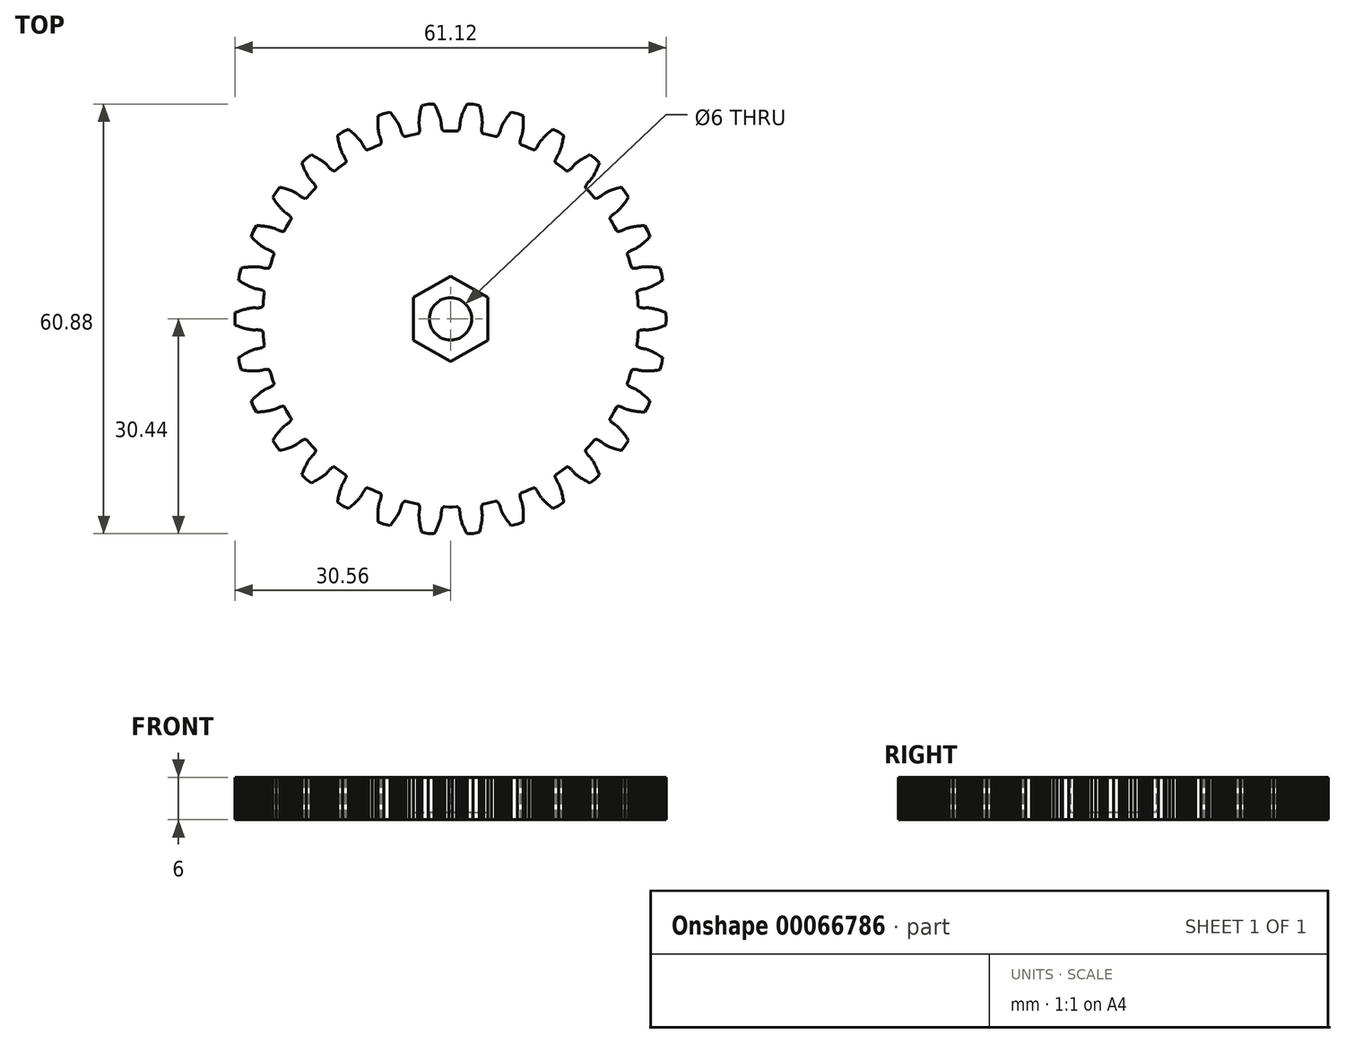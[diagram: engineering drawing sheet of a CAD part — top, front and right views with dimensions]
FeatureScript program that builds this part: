
annotation { "Feature Type Name" : "Feature", "Feature Type Description" : "" }
export const myFeature = defineFeature(function(context is Context, id is Id, definition is map)
    precondition{}
    {
        {
            var Q0;
            Q0=qCreatedBy(makeId("Top.planeOp"),FACE);
            var sketch = newSketch(context, id + "F0", { "sketchPlane" : qUnion([Q0])});
            skCircle(sketch, "E0", {"center": v(0, 0) * mm, "radius": 3 * mm});
            skLineSegment(sketch, "E1", {"start": v(29.66, -7.2) * mm, "end": v(29.89, -6.35) * mm});
            skLineSegment(sketch, "E2", {"start": v(29.89, -6.35) * mm, "end": v(30.03, -5.49) * mm});
            skLineSegment(sketch, "E3", {"start": v(30.03, -5.49) * mm, "end": v(29.86, -5.37) * mm});
            skLineSegment(sketch, "E4", {"start": v(29.86, -5.37) * mm, "end": v(29.65, -5.24) * mm});
            skLineSegment(sketch, "E5", {"start": v(29.65, -5.24) * mm, "end": v(29.45, -5.11) * mm});
            skLineSegment(sketch, "E6", {"start": v(29.45, -5.11) * mm, "end": v(29.26, -5) * mm});
            skLineSegment(sketch, "E7", {"start": v(29.26, -5) * mm, "end": v(29.07, -4.9) * mm});
            skLineSegment(sketch, "E8", {"start": v(29.07, -4.9) * mm, "end": v(28.9, -4.8) * mm});
            skLineSegment(sketch, "E9", {"start": v(28.9, -4.8) * mm, "end": v(28.73, -4.71) * mm});
            skLineSegment(sketch, "E10", {"start": v(28.73, -4.71) * mm, "end": v(28.57, -4.63) * mm});
            skLineSegment(sketch, "E11", {"start": v(28.57, -4.63) * mm, "end": v(28.42, -4.57) * mm});
            skLineSegment(sketch, "E12", {"start": v(28.42, -4.57) * mm, "end": v(28.29, -4.5) * mm});
            skLineSegment(sketch, "E13", {"start": v(28.29, -4.5) * mm, "end": v(28.16, -4.45) * mm});
            skLineSegment(sketch, "E14", {"start": v(28.16, -4.45) * mm, "end": v(28.04, -4.4) * mm});
            skLineSegment(sketch, "E15", {"start": v(28.04, -4.4) * mm, "end": v(27.93, -4.37) * mm});
            skLineSegment(sketch, "E16", {"start": v(27.93, -4.37) * mm, "end": v(27.83, -4.33) * mm});
            skLineSegment(sketch, "E17", {"start": v(27.83, -4.33) * mm, "end": v(27.75, -4.3) * mm});
            skLineSegment(sketch, "E18", {"start": v(27.75, -4.3) * mm, "end": v(27.67, -4.28) * mm});
            skLineSegment(sketch, "E19", {"start": v(27.67, -4.28) * mm, "end": v(27.6, -4.27) * mm});
            skLineSegment(sketch, "E20", {"start": v(27.6, -4.27) * mm, "end": v(27.56, -4.25) * mm});
            skLineSegment(sketch, "E21", {"start": v(27.56, -4.25) * mm, "end": v(27.52, -4.24) * mm});
            skLineSegment(sketch, "E22", {"start": v(27.52, -4.24) * mm, "end": v(27.49, -4.24) * mm});
            skLineSegment(sketch, "E23", {"start": v(27.49, -4.24) * mm, "end": v(27.47, -4.23) * mm});
            skLineSegment(sketch, "E24", {"start": v(27.47, -4.23) * mm, "end": v(27.47, -4.23) * mm});
            skLineSegment(sketch, "E25", {"start": v(27.47, -4.23) * mm, "end": v(27.38, -4.22) * mm});
            skLineSegment(sketch, "E26", {"start": v(27.38, -4.22) * mm, "end": v(27.23, -4.2) * mm});
            skLineSegment(sketch, "E27", {"start": v(27.23, -4.2) * mm, "end": v(27.08, -4.17) * mm});
            skLineSegment(sketch, "E28", {"start": v(27.08, -4.17) * mm, "end": v(26.95, -4.14) * mm});
            skLineSegment(sketch, "E29", {"start": v(26.95, -4.14) * mm, "end": v(26.83, -4.1) * mm});
            skLineSegment(sketch, "E30", {"start": v(26.83, -4.1) * mm, "end": v(26.73, -4.06) * mm});
            skLineSegment(sketch, "E31", {"start": v(26.73, -4.06) * mm, "end": v(26.64, -4.02) * mm});
            skLineSegment(sketch, "E32", {"start": v(26.64, -4.02) * mm, "end": v(26.56, -3.98) * mm});
            skLineSegment(sketch, "E33", {"start": v(26.56, -3.98) * mm, "end": v(26.5, -3.94) * mm});
            skLineSegment(sketch, "E34", {"start": v(26.5, -3.94) * mm, "end": v(26.45, -3.9) * mm});
            skLineSegment(sketch, "E35", {"start": v(26.45, -3.9) * mm, "end": v(26.4, -3.85) * mm});
            skLineSegment(sketch, "E36", {"start": v(26.4, -3.85) * mm, "end": v(26.39, -3.8) * mm});
            skLineSegment(sketch, "E37", {"start": v(26.39, -3.8) * mm, "end": v(26.38, -3.76) * mm});
            skLineSegment(sketch, "E38", {"start": v(26.38, -3.76) * mm, "end": v(26.38, -3.72) * mm});
            skLineSegment(sketch, "E39", {"start": v(26.38, -3.72) * mm, "end": v(26.4, -3.62) * mm});
            skLineSegment(sketch, "E40", {"start": v(26.4, -3.62) * mm, "end": v(26.46, -3.06) * mm});
            skLineSegment(sketch, "E41", {"start": v(26.46, -3.06) * mm, "end": v(26.52, -2.5) * mm});
            skLineSegment(sketch, "E42", {"start": v(26.52, -2.5) * mm, "end": v(26.57, -1.95) * mm});
            skLineSegment(sketch, "E43", {"start": v(26.57, -1.95) * mm, "end": v(26.57, -1.85) * mm});
            skLineSegment(sketch, "E44", {"start": v(26.57, -1.85) * mm, "end": v(26.58, -1.8) * mm});
            skLineSegment(sketch, "E45", {"start": v(26.58, -1.8) * mm, "end": v(26.6, -1.77) * mm});
            skLineSegment(sketch, "E46", {"start": v(26.6, -1.77) * mm, "end": v(26.63, -1.73) * mm});
            skLineSegment(sketch, "E47", {"start": v(26.63, -1.73) * mm, "end": v(26.68, -1.7) * mm});
            skLineSegment(sketch, "E48", {"start": v(26.68, -1.7) * mm, "end": v(26.74, -1.66) * mm});
            skLineSegment(sketch, "E49", {"start": v(26.74, -1.66) * mm, "end": v(26.8, -1.63) * mm});
            skLineSegment(sketch, "E50", {"start": v(26.8, -1.63) * mm, "end": v(26.9, -1.6) * mm});
            skLineSegment(sketch, "E51", {"start": v(26.9, -1.6) * mm, "end": v(26.99, -1.58) * mm});
            skLineSegment(sketch, "E52", {"start": v(26.99, -1.58) * mm, "end": v(27.1, -1.57) * mm});
            skLineSegment(sketch, "E53", {"start": v(27.1, -1.57) * mm, "end": v(27.22, -1.56) * mm});
            skLineSegment(sketch, "E54", {"start": v(27.22, -1.56) * mm, "end": v(27.36, -1.55) * mm});
            skLineSegment(sketch, "E55", {"start": v(27.36, -1.55) * mm, "end": v(27.5, -1.55) * mm});
            skLineSegment(sketch, "E56", {"start": v(27.5, -1.55) * mm, "end": v(27.66, -1.56) * mm});
            skLineSegment(sketch, "E57", {"start": v(27.66, -1.56) * mm, "end": v(27.75, -1.57) * mm});
            skLineSegment(sketch, "E58", {"start": v(27.75, -1.57) * mm, "end": v(27.75, -1.57) * mm});
            skLineSegment(sketch, "E59", {"start": v(27.75, -1.57) * mm, "end": v(27.77, -1.57) * mm});
            skLineSegment(sketch, "E60", {"start": v(27.77, -1.57) * mm, "end": v(27.8, -1.57) * mm});
            skLineSegment(sketch, "E61", {"start": v(27.8, -1.57) * mm, "end": v(27.84, -1.57) * mm});
            skLineSegment(sketch, "E62", {"start": v(27.84, -1.57) * mm, "end": v(27.9, -1.57) * mm});
            skLineSegment(sketch, "E63", {"start": v(27.9, -1.57) * mm, "end": v(27.96, -1.56) * mm});
            skLineSegment(sketch, "E64", {"start": v(27.96, -1.56) * mm, "end": v(28.04, -1.56) * mm});
            skLineSegment(sketch, "E65", {"start": v(28.04, -1.56) * mm, "end": v(28.13, -1.55) * mm});
            skLineSegment(sketch, "E66", {"start": v(28.13, -1.55) * mm, "end": v(28.23, -1.54) * mm});
            skLineSegment(sketch, "E67", {"start": v(28.23, -1.54) * mm, "end": v(28.34, -1.52) * mm});
            skLineSegment(sketch, "E68", {"start": v(28.34, -1.52) * mm, "end": v(28.47, -1.5) * mm});
            skLineSegment(sketch, "E69", {"start": v(28.47, -1.5) * mm, "end": v(28.6, -1.48) * mm});
            skLineSegment(sketch, "E70", {"start": v(28.6, -1.48) * mm, "end": v(28.75, -1.44) * mm});
            skLineSegment(sketch, "E71", {"start": v(28.75, -1.44) * mm, "end": v(28.91, -1.4) * mm});
            skLineSegment(sketch, "E72", {"start": v(28.91, -1.4) * mm, "end": v(29.08, -1.37) * mm});
            skLineSegment(sketch, "E73", {"start": v(29.08, -1.37) * mm, "end": v(29.26, -1.32) * mm});
            skLineSegment(sketch, "E74", {"start": v(29.26, -1.32) * mm, "end": v(29.46, -1.26) * mm});
            skLineSegment(sketch, "E75", {"start": v(29.46, -1.26) * mm, "end": v(29.66, -1.2) * mm});
            skLineSegment(sketch, "E76", {"start": v(29.66, -1.2) * mm, "end": v(29.87, -1.12) * mm});
            skLineSegment(sketch, "E77", {"start": v(29.87, -1.12) * mm, "end": v(30.1, -1.04) * mm});
            skLineSegment(sketch, "E78", {"start": v(30.1, -1.04) * mm, "end": v(30.32, -0.95) * mm});
            skLineSegment(sketch, "E79", {"start": v(30.32, -0.95) * mm, "end": v(30.51, -0.87) * mm});
            skLineSegment(sketch, "E80", {"start": v(30.51, -0.87) * mm, "end": v(30.56, 0) * mm});
            skLineSegment(sketch, "E81", {"start": v(30.56, 0) * mm, "end": v(30.51, 0.87) * mm});
            skLineSegment(sketch, "E82", {"start": v(30.51, 0.87) * mm, "end": v(30.32, 0.95) * mm});
            skLineSegment(sketch, "E83", {"start": v(30.32, 0.95) * mm, "end": v(30.1, 1.04) * mm});
            skLineSegment(sketch, "E84", {"start": v(30.1, 1.04) * mm, "end": v(29.87, 1.12) * mm});
            skLineSegment(sketch, "E85", {"start": v(29.87, 1.12) * mm, "end": v(29.66, 1.2) * mm});
            skLineSegment(sketch, "E86", {"start": v(29.66, 1.2) * mm, "end": v(29.46, 1.26) * mm});
            skLineSegment(sketch, "E87", {"start": v(29.46, 1.26) * mm, "end": v(29.26, 1.32) * mm});
            skLineSegment(sketch, "E88", {"start": v(29.26, 1.32) * mm, "end": v(29.08, 1.37) * mm});
            skLineSegment(sketch, "E89", {"start": v(29.08, 1.37) * mm, "end": v(28.91, 1.4) * mm});
            skLineSegment(sketch, "E90", {"start": v(28.91, 1.4) * mm, "end": v(28.75, 1.44) * mm});
            skLineSegment(sketch, "E91", {"start": v(28.75, 1.44) * mm, "end": v(28.6, 1.48) * mm});
            skLineSegment(sketch, "E92", {"start": v(28.6, 1.48) * mm, "end": v(28.47, 1.5) * mm});
            skLineSegment(sketch, "E93", {"start": v(28.47, 1.5) * mm, "end": v(28.34, 1.52) * mm});
            skLineSegment(sketch, "E94", {"start": v(28.34, 1.52) * mm, "end": v(28.23, 1.54) * mm});
            skLineSegment(sketch, "E95", {"start": v(28.23, 1.54) * mm, "end": v(28.13, 1.55) * mm});
            skLineSegment(sketch, "E96", {"start": v(28.13, 1.55) * mm, "end": v(28.04, 1.56) * mm});
            skLineSegment(sketch, "E97", {"start": v(28.04, 1.56) * mm, "end": v(27.96, 1.56) * mm});
            skLineSegment(sketch, "E98", {"start": v(27.96, 1.56) * mm, "end": v(27.9, 1.57) * mm});
            skLineSegment(sketch, "E99", {"start": v(27.9, 1.57) * mm, "end": v(27.84, 1.57) * mm});
            skLineSegment(sketch, "E100", {"start": v(27.84, 1.57) * mm, "end": v(27.8, 1.57) * mm});
            skLineSegment(sketch, "E101", {"start": v(27.8, 1.57) * mm, "end": v(27.77, 1.57) * mm});
            skLineSegment(sketch, "E102", {"start": v(27.77, 1.57) * mm, "end": v(27.75, 1.57) * mm});
            skLineSegment(sketch, "E103", {"start": v(27.75, 1.57) * mm, "end": v(27.75, 1.57) * mm});
            skLineSegment(sketch, "E104", {"start": v(27.75, 1.57) * mm, "end": v(27.66, 1.56) * mm});
            skLineSegment(sketch, "E105", {"start": v(27.66, 1.56) * mm, "end": v(27.5, 1.55) * mm});
            skLineSegment(sketch, "E106", {"start": v(27.5, 1.55) * mm, "end": v(27.36, 1.55) * mm});
            skLineSegment(sketch, "E107", {"start": v(27.36, 1.55) * mm, "end": v(27.22, 1.56) * mm});
            skLineSegment(sketch, "E108", {"start": v(27.22, 1.56) * mm, "end": v(27.1, 1.57) * mm});
            skLineSegment(sketch, "E109", {"start": v(27.1, 1.57) * mm, "end": v(26.99, 1.58) * mm});
            skLineSegment(sketch, "E110", {"start": v(26.99, 1.58) * mm, "end": v(26.9, 1.6) * mm});
            skLineSegment(sketch, "E111", {"start": v(26.9, 1.6) * mm, "end": v(26.8, 1.63) * mm});
            skLineSegment(sketch, "E112", {"start": v(26.8, 1.63) * mm, "end": v(26.74, 1.66) * mm});
            skLineSegment(sketch, "E113", {"start": v(26.74, 1.66) * mm, "end": v(26.68, 1.7) * mm});
            skLineSegment(sketch, "E114", {"start": v(26.68, 1.7) * mm, "end": v(26.63, 1.73) * mm});
            skLineSegment(sketch, "E115", {"start": v(26.63, 1.73) * mm, "end": v(26.6, 1.77) * mm});
            skLineSegment(sketch, "E116", {"start": v(26.6, 1.77) * mm, "end": v(26.58, 1.8) * mm});
            skLineSegment(sketch, "E117", {"start": v(26.58, 1.8) * mm, "end": v(26.57, 1.85) * mm});
            skLineSegment(sketch, "E118", {"start": v(26.57, 1.85) * mm, "end": v(26.57, 1.95) * mm});
            skLineSegment(sketch, "E119", {"start": v(26.57, 1.95) * mm, "end": v(26.52, 2.5) * mm});
            skLineSegment(sketch, "E120", {"start": v(26.52, 2.5) * mm, "end": v(26.46, 3.06) * mm});
            skLineSegment(sketch, "E121", {"start": v(26.46, 3.06) * mm, "end": v(26.4, 3.62) * mm});
            skLineSegment(sketch, "E122", {"start": v(26.4, 3.62) * mm, "end": v(26.38, 3.72) * mm});
            skLineSegment(sketch, "E123", {"start": v(26.38, 3.72) * mm, "end": v(26.38, 3.76) * mm});
            skLineSegment(sketch, "E124", {"start": v(26.38, 3.76) * mm, "end": v(26.39, 3.8) * mm});
            skLineSegment(sketch, "E125", {"start": v(26.39, 3.8) * mm, "end": v(26.4, 3.85) * mm});
            skLineSegment(sketch, "E126", {"start": v(26.4, 3.85) * mm, "end": v(26.45, 3.9) * mm});
            skLineSegment(sketch, "E127", {"start": v(26.45, 3.9) * mm, "end": v(26.5, 3.94) * mm});
            skLineSegment(sketch, "E128", {"start": v(26.5, 3.94) * mm, "end": v(26.56, 3.98) * mm});
            skLineSegment(sketch, "E129", {"start": v(26.56, 3.98) * mm, "end": v(26.64, 4.02) * mm});
            skLineSegment(sketch, "E130", {"start": v(26.64, 4.02) * mm, "end": v(26.73, 4.06) * mm});
            skLineSegment(sketch, "E131", {"start": v(26.73, 4.06) * mm, "end": v(26.83, 4.1) * mm});
            skLineSegment(sketch, "E132", {"start": v(26.83, 4.1) * mm, "end": v(26.95, 4.14) * mm});
            skLineSegment(sketch, "E133", {"start": v(26.95, 4.14) * mm, "end": v(27.08, 4.17) * mm});
            skLineSegment(sketch, "E134", {"start": v(27.08, 4.17) * mm, "end": v(27.23, 4.2) * mm});
            skLineSegment(sketch, "E135", {"start": v(27.23, 4.2) * mm, "end": v(27.38, 4.22) * mm});
            skLineSegment(sketch, "E136", {"start": v(27.38, 4.22) * mm, "end": v(27.47, 4.23) * mm});
            skLineSegment(sketch, "E137", {"start": v(27.47, 4.23) * mm, "end": v(27.47, 4.23) * mm});
            skLineSegment(sketch, "E138", {"start": v(27.47, 4.23) * mm, "end": v(27.49, 4.24) * mm});
            skLineSegment(sketch, "E139", {"start": v(27.49, 4.24) * mm, "end": v(27.52, 4.24) * mm});
            skLineSegment(sketch, "E140", {"start": v(27.52, 4.24) * mm, "end": v(27.56, 4.25) * mm});
            skLineSegment(sketch, "E141", {"start": v(27.56, 4.25) * mm, "end": v(27.6, 4.27) * mm});
            skLineSegment(sketch, "E142", {"start": v(27.6, 4.27) * mm, "end": v(27.67, 4.28) * mm});
            skLineSegment(sketch, "E143", {"start": v(27.67, 4.28) * mm, "end": v(27.75, 4.3) * mm});
            skLineSegment(sketch, "E144", {"start": v(27.75, 4.3) * mm, "end": v(27.83, 4.33) * mm});
            skLineSegment(sketch, "E145", {"start": v(27.83, 4.33) * mm, "end": v(27.93, 4.37) * mm});
            skLineSegment(sketch, "E146", {"start": v(27.93, 4.37) * mm, "end": v(28.04, 4.4) * mm});
            skLineSegment(sketch, "E147", {"start": v(28.04, 4.4) * mm, "end": v(28.16, 4.45) * mm});
            skLineSegment(sketch, "E148", {"start": v(28.16, 4.45) * mm, "end": v(28.29, 4.5) * mm});
            skLineSegment(sketch, "E149", {"start": v(28.29, 4.5) * mm, "end": v(28.42, 4.57) * mm});
            skLineSegment(sketch, "E150", {"start": v(28.42, 4.57) * mm, "end": v(28.57, 4.63) * mm});
            skLineSegment(sketch, "E151", {"start": v(28.57, 4.63) * mm, "end": v(28.73, 4.71) * mm});
            skLineSegment(sketch, "E152", {"start": v(28.73, 4.71) * mm, "end": v(28.9, 4.8) * mm});
            skLineSegment(sketch, "E153", {"start": v(28.9, 4.8) * mm, "end": v(29.07, 4.9) * mm});
            skLineSegment(sketch, "E154", {"start": v(29.07, 4.9) * mm, "end": v(29.26, 5) * mm});
            skLineSegment(sketch, "E155", {"start": v(29.26, 5) * mm, "end": v(29.45, 5.11) * mm});
            skLineSegment(sketch, "E156", {"start": v(29.45, 5.11) * mm, "end": v(29.65, 5.24) * mm});
            skLineSegment(sketch, "E157", {"start": v(29.65, 5.24) * mm, "end": v(29.86, 5.37) * mm});
            skLineSegment(sketch, "E158", {"start": v(29.86, 5.37) * mm, "end": v(30.03, 5.49) * mm});
            skLineSegment(sketch, "E159", {"start": v(30.03, 5.49) * mm, "end": v(29.89, 6.35) * mm});
            skLineSegment(sketch, "E160", {"start": v(29.89, 6.35) * mm, "end": v(29.66, 7.2) * mm});
            skLineSegment(sketch, "E161", {"start": v(29.66, 7.2) * mm, "end": v(29.46, 7.23) * mm});
            skLineSegment(sketch, "E162", {"start": v(29.46, 7.23) * mm, "end": v(29.22, 7.28) * mm});
            skLineSegment(sketch, "E163", {"start": v(29.22, 7.28) * mm, "end": v(28.98, 7.3) * mm});
            skLineSegment(sketch, "E164", {"start": v(28.98, 7.3) * mm, "end": v(28.76, 7.33) * mm});
            skLineSegment(sketch, "E165", {"start": v(28.76, 7.33) * mm, "end": v(28.55, 7.36) * mm});
            skLineSegment(sketch, "E166", {"start": v(28.55, 7.36) * mm, "end": v(28.35, 7.37) * mm});
            skLineSegment(sketch, "E167", {"start": v(28.35, 7.37) * mm, "end": v(28.16, 7.38) * mm});
            skLineSegment(sketch, "E168", {"start": v(28.16, 7.38) * mm, "end": v(27.99, 7.39) * mm});
            skLineSegment(sketch, "E169", {"start": v(27.99, 7.39) * mm, "end": v(27.82, 7.4) * mm});
            skLineSegment(sketch, "E170", {"start": v(27.82, 7.4) * mm, "end": v(27.67, 7.39) * mm});
            skLineSegment(sketch, "E171", {"start": v(27.67, 7.39) * mm, "end": v(27.53, 7.39) * mm});
            skLineSegment(sketch, "E172", {"start": v(27.53, 7.39) * mm, "end": v(27.4, 7.38) * mm});
            skLineSegment(sketch, "E173", {"start": v(27.4, 7.38) * mm, "end": v(27.3, 7.37) * mm});
            skLineSegment(sketch, "E174", {"start": v(27.3, 7.37) * mm, "end": v(27.2, 7.36) * mm});
            skLineSegment(sketch, "E175", {"start": v(27.2, 7.36) * mm, "end": v(27.1, 7.35) * mm});
            skLineSegment(sketch, "E176", {"start": v(27.1, 7.35) * mm, "end": v(27.02, 7.34) * mm});
            skLineSegment(sketch, "E177", {"start": v(27.02, 7.34) * mm, "end": v(26.96, 7.33) * mm});
            skLineSegment(sketch, "E178", {"start": v(26.96, 7.33) * mm, "end": v(26.9, 7.32) * mm});
            skLineSegment(sketch, "E179", {"start": v(26.9, 7.32) * mm, "end": v(26.86, 7.32) * mm});
            skLineSegment(sketch, "E180", {"start": v(26.86, 7.32) * mm, "end": v(26.84, 7.3) * mm});
            skLineSegment(sketch, "E181", {"start": v(26.84, 7.3) * mm, "end": v(26.82, 7.3) * mm});
            skLineSegment(sketch, "E182", {"start": v(26.82, 7.3) * mm, "end": v(26.82, 7.3) * mm});
            skLineSegment(sketch, "E183", {"start": v(26.82, 7.3) * mm, "end": v(26.73, 7.28) * mm});
            skLineSegment(sketch, "E184", {"start": v(26.73, 7.28) * mm, "end": v(26.58, 7.24) * mm});
            skLineSegment(sketch, "E185", {"start": v(26.58, 7.24) * mm, "end": v(26.44, 7.2) * mm});
            skLineSegment(sketch, "E186", {"start": v(26.44, 7.2) * mm, "end": v(26.3, 7.18) * mm});
            skLineSegment(sketch, "E187", {"start": v(26.3, 7.18) * mm, "end": v(26.18, 7.17) * mm});
            skLineSegment(sketch, "E188", {"start": v(26.18, 7.17) * mm, "end": v(26.07, 7.16) * mm});
            skLineSegment(sketch, "E189", {"start": v(26.07, 7.16) * mm, "end": v(25.97, 7.16) * mm});
            skLineSegment(sketch, "E190", {"start": v(25.97, 7.16) * mm, "end": v(25.88, 7.17) * mm});
            skLineSegment(sketch, "E191", {"start": v(25.88, 7.17) * mm, "end": v(25.8, 7.18) * mm});
            skLineSegment(sketch, "E192", {"start": v(25.8, 7.18) * mm, "end": v(25.74, 7.2) * mm});
            skLineSegment(sketch, "E193", {"start": v(25.74, 7.2) * mm, "end": v(25.69, 7.23) * mm});
            skLineSegment(sketch, "E194", {"start": v(25.69, 7.23) * mm, "end": v(25.65, 7.26) * mm});
            skLineSegment(sketch, "E195", {"start": v(25.65, 7.26) * mm, "end": v(25.62, 7.3) * mm});
            skLineSegment(sketch, "E196", {"start": v(25.62, 7.3) * mm, "end": v(25.6, 7.33) * mm});
            skLineSegment(sketch, "E197", {"start": v(25.6, 7.33) * mm, "end": v(25.58, 7.43) * mm});
            skLineSegment(sketch, "E198", {"start": v(25.58, 7.43) * mm, "end": v(25.42, 7.97) * mm});
            skLineSegment(sketch, "E199", {"start": v(25.42, 7.97) * mm, "end": v(25.25, 8.5) * mm});
            skLineSegment(sketch, "E200", {"start": v(25.25, 8.5) * mm, "end": v(25.06, 9.02) * mm});
            skLineSegment(sketch, "E201", {"start": v(25.06, 9.02) * mm, "end": v(25.03, 9.12) * mm});
            skLineSegment(sketch, "E202", {"start": v(25.03, 9.12) * mm, "end": v(25.02, 9.16) * mm});
            skLineSegment(sketch, "E203", {"start": v(25.02, 9.16) * mm, "end": v(25.02, 9.2) * mm});
            skLineSegment(sketch, "E204", {"start": v(25.02, 9.2) * mm, "end": v(25.03, 9.25) * mm});
            skLineSegment(sketch, "E205", {"start": v(25.03, 9.25) * mm, "end": v(25.06, 9.3) * mm});
            skLineSegment(sketch, "E206", {"start": v(25.06, 9.3) * mm, "end": v(25.1, 9.36) * mm});
            skLineSegment(sketch, "E207", {"start": v(25.1, 9.36) * mm, "end": v(25.15, 9.41) * mm});
            skLineSegment(sketch, "E208", {"start": v(25.15, 9.41) * mm, "end": v(25.22, 9.47) * mm});
            skLineSegment(sketch, "E209", {"start": v(25.22, 9.47) * mm, "end": v(25.3, 9.53) * mm});
            skLineSegment(sketch, "E210", {"start": v(25.3, 9.53) * mm, "end": v(25.4, 9.6) * mm});
            skLineSegment(sketch, "E211", {"start": v(25.4, 9.6) * mm, "end": v(25.5, 9.65) * mm});
            skLineSegment(sketch, "E212", {"start": v(25.5, 9.65) * mm, "end": v(25.62, 9.71) * mm});
            skLineSegment(sketch, "E213", {"start": v(25.62, 9.71) * mm, "end": v(25.76, 9.77) * mm});
            skLineSegment(sketch, "E214", {"start": v(25.76, 9.77) * mm, "end": v(25.9, 9.82) * mm});
            skLineSegment(sketch, "E215", {"start": v(25.9, 9.82) * mm, "end": v(25.99, 9.85) * mm});
            skLineSegment(sketch, "E216", {"start": v(25.99, 9.85) * mm, "end": v(26, 9.85) * mm});
            skLineSegment(sketch, "E217", {"start": v(26, 9.85) * mm, "end": v(26, 9.86) * mm});
            skLineSegment(sketch, "E218", {"start": v(26, 9.86) * mm, "end": v(26.03, 9.87) * mm});
            skLineSegment(sketch, "E219", {"start": v(26.03, 9.87) * mm, "end": v(26.07, 9.89) * mm});
            skLineSegment(sketch, "E220", {"start": v(26.07, 9.89) * mm, "end": v(26.12, 9.91) * mm});
            skLineSegment(sketch, "E221", {"start": v(26.12, 9.91) * mm, "end": v(26.18, 9.94) * mm});
            skLineSegment(sketch, "E222", {"start": v(26.18, 9.94) * mm, "end": v(26.25, 9.98) * mm});
            skLineSegment(sketch, "E223", {"start": v(26.25, 9.98) * mm, "end": v(26.33, 10.03) * mm});
            skLineSegment(sketch, "E224", {"start": v(26.33, 10.03) * mm, "end": v(26.41, 10.08) * mm});
            skLineSegment(sketch, "E225", {"start": v(26.41, 10.08) * mm, "end": v(26.51, 10.14) * mm});
            skLineSegment(sketch, "E226", {"start": v(26.51, 10.14) * mm, "end": v(26.62, 10.2) * mm});
            skLineSegment(sketch, "E227", {"start": v(26.62, 10.2) * mm, "end": v(26.73, 10.29) * mm});
            skLineSegment(sketch, "E228", {"start": v(26.73, 10.29) * mm, "end": v(26.85, 10.38) * mm});
            skLineSegment(sketch, "E229", {"start": v(26.85, 10.38) * mm, "end": v(26.99, 10.47) * mm});
            skLineSegment(sketch, "E230", {"start": v(26.99, 10.47) * mm, "end": v(27.12, 10.58) * mm});
            skLineSegment(sketch, "E231", {"start": v(27.12, 10.58) * mm, "end": v(27.27, 10.7) * mm});
            skLineSegment(sketch, "E232", {"start": v(27.27, 10.7) * mm, "end": v(27.42, 10.83) * mm});
            skLineSegment(sketch, "E233", {"start": v(27.42, 10.83) * mm, "end": v(27.58, 10.97) * mm});
            skLineSegment(sketch, "E234", {"start": v(27.58, 10.97) * mm, "end": v(27.74, 11.12) * mm});
            skLineSegment(sketch, "E235", {"start": v(27.74, 11.12) * mm, "end": v(27.91, 11.29) * mm});
            skLineSegment(sketch, "E236", {"start": v(27.91, 11.29) * mm, "end": v(28.09, 11.47) * mm});
            skLineSegment(sketch, "E237", {"start": v(28.09, 11.47) * mm, "end": v(28.23, 11.61) * mm});
            skLineSegment(sketch, "E238", {"start": v(28.23, 11.61) * mm, "end": v(27.92, 12.43) * mm});
            skLineSegment(sketch, "E239", {"start": v(27.92, 12.43) * mm, "end": v(27.52, 13.2) * mm});
            skLineSegment(sketch, "E240", {"start": v(27.52, 13.2) * mm, "end": v(27.32, 13.2) * mm});
            skLineSegment(sketch, "E241", {"start": v(27.32, 13.2) * mm, "end": v(27.07, 13.2) * mm});
            skLineSegment(sketch, "E242", {"start": v(27.07, 13.2) * mm, "end": v(26.83, 13.17) * mm});
            skLineSegment(sketch, "E243", {"start": v(26.83, 13.17) * mm, "end": v(26.6, 13.15) * mm});
            skLineSegment(sketch, "E244", {"start": v(26.6, 13.15) * mm, "end": v(26.4, 13.13) * mm});
            skLineSegment(sketch, "E245", {"start": v(26.4, 13.13) * mm, "end": v(26.2, 13.1) * mm});
            skLineSegment(sketch, "E246", {"start": v(26.2, 13.1) * mm, "end": v(26.01, 13.08) * mm});
            skLineSegment(sketch, "E247", {"start": v(26.01, 13.08) * mm, "end": v(25.84, 13.05) * mm});
            skLineSegment(sketch, "E248", {"start": v(25.84, 13.05) * mm, "end": v(25.68, 13.01) * mm});
            skLineSegment(sketch, "E249", {"start": v(25.68, 13.01) * mm, "end": v(25.53, 12.98) * mm});
            skLineSegment(sketch, "E250", {"start": v(25.53, 12.98) * mm, "end": v(25.4, 12.95) * mm});
            skLineSegment(sketch, "E251", {"start": v(25.4, 12.95) * mm, "end": v(25.27, 12.92) * mm});
            skLineSegment(sketch, "E252", {"start": v(25.27, 12.92) * mm, "end": v(25.16, 12.89) * mm});
            skLineSegment(sketch, "E253", {"start": v(25.16, 12.89) * mm, "end": v(25.07, 12.86) * mm});
            skLineSegment(sketch, "E254", {"start": v(25.07, 12.86) * mm, "end": v(24.98, 12.83) * mm});
            skLineSegment(sketch, "E255", {"start": v(24.98, 12.83) * mm, "end": v(24.9, 12.8) * mm});
            skLineSegment(sketch, "E256", {"start": v(24.9, 12.8) * mm, "end": v(24.84, 12.78) * mm});
            skLineSegment(sketch, "E257", {"start": v(24.84, 12.78) * mm, "end": v(24.8, 12.76) * mm});
            skLineSegment(sketch, "E258", {"start": v(24.8, 12.76) * mm, "end": v(24.76, 12.74) * mm});
            skLineSegment(sketch, "E259", {"start": v(24.76, 12.74) * mm, "end": v(24.73, 12.73) * mm});
            skLineSegment(sketch, "E260", {"start": v(24.73, 12.73) * mm, "end": v(24.71, 12.72) * mm});
            skLineSegment(sketch, "E261", {"start": v(24.71, 12.72) * mm, "end": v(24.71, 12.72) * mm});
            skLineSegment(sketch, "E262", {"start": v(24.71, 12.72) * mm, "end": v(24.64, 12.68) * mm});
            skLineSegment(sketch, "E263", {"start": v(24.64, 12.68) * mm, "end": v(24.5, 12.6) * mm});
            skLineSegment(sketch, "E264", {"start": v(24.5, 12.6) * mm, "end": v(24.36, 12.54) * mm});
            skLineSegment(sketch, "E265", {"start": v(24.36, 12.54) * mm, "end": v(24.24, 12.5) * mm});
            skLineSegment(sketch, "E266", {"start": v(24.24, 12.5) * mm, "end": v(24.12, 12.45) * mm});
            skLineSegment(sketch, "E267", {"start": v(24.12, 12.45) * mm, "end": v(24.01, 12.42) * mm});
            skLineSegment(sketch, "E268", {"start": v(24.01, 12.42) * mm, "end": v(23.92, 12.4) * mm});
            skLineSegment(sketch, "E269", {"start": v(23.92, 12.4) * mm, "end": v(23.83, 12.4) * mm});
            skLineSegment(sketch, "E270", {"start": v(23.83, 12.4) * mm, "end": v(23.75, 12.4) * mm});
            skLineSegment(sketch, "E271", {"start": v(23.75, 12.4) * mm, "end": v(23.68, 12.4) * mm});
            skLineSegment(sketch, "E272", {"start": v(23.68, 12.4) * mm, "end": v(23.63, 12.41) * mm});
            skLineSegment(sketch, "E273", {"start": v(23.63, 12.41) * mm, "end": v(23.58, 12.43) * mm});
            skLineSegment(sketch, "E274", {"start": v(23.58, 12.43) * mm, "end": v(23.55, 12.46) * mm});
            skLineSegment(sketch, "E275", {"start": v(23.55, 12.46) * mm, "end": v(23.52, 12.5) * mm});
            skLineSegment(sketch, "E276", {"start": v(23.52, 12.5) * mm, "end": v(23.48, 12.59) * mm});
            skLineSegment(sketch, "E277", {"start": v(23.48, 12.59) * mm, "end": v(23.2, 13.08) * mm});
            skLineSegment(sketch, "E278", {"start": v(23.2, 13.08) * mm, "end": v(22.93, 13.56) * mm});
            skLineSegment(sketch, "E279", {"start": v(22.93, 13.56) * mm, "end": v(22.64, 14.04) * mm});
            skLineSegment(sketch, "E280", {"start": v(22.64, 14.04) * mm, "end": v(22.59, 14.12) * mm});
            skLineSegment(sketch, "E281", {"start": v(22.59, 14.12) * mm, "end": v(22.57, 14.16) * mm});
            skLineSegment(sketch, "E282", {"start": v(22.57, 14.16) * mm, "end": v(22.56, 14.2) * mm});
            skLineSegment(sketch, "E283", {"start": v(22.56, 14.2) * mm, "end": v(22.56, 14.25) * mm});
            skLineSegment(sketch, "E284", {"start": v(22.56, 14.25) * mm, "end": v(22.58, 14.31) * mm});
            skLineSegment(sketch, "E285", {"start": v(22.58, 14.31) * mm, "end": v(22.6, 14.37) * mm});
            skLineSegment(sketch, "E286", {"start": v(22.6, 14.37) * mm, "end": v(22.65, 14.44) * mm});
            skLineSegment(sketch, "E287", {"start": v(22.65, 14.44) * mm, "end": v(22.7, 14.5) * mm});
            skLineSegment(sketch, "E288", {"start": v(22.7, 14.5) * mm, "end": v(22.77, 14.58) * mm});
            skLineSegment(sketch, "E289", {"start": v(22.77, 14.58) * mm, "end": v(22.84, 14.66) * mm});
            skLineSegment(sketch, "E290", {"start": v(22.84, 14.66) * mm, "end": v(22.94, 14.74) * mm});
            skLineSegment(sketch, "E291", {"start": v(22.94, 14.74) * mm, "end": v(23.04, 14.83) * mm});
            skLineSegment(sketch, "E292", {"start": v(23.04, 14.83) * mm, "end": v(23.16, 14.91) * mm});
            skLineSegment(sketch, "E293", {"start": v(23.16, 14.91) * mm, "end": v(23.3, 15) * mm});
            skLineSegment(sketch, "E294", {"start": v(23.3, 15) * mm, "end": v(23.37, 15.04) * mm});
            skLineSegment(sketch, "E295", {"start": v(23.37, 15.04) * mm, "end": v(23.37, 15.04) * mm});
            skLineSegment(sketch, "E296", {"start": v(23.37, 15.04) * mm, "end": v(23.39, 15.05) * mm});
            skLineSegment(sketch, "E297", {"start": v(23.39, 15.05) * mm, "end": v(23.41, 15.07) * mm});
            skLineSegment(sketch, "E298", {"start": v(23.41, 15.07) * mm, "end": v(23.45, 15.1) * mm});
            skLineSegment(sketch, "E299", {"start": v(23.45, 15.1) * mm, "end": v(23.49, 15.13) * mm});
            skLineSegment(sketch, "E300", {"start": v(23.49, 15.13) * mm, "end": v(23.54, 15.17) * mm});
            skLineSegment(sketch, "E301", {"start": v(23.54, 15.17) * mm, "end": v(23.6, 15.22) * mm});
            skLineSegment(sketch, "E302", {"start": v(23.6, 15.22) * mm, "end": v(23.67, 15.28) * mm});
            skLineSegment(sketch, "E303", {"start": v(23.67, 15.28) * mm, "end": v(23.74, 15.35) * mm});
            skLineSegment(sketch, "E304", {"start": v(23.74, 15.35) * mm, "end": v(23.82, 15.43) * mm});
            skLineSegment(sketch, "E305", {"start": v(23.82, 15.43) * mm, "end": v(23.91, 15.52) * mm});
            skLineSegment(sketch, "E306", {"start": v(23.91, 15.52) * mm, "end": v(24, 15.62) * mm});
            skLineSegment(sketch, "E307", {"start": v(24, 15.62) * mm, "end": v(24.11, 15.73) * mm});
            skLineSegment(sketch, "E308", {"start": v(24.11, 15.73) * mm, "end": v(24.22, 15.85) * mm});
            skLineSegment(sketch, "E309", {"start": v(24.22, 15.85) * mm, "end": v(24.33, 15.99) * mm});
            skLineSegment(sketch, "E310", {"start": v(24.33, 15.99) * mm, "end": v(24.45, 16.14) * mm});
            skLineSegment(sketch, "E311", {"start": v(24.45, 16.14) * mm, "end": v(24.57, 16.3) * mm});
            skLineSegment(sketch, "E312", {"start": v(24.57, 16.3) * mm, "end": v(24.7, 16.47) * mm});
            skLineSegment(sketch, "E313", {"start": v(24.7, 16.47) * mm, "end": v(24.83, 16.65) * mm});
            skLineSegment(sketch, "E314", {"start": v(24.83, 16.65) * mm, "end": v(24.96, 16.85) * mm});
            skLineSegment(sketch, "E315", {"start": v(24.96, 16.85) * mm, "end": v(25.1, 17.05) * mm});
            skLineSegment(sketch, "E316", {"start": v(25.1, 17.05) * mm, "end": v(25.2, 17.23) * mm});
            skLineSegment(sketch, "E317", {"start": v(25.2, 17.23) * mm, "end": v(24.72, 17.96) * mm});
            skLineSegment(sketch, "E318", {"start": v(24.72, 17.96) * mm, "end": v(24.17, 18.64) * mm});
            skLineSegment(sketch, "E319", {"start": v(24.17, 18.64) * mm, "end": v(23.97, 18.6) * mm});
            skLineSegment(sketch, "E320", {"start": v(23.97, 18.6) * mm, "end": v(23.73, 18.53) * mm});
            skLineSegment(sketch, "E321", {"start": v(23.73, 18.53) * mm, "end": v(23.5, 18.47) * mm});
            skLineSegment(sketch, "E322", {"start": v(23.5, 18.47) * mm, "end": v(23.3, 18.4) * mm});
            skLineSegment(sketch, "E323", {"start": v(23.3, 18.4) * mm, "end": v(23.09, 18.33) * mm});
            skLineSegment(sketch, "E324", {"start": v(23.09, 18.33) * mm, "end": v(22.9, 18.27) * mm});
            skLineSegment(sketch, "E325", {"start": v(22.9, 18.27) * mm, "end": v(22.73, 18.2) * mm});
            skLineSegment(sketch, "E326", {"start": v(22.73, 18.2) * mm, "end": v(22.56, 18.13) * mm});
            skLineSegment(sketch, "E327", {"start": v(22.56, 18.13) * mm, "end": v(22.41, 18.07) * mm});
            skLineSegment(sketch, "E328", {"start": v(22.41, 18.07) * mm, "end": v(22.27, 18) * mm});
            skLineSegment(sketch, "E329", {"start": v(22.27, 18) * mm, "end": v(22.15, 17.95) * mm});
            skLineSegment(sketch, "E330", {"start": v(22.15, 17.95) * mm, "end": v(22.04, 17.89) * mm});
            skLineSegment(sketch, "E331", {"start": v(22.04, 17.89) * mm, "end": v(21.93, 17.84) * mm});
            skLineSegment(sketch, "E332", {"start": v(21.93, 17.84) * mm, "end": v(21.84, 17.79) * mm});
            skLineSegment(sketch, "E333", {"start": v(21.84, 17.79) * mm, "end": v(21.77, 17.74) * mm});
            skLineSegment(sketch, "E334", {"start": v(21.77, 17.74) * mm, "end": v(21.7, 17.7) * mm});
            skLineSegment(sketch, "E335", {"start": v(21.7, 17.7) * mm, "end": v(21.64, 17.66) * mm});
            skLineSegment(sketch, "E336", {"start": v(21.64, 17.66) * mm, "end": v(21.6, 17.63) * mm});
            skLineSegment(sketch, "E337", {"start": v(21.6, 17.63) * mm, "end": v(21.57, 17.6) * mm});
            skLineSegment(sketch, "E338", {"start": v(21.57, 17.6) * mm, "end": v(21.54, 17.6) * mm});
            skLineSegment(sketch, "E339", {"start": v(21.54, 17.6) * mm, "end": v(21.53, 17.58) * mm});
            skLineSegment(sketch, "E340", {"start": v(21.53, 17.58) * mm, "end": v(21.53, 17.58) * mm});
            skLineSegment(sketch, "E341", {"start": v(21.53, 17.58) * mm, "end": v(21.46, 17.52) * mm});
            skLineSegment(sketch, "E342", {"start": v(21.46, 17.52) * mm, "end": v(21.34, 17.42) * mm});
            skLineSegment(sketch, "E343", {"start": v(21.34, 17.42) * mm, "end": v(21.22, 17.33) * mm});
            skLineSegment(sketch, "E344", {"start": v(21.22, 17.33) * mm, "end": v(21.1, 17.26) * mm});
            skLineSegment(sketch, "E345", {"start": v(21.1, 17.26) * mm, "end": v(21, 17.2) * mm});
            skLineSegment(sketch, "E346", {"start": v(21, 17.2) * mm, "end": v(20.9, 17.14) * mm});
            skLineSegment(sketch, "E347", {"start": v(20.9, 17.14) * mm, "end": v(20.81, 17.1) * mm});
            skLineSegment(sketch, "E348", {"start": v(20.81, 17.1) * mm, "end": v(20.73, 17.08) * mm});
            skLineSegment(sketch, "E349", {"start": v(20.73, 17.08) * mm, "end": v(20.65, 17.06) * mm});
            skLineSegment(sketch, "E350", {"start": v(20.65, 17.06) * mm, "end": v(20.59, 17.05) * mm});
            skLineSegment(sketch, "E351", {"start": v(20.59, 17.05) * mm, "end": v(20.53, 17.05) * mm});
            skLineSegment(sketch, "E352", {"start": v(20.53, 17.05) * mm, "end": v(20.48, 17.06) * mm});
            skLineSegment(sketch, "E353", {"start": v(20.48, 17.06) * mm, "end": v(20.44, 17.09) * mm});
            skLineSegment(sketch, "E354", {"start": v(20.44, 17.09) * mm, "end": v(20.41, 17.12) * mm});
            skLineSegment(sketch, "E355", {"start": v(20.41, 17.12) * mm, "end": v(20.35, 17.2) * mm});
            skLineSegment(sketch, "E356", {"start": v(20.35, 17.2) * mm, "end": v(19.98, 17.62) * mm});
            skLineSegment(sketch, "E357", {"start": v(19.98, 17.62) * mm, "end": v(19.6, 18.03) * mm});
            skLineSegment(sketch, "E358", {"start": v(19.6, 18.03) * mm, "end": v(19.23, 18.44) * mm});
            skLineSegment(sketch, "E359", {"start": v(19.23, 18.44) * mm, "end": v(19.16, 18.51) * mm});
            skLineSegment(sketch, "E360", {"start": v(19.16, 18.51) * mm, "end": v(19.13, 18.54) * mm});
            skLineSegment(sketch, "E361", {"start": v(19.13, 18.54) * mm, "end": v(19.11, 18.58) * mm});
            skLineSegment(sketch, "E362", {"start": v(19.11, 18.58) * mm, "end": v(19.1, 18.63) * mm});
            skLineSegment(sketch, "E363", {"start": v(19.1, 18.63) * mm, "end": v(19.1, 18.7) * mm});
            skLineSegment(sketch, "E364", {"start": v(19.1, 18.7) * mm, "end": v(19.12, 18.76) * mm});
            skLineSegment(sketch, "E365", {"start": v(19.12, 18.76) * mm, "end": v(19.15, 18.83) * mm});
            skLineSegment(sketch, "E366", {"start": v(19.15, 18.83) * mm, "end": v(19.19, 18.91) * mm});
            skLineSegment(sketch, "E367", {"start": v(19.19, 18.91) * mm, "end": v(19.24, 19) * mm});
            skLineSegment(sketch, "E368", {"start": v(19.24, 19) * mm, "end": v(19.3, 19.1) * mm});
            skLineSegment(sketch, "E369", {"start": v(19.3, 19.1) * mm, "end": v(19.37, 19.19) * mm});
            skLineSegment(sketch, "E370", {"start": v(19.37, 19.19) * mm, "end": v(19.46, 19.3) * mm});
            skLineSegment(sketch, "E371", {"start": v(19.46, 19.3) * mm, "end": v(19.56, 19.4) * mm});
            skLineSegment(sketch, "E372", {"start": v(19.56, 19.4) * mm, "end": v(19.67, 19.51) * mm});
            skLineSegment(sketch, "E373", {"start": v(19.67, 19.51) * mm, "end": v(19.73, 19.57) * mm});
            skLineSegment(sketch, "E374", {"start": v(19.73, 19.57) * mm, "end": v(19.74, 19.57) * mm});
            skLineSegment(sketch, "E375", {"start": v(19.74, 19.57) * mm, "end": v(19.75, 19.59) * mm});
            skLineSegment(sketch, "E376", {"start": v(19.75, 19.59) * mm, "end": v(19.77, 19.6) * mm});
            skLineSegment(sketch, "E377", {"start": v(19.77, 19.6) * mm, "end": v(19.8, 19.64) * mm});
            skLineSegment(sketch, "E378", {"start": v(19.8, 19.64) * mm, "end": v(19.83, 19.68) * mm});
            skLineSegment(sketch, "E379", {"start": v(19.83, 19.68) * mm, "end": v(19.87, 19.73) * mm});
            skLineSegment(sketch, "E380", {"start": v(19.87, 19.73) * mm, "end": v(19.92, 19.8) * mm});
            skLineSegment(sketch, "E381", {"start": v(19.92, 19.8) * mm, "end": v(19.97, 19.87) * mm});
            skLineSegment(sketch, "E382", {"start": v(19.97, 19.87) * mm, "end": v(20.03, 19.95) * mm});
            skLineSegment(sketch, "E383", {"start": v(20.03, 19.95) * mm, "end": v(20.1, 20.04) * mm});
            skLineSegment(sketch, "E384", {"start": v(20.1, 20.04) * mm, "end": v(20.16, 20.15) * mm});
            skLineSegment(sketch, "E385", {"start": v(20.16, 20.15) * mm, "end": v(20.24, 20.27) * mm});
            skLineSegment(sketch, "E386", {"start": v(20.24, 20.27) * mm, "end": v(20.31, 20.4) * mm});
            skLineSegment(sketch, "E387", {"start": v(20.31, 20.4) * mm, "end": v(20.4, 20.54) * mm});
            skLineSegment(sketch, "E388", {"start": v(20.4, 20.54) * mm, "end": v(20.47, 20.7) * mm});
            skLineSegment(sketch, "E389", {"start": v(20.47, 20.7) * mm, "end": v(20.56, 20.87) * mm});
            skLineSegment(sketch, "E390", {"start": v(20.56, 20.87) * mm, "end": v(20.65, 21.05) * mm});
            skLineSegment(sketch, "E391", {"start": v(20.65, 21.05) * mm, "end": v(20.73, 21.24) * mm});
            skLineSegment(sketch, "E392", {"start": v(20.73, 21.24) * mm, "end": v(20.82, 21.45) * mm});
            skLineSegment(sketch, "E393", {"start": v(20.82, 21.45) * mm, "end": v(20.9, 21.67) * mm});
            skLineSegment(sketch, "E394", {"start": v(20.9, 21.67) * mm, "end": v(21, 21.9) * mm});
            skLineSegment(sketch, "E395", {"start": v(21, 21.9) * mm, "end": v(21.07, 22.1) * mm});
            skLineSegment(sketch, "E396", {"start": v(21.07, 22.1) * mm, "end": v(20.45, 22.7) * mm});
            skLineSegment(sketch, "E397", {"start": v(20.45, 22.7) * mm, "end": v(19.77, 23.26) * mm});
            skLineSegment(sketch, "E398", {"start": v(19.77, 23.26) * mm, "end": v(19.58, 23.17) * mm});
            skLineSegment(sketch, "E399", {"start": v(19.58, 23.17) * mm, "end": v(19.36, 23.06) * mm});
            skLineSegment(sketch, "E400", {"start": v(19.36, 23.06) * mm, "end": v(19.15, 22.95) * mm});
            skLineSegment(sketch, "E401", {"start": v(19.15, 22.95) * mm, "end": v(18.96, 22.84) * mm});
            skLineSegment(sketch, "E402", {"start": v(18.96, 22.84) * mm, "end": v(18.77, 22.73) * mm});
            skLineSegment(sketch, "E403", {"start": v(18.77, 22.73) * mm, "end": v(18.6, 22.63) * mm});
            skLineSegment(sketch, "E404", {"start": v(18.6, 22.63) * mm, "end": v(18.45, 22.53) * mm});
            skLineSegment(sketch, "E405", {"start": v(18.45, 22.53) * mm, "end": v(18.3, 22.43) * mm});
            skLineSegment(sketch, "E406", {"start": v(18.3, 22.43) * mm, "end": v(18.17, 22.33) * mm});
            skLineSegment(sketch, "E407", {"start": v(18.17, 22.33) * mm, "end": v(18.04, 22.24) * mm});
            skLineSegment(sketch, "E408", {"start": v(18.04, 22.24) * mm, "end": v(17.93, 22.16) * mm});
            skLineSegment(sketch, "E409", {"start": v(17.93, 22.16) * mm, "end": v(17.83, 22.08) * mm});
            skLineSegment(sketch, "E410", {"start": v(17.83, 22.08) * mm, "end": v(17.75, 22) * mm});
            skLineSegment(sketch, "E411", {"start": v(17.75, 22) * mm, "end": v(17.67, 21.94) * mm});
            skLineSegment(sketch, "E412", {"start": v(17.67, 21.94) * mm, "end": v(17.6, 21.88) * mm});
            skLineSegment(sketch, "E413", {"start": v(17.6, 21.88) * mm, "end": v(17.55, 21.82) * mm});
            skLineSegment(sketch, "E414", {"start": v(17.55, 21.82) * mm, "end": v(17.5, 21.78) * mm});
            skLineSegment(sketch, "E415", {"start": v(17.5, 21.78) * mm, "end": v(17.46, 21.74) * mm});
            skLineSegment(sketch, "E416", {"start": v(17.46, 21.74) * mm, "end": v(17.43, 21.7) * mm});
            skLineSegment(sketch, "E417", {"start": v(17.43, 21.7) * mm, "end": v(17.41, 21.69) * mm});
            skLineSegment(sketch, "E418", {"start": v(17.41, 21.69) * mm, "end": v(17.4, 21.67) * mm});
            skLineSegment(sketch, "E419", {"start": v(17.4, 21.67) * mm, "end": v(17.4, 21.67) * mm});
            skLineSegment(sketch, "E420", {"start": v(17.4, 21.67) * mm, "end": v(17.35, 21.6) * mm});
            skLineSegment(sketch, "E421", {"start": v(17.35, 21.6) * mm, "end": v(17.25, 21.48) * mm});
            skLineSegment(sketch, "E422", {"start": v(17.25, 21.48) * mm, "end": v(17.15, 21.37) * mm});
            skLineSegment(sketch, "E423", {"start": v(17.15, 21.37) * mm, "end": v(17.06, 21.27) * mm});
            skLineSegment(sketch, "E424", {"start": v(17.06, 21.27) * mm, "end": v(16.97, 21.19) * mm});
            skLineSegment(sketch, "E425", {"start": v(16.97, 21.19) * mm, "end": v(16.88, 21.12) * mm});
            skLineSegment(sketch, "E426", {"start": v(16.88, 21.12) * mm, "end": v(16.8, 21.06) * mm});
            skLineSegment(sketch, "E427", {"start": v(16.8, 21.06) * mm, "end": v(16.73, 21.01) * mm});
            skLineSegment(sketch, "E428", {"start": v(16.73, 21.01) * mm, "end": v(16.66, 20.98) * mm});
            skLineSegment(sketch, "E429", {"start": v(16.66, 20.98) * mm, "end": v(16.6, 20.96) * mm});
            skLineSegment(sketch, "E430", {"start": v(16.6, 20.96) * mm, "end": v(16.54, 20.95) * mm});
            skLineSegment(sketch, "E431", {"start": v(16.54, 20.95) * mm, "end": v(16.48, 20.95) * mm});
            skLineSegment(sketch, "E432", {"start": v(16.48, 20.95) * mm, "end": v(16.44, 20.96) * mm});
            skLineSegment(sketch, "E433", {"start": v(16.44, 20.96) * mm, "end": v(16.4, 20.99) * mm});
            skLineSegment(sketch, "E434", {"start": v(16.4, 20.99) * mm, "end": v(16.33, 21.05) * mm});
            skLineSegment(sketch, "E435", {"start": v(16.33, 21.05) * mm, "end": v(15.88, 21.39) * mm});
            skLineSegment(sketch, "E436", {"start": v(15.88, 21.39) * mm, "end": v(15.43, 21.71) * mm});
            skLineSegment(sketch, "E437", {"start": v(15.43, 21.71) * mm, "end": v(14.97, 22.03) * mm});
            skLineSegment(sketch, "E438", {"start": v(14.97, 22.03) * mm, "end": v(14.89, 22.09) * mm});
            skLineSegment(sketch, "E439", {"start": v(14.89, 22.09) * mm, "end": v(14.86, 22.11) * mm});
            skLineSegment(sketch, "E440", {"start": v(14.86, 22.11) * mm, "end": v(14.83, 22.15) * mm});
            skLineSegment(sketch, "E441", {"start": v(14.83, 22.15) * mm, "end": v(14.81, 22.2) * mm});
            skLineSegment(sketch, "E442", {"start": v(14.81, 22.2) * mm, "end": v(14.8, 22.26) * mm});
            skLineSegment(sketch, "E443", {"start": v(14.8, 22.26) * mm, "end": v(14.8, 22.32) * mm});
            skLineSegment(sketch, "E444", {"start": v(14.8, 22.32) * mm, "end": v(14.81, 22.4) * mm});
            skLineSegment(sketch, "E445", {"start": v(14.81, 22.4) * mm, "end": v(14.83, 22.49) * mm});
            skLineSegment(sketch, "E446", {"start": v(14.83, 22.49) * mm, "end": v(14.87, 22.58) * mm});
            skLineSegment(sketch, "E447", {"start": v(14.87, 22.58) * mm, "end": v(14.9, 22.69) * mm});
            skLineSegment(sketch, "E448", {"start": v(14.9, 22.69) * mm, "end": v(14.96, 22.8) * mm});
            skLineSegment(sketch, "E449", {"start": v(14.96, 22.8) * mm, "end": v(15.02, 22.92) * mm});
            skLineSegment(sketch, "E450", {"start": v(15.02, 22.92) * mm, "end": v(15.1, 23.04) * mm});
            skLineSegment(sketch, "E451", {"start": v(15.1, 23.04) * mm, "end": v(15.18, 23.18) * mm});
            skLineSegment(sketch, "E452", {"start": v(15.18, 23.18) * mm, "end": v(15.23, 23.25) * mm});
            skLineSegment(sketch, "E453", {"start": v(15.23, 23.25) * mm, "end": v(15.23, 23.25) * mm});
            skLineSegment(sketch, "E454", {"start": v(15.23, 23.25) * mm, "end": v(15.24, 23.26) * mm});
            skLineSegment(sketch, "E455", {"start": v(15.24, 23.26) * mm, "end": v(15.26, 23.29) * mm});
            skLineSegment(sketch, "E456", {"start": v(15.26, 23.29) * mm, "end": v(15.28, 23.32) * mm});
            skLineSegment(sketch, "E457", {"start": v(15.28, 23.32) * mm, "end": v(15.3, 23.37) * mm});
            skLineSegment(sketch, "E458", {"start": v(15.3, 23.37) * mm, "end": v(15.33, 23.43) * mm});
            skLineSegment(sketch, "E459", {"start": v(15.33, 23.43) * mm, "end": v(15.37, 23.5) * mm});
            skLineSegment(sketch, "E460", {"start": v(15.37, 23.5) * mm, "end": v(15.4, 23.58) * mm});
            skLineSegment(sketch, "E461", {"start": v(15.4, 23.58) * mm, "end": v(15.45, 23.68) * mm});
            skLineSegment(sketch, "E462", {"start": v(15.45, 23.68) * mm, "end": v(15.49, 23.78) * mm});
            skLineSegment(sketch, "E463", {"start": v(15.49, 23.78) * mm, "end": v(15.53, 23.9) * mm});
            skLineSegment(sketch, "E464", {"start": v(15.53, 23.9) * mm, "end": v(15.58, 24.03) * mm});
            skLineSegment(sketch, "E465", {"start": v(15.58, 24.03) * mm, "end": v(15.63, 24.18) * mm});
            skLineSegment(sketch, "E466", {"start": v(15.63, 24.18) * mm, "end": v(15.68, 24.33) * mm});
            skLineSegment(sketch, "E467", {"start": v(15.68, 24.33) * mm, "end": v(15.72, 24.5) * mm});
            skLineSegment(sketch, "E468", {"start": v(15.72, 24.5) * mm, "end": v(15.77, 24.69) * mm});
            skLineSegment(sketch, "E469", {"start": v(15.77, 24.69) * mm, "end": v(15.82, 24.88) * mm});
            skLineSegment(sketch, "E470", {"start": v(15.82, 24.88) * mm, "end": v(15.86, 25.09) * mm});
            skLineSegment(sketch, "E471", {"start": v(15.86, 25.09) * mm, "end": v(15.9, 25.3) * mm});
            skLineSegment(sketch, "E472", {"start": v(15.9, 25.3) * mm, "end": v(15.95, 25.54) * mm});
            skLineSegment(sketch, "E473", {"start": v(15.95, 25.54) * mm, "end": v(15.99, 25.79) * mm});
            skLineSegment(sketch, "E474", {"start": v(15.99, 25.79) * mm, "end": v(16.01, 25.99) * mm});
            skLineSegment(sketch, "E475", {"start": v(16.01, 25.99) * mm, "end": v(15.28, 26.46) * mm});
            skLineSegment(sketch, "E476", {"start": v(15.28, 26.46) * mm, "end": v(14.5, 26.86) * mm});
            skLineSegment(sketch, "E477", {"start": v(14.5, 26.86) * mm, "end": v(14.34, 26.74) * mm});
            skLineSegment(sketch, "E478", {"start": v(14.34, 26.74) * mm, "end": v(14.14, 26.58) * mm});
            skLineSegment(sketch, "E479", {"start": v(14.14, 26.58) * mm, "end": v(13.96, 26.43) * mm});
            skLineSegment(sketch, "E480", {"start": v(13.96, 26.43) * mm, "end": v(13.8, 26.28) * mm});
            skLineSegment(sketch, "E481", {"start": v(13.8, 26.28) * mm, "end": v(13.64, 26.14) * mm});
            skLineSegment(sketch, "E482", {"start": v(13.64, 26.14) * mm, "end": v(13.5, 26) * mm});
            skLineSegment(sketch, "E483", {"start": v(13.5, 26) * mm, "end": v(13.36, 25.87) * mm});
            skLineSegment(sketch, "E484", {"start": v(13.36, 25.87) * mm, "end": v(13.24, 25.74) * mm});
            skLineSegment(sketch, "E485", {"start": v(13.24, 25.74) * mm, "end": v(13.13, 25.62) * mm});
            skLineSegment(sketch, "E486", {"start": v(13.13, 25.62) * mm, "end": v(13.02, 25.5) * mm});
            skLineSegment(sketch, "E487", {"start": v(13.02, 25.5) * mm, "end": v(12.93, 25.4) * mm});
            skLineSegment(sketch, "E488", {"start": v(12.93, 25.4) * mm, "end": v(12.85, 25.3) * mm});
            skLineSegment(sketch, "E489", {"start": v(12.85, 25.3) * mm, "end": v(12.78, 25.22) * mm});
            skLineSegment(sketch, "E490", {"start": v(12.78, 25.22) * mm, "end": v(12.72, 25.13) * mm});
            skLineSegment(sketch, "E491", {"start": v(12.72, 25.13) * mm, "end": v(12.67, 25.06) * mm});
            skLineSegment(sketch, "E492", {"start": v(12.67, 25.06) * mm, "end": v(12.63, 25) * mm});
            skLineSegment(sketch, "E493", {"start": v(12.63, 25) * mm, "end": v(12.59, 24.94) * mm});
            skLineSegment(sketch, "E494", {"start": v(12.59, 24.94) * mm, "end": v(12.56, 24.9) * mm});
            skLineSegment(sketch, "E495", {"start": v(12.56, 24.9) * mm, "end": v(12.54, 24.86) * mm});
            skLineSegment(sketch, "E496", {"start": v(12.54, 24.86) * mm, "end": v(12.52, 24.83) * mm});
            skLineSegment(sketch, "E497", {"start": v(12.52, 24.83) * mm, "end": v(12.52, 24.82) * mm});
            skLineSegment(sketch, "E498", {"start": v(12.52, 24.82) * mm, "end": v(12.52, 24.82) * mm});
            skLineSegment(sketch, "E499", {"start": v(12.52, 24.82) * mm, "end": v(12.48, 24.74) * mm});
            skLineSegment(sketch, "E500", {"start": v(12.48, 24.74) * mm, "end": v(12.4, 24.6) * mm});
            skLineSegment(sketch, "E501", {"start": v(12.4, 24.6) * mm, "end": v(12.34, 24.47) * mm});
            skLineSegment(sketch, "E502", {"start": v(12.34, 24.47) * mm, "end": v(12.26, 24.35) * mm});
            skLineSegment(sketch, "E503", {"start": v(12.26, 24.35) * mm, "end": v(12.2, 24.25) * mm});
            skLineSegment(sketch, "E504", {"start": v(12.2, 24.25) * mm, "end": v(12.12, 24.17) * mm});
            skLineSegment(sketch, "E505", {"start": v(12.12, 24.17) * mm, "end": v(12.06, 24.1) * mm});
            skLineSegment(sketch, "E506", {"start": v(12.06, 24.1) * mm, "end": v(12, 24.03) * mm});
            skLineSegment(sketch, "E507", {"start": v(12, 24.03) * mm, "end": v(11.93, 23.98) * mm});
            skLineSegment(sketch, "E508", {"start": v(11.93, 23.98) * mm, "end": v(11.87, 23.95) * mm});
            skLineSegment(sketch, "E509", {"start": v(11.87, 23.95) * mm, "end": v(11.82, 23.93) * mm});
            skLineSegment(sketch, "E510", {"start": v(11.82, 23.93) * mm, "end": v(11.77, 23.92) * mm});
            skLineSegment(sketch, "E511", {"start": v(11.77, 23.92) * mm, "end": v(11.72, 23.92) * mm});
            skLineSegment(sketch, "E512", {"start": v(11.72, 23.92) * mm, "end": v(11.69, 23.94) * mm});
            skLineSegment(sketch, "E513", {"start": v(11.69, 23.94) * mm, "end": v(11.6, 23.98) * mm});
            skLineSegment(sketch, "E514", {"start": v(11.6, 23.98) * mm, "end": v(11.09, 24.22) * mm});
            skLineSegment(sketch, "E515", {"start": v(11.09, 24.22) * mm, "end": v(10.58, 24.45) * mm});
            skLineSegment(sketch, "E516", {"start": v(10.58, 24.45) * mm, "end": v(10.07, 24.66) * mm});
            skLineSegment(sketch, "E517", {"start": v(10.07, 24.66) * mm, "end": v(9.97, 24.7) * mm});
            skLineSegment(sketch, "E518", {"start": v(9.97, 24.7) * mm, "end": v(9.93, 24.72) * mm});
            skLineSegment(sketch, "E519", {"start": v(9.93, 24.72) * mm, "end": v(9.9, 24.75) * mm});
            skLineSegment(sketch, "E520", {"start": v(9.9, 24.75) * mm, "end": v(9.87, 24.8) * mm});
            skLineSegment(sketch, "E521", {"start": v(9.87, 24.8) * mm, "end": v(9.85, 24.85) * mm});
            skLineSegment(sketch, "E522", {"start": v(9.85, 24.85) * mm, "end": v(9.84, 24.91) * mm});
            skLineSegment(sketch, "E523", {"start": v(9.84, 24.91) * mm, "end": v(9.83, 25) * mm});
            skLineSegment(sketch, "E524", {"start": v(9.83, 25) * mm, "end": v(9.84, 25.08) * mm});
            skLineSegment(sketch, "E525", {"start": v(9.84, 25.08) * mm, "end": v(9.85, 25.18) * mm});
            skLineSegment(sketch, "E526", {"start": v(9.85, 25.18) * mm, "end": v(9.86, 25.29) * mm});
            skLineSegment(sketch, "E527", {"start": v(9.86, 25.29) * mm, "end": v(9.9, 25.4) * mm});
            skLineSegment(sketch, "E528", {"start": v(9.9, 25.4) * mm, "end": v(9.93, 25.54) * mm});
            skLineSegment(sketch, "E529", {"start": v(9.93, 25.54) * mm, "end": v(9.98, 25.68) * mm});
            skLineSegment(sketch, "E530", {"start": v(9.98, 25.68) * mm, "end": v(10.03, 25.83) * mm});
            skLineSegment(sketch, "E531", {"start": v(10.03, 25.83) * mm, "end": v(10.07, 25.9) * mm});
            skLineSegment(sketch, "E532", {"start": v(10.07, 25.9) * mm, "end": v(10.07, 25.9) * mm});
            skLineSegment(sketch, "E533", {"start": v(10.07, 25.9) * mm, "end": v(10.07, 25.92) * mm});
            skLineSegment(sketch, "E534", {"start": v(10.07, 25.92) * mm, "end": v(10.08, 25.95) * mm});
            skLineSegment(sketch, "E535", {"start": v(10.08, 25.95) * mm, "end": v(10.1, 26) * mm});
            skLineSegment(sketch, "E536", {"start": v(10.1, 26) * mm, "end": v(10.11, 26.04) * mm});
            skLineSegment(sketch, "E537", {"start": v(10.11, 26.04) * mm, "end": v(10.13, 26.1) * mm});
            skLineSegment(sketch, "E538", {"start": v(10.13, 26.1) * mm, "end": v(10.15, 26.18) * mm});
            skLineSegment(sketch, "E539", {"start": v(10.15, 26.18) * mm, "end": v(10.16, 26.27) * mm});
            skLineSegment(sketch, "E540", {"start": v(10.16, 26.27) * mm, "end": v(10.18, 26.37) * mm});
            skLineSegment(sketch, "E541", {"start": v(10.18, 26.37) * mm, "end": v(10.2, 26.49) * mm});
            skLineSegment(sketch, "E542", {"start": v(10.2, 26.49) * mm, "end": v(10.22, 26.61) * mm});
            skLineSegment(sketch, "E543", {"start": v(10.22, 26.61) * mm, "end": v(10.24, 26.75) * mm});
            skLineSegment(sketch, "E544", {"start": v(10.24, 26.75) * mm, "end": v(10.26, 26.9) * mm});
            skLineSegment(sketch, "E545", {"start": v(10.26, 26.9) * mm, "end": v(10.27, 27.06) * mm});
            skLineSegment(sketch, "E546", {"start": v(10.27, 27.06) * mm, "end": v(10.29, 27.24) * mm});
            skLineSegment(sketch, "E547", {"start": v(10.29, 27.24) * mm, "end": v(10.3, 27.42) * mm});
            skLineSegment(sketch, "E548", {"start": v(10.3, 27.42) * mm, "end": v(10.3, 27.62) * mm});
            skLineSegment(sketch, "E549", {"start": v(10.3, 27.62) * mm, "end": v(10.3, 27.84) * mm});
            skLineSegment(sketch, "E550", {"start": v(10.3, 27.84) * mm, "end": v(10.3, 28.06) * mm});
            skLineSegment(sketch, "E551", {"start": v(10.3, 28.06) * mm, "end": v(10.29, 28.3) * mm});
            skLineSegment(sketch, "E552", {"start": v(10.29, 28.3) * mm, "end": v(10.28, 28.55) * mm});
            skLineSegment(sketch, "E553", {"start": v(10.28, 28.55) * mm, "end": v(10.26, 28.75) * mm});
            skLineSegment(sketch, "E554", {"start": v(10.26, 28.75) * mm, "end": v(9.44, 29.06) * mm});
            skLineSegment(sketch, "E555", {"start": v(9.44, 29.06) * mm, "end": v(8.6, 29.29) * mm});
            skLineSegment(sketch, "E556", {"start": v(8.6, 29.29) * mm, "end": v(8.47, 29.13) * mm});
            skLineSegment(sketch, "E557", {"start": v(8.47, 29.13) * mm, "end": v(8.3, 28.94) * mm});
            skLineSegment(sketch, "E558", {"start": v(8.3, 28.94) * mm, "end": v(8.16, 28.76) * mm});
            skLineSegment(sketch, "E559", {"start": v(8.16, 28.76) * mm, "end": v(8.03, 28.58) * mm});
            skLineSegment(sketch, "E560", {"start": v(8.03, 28.58) * mm, "end": v(7.9, 28.4) * mm});
            skLineSegment(sketch, "E561", {"start": v(7.9, 28.4) * mm, "end": v(7.8, 28.24) * mm});
            skLineSegment(sketch, "E562", {"start": v(7.8, 28.24) * mm, "end": v(7.69, 28.08) * mm});
            skLineSegment(sketch, "E563", {"start": v(7.69, 28.08) * mm, "end": v(7.6, 27.93) * mm});
            skLineSegment(sketch, "E564", {"start": v(7.6, 27.93) * mm, "end": v(7.51, 27.8) * mm});
            skLineSegment(sketch, "E565", {"start": v(7.51, 27.8) * mm, "end": v(7.44, 27.66) * mm});
            skLineSegment(sketch, "E566", {"start": v(7.44, 27.66) * mm, "end": v(7.37, 27.54) * mm});
            skLineSegment(sketch, "E567", {"start": v(7.37, 27.54) * mm, "end": v(7.31, 27.43) * mm});
            skLineSegment(sketch, "E568", {"start": v(7.31, 27.43) * mm, "end": v(7.26, 27.32) * mm});
            skLineSegment(sketch, "E569", {"start": v(7.26, 27.32) * mm, "end": v(7.22, 27.23) * mm});
            skLineSegment(sketch, "E570", {"start": v(7.22, 27.23) * mm, "end": v(7.18, 27.15) * mm});
            skLineSegment(sketch, "E571", {"start": v(7.18, 27.15) * mm, "end": v(7.15, 27.07) * mm});
            skLineSegment(sketch, "E572", {"start": v(7.15, 27.07) * mm, "end": v(7.13, 27.01) * mm});
            skLineSegment(sketch, "E573", {"start": v(7.13, 27.01) * mm, "end": v(7.11, 26.96) * mm});
            skLineSegment(sketch, "E574", {"start": v(7.11, 26.96) * mm, "end": v(7.1, 26.92) * mm});
            skLineSegment(sketch, "E575", {"start": v(7.1, 26.92) * mm, "end": v(7.09, 26.9) * mm});
            skLineSegment(sketch, "E576", {"start": v(7.09, 26.9) * mm, "end": v(7.08, 26.88) * mm});
            skLineSegment(sketch, "E577", {"start": v(7.08, 26.88) * mm, "end": v(7.08, 26.88) * mm});
            skLineSegment(sketch, "E578", {"start": v(7.08, 26.88) * mm, "end": v(7.06, 26.8) * mm});
            skLineSegment(sketch, "E579", {"start": v(7.06, 26.8) * mm, "end": v(7.02, 26.64) * mm});
            skLineSegment(sketch, "E580", {"start": v(7.02, 26.64) * mm, "end": v(6.98, 26.5) * mm});
            skLineSegment(sketch, "E581", {"start": v(6.98, 26.5) * mm, "end": v(6.93, 26.37) * mm});
            skLineSegment(sketch, "E582", {"start": v(6.93, 26.37) * mm, "end": v(6.88, 26.26) * mm});
            skLineSegment(sketch, "E583", {"start": v(6.88, 26.26) * mm, "end": v(6.84, 26.16) * mm});
            skLineSegment(sketch, "E584", {"start": v(6.84, 26.16) * mm, "end": v(6.78, 26.07) * mm});
            skLineSegment(sketch, "E585", {"start": v(6.78, 26.07) * mm, "end": v(6.73, 26) * mm});
            skLineSegment(sketch, "E586", {"start": v(6.73, 26) * mm, "end": v(6.68, 25.94) * mm});
            skLineSegment(sketch, "E587", {"start": v(6.68, 25.94) * mm, "end": v(6.63, 25.9) * mm});
            skLineSegment(sketch, "E588", {"start": v(6.63, 25.9) * mm, "end": v(6.59, 25.86) * mm});
            skLineSegment(sketch, "E589", {"start": v(6.59, 25.86) * mm, "end": v(6.54, 25.84) * mm});
            skLineSegment(sketch, "E590", {"start": v(6.54, 25.84) * mm, "end": v(6.5, 25.84) * mm});
            skLineSegment(sketch, "E591", {"start": v(6.5, 25.84) * mm, "end": v(6.45, 25.85) * mm});
            skLineSegment(sketch, "E592", {"start": v(6.45, 25.85) * mm, "end": v(6.35, 25.87) * mm});
            skLineSegment(sketch, "E593", {"start": v(6.35, 25.87) * mm, "end": v(5.81, 26) * mm});
            skLineSegment(sketch, "E594", {"start": v(5.81, 26) * mm, "end": v(5.27, 26.11) * mm});
            skLineSegment(sketch, "E595", {"start": v(5.27, 26.11) * mm, "end": v(4.72, 26.22) * mm});
            skLineSegment(sketch, "E596", {"start": v(4.72, 26.22) * mm, "end": v(4.62, 26.24) * mm});
            skLineSegment(sketch, "E597", {"start": v(4.62, 26.24) * mm, "end": v(4.58, 26.25) * mm});
            skLineSegment(sketch, "E598", {"start": v(4.58, 26.25) * mm, "end": v(4.54, 26.27) * mm});
            skLineSegment(sketch, "E599", {"start": v(4.54, 26.27) * mm, "end": v(4.5, 26.3) * mm});
            skLineSegment(sketch, "E600", {"start": v(4.5, 26.3) * mm, "end": v(4.47, 26.35) * mm});
            skLineSegment(sketch, "E601", {"start": v(4.47, 26.35) * mm, "end": v(4.44, 26.42) * mm});
            skLineSegment(sketch, "E602", {"start": v(4.44, 26.42) * mm, "end": v(4.42, 26.5) * mm});
            skLineSegment(sketch, "E603", {"start": v(4.42, 26.5) * mm, "end": v(4.4, 26.58) * mm});
            skLineSegment(sketch, "E604", {"start": v(4.4, 26.58) * mm, "end": v(4.4, 26.68) * mm});
            skLineSegment(sketch, "E605", {"start": v(4.4, 26.68) * mm, "end": v(4.4, 26.79) * mm});
            skLineSegment(sketch, "E606", {"start": v(4.4, 26.79) * mm, "end": v(4.4, 26.91) * mm});
            skLineSegment(sketch, "E607", {"start": v(4.4, 26.91) * mm, "end": v(4.4, 27.05) * mm});
            skLineSegment(sketch, "E608", {"start": v(4.4, 27.05) * mm, "end": v(4.42, 27.2) * mm});
            skLineSegment(sketch, "E609", {"start": v(4.42, 27.2) * mm, "end": v(4.44, 27.35) * mm});
            skLineSegment(sketch, "E610", {"start": v(4.44, 27.35) * mm, "end": v(4.46, 27.43) * mm});
            skLineSegment(sketch, "E611", {"start": v(4.46, 27.43) * mm, "end": v(4.46, 27.44) * mm});
            skLineSegment(sketch, "E612", {"start": v(4.46, 27.44) * mm, "end": v(4.46, 27.45) * mm});
            skLineSegment(sketch, "E613", {"start": v(4.46, 27.45) * mm, "end": v(4.47, 27.48) * mm});
            skLineSegment(sketch, "E614", {"start": v(4.47, 27.48) * mm, "end": v(4.47, 27.52) * mm});
            skLineSegment(sketch, "E615", {"start": v(4.47, 27.52) * mm, "end": v(4.47, 27.58) * mm});
            skLineSegment(sketch, "E616", {"start": v(4.47, 27.58) * mm, "end": v(4.48, 27.64) * mm});
            skLineSegment(sketch, "E617", {"start": v(4.48, 27.64) * mm, "end": v(4.48, 27.72) * mm});
            skLineSegment(sketch, "E618", {"start": v(4.48, 27.72) * mm, "end": v(4.48, 27.81) * mm});
            skLineSegment(sketch, "E619", {"start": v(4.48, 27.81) * mm, "end": v(4.48, 27.91) * mm});
            skLineSegment(sketch, "E620", {"start": v(4.48, 27.91) * mm, "end": v(4.47, 28.03) * mm});
            skLineSegment(sketch, "E621", {"start": v(4.47, 28.03) * mm, "end": v(4.47, 28.15) * mm});
            skLineSegment(sketch, "E622", {"start": v(4.47, 28.15) * mm, "end": v(4.46, 28.3) * mm});
            skLineSegment(sketch, "E623", {"start": v(4.46, 28.3) * mm, "end": v(4.44, 28.44) * mm});
            skLineSegment(sketch, "E624", {"start": v(4.44, 28.44) * mm, "end": v(4.42, 28.6) * mm});
            skLineSegment(sketch, "E625", {"start": v(4.42, 28.6) * mm, "end": v(4.4, 28.78) * mm});
            skLineSegment(sketch, "E626", {"start": v(4.4, 28.78) * mm, "end": v(4.37, 28.97) * mm});
            skLineSegment(sketch, "E627", {"start": v(4.37, 28.97) * mm, "end": v(4.33, 29.16) * mm});
            skLineSegment(sketch, "E628", {"start": v(4.33, 29.16) * mm, "end": v(4.29, 29.37) * mm});
            skLineSegment(sketch, "E629", {"start": v(4.29, 29.37) * mm, "end": v(4.24, 29.59) * mm});
            skLineSegment(sketch, "E630", {"start": v(4.24, 29.59) * mm, "end": v(4.18, 29.82) * mm});
            skLineSegment(sketch, "E631", {"start": v(4.18, 29.82) * mm, "end": v(4.12, 30.06) * mm});
            skLineSegment(sketch, "E632", {"start": v(4.12, 30.06) * mm, "end": v(4.06, 30.25) * mm});
            skLineSegment(sketch, "E633", {"start": v(4.06, 30.25) * mm, "end": v(3.2, 30.4) * mm});
            skLineSegment(sketch, "E634", {"start": v(3.2, 30.4) * mm, "end": v(2.32, 30.44) * mm});
            skLineSegment(sketch, "E635", {"start": v(2.32, 30.44) * mm, "end": v(2.22, 30.26) * mm});
            skLineSegment(sketch, "E636", {"start": v(2.22, 30.26) * mm, "end": v(2.11, 30.04) * mm});
            skLineSegment(sketch, "E637", {"start": v(2.11, 30.04) * mm, "end": v(2, 29.82) * mm});
            skLineSegment(sketch, "E638", {"start": v(2, 29.82) * mm, "end": v(1.91, 29.62) * mm});
            skLineSegment(sketch, "E639", {"start": v(1.91, 29.62) * mm, "end": v(1.83, 29.43) * mm});
            skLineSegment(sketch, "E640", {"start": v(1.83, 29.43) * mm, "end": v(1.75, 29.24) * mm});
            skLineSegment(sketch, "E641", {"start": v(1.75, 29.24) * mm, "end": v(1.68, 29.07) * mm});
            skLineSegment(sketch, "E642", {"start": v(1.68, 29.07) * mm, "end": v(1.62, 28.9) * mm});
            skLineSegment(sketch, "E643", {"start": v(1.62, 28.9) * mm, "end": v(1.57, 28.75) * mm});
            skLineSegment(sketch, "E644", {"start": v(1.57, 28.75) * mm, "end": v(1.52, 28.6) * mm});
            skLineSegment(sketch, "E645", {"start": v(1.52, 28.6) * mm, "end": v(1.48, 28.47) * mm});
            skLineSegment(sketch, "E646", {"start": v(1.48, 28.47) * mm, "end": v(1.45, 28.35) * mm});
            skLineSegment(sketch, "E647", {"start": v(1.45, 28.35) * mm, "end": v(1.42, 28.23) * mm});
            skLineSegment(sketch, "E648", {"start": v(1.42, 28.23) * mm, "end": v(1.4, 28.13) * mm});
            skLineSegment(sketch, "E649", {"start": v(1.4, 28.13) * mm, "end": v(1.38, 28.05) * mm});
            skLineSegment(sketch, "E650", {"start": v(1.38, 28.05) * mm, "end": v(1.37, 27.97) * mm});
            skLineSegment(sketch, "E651", {"start": v(1.37, 27.97) * mm, "end": v(1.36, 27.9) * mm});
            skLineSegment(sketch, "E652", {"start": v(1.36, 27.9) * mm, "end": v(1.35, 27.85) * mm});
            skLineSegment(sketch, "E653", {"start": v(1.35, 27.85) * mm, "end": v(1.34, 27.8) * mm});
            skLineSegment(sketch, "E654", {"start": v(1.34, 27.8) * mm, "end": v(1.34, 27.78) * mm});
            skLineSegment(sketch, "E655", {"start": v(1.34, 27.78) * mm, "end": v(1.34, 27.76) * mm});
            skLineSegment(sketch, "E656", {"start": v(1.34, 27.76) * mm, "end": v(1.34, 27.76) * mm});
            skLineSegment(sketch, "E657", {"start": v(1.34, 27.76) * mm, "end": v(1.34, 27.67) * mm});
            skLineSegment(sketch, "E658", {"start": v(1.34, 27.67) * mm, "end": v(1.33, 27.52) * mm});
            skLineSegment(sketch, "E659", {"start": v(1.33, 27.52) * mm, "end": v(1.32, 27.37) * mm});
            skLineSegment(sketch, "E660", {"start": v(1.32, 27.37) * mm, "end": v(1.3, 27.24) * mm});
            skLineSegment(sketch, "E661", {"start": v(1.3, 27.24) * mm, "end": v(1.28, 27.12) * mm});
            skLineSegment(sketch, "E662", {"start": v(1.28, 27.12) * mm, "end": v(1.25, 27) * mm});
            skLineSegment(sketch, "E663", {"start": v(1.25, 27) * mm, "end": v(1.22, 26.91) * mm});
            skLineSegment(sketch, "E664", {"start": v(1.22, 26.91) * mm, "end": v(1.18, 26.83) * mm});
            skLineSegment(sketch, "E665", {"start": v(1.18, 26.83) * mm, "end": v(1.14, 26.76) * mm});
            skLineSegment(sketch, "E666", {"start": v(1.14, 26.76) * mm, "end": v(1.1, 26.7) * mm});
            skLineSegment(sketch, "E667", {"start": v(1.1, 26.7) * mm, "end": v(1.06, 26.67) * mm});
            skLineSegment(sketch, "E668", {"start": v(1.06, 26.67) * mm, "end": v(1.02, 26.64) * mm});
            skLineSegment(sketch, "E669", {"start": v(1.02, 26.64) * mm, "end": v(0.98, 26.62) * mm});
            skLineSegment(sketch, "E670", {"start": v(0.98, 26.62) * mm, "end": v(0.94, 26.62) * mm});
            skLineSegment(sketch, "E671", {"start": v(0.94, 26.62) * mm, "end": v(0.84, 26.63) * mm});
            skLineSegment(sketch, "E672", {"start": v(0.84, 26.63) * mm, "end": v(0.28, 26.64) * mm});
            skLineSegment(sketch, "E673", {"start": v(0.28, 26.64) * mm, "end": v(-0.28, 26.64) * mm});
            skLineSegment(sketch, "E674", {"start": v(-0.28, 26.64) * mm, "end": v(-0.84, 26.63) * mm});
            skLineSegment(sketch, "E675", {"start": v(-0.84, 26.63) * mm, "end": v(-0.94, 26.62) * mm});
            skLineSegment(sketch, "E676", {"start": v(-0.94, 26.62) * mm, "end": v(-0.98, 26.62) * mm});
            skLineSegment(sketch, "E677", {"start": v(-0.98, 26.62) * mm, "end": v(-1.02, 26.64) * mm});
            skLineSegment(sketch, "E678", {"start": v(-1.02, 26.64) * mm, "end": v(-1.06, 26.67) * mm});
            skLineSegment(sketch, "E679", {"start": v(-1.06, 26.67) * mm, "end": v(-1.1, 26.7) * mm});
            skLineSegment(sketch, "E680", {"start": v(-1.1, 26.7) * mm, "end": v(-1.14, 26.76) * mm});
            skLineSegment(sketch, "E681", {"start": v(-1.14, 26.76) * mm, "end": v(-1.18, 26.83) * mm});
            skLineSegment(sketch, "E682", {"start": v(-1.18, 26.83) * mm, "end": v(-1.22, 26.91) * mm});
            skLineSegment(sketch, "E683", {"start": v(-1.22, 26.91) * mm, "end": v(-1.25, 27) * mm});
            skLineSegment(sketch, "E684", {"start": v(-1.25, 27) * mm, "end": v(-1.28, 27.12) * mm});
            skLineSegment(sketch, "E685", {"start": v(-1.28, 27.12) * mm, "end": v(-1.3, 27.24) * mm});
            skLineSegment(sketch, "E686", {"start": v(-1.3, 27.24) * mm, "end": v(-1.32, 27.37) * mm});
            skLineSegment(sketch, "E687", {"start": v(-1.32, 27.37) * mm, "end": v(-1.33, 27.52) * mm});
            skLineSegment(sketch, "E688", {"start": v(-1.33, 27.52) * mm, "end": v(-1.34, 27.67) * mm});
            skLineSegment(sketch, "E689", {"start": v(-1.34, 27.67) * mm, "end": v(-1.34, 27.76) * mm});
            skLineSegment(sketch, "E690", {"start": v(-1.34, 27.76) * mm, "end": v(-1.34, 27.76) * mm});
            skLineSegment(sketch, "E691", {"start": v(-1.34, 27.76) * mm, "end": v(-1.34, 27.78) * mm});
            skLineSegment(sketch, "E692", {"start": v(-1.34, 27.78) * mm, "end": v(-1.34, 27.8) * mm});
            skLineSegment(sketch, "E693", {"start": v(-1.34, 27.8) * mm, "end": v(-1.35, 27.85) * mm});
            skLineSegment(sketch, "E694", {"start": v(-1.35, 27.85) * mm, "end": v(-1.36, 27.9) * mm});
            skLineSegment(sketch, "E695", {"start": v(-1.36, 27.9) * mm, "end": v(-1.37, 27.97) * mm});
            skLineSegment(sketch, "E696", {"start": v(-1.37, 27.97) * mm, "end": v(-1.38, 28.05) * mm});
            skLineSegment(sketch, "E697", {"start": v(-1.38, 28.05) * mm, "end": v(-1.4, 28.13) * mm});
            skLineSegment(sketch, "E698", {"start": v(-1.4, 28.13) * mm, "end": v(-1.42, 28.23) * mm});
            skLineSegment(sketch, "E699", {"start": v(-1.42, 28.23) * mm, "end": v(-1.45, 28.35) * mm});
            skLineSegment(sketch, "E700", {"start": v(-1.45, 28.35) * mm, "end": v(-1.48, 28.47) * mm});
            skLineSegment(sketch, "E701", {"start": v(-1.48, 28.47) * mm, "end": v(-1.52, 28.6) * mm});
            skLineSegment(sketch, "E702", {"start": v(-1.52, 28.6) * mm, "end": v(-1.57, 28.75) * mm});
            skLineSegment(sketch, "E703", {"start": v(-1.57, 28.75) * mm, "end": v(-1.62, 28.9) * mm});
            skLineSegment(sketch, "E704", {"start": v(-1.62, 28.9) * mm, "end": v(-1.68, 29.07) * mm});
            skLineSegment(sketch, "E705", {"start": v(-1.68, 29.07) * mm, "end": v(-1.75, 29.24) * mm});
            skLineSegment(sketch, "E706", {"start": v(-1.75, 29.24) * mm, "end": v(-1.83, 29.43) * mm});
            skLineSegment(sketch, "E707", {"start": v(-1.83, 29.43) * mm, "end": v(-1.91, 29.62) * mm});
            skLineSegment(sketch, "E708", {"start": v(-1.91, 29.62) * mm, "end": v(-2, 29.82) * mm});
            skLineSegment(sketch, "E709", {"start": v(-2, 29.82) * mm, "end": v(-2.11, 30.04) * mm});
            skLineSegment(sketch, "E710", {"start": v(-2.11, 30.04) * mm, "end": v(-2.22, 30.26) * mm});
            skLineSegment(sketch, "E711", {"start": v(-2.22, 30.26) * mm, "end": v(-2.32, 30.44) * mm});
            skLineSegment(sketch, "E712", {"start": v(-2.32, 30.44) * mm, "end": v(-3.2, 30.4) * mm});
            skLineSegment(sketch, "E713", {"start": v(-3.2, 30.4) * mm, "end": v(-4.06, 30.25) * mm});
            skLineSegment(sketch, "E714", {"start": v(-4.06, 30.25) * mm, "end": v(-4.12, 30.06) * mm});
            skLineSegment(sketch, "E715", {"start": v(-4.12, 30.06) * mm, "end": v(-4.18, 29.82) * mm});
            skLineSegment(sketch, "E716", {"start": v(-4.18, 29.82) * mm, "end": v(-4.24, 29.59) * mm});
            skLineSegment(sketch, "E717", {"start": v(-4.24, 29.59) * mm, "end": v(-4.29, 29.37) * mm});
            skLineSegment(sketch, "E718", {"start": v(-4.29, 29.37) * mm, "end": v(-4.33, 29.16) * mm});
            skLineSegment(sketch, "E719", {"start": v(-4.33, 29.16) * mm, "end": v(-4.37, 28.97) * mm});
            skLineSegment(sketch, "E720", {"start": v(-4.37, 28.97) * mm, "end": v(-4.4, 28.78) * mm});
            skLineSegment(sketch, "E721", {"start": v(-4.4, 28.78) * mm, "end": v(-4.42, 28.6) * mm});
            skLineSegment(sketch, "E722", {"start": v(-4.42, 28.6) * mm, "end": v(-4.44, 28.44) * mm});
            skLineSegment(sketch, "E723", {"start": v(-4.44, 28.44) * mm, "end": v(-4.46, 28.3) * mm});
            skLineSegment(sketch, "E724", {"start": v(-4.46, 28.3) * mm, "end": v(-4.47, 28.15) * mm});
            skLineSegment(sketch, "E725", {"start": v(-4.47, 28.15) * mm, "end": v(-4.47, 28.03) * mm});
            skLineSegment(sketch, "E726", {"start": v(-4.47, 28.03) * mm, "end": v(-4.48, 27.91) * mm});
            skLineSegment(sketch, "E727", {"start": v(-4.48, 27.91) * mm, "end": v(-4.48, 27.81) * mm});
            skLineSegment(sketch, "E728", {"start": v(-4.48, 27.81) * mm, "end": v(-4.48, 27.72) * mm});
            skLineSegment(sketch, "E729", {"start": v(-4.48, 27.72) * mm, "end": v(-4.48, 27.64) * mm});
            skLineSegment(sketch, "E730", {"start": v(-4.48, 27.64) * mm, "end": v(-4.47, 27.58) * mm});
            skLineSegment(sketch, "E731", {"start": v(-4.47, 27.58) * mm, "end": v(-4.47, 27.52) * mm});
            skLineSegment(sketch, "E732", {"start": v(-4.47, 27.52) * mm, "end": v(-4.47, 27.48) * mm});
            skLineSegment(sketch, "E733", {"start": v(-4.47, 27.48) * mm, "end": v(-4.46, 27.45) * mm});
            skLineSegment(sketch, "E734", {"start": v(-4.46, 27.45) * mm, "end": v(-4.46, 27.44) * mm});
            skLineSegment(sketch, "E735", {"start": v(-4.46, 27.44) * mm, "end": v(-4.46, 27.43) * mm});
            skLineSegment(sketch, "E736", {"start": v(-4.46, 27.43) * mm, "end": v(-4.44, 27.35) * mm});
            skLineSegment(sketch, "E737", {"start": v(-4.44, 27.35) * mm, "end": v(-4.42, 27.2) * mm});
            skLineSegment(sketch, "E738", {"start": v(-4.42, 27.2) * mm, "end": v(-4.4, 27.05) * mm});
            skLineSegment(sketch, "E739", {"start": v(-4.4, 27.05) * mm, "end": v(-4.4, 26.91) * mm});
            skLineSegment(sketch, "E740", {"start": v(-4.4, 26.91) * mm, "end": v(-4.4, 26.79) * mm});
            skLineSegment(sketch, "E741", {"start": v(-4.4, 26.79) * mm, "end": v(-4.4, 26.68) * mm});
            skLineSegment(sketch, "E742", {"start": v(-4.4, 26.68) * mm, "end": v(-4.4, 26.58) * mm});
            skLineSegment(sketch, "E743", {"start": v(-4.4, 26.58) * mm, "end": v(-4.42, 26.5) * mm});
            skLineSegment(sketch, "E744", {"start": v(-4.42, 26.5) * mm, "end": v(-4.44, 26.42) * mm});
            skLineSegment(sketch, "E745", {"start": v(-4.44, 26.42) * mm, "end": v(-4.47, 26.35) * mm});
            skLineSegment(sketch, "E746", {"start": v(-4.47, 26.35) * mm, "end": v(-4.5, 26.3) * mm});
            skLineSegment(sketch, "E747", {"start": v(-4.5, 26.3) * mm, "end": v(-4.54, 26.27) * mm});
            skLineSegment(sketch, "E748", {"start": v(-4.54, 26.27) * mm, "end": v(-4.58, 26.25) * mm});
            skLineSegment(sketch, "E749", {"start": v(-4.58, 26.25) * mm, "end": v(-4.62, 26.24) * mm});
            skLineSegment(sketch, "E750", {"start": v(-4.62, 26.24) * mm, "end": v(-4.72, 26.22) * mm});
            skLineSegment(sketch, "E751", {"start": v(-4.72, 26.22) * mm, "end": v(-5.27, 26.11) * mm});
            skLineSegment(sketch, "E752", {"start": v(-5.27, 26.11) * mm, "end": v(-5.81, 26) * mm});
            skLineSegment(sketch, "E753", {"start": v(-5.81, 26) * mm, "end": v(-6.35, 25.87) * mm});
            skLineSegment(sketch, "E754", {"start": v(-6.35, 25.87) * mm, "end": v(-6.45, 25.85) * mm});
            skLineSegment(sketch, "E755", {"start": v(-6.45, 25.85) * mm, "end": v(-6.5, 25.84) * mm});
            skLineSegment(sketch, "E756", {"start": v(-6.5, 25.84) * mm, "end": v(-6.54, 25.84) * mm});
            skLineSegment(sketch, "E757", {"start": v(-6.54, 25.84) * mm, "end": v(-6.59, 25.86) * mm});
            skLineSegment(sketch, "E758", {"start": v(-6.59, 25.86) * mm, "end": v(-6.63, 25.9) * mm});
            skLineSegment(sketch, "E759", {"start": v(-6.63, 25.9) * mm, "end": v(-6.68, 25.94) * mm});
            skLineSegment(sketch, "E760", {"start": v(-6.68, 25.94) * mm, "end": v(-6.73, 26) * mm});
            skLineSegment(sketch, "E761", {"start": v(-6.73, 26) * mm, "end": v(-6.78, 26.07) * mm});
            skLineSegment(sketch, "E762", {"start": v(-6.78, 26.07) * mm, "end": v(-6.84, 26.16) * mm});
            skLineSegment(sketch, "E763", {"start": v(-6.84, 26.16) * mm, "end": v(-6.88, 26.26) * mm});
            skLineSegment(sketch, "E764", {"start": v(-6.88, 26.26) * mm, "end": v(-6.93, 26.37) * mm});
            skLineSegment(sketch, "E765", {"start": v(-6.93, 26.37) * mm, "end": v(-6.98, 26.5) * mm});
            skLineSegment(sketch, "E766", {"start": v(-6.98, 26.5) * mm, "end": v(-7.02, 26.64) * mm});
            skLineSegment(sketch, "E767", {"start": v(-7.02, 26.64) * mm, "end": v(-7.06, 26.8) * mm});
            skLineSegment(sketch, "E768", {"start": v(-7.06, 26.8) * mm, "end": v(-7.08, 26.88) * mm});
            skLineSegment(sketch, "E769", {"start": v(-7.08, 26.88) * mm, "end": v(-7.08, 26.88) * mm});
            skLineSegment(sketch, "E770", {"start": v(-7.08, 26.88) * mm, "end": v(-7.09, 26.9) * mm});
            skLineSegment(sketch, "E771", {"start": v(-7.09, 26.9) * mm, "end": v(-7.1, 26.92) * mm});
            skLineSegment(sketch, "E772", {"start": v(-7.1, 26.92) * mm, "end": v(-7.11, 26.96) * mm});
            skLineSegment(sketch, "E773", {"start": v(-7.11, 26.96) * mm, "end": v(-7.13, 27.01) * mm});
            skLineSegment(sketch, "E774", {"start": v(-7.13, 27.01) * mm, "end": v(-7.15, 27.07) * mm});
            skLineSegment(sketch, "E775", {"start": v(-7.15, 27.07) * mm, "end": v(-7.18, 27.15) * mm});
            skLineSegment(sketch, "E776", {"start": v(-7.18, 27.15) * mm, "end": v(-7.22, 27.23) * mm});
            skLineSegment(sketch, "E777", {"start": v(-7.22, 27.23) * mm, "end": v(-7.26, 27.32) * mm});
            skLineSegment(sketch, "E778", {"start": v(-7.26, 27.32) * mm, "end": v(-7.31, 27.43) * mm});
            skLineSegment(sketch, "E779", {"start": v(-7.31, 27.43) * mm, "end": v(-7.37, 27.54) * mm});
            skLineSegment(sketch, "E780", {"start": v(-7.37, 27.54) * mm, "end": v(-7.44, 27.66) * mm});
            skLineSegment(sketch, "E781", {"start": v(-7.44, 27.66) * mm, "end": v(-7.51, 27.8) * mm});
            skLineSegment(sketch, "E782", {"start": v(-7.51, 27.8) * mm, "end": v(-7.6, 27.93) * mm});
            skLineSegment(sketch, "E783", {"start": v(-7.6, 27.93) * mm, "end": v(-7.69, 28.08) * mm});
            skLineSegment(sketch, "E784", {"start": v(-7.69, 28.08) * mm, "end": v(-7.8, 28.24) * mm});
            skLineSegment(sketch, "E785", {"start": v(-7.8, 28.24) * mm, "end": v(-7.9, 28.4) * mm});
            skLineSegment(sketch, "E786", {"start": v(-7.9, 28.4) * mm, "end": v(-8.03, 28.58) * mm});
            skLineSegment(sketch, "E787", {"start": v(-8.03, 28.58) * mm, "end": v(-8.16, 28.76) * mm});
            skLineSegment(sketch, "E788", {"start": v(-8.16, 28.76) * mm, "end": v(-8.3, 28.94) * mm});
            skLineSegment(sketch, "E789", {"start": v(-8.3, 28.94) * mm, "end": v(-8.47, 29.13) * mm});
            skLineSegment(sketch, "E790", {"start": v(-8.47, 29.13) * mm, "end": v(-8.6, 29.29) * mm});
            skLineSegment(sketch, "E791", {"start": v(-8.6, 29.29) * mm, "end": v(-9.44, 29.06) * mm});
            skLineSegment(sketch, "E792", {"start": v(-9.44, 29.06) * mm, "end": v(-10.26, 28.75) * mm});
            skLineSegment(sketch, "E793", {"start": v(-10.26, 28.75) * mm, "end": v(-10.28, 28.55) * mm});
            skLineSegment(sketch, "E794", {"start": v(-10.28, 28.55) * mm, "end": v(-10.29, 28.3) * mm});
            skLineSegment(sketch, "E795", {"start": v(-10.29, 28.3) * mm, "end": v(-10.3, 28.06) * mm});
            skLineSegment(sketch, "E796", {"start": v(-10.3, 28.06) * mm, "end": v(-10.3, 27.84) * mm});
            skLineSegment(sketch, "E797", {"start": v(-10.3, 27.84) * mm, "end": v(-10.3, 27.62) * mm});
            skLineSegment(sketch, "E798", {"start": v(-10.3, 27.62) * mm, "end": v(-10.3, 27.42) * mm});
            skLineSegment(sketch, "E799", {"start": v(-10.3, 27.42) * mm, "end": v(-10.29, 27.24) * mm});
            skLineSegment(sketch, "E800", {"start": v(-10.29, 27.24) * mm, "end": v(-10.27, 27.06) * mm});
            skLineSegment(sketch, "E801", {"start": v(-10.27, 27.06) * mm, "end": v(-10.26, 26.9) * mm});
            skLineSegment(sketch, "E802", {"start": v(-10.26, 26.9) * mm, "end": v(-10.24, 26.75) * mm});
            skLineSegment(sketch, "E803", {"start": v(-10.24, 26.75) * mm, "end": v(-10.22, 26.61) * mm});
            skLineSegment(sketch, "E804", {"start": v(-10.22, 26.61) * mm, "end": v(-10.2, 26.49) * mm});
            skLineSegment(sketch, "E805", {"start": v(-10.2, 26.49) * mm, "end": v(-10.18, 26.37) * mm});
            skLineSegment(sketch, "E806", {"start": v(-10.18, 26.37) * mm, "end": v(-10.16, 26.27) * mm});
            skLineSegment(sketch, "E807", {"start": v(-10.16, 26.27) * mm, "end": v(-10.15, 26.18) * mm});
            skLineSegment(sketch, "E808", {"start": v(-10.15, 26.18) * mm, "end": v(-10.13, 26.1) * mm});
            skLineSegment(sketch, "E809", {"start": v(-10.13, 26.1) * mm, "end": v(-10.11, 26.04) * mm});
            skLineSegment(sketch, "E810", {"start": v(-10.11, 26.04) * mm, "end": v(-10.1, 26) * mm});
            skLineSegment(sketch, "E811", {"start": v(-10.1, 26) * mm, "end": v(-10.08, 25.95) * mm});
            skLineSegment(sketch, "E812", {"start": v(-10.08, 25.95) * mm, "end": v(-10.07, 25.92) * mm});
            skLineSegment(sketch, "E813", {"start": v(-10.07, 25.92) * mm, "end": v(-10.07, 25.9) * mm});
            skLineSegment(sketch, "E814", {"start": v(-10.07, 25.9) * mm, "end": v(-10.07, 25.9) * mm});
            skLineSegment(sketch, "E815", {"start": v(-10.07, 25.9) * mm, "end": v(-10.03, 25.83) * mm});
            skLineSegment(sketch, "E816", {"start": v(-10.03, 25.83) * mm, "end": v(-9.98, 25.68) * mm});
            skLineSegment(sketch, "E817", {"start": v(-9.98, 25.68) * mm, "end": v(-9.93, 25.54) * mm});
            skLineSegment(sketch, "E818", {"start": v(-9.93, 25.54) * mm, "end": v(-9.9, 25.4) * mm});
            skLineSegment(sketch, "E819", {"start": v(-9.9, 25.4) * mm, "end": v(-9.86, 25.29) * mm});
            skLineSegment(sketch, "E820", {"start": v(-9.86, 25.29) * mm, "end": v(-9.85, 25.18) * mm});
            skLineSegment(sketch, "E821", {"start": v(-9.85, 25.18) * mm, "end": v(-9.84, 25.08) * mm});
            skLineSegment(sketch, "E822", {"start": v(-9.84, 25.08) * mm, "end": v(-9.83, 25) * mm});
            skLineSegment(sketch, "E823", {"start": v(-9.83, 25) * mm, "end": v(-9.84, 24.91) * mm});
            skLineSegment(sketch, "E824", {"start": v(-9.84, 24.91) * mm, "end": v(-9.85, 24.85) * mm});
            skLineSegment(sketch, "E825", {"start": v(-9.85, 24.85) * mm, "end": v(-9.87, 24.8) * mm});
            skLineSegment(sketch, "E826", {"start": v(-9.87, 24.8) * mm, "end": v(-9.9, 24.75) * mm});
            skLineSegment(sketch, "E827", {"start": v(-9.9, 24.75) * mm, "end": v(-9.93, 24.72) * mm});
            skLineSegment(sketch, "E828", {"start": v(-9.93, 24.72) * mm, "end": v(-9.97, 24.7) * mm});
            skLineSegment(sketch, "E829", {"start": v(-9.97, 24.7) * mm, "end": v(-10.07, 24.66) * mm});
            skLineSegment(sketch, "E830", {"start": v(-10.07, 24.66) * mm, "end": v(-10.58, 24.45) * mm});
            skLineSegment(sketch, "E831", {"start": v(-10.58, 24.45) * mm, "end": v(-11.09, 24.22) * mm});
            skLineSegment(sketch, "E832", {"start": v(-11.09, 24.22) * mm, "end": v(-11.6, 23.98) * mm});
            skLineSegment(sketch, "E833", {"start": v(-11.6, 23.98) * mm, "end": v(-11.69, 23.94) * mm});
            skLineSegment(sketch, "E834", {"start": v(-11.69, 23.94) * mm, "end": v(-11.72, 23.92) * mm});
            skLineSegment(sketch, "E835", {"start": v(-11.72, 23.92) * mm, "end": v(-11.77, 23.92) * mm});
            skLineSegment(sketch, "E836", {"start": v(-11.77, 23.92) * mm, "end": v(-11.82, 23.93) * mm});
            skLineSegment(sketch, "E837", {"start": v(-11.82, 23.93) * mm, "end": v(-11.87, 23.95) * mm});
            skLineSegment(sketch, "E838", {"start": v(-11.87, 23.95) * mm, "end": v(-11.93, 23.98) * mm});
            skLineSegment(sketch, "E839", {"start": v(-11.93, 23.98) * mm, "end": v(-12, 24.03) * mm});
            skLineSegment(sketch, "E840", {"start": v(-12, 24.03) * mm, "end": v(-12.06, 24.1) * mm});
            skLineSegment(sketch, "E841", {"start": v(-12.06, 24.1) * mm, "end": v(-12.12, 24.17) * mm});
            skLineSegment(sketch, "E842", {"start": v(-12.12, 24.17) * mm, "end": v(-12.2, 24.25) * mm});
            skLineSegment(sketch, "E843", {"start": v(-12.2, 24.25) * mm, "end": v(-12.26, 24.35) * mm});
            skLineSegment(sketch, "E844", {"start": v(-12.26, 24.35) * mm, "end": v(-12.34, 24.47) * mm});
            skLineSegment(sketch, "E845", {"start": v(-12.34, 24.47) * mm, "end": v(-12.4, 24.6) * mm});
            skLineSegment(sketch, "E846", {"start": v(-12.4, 24.6) * mm, "end": v(-12.48, 24.74) * mm});
            skLineSegment(sketch, "E847", {"start": v(-12.48, 24.74) * mm, "end": v(-12.52, 24.82) * mm});
            skLineSegment(sketch, "E848", {"start": v(-12.52, 24.82) * mm, "end": v(-12.52, 24.82) * mm});
            skLineSegment(sketch, "E849", {"start": v(-12.52, 24.82) * mm, "end": v(-12.52, 24.83) * mm});
            skLineSegment(sketch, "E850", {"start": v(-12.52, 24.83) * mm, "end": v(-12.54, 24.86) * mm});
            skLineSegment(sketch, "E851", {"start": v(-12.54, 24.86) * mm, "end": v(-12.56, 24.9) * mm});
            skLineSegment(sketch, "E852", {"start": v(-12.56, 24.9) * mm, "end": v(-12.59, 24.94) * mm});
            skLineSegment(sketch, "E853", {"start": v(-12.59, 24.94) * mm, "end": v(-12.63, 25) * mm});
            skLineSegment(sketch, "E854", {"start": v(-12.63, 25) * mm, "end": v(-12.67, 25.06) * mm});
            skLineSegment(sketch, "E855", {"start": v(-12.67, 25.06) * mm, "end": v(-12.72, 25.13) * mm});
            skLineSegment(sketch, "E856", {"start": v(-12.72, 25.13) * mm, "end": v(-12.78, 25.22) * mm});
            skLineSegment(sketch, "E857", {"start": v(-12.78, 25.22) * mm, "end": v(-12.85, 25.3) * mm});
            skLineSegment(sketch, "E858", {"start": v(-12.85, 25.3) * mm, "end": v(-12.93, 25.4) * mm});
            skLineSegment(sketch, "E859", {"start": v(-12.93, 25.4) * mm, "end": v(-13.02, 25.5) * mm});
            skLineSegment(sketch, "E860", {"start": v(-13.02, 25.5) * mm, "end": v(-13.13, 25.62) * mm});
            skLineSegment(sketch, "E861", {"start": v(-13.13, 25.62) * mm, "end": v(-13.24, 25.74) * mm});
            skLineSegment(sketch, "E862", {"start": v(-13.24, 25.74) * mm, "end": v(-13.36, 25.87) * mm});
            skLineSegment(sketch, "E863", {"start": v(-13.36, 25.87) * mm, "end": v(-13.5, 26) * mm});
            skLineSegment(sketch, "E864", {"start": v(-13.5, 26) * mm, "end": v(-13.64, 26.14) * mm});
            skLineSegment(sketch, "E865", {"start": v(-13.64, 26.14) * mm, "end": v(-13.8, 26.28) * mm});
            skLineSegment(sketch, "E866", {"start": v(-13.8, 26.28) * mm, "end": v(-13.96, 26.43) * mm});
            skLineSegment(sketch, "E867", {"start": v(-13.96, 26.43) * mm, "end": v(-14.14, 26.58) * mm});
            skLineSegment(sketch, "E868", {"start": v(-14.14, 26.58) * mm, "end": v(-14.34, 26.74) * mm});
            skLineSegment(sketch, "E869", {"start": v(-14.34, 26.74) * mm, "end": v(-14.5, 26.86) * mm});
            skLineSegment(sketch, "E870", {"start": v(-14.5, 26.86) * mm, "end": v(-15.28, 26.46) * mm});
            skLineSegment(sketch, "E871", {"start": v(-15.28, 26.46) * mm, "end": v(-16.01, 25.99) * mm});
            skLineSegment(sketch, "E872", {"start": v(-16.01, 25.99) * mm, "end": v(-15.99, 25.79) * mm});
            skLineSegment(sketch, "E873", {"start": v(-15.99, 25.79) * mm, "end": v(-15.95, 25.54) * mm});
            skLineSegment(sketch, "E874", {"start": v(-15.95, 25.54) * mm, "end": v(-15.9, 25.3) * mm});
            skLineSegment(sketch, "E875", {"start": v(-15.9, 25.3) * mm, "end": v(-15.86, 25.09) * mm});
            skLineSegment(sketch, "E876", {"start": v(-15.86, 25.09) * mm, "end": v(-15.82, 24.88) * mm});
            skLineSegment(sketch, "E877", {"start": v(-15.82, 24.88) * mm, "end": v(-15.77, 24.69) * mm});
            skLineSegment(sketch, "E878", {"start": v(-15.77, 24.69) * mm, "end": v(-15.72, 24.5) * mm});
            skLineSegment(sketch, "E879", {"start": v(-15.72, 24.5) * mm, "end": v(-15.68, 24.33) * mm});
            skLineSegment(sketch, "E880", {"start": v(-15.68, 24.33) * mm, "end": v(-15.63, 24.18) * mm});
            skLineSegment(sketch, "E881", {"start": v(-15.63, 24.18) * mm, "end": v(-15.58, 24.03) * mm});
            skLineSegment(sketch, "E882", {"start": v(-15.58, 24.03) * mm, "end": v(-15.53, 23.9) * mm});
            skLineSegment(sketch, "E883", {"start": v(-15.53, 23.9) * mm, "end": v(-15.49, 23.78) * mm});
            skLineSegment(sketch, "E884", {"start": v(-15.49, 23.78) * mm, "end": v(-15.45, 23.68) * mm});
            skLineSegment(sketch, "E885", {"start": v(-15.45, 23.68) * mm, "end": v(-15.4, 23.58) * mm});
            skLineSegment(sketch, "E886", {"start": v(-15.4, 23.58) * mm, "end": v(-15.37, 23.5) * mm});
            skLineSegment(sketch, "E887", {"start": v(-15.37, 23.5) * mm, "end": v(-15.33, 23.43) * mm});
            skLineSegment(sketch, "E888", {"start": v(-15.33, 23.43) * mm, "end": v(-15.3, 23.37) * mm});
            skLineSegment(sketch, "E889", {"start": v(-15.3, 23.37) * mm, "end": v(-15.28, 23.32) * mm});
            skLineSegment(sketch, "E890", {"start": v(-15.28, 23.32) * mm, "end": v(-15.26, 23.29) * mm});
            skLineSegment(sketch, "E891", {"start": v(-15.26, 23.29) * mm, "end": v(-15.24, 23.26) * mm});
            skLineSegment(sketch, "E892", {"start": v(-15.24, 23.26) * mm, "end": v(-15.23, 23.25) * mm});
            skLineSegment(sketch, "E893", {"start": v(-15.23, 23.25) * mm, "end": v(-15.23, 23.25) * mm});
            skLineSegment(sketch, "E894", {"start": v(-15.23, 23.25) * mm, "end": v(-15.18, 23.18) * mm});
            skLineSegment(sketch, "E895", {"start": v(-15.18, 23.18) * mm, "end": v(-15.1, 23.04) * mm});
            skLineSegment(sketch, "E896", {"start": v(-15.1, 23.04) * mm, "end": v(-15.02, 22.92) * mm});
            skLineSegment(sketch, "E897", {"start": v(-15.02, 22.92) * mm, "end": v(-14.96, 22.8) * mm});
            skLineSegment(sketch, "E898", {"start": v(-14.96, 22.8) * mm, "end": v(-14.9, 22.69) * mm});
            skLineSegment(sketch, "E899", {"start": v(-14.9, 22.69) * mm, "end": v(-14.87, 22.58) * mm});
            skLineSegment(sketch, "E900", {"start": v(-14.87, 22.58) * mm, "end": v(-14.83, 22.49) * mm});
            skLineSegment(sketch, "E901", {"start": v(-14.83, 22.49) * mm, "end": v(-14.81, 22.4) * mm});
            skLineSegment(sketch, "E902", {"start": v(-14.81, 22.4) * mm, "end": v(-14.8, 22.32) * mm});
            skLineSegment(sketch, "E903", {"start": v(-14.8, 22.32) * mm, "end": v(-14.8, 22.26) * mm});
            skLineSegment(sketch, "E904", {"start": v(-14.8, 22.26) * mm, "end": v(-14.81, 22.2) * mm});
            skLineSegment(sketch, "E905", {"start": v(-14.81, 22.2) * mm, "end": v(-14.83, 22.15) * mm});
            skLineSegment(sketch, "E906", {"start": v(-14.83, 22.15) * mm, "end": v(-14.86, 22.11) * mm});
            skLineSegment(sketch, "E907", {"start": v(-14.86, 22.11) * mm, "end": v(-14.89, 22.09) * mm});
            skLineSegment(sketch, "E908", {"start": v(-14.89, 22.09) * mm, "end": v(-14.97, 22.03) * mm});
            skLineSegment(sketch, "E909", {"start": v(-14.97, 22.03) * mm, "end": v(-15.43, 21.71) * mm});
            skLineSegment(sketch, "E910", {"start": v(-15.43, 21.71) * mm, "end": v(-15.88, 21.39) * mm});
            skLineSegment(sketch, "E911", {"start": v(-15.88, 21.39) * mm, "end": v(-16.33, 21.05) * mm});
            skLineSegment(sketch, "E912", {"start": v(-16.33, 21.05) * mm, "end": v(-16.4, 20.99) * mm});
            skLineSegment(sketch, "E913", {"start": v(-16.4, 20.99) * mm, "end": v(-16.44, 20.96) * mm});
            skLineSegment(sketch, "E914", {"start": v(-16.44, 20.96) * mm, "end": v(-16.48, 20.95) * mm});
            skLineSegment(sketch, "E915", {"start": v(-16.48, 20.95) * mm, "end": v(-16.54, 20.95) * mm});
            skLineSegment(sketch, "E916", {"start": v(-16.54, 20.95) * mm, "end": v(-16.6, 20.96) * mm});
            skLineSegment(sketch, "E917", {"start": v(-16.6, 20.96) * mm, "end": v(-16.66, 20.98) * mm});
            skLineSegment(sketch, "E918", {"start": v(-16.66, 20.98) * mm, "end": v(-16.73, 21.01) * mm});
            skLineSegment(sketch, "E919", {"start": v(-16.73, 21.01) * mm, "end": v(-16.8, 21.06) * mm});
            skLineSegment(sketch, "E920", {"start": v(-16.8, 21.06) * mm, "end": v(-16.88, 21.12) * mm});
            skLineSegment(sketch, "E921", {"start": v(-16.88, 21.12) * mm, "end": v(-16.97, 21.19) * mm});
            skLineSegment(sketch, "E922", {"start": v(-16.97, 21.19) * mm, "end": v(-17.06, 21.27) * mm});
            skLineSegment(sketch, "E923", {"start": v(-17.06, 21.27) * mm, "end": v(-17.15, 21.37) * mm});
            skLineSegment(sketch, "E924", {"start": v(-17.15, 21.37) * mm, "end": v(-17.25, 21.48) * mm});
            skLineSegment(sketch, "E925", {"start": v(-17.25, 21.48) * mm, "end": v(-17.35, 21.6) * mm});
            skLineSegment(sketch, "E926", {"start": v(-17.35, 21.6) * mm, "end": v(-17.4, 21.67) * mm});
            skLineSegment(sketch, "E927", {"start": v(-17.4, 21.67) * mm, "end": v(-17.4, 21.67) * mm});
            skLineSegment(sketch, "E928", {"start": v(-17.4, 21.67) * mm, "end": v(-17.41, 21.69) * mm});
            skLineSegment(sketch, "E929", {"start": v(-17.41, 21.69) * mm, "end": v(-17.43, 21.7) * mm});
            skLineSegment(sketch, "E930", {"start": v(-17.43, 21.7) * mm, "end": v(-17.46, 21.74) * mm});
            skLineSegment(sketch, "E931", {"start": v(-17.46, 21.74) * mm, "end": v(-17.5, 21.78) * mm});
            skLineSegment(sketch, "E932", {"start": v(-17.5, 21.78) * mm, "end": v(-17.55, 21.82) * mm});
            skLineSegment(sketch, "E933", {"start": v(-17.55, 21.82) * mm, "end": v(-17.6, 21.88) * mm});
            skLineSegment(sketch, "E934", {"start": v(-17.6, 21.88) * mm, "end": v(-17.67, 21.94) * mm});
            skLineSegment(sketch, "E935", {"start": v(-17.67, 21.94) * mm, "end": v(-17.75, 22) * mm});
            skLineSegment(sketch, "E936", {"start": v(-17.75, 22) * mm, "end": v(-17.83, 22.08) * mm});
            skLineSegment(sketch, "E937", {"start": v(-17.83, 22.08) * mm, "end": v(-17.93, 22.16) * mm});
            skLineSegment(sketch, "E938", {"start": v(-17.93, 22.16) * mm, "end": v(-18.04, 22.24) * mm});
            skLineSegment(sketch, "E939", {"start": v(-18.04, 22.24) * mm, "end": v(-18.17, 22.33) * mm});
            skLineSegment(sketch, "E940", {"start": v(-18.17, 22.33) * mm, "end": v(-18.3, 22.43) * mm});
            skLineSegment(sketch, "E941", {"start": v(-18.3, 22.43) * mm, "end": v(-18.45, 22.53) * mm});
            skLineSegment(sketch, "E942", {"start": v(-18.45, 22.53) * mm, "end": v(-18.6, 22.63) * mm});
            skLineSegment(sketch, "E943", {"start": v(-18.6, 22.63) * mm, "end": v(-18.77, 22.73) * mm});
            skLineSegment(sketch, "E944", {"start": v(-18.77, 22.73) * mm, "end": v(-18.96, 22.84) * mm});
            skLineSegment(sketch, "E945", {"start": v(-18.96, 22.84) * mm, "end": v(-19.15, 22.95) * mm});
            skLineSegment(sketch, "E946", {"start": v(-19.15, 22.95) * mm, "end": v(-19.36, 23.06) * mm});
            skLineSegment(sketch, "E947", {"start": v(-19.36, 23.06) * mm, "end": v(-19.58, 23.17) * mm});
            skLineSegment(sketch, "E948", {"start": v(-19.58, 23.17) * mm, "end": v(-19.77, 23.26) * mm});
            skLineSegment(sketch, "E949", {"start": v(-19.77, 23.26) * mm, "end": v(-20.45, 22.7) * mm});
            skLineSegment(sketch, "E950", {"start": v(-20.45, 22.7) * mm, "end": v(-21.07, 22.1) * mm});
            skLineSegment(sketch, "E951", {"start": v(-21.07, 22.1) * mm, "end": v(-21, 21.9) * mm});
            skLineSegment(sketch, "E952", {"start": v(-21, 21.9) * mm, "end": v(-20.9, 21.67) * mm});
            skLineSegment(sketch, "E953", {"start": v(-20.9, 21.67) * mm, "end": v(-20.82, 21.45) * mm});
            skLineSegment(sketch, "E954", {"start": v(-20.82, 21.45) * mm, "end": v(-20.73, 21.24) * mm});
            skLineSegment(sketch, "E955", {"start": v(-20.73, 21.24) * mm, "end": v(-20.65, 21.05) * mm});
            skLineSegment(sketch, "E956", {"start": v(-20.65, 21.05) * mm, "end": v(-20.56, 20.87) * mm});
            skLineSegment(sketch, "E957", {"start": v(-20.56, 20.87) * mm, "end": v(-20.47, 20.7) * mm});
            skLineSegment(sketch, "E958", {"start": v(-20.47, 20.7) * mm, "end": v(-20.4, 20.54) * mm});
            skLineSegment(sketch, "E959", {"start": v(-20.4, 20.54) * mm, "end": v(-20.31, 20.4) * mm});
            skLineSegment(sketch, "E960", {"start": v(-20.31, 20.4) * mm, "end": v(-20.24, 20.27) * mm});
            skLineSegment(sketch, "E961", {"start": v(-20.24, 20.27) * mm, "end": v(-20.16, 20.15) * mm});
            skLineSegment(sketch, "E962", {"start": v(-20.16, 20.15) * mm, "end": v(-20.1, 20.04) * mm});
            skLineSegment(sketch, "E963", {"start": v(-20.1, 20.04) * mm, "end": v(-20.03, 19.95) * mm});
            skLineSegment(sketch, "E964", {"start": v(-20.03, 19.95) * mm, "end": v(-19.97, 19.87) * mm});
            skLineSegment(sketch, "E965", {"start": v(-19.97, 19.87) * mm, "end": v(-19.92, 19.8) * mm});
            skLineSegment(sketch, "E966", {"start": v(-19.92, 19.8) * mm, "end": v(-19.87, 19.73) * mm});
            skLineSegment(sketch, "E967", {"start": v(-19.87, 19.73) * mm, "end": v(-19.83, 19.68) * mm});
            skLineSegment(sketch, "E968", {"start": v(-19.83, 19.68) * mm, "end": v(-19.8, 19.64) * mm});
            skLineSegment(sketch, "E969", {"start": v(-19.8, 19.64) * mm, "end": v(-19.77, 19.6) * mm});
            skLineSegment(sketch, "E970", {"start": v(-19.77, 19.6) * mm, "end": v(-19.75, 19.59) * mm});
            skLineSegment(sketch, "E971", {"start": v(-19.75, 19.59) * mm, "end": v(-19.74, 19.57) * mm});
            skLineSegment(sketch, "E972", {"start": v(-19.74, 19.57) * mm, "end": v(-19.73, 19.57) * mm});
            skLineSegment(sketch, "E973", {"start": v(-19.73, 19.57) * mm, "end": v(-19.67, 19.51) * mm});
            skLineSegment(sketch, "E974", {"start": v(-19.67, 19.51) * mm, "end": v(-19.56, 19.4) * mm});
            skLineSegment(sketch, "E975", {"start": v(-19.56, 19.4) * mm, "end": v(-19.46, 19.3) * mm});
            skLineSegment(sketch, "E976", {"start": v(-19.46, 19.3) * mm, "end": v(-19.37, 19.19) * mm});
            skLineSegment(sketch, "E977", {"start": v(-19.37, 19.19) * mm, "end": v(-19.3, 19.1) * mm});
            skLineSegment(sketch, "E978", {"start": v(-19.3, 19.1) * mm, "end": v(-19.24, 19) * mm});
            skLineSegment(sketch, "E979", {"start": v(-19.24, 19) * mm, "end": v(-19.19, 18.91) * mm});
            skLineSegment(sketch, "E980", {"start": v(-19.19, 18.91) * mm, "end": v(-19.15, 18.83) * mm});
            skLineSegment(sketch, "E981", {"start": v(-19.15, 18.83) * mm, "end": v(-19.12, 18.76) * mm});
            skLineSegment(sketch, "E982", {"start": v(-19.12, 18.76) * mm, "end": v(-19.1, 18.7) * mm});
            skLineSegment(sketch, "E983", {"start": v(-19.1, 18.7) * mm, "end": v(-19.1, 18.63) * mm});
            skLineSegment(sketch, "E984", {"start": v(-19.1, 18.63) * mm, "end": v(-19.11, 18.58) * mm});
            skLineSegment(sketch, "E985", {"start": v(-19.11, 18.58) * mm, "end": v(-19.13, 18.54) * mm});
            skLineSegment(sketch, "E986", {"start": v(-19.13, 18.54) * mm, "end": v(-19.16, 18.51) * mm});
            skLineSegment(sketch, "E987", {"start": v(-19.16, 18.51) * mm, "end": v(-19.23, 18.44) * mm});
            skLineSegment(sketch, "E988", {"start": v(-19.23, 18.44) * mm, "end": v(-19.6, 18.03) * mm});
            skLineSegment(sketch, "E989", {"start": v(-19.6, 18.03) * mm, "end": v(-19.98, 17.62) * mm});
            skLineSegment(sketch, "E990", {"start": v(-19.98, 17.62) * mm, "end": v(-20.35, 17.2) * mm});
            skLineSegment(sketch, "E991", {"start": v(-20.35, 17.2) * mm, "end": v(-20.41, 17.12) * mm});
            skLineSegment(sketch, "E992", {"start": v(-20.41, 17.12) * mm, "end": v(-20.44, 17.09) * mm});
            skLineSegment(sketch, "E993", {"start": v(-20.44, 17.09) * mm, "end": v(-20.48, 17.06) * mm});
            skLineSegment(sketch, "E994", {"start": v(-20.48, 17.06) * mm, "end": v(-20.53, 17.05) * mm});
            skLineSegment(sketch, "E995", {"start": v(-20.53, 17.05) * mm, "end": v(-20.59, 17.05) * mm});
            skLineSegment(sketch, "E996", {"start": v(-20.59, 17.05) * mm, "end": v(-20.65, 17.06) * mm});
            skLineSegment(sketch, "E997", {"start": v(-20.65, 17.06) * mm, "end": v(-20.73, 17.08) * mm});
            skLineSegment(sketch, "E998", {"start": v(-20.73, 17.08) * mm, "end": v(-20.81, 17.1) * mm});
            skLineSegment(sketch, "E999", {"start": v(-20.81, 17.1) * mm, "end": v(-20.9, 17.14) * mm});
            skLineSegment(sketch, "E1000", {"start": v(-20.9, 17.14) * mm, "end": v(-21, 17.2) * mm});
            skLineSegment(sketch, "E1001", {"start": v(-21, 17.2) * mm, "end": v(-21.1, 17.26) * mm});
            skLineSegment(sketch, "E1002", {"start": v(-21.1, 17.26) * mm, "end": v(-21.22, 17.33) * mm});
            skLineSegment(sketch, "E1003", {"start": v(-21.22, 17.33) * mm, "end": v(-21.34, 17.42) * mm});
            skLineSegment(sketch, "E1004", {"start": v(-21.34, 17.42) * mm, "end": v(-21.46, 17.52) * mm});
            skLineSegment(sketch, "E1005", {"start": v(-21.46, 17.52) * mm, "end": v(-21.53, 17.58) * mm});
            skLineSegment(sketch, "E1006", {"start": v(-21.53, 17.58) * mm, "end": v(-21.53, 17.58) * mm});
            skLineSegment(sketch, "E1007", {"start": v(-21.53, 17.58) * mm, "end": v(-21.54, 17.6) * mm});
            skLineSegment(sketch, "E1008", {"start": v(-21.54, 17.6) * mm, "end": v(-21.57, 17.6) * mm});
            skLineSegment(sketch, "E1009", {"start": v(-21.57, 17.6) * mm, "end": v(-21.6, 17.63) * mm});
            skLineSegment(sketch, "E1010", {"start": v(-21.6, 17.63) * mm, "end": v(-21.64, 17.66) * mm});
            skLineSegment(sketch, "E1011", {"start": v(-21.64, 17.66) * mm, "end": v(-21.7, 17.7) * mm});
            skLineSegment(sketch, "E1012", {"start": v(-21.7, 17.7) * mm, "end": v(-21.77, 17.74) * mm});
            skLineSegment(sketch, "E1013", {"start": v(-21.77, 17.74) * mm, "end": v(-21.84, 17.79) * mm});
            skLineSegment(sketch, "E1014", {"start": v(-21.84, 17.79) * mm, "end": v(-21.93, 17.84) * mm});
            skLineSegment(sketch, "E1015", {"start": v(-21.93, 17.84) * mm, "end": v(-22.04, 17.89) * mm});
            skLineSegment(sketch, "E1016", {"start": v(-22.04, 17.89) * mm, "end": v(-22.15, 17.95) * mm});
            skLineSegment(sketch, "E1017", {"start": v(-22.15, 17.95) * mm, "end": v(-22.27, 18) * mm});
            skLineSegment(sketch, "E1018", {"start": v(-22.27, 18) * mm, "end": v(-22.41, 18.07) * mm});
            skLineSegment(sketch, "E1019", {"start": v(-22.41, 18.07) * mm, "end": v(-22.56, 18.13) * mm});
            skLineSegment(sketch, "E1020", {"start": v(-22.56, 18.13) * mm, "end": v(-22.73, 18.2) * mm});
            skLineSegment(sketch, "E1021", {"start": v(-22.73, 18.2) * mm, "end": v(-22.9, 18.27) * mm});
            skLineSegment(sketch, "E1022", {"start": v(-22.9, 18.27) * mm, "end": v(-23.09, 18.33) * mm});
            skLineSegment(sketch, "E1023", {"start": v(-23.09, 18.33) * mm, "end": v(-23.3, 18.4) * mm});
            skLineSegment(sketch, "E1024", {"start": v(-23.3, 18.4) * mm, "end": v(-23.5, 18.47) * mm});
            skLineSegment(sketch, "E1025", {"start": v(-23.5, 18.47) * mm, "end": v(-23.73, 18.53) * mm});
            skLineSegment(sketch, "E1026", {"start": v(-23.73, 18.53) * mm, "end": v(-23.97, 18.6) * mm});
            skLineSegment(sketch, "E1027", {"start": v(-23.97, 18.6) * mm, "end": v(-24.17, 18.64) * mm});
            skLineSegment(sketch, "E1028", {"start": v(-24.17, 18.64) * mm, "end": v(-24.72, 17.96) * mm});
            skLineSegment(sketch, "E1029", {"start": v(-24.72, 17.96) * mm, "end": v(-25.2, 17.23) * mm});
            skLineSegment(sketch, "E1030", {"start": v(-25.2, 17.23) * mm, "end": v(-25.1, 17.05) * mm});
            skLineSegment(sketch, "E1031", {"start": v(-25.1, 17.05) * mm, "end": v(-24.96, 16.85) * mm});
            skLineSegment(sketch, "E1032", {"start": v(-24.96, 16.85) * mm, "end": v(-24.83, 16.65) * mm});
            skLineSegment(sketch, "E1033", {"start": v(-24.83, 16.65) * mm, "end": v(-24.7, 16.47) * mm});
            skLineSegment(sketch, "E1034", {"start": v(-24.7, 16.47) * mm, "end": v(-24.57, 16.3) * mm});
            skLineSegment(sketch, "E1035", {"start": v(-24.57, 16.3) * mm, "end": v(-24.45, 16.14) * mm});
            skLineSegment(sketch, "E1036", {"start": v(-24.45, 16.14) * mm, "end": v(-24.33, 15.99) * mm});
            skLineSegment(sketch, "E1037", {"start": v(-24.33, 15.99) * mm, "end": v(-24.22, 15.85) * mm});
            skLineSegment(sketch, "E1038", {"start": v(-24.22, 15.85) * mm, "end": v(-24.11, 15.73) * mm});
            skLineSegment(sketch, "E1039", {"start": v(-24.11, 15.73) * mm, "end": v(-24, 15.62) * mm});
            skLineSegment(sketch, "E1040", {"start": v(-24, 15.62) * mm, "end": v(-23.91, 15.52) * mm});
            skLineSegment(sketch, "E1041", {"start": v(-23.91, 15.52) * mm, "end": v(-23.82, 15.43) * mm});
            skLineSegment(sketch, "E1042", {"start": v(-23.82, 15.43) * mm, "end": v(-23.74, 15.35) * mm});
            skLineSegment(sketch, "E1043", {"start": v(-23.74, 15.35) * mm, "end": v(-23.67, 15.28) * mm});
            skLineSegment(sketch, "E1044", {"start": v(-23.67, 15.28) * mm, "end": v(-23.6, 15.22) * mm});
            skLineSegment(sketch, "E1045", {"start": v(-23.6, 15.22) * mm, "end": v(-23.54, 15.17) * mm});
            skLineSegment(sketch, "E1046", {"start": v(-23.54, 15.17) * mm, "end": v(-23.49, 15.13) * mm});
            skLineSegment(sketch, "E1047", {"start": v(-23.49, 15.13) * mm, "end": v(-23.45, 15.1) * mm});
            skLineSegment(sketch, "E1048", {"start": v(-23.45, 15.1) * mm, "end": v(-23.41, 15.07) * mm});
            skLineSegment(sketch, "E1049", {"start": v(-23.41, 15.07) * mm, "end": v(-23.39, 15.05) * mm});
            skLineSegment(sketch, "E1050", {"start": v(-23.39, 15.05) * mm, "end": v(-23.37, 15.04) * mm});
            skLineSegment(sketch, "E1051", {"start": v(-23.37, 15.04) * mm, "end": v(-23.37, 15.04) * mm});
            skLineSegment(sketch, "E1052", {"start": v(-23.37, 15.04) * mm, "end": v(-23.3, 15) * mm});
            skLineSegment(sketch, "E1053", {"start": v(-23.3, 15) * mm, "end": v(-23.16, 14.91) * mm});
            skLineSegment(sketch, "E1054", {"start": v(-23.16, 14.91) * mm, "end": v(-23.04, 14.83) * mm});
            skLineSegment(sketch, "E1055", {"start": v(-23.04, 14.83) * mm, "end": v(-22.94, 14.74) * mm});
            skLineSegment(sketch, "E1056", {"start": v(-22.94, 14.74) * mm, "end": v(-22.84, 14.66) * mm});
            skLineSegment(sketch, "E1057", {"start": v(-22.84, 14.66) * mm, "end": v(-22.77, 14.58) * mm});
            skLineSegment(sketch, "E1058", {"start": v(-22.77, 14.58) * mm, "end": v(-22.7, 14.5) * mm});
            skLineSegment(sketch, "E1059", {"start": v(-22.7, 14.5) * mm, "end": v(-22.65, 14.44) * mm});
            skLineSegment(sketch, "E1060", {"start": v(-22.65, 14.44) * mm, "end": v(-22.6, 14.37) * mm});
            skLineSegment(sketch, "E1061", {"start": v(-22.6, 14.37) * mm, "end": v(-22.58, 14.31) * mm});
            skLineSegment(sketch, "E1062", {"start": v(-22.58, 14.31) * mm, "end": v(-22.56, 14.25) * mm});
            skLineSegment(sketch, "E1063", {"start": v(-22.56, 14.25) * mm, "end": v(-22.56, 14.2) * mm});
            skLineSegment(sketch, "E1064", {"start": v(-22.56, 14.2) * mm, "end": v(-22.57, 14.16) * mm});
            skLineSegment(sketch, "E1065", {"start": v(-22.57, 14.16) * mm, "end": v(-22.59, 14.12) * mm});
            skLineSegment(sketch, "E1066", {"start": v(-22.59, 14.12) * mm, "end": v(-22.64, 14.04) * mm});
            skLineSegment(sketch, "E1067", {"start": v(-22.64, 14.04) * mm, "end": v(-22.93, 13.56) * mm});
            skLineSegment(sketch, "E1068", {"start": v(-22.93, 13.56) * mm, "end": v(-23.2, 13.08) * mm});
            skLineSegment(sketch, "E1069", {"start": v(-23.2, 13.08) * mm, "end": v(-23.48, 12.59) * mm});
            skLineSegment(sketch, "E1070", {"start": v(-23.48, 12.59) * mm, "end": v(-23.52, 12.5) * mm});
            skLineSegment(sketch, "E1071", {"start": v(-23.52, 12.5) * mm, "end": v(-23.55, 12.46) * mm});
            skLineSegment(sketch, "E1072", {"start": v(-23.55, 12.46) * mm, "end": v(-23.58, 12.43) * mm});
            skLineSegment(sketch, "E1073", {"start": v(-23.58, 12.43) * mm, "end": v(-23.63, 12.41) * mm});
            skLineSegment(sketch, "E1074", {"start": v(-23.63, 12.41) * mm, "end": v(-23.68, 12.4) * mm});
            skLineSegment(sketch, "E1075", {"start": v(-23.68, 12.4) * mm, "end": v(-23.75, 12.4) * mm});
            skLineSegment(sketch, "E1076", {"start": v(-23.75, 12.4) * mm, "end": v(-23.83, 12.4) * mm});
            skLineSegment(sketch, "E1077", {"start": v(-23.83, 12.4) * mm, "end": v(-23.92, 12.4) * mm});
            skLineSegment(sketch, "E1078", {"start": v(-23.92, 12.4) * mm, "end": v(-24.01, 12.42) * mm});
            skLineSegment(sketch, "E1079", {"start": v(-24.01, 12.42) * mm, "end": v(-24.12, 12.45) * mm});
            skLineSegment(sketch, "E1080", {"start": v(-24.12, 12.45) * mm, "end": v(-24.24, 12.5) * mm});
            skLineSegment(sketch, "E1081", {"start": v(-24.24, 12.5) * mm, "end": v(-24.36, 12.54) * mm});
            skLineSegment(sketch, "E1082", {"start": v(-24.36, 12.54) * mm, "end": v(-24.5, 12.6) * mm});
            skLineSegment(sketch, "E1083", {"start": v(-24.5, 12.6) * mm, "end": v(-24.64, 12.68) * mm});
            skLineSegment(sketch, "E1084", {"start": v(-24.64, 12.68) * mm, "end": v(-24.71, 12.72) * mm});
            skLineSegment(sketch, "E1085", {"start": v(-24.71, 12.72) * mm, "end": v(-24.71, 12.72) * mm});
            skLineSegment(sketch, "E1086", {"start": v(-24.71, 12.72) * mm, "end": v(-24.73, 12.73) * mm});
            skLineSegment(sketch, "E1087", {"start": v(-24.73, 12.73) * mm, "end": v(-24.76, 12.74) * mm});
            skLineSegment(sketch, "E1088", {"start": v(-24.76, 12.74) * mm, "end": v(-24.8, 12.76) * mm});
            skLineSegment(sketch, "E1089", {"start": v(-24.8, 12.76) * mm, "end": v(-24.84, 12.78) * mm});
            skLineSegment(sketch, "E1090", {"start": v(-24.84, 12.78) * mm, "end": v(-24.9, 12.8) * mm});
            skLineSegment(sketch, "E1091", {"start": v(-24.9, 12.8) * mm, "end": v(-24.98, 12.83) * mm});
            skLineSegment(sketch, "E1092", {"start": v(-24.98, 12.83) * mm, "end": v(-25.07, 12.86) * mm});
            skLineSegment(sketch, "E1093", {"start": v(-25.07, 12.86) * mm, "end": v(-25.16, 12.89) * mm});
            skLineSegment(sketch, "E1094", {"start": v(-25.16, 12.89) * mm, "end": v(-25.27, 12.92) * mm});
            skLineSegment(sketch, "E1095", {"start": v(-25.27, 12.92) * mm, "end": v(-25.4, 12.95) * mm});
            skLineSegment(sketch, "E1096", {"start": v(-25.4, 12.95) * mm, "end": v(-25.53, 12.98) * mm});
            skLineSegment(sketch, "E1097", {"start": v(-25.53, 12.98) * mm, "end": v(-25.68, 13.01) * mm});
            skLineSegment(sketch, "E1098", {"start": v(-25.68, 13.01) * mm, "end": v(-25.84, 13.05) * mm});
            skLineSegment(sketch, "E1099", {"start": v(-25.84, 13.05) * mm, "end": v(-26.01, 13.08) * mm});
            skLineSegment(sketch, "E1100", {"start": v(-26.01, 13.08) * mm, "end": v(-26.2, 13.1) * mm});
            skLineSegment(sketch, "E1101", {"start": v(-26.2, 13.1) * mm, "end": v(-26.4, 13.13) * mm});
            skLineSegment(sketch, "E1102", {"start": v(-26.4, 13.13) * mm, "end": v(-26.6, 13.15) * mm});
            skLineSegment(sketch, "E1103", {"start": v(-26.6, 13.15) * mm, "end": v(-26.83, 13.17) * mm});
            skLineSegment(sketch, "E1104", {"start": v(-26.83, 13.17) * mm, "end": v(-27.07, 13.2) * mm});
            skLineSegment(sketch, "E1105", {"start": v(-27.07, 13.2) * mm, "end": v(-27.32, 13.2) * mm});
            skLineSegment(sketch, "E1106", {"start": v(-27.32, 13.2) * mm, "end": v(-27.52, 13.2) * mm});
            skLineSegment(sketch, "E1107", {"start": v(-27.52, 13.2) * mm, "end": v(-27.92, 12.43) * mm});
            skLineSegment(sketch, "E1108", {"start": v(-27.92, 12.43) * mm, "end": v(-28.23, 11.61) * mm});
            skLineSegment(sketch, "E1109", {"start": v(-28.23, 11.61) * mm, "end": v(-28.09, 11.47) * mm});
            skLineSegment(sketch, "E1110", {"start": v(-28.09, 11.47) * mm, "end": v(-27.91, 11.29) * mm});
            skLineSegment(sketch, "E1111", {"start": v(-27.91, 11.29) * mm, "end": v(-27.74, 11.12) * mm});
            skLineSegment(sketch, "E1112", {"start": v(-27.74, 11.12) * mm, "end": v(-27.58, 10.97) * mm});
            skLineSegment(sketch, "E1113", {"start": v(-27.58, 10.97) * mm, "end": v(-27.42, 10.83) * mm});
            skLineSegment(sketch, "E1114", {"start": v(-27.42, 10.83) * mm, "end": v(-27.27, 10.7) * mm});
            skLineSegment(sketch, "E1115", {"start": v(-27.27, 10.7) * mm, "end": v(-27.12, 10.58) * mm});
            skLineSegment(sketch, "E1116", {"start": v(-27.12, 10.58) * mm, "end": v(-26.99, 10.47) * mm});
            skLineSegment(sketch, "E1117", {"start": v(-26.99, 10.47) * mm, "end": v(-26.85, 10.38) * mm});
            skLineSegment(sketch, "E1118", {"start": v(-26.85, 10.38) * mm, "end": v(-26.73, 10.29) * mm});
            skLineSegment(sketch, "E1119", {"start": v(-26.73, 10.29) * mm, "end": v(-26.62, 10.2) * mm});
            skLineSegment(sketch, "E1120", {"start": v(-26.62, 10.2) * mm, "end": v(-26.51, 10.14) * mm});
            skLineSegment(sketch, "E1121", {"start": v(-26.51, 10.14) * mm, "end": v(-26.41, 10.08) * mm});
            skLineSegment(sketch, "E1122", {"start": v(-26.41, 10.08) * mm, "end": v(-26.33, 10.03) * mm});
            skLineSegment(sketch, "E1123", {"start": v(-26.33, 10.03) * mm, "end": v(-26.25, 9.98) * mm});
            skLineSegment(sketch, "E1124", {"start": v(-26.25, 9.98) * mm, "end": v(-26.18, 9.94) * mm});
            skLineSegment(sketch, "E1125", {"start": v(-26.18, 9.94) * mm, "end": v(-26.12, 9.91) * mm});
            skLineSegment(sketch, "E1126", {"start": v(-26.12, 9.91) * mm, "end": v(-26.07, 9.89) * mm});
            skLineSegment(sketch, "E1127", {"start": v(-26.07, 9.89) * mm, "end": v(-26.03, 9.87) * mm});
            skLineSegment(sketch, "E1128", {"start": v(-26.03, 9.87) * mm, "end": v(-26, 9.86) * mm});
            skLineSegment(sketch, "E1129", {"start": v(-26, 9.86) * mm, "end": v(-26, 9.85) * mm});
            skLineSegment(sketch, "E1130", {"start": v(-26, 9.85) * mm, "end": v(-25.99, 9.85) * mm});
            skLineSegment(sketch, "E1131", {"start": v(-25.99, 9.85) * mm, "end": v(-25.9, 9.82) * mm});
            skLineSegment(sketch, "E1132", {"start": v(-25.9, 9.82) * mm, "end": v(-25.76, 9.77) * mm});
            skLineSegment(sketch, "E1133", {"start": v(-25.76, 9.77) * mm, "end": v(-25.62, 9.71) * mm});
            skLineSegment(sketch, "E1134", {"start": v(-25.62, 9.71) * mm, "end": v(-25.5, 9.65) * mm});
            skLineSegment(sketch, "E1135", {"start": v(-25.5, 9.65) * mm, "end": v(-25.4, 9.6) * mm});
            skLineSegment(sketch, "E1136", {"start": v(-25.4, 9.6) * mm, "end": v(-25.3, 9.53) * mm});
            skLineSegment(sketch, "E1137", {"start": v(-25.3, 9.53) * mm, "end": v(-25.22, 9.47) * mm});
            skLineSegment(sketch, "E1138", {"start": v(-25.22, 9.47) * mm, "end": v(-25.15, 9.41) * mm});
            skLineSegment(sketch, "E1139", {"start": v(-25.15, 9.41) * mm, "end": v(-25.1, 9.36) * mm});
            skLineSegment(sketch, "E1140", {"start": v(-25.1, 9.36) * mm, "end": v(-25.06, 9.3) * mm});
            skLineSegment(sketch, "E1141", {"start": v(-25.06, 9.3) * mm, "end": v(-25.03, 9.25) * mm});
            skLineSegment(sketch, "E1142", {"start": v(-25.03, 9.25) * mm, "end": v(-25.02, 9.2) * mm});
            skLineSegment(sketch, "E1143", {"start": v(-25.02, 9.2) * mm, "end": v(-25.02, 9.16) * mm});
            skLineSegment(sketch, "E1144", {"start": v(-25.02, 9.16) * mm, "end": v(-25.03, 9.12) * mm});
            skLineSegment(sketch, "E1145", {"start": v(-25.03, 9.12) * mm, "end": v(-25.06, 9.02) * mm});
            skLineSegment(sketch, "E1146", {"start": v(-25.06, 9.02) * mm, "end": v(-25.25, 8.5) * mm});
            skLineSegment(sketch, "E1147", {"start": v(-25.25, 8.5) * mm, "end": v(-25.42, 7.97) * mm});
            skLineSegment(sketch, "E1148", {"start": v(-25.42, 7.97) * mm, "end": v(-25.58, 7.43) * mm});
            skLineSegment(sketch, "E1149", {"start": v(-25.58, 7.43) * mm, "end": v(-25.6, 7.33) * mm});
            skLineSegment(sketch, "E1150", {"start": v(-25.6, 7.33) * mm, "end": v(-25.62, 7.3) * mm});
            skLineSegment(sketch, "E1151", {"start": v(-25.62, 7.3) * mm, "end": v(-25.65, 7.26) * mm});
            skLineSegment(sketch, "E1152", {"start": v(-25.65, 7.26) * mm, "end": v(-25.69, 7.23) * mm});
            skLineSegment(sketch, "E1153", {"start": v(-25.69, 7.23) * mm, "end": v(-25.74, 7.2) * mm});
            skLineSegment(sketch, "E1154", {"start": v(-25.74, 7.2) * mm, "end": v(-25.8, 7.18) * mm});
            skLineSegment(sketch, "E1155", {"start": v(-25.8, 7.18) * mm, "end": v(-25.88, 7.17) * mm});
            skLineSegment(sketch, "E1156", {"start": v(-25.88, 7.17) * mm, "end": v(-25.97, 7.16) * mm});
            skLineSegment(sketch, "E1157", {"start": v(-25.97, 7.16) * mm, "end": v(-26.07, 7.16) * mm});
            skLineSegment(sketch, "E1158", {"start": v(-26.07, 7.16) * mm, "end": v(-26.18, 7.17) * mm});
            skLineSegment(sketch, "E1159", {"start": v(-26.18, 7.17) * mm, "end": v(-26.3, 7.18) * mm});
            skLineSegment(sketch, "E1160", {"start": v(-26.3, 7.18) * mm, "end": v(-26.44, 7.2) * mm});
            skLineSegment(sketch, "E1161", {"start": v(-26.44, 7.2) * mm, "end": v(-26.58, 7.24) * mm});
            skLineSegment(sketch, "E1162", {"start": v(-26.58, 7.24) * mm, "end": v(-26.73, 7.28) * mm});
            skLineSegment(sketch, "E1163", {"start": v(-26.73, 7.28) * mm, "end": v(-26.82, 7.3) * mm});
            skLineSegment(sketch, "E1164", {"start": v(-26.82, 7.3) * mm, "end": v(-26.82, 7.3) * mm});
            skLineSegment(sketch, "E1165", {"start": v(-26.82, 7.3) * mm, "end": v(-26.84, 7.3) * mm});
            skLineSegment(sketch, "E1166", {"start": v(-26.84, 7.3) * mm, "end": v(-26.86, 7.32) * mm});
            skLineSegment(sketch, "E1167", {"start": v(-26.86, 7.32) * mm, "end": v(-26.9, 7.32) * mm});
            skLineSegment(sketch, "E1168", {"start": v(-26.9, 7.32) * mm, "end": v(-26.96, 7.33) * mm});
            skLineSegment(sketch, "E1169", {"start": v(-26.96, 7.33) * mm, "end": v(-27.02, 7.34) * mm});
            skLineSegment(sketch, "E1170", {"start": v(-27.02, 7.34) * mm, "end": v(-27.1, 7.35) * mm});
            skLineSegment(sketch, "E1171", {"start": v(-27.1, 7.35) * mm, "end": v(-27.2, 7.36) * mm});
            skLineSegment(sketch, "E1172", {"start": v(-27.2, 7.36) * mm, "end": v(-27.3, 7.37) * mm});
            skLineSegment(sketch, "E1173", {"start": v(-27.3, 7.37) * mm, "end": v(-27.4, 7.38) * mm});
            skLineSegment(sketch, "E1174", {"start": v(-27.4, 7.38) * mm, "end": v(-27.53, 7.39) * mm});
            skLineSegment(sketch, "E1175", {"start": v(-27.53, 7.39) * mm, "end": v(-27.67, 7.39) * mm});
            skLineSegment(sketch, "E1176", {"start": v(-27.67, 7.39) * mm, "end": v(-27.82, 7.4) * mm});
            skLineSegment(sketch, "E1177", {"start": v(-27.82, 7.4) * mm, "end": v(-27.99, 7.39) * mm});
            skLineSegment(sketch, "E1178", {"start": v(-27.99, 7.39) * mm, "end": v(-28.16, 7.38) * mm});
            skLineSegment(sketch, "E1179", {"start": v(-28.16, 7.38) * mm, "end": v(-28.35, 7.37) * mm});
            skLineSegment(sketch, "E1180", {"start": v(-28.35, 7.37) * mm, "end": v(-28.55, 7.36) * mm});
            skLineSegment(sketch, "E1181", {"start": v(-28.55, 7.36) * mm, "end": v(-28.76, 7.33) * mm});
            skLineSegment(sketch, "E1182", {"start": v(-28.76, 7.33) * mm, "end": v(-28.98, 7.3) * mm});
            skLineSegment(sketch, "E1183", {"start": v(-28.98, 7.3) * mm, "end": v(-29.22, 7.28) * mm});
            skLineSegment(sketch, "E1184", {"start": v(-29.22, 7.28) * mm, "end": v(-29.46, 7.23) * mm});
            skLineSegment(sketch, "E1185", {"start": v(-29.46, 7.23) * mm, "end": v(-29.66, 7.2) * mm});
            skLineSegment(sketch, "E1186", {"start": v(-29.66, 7.2) * mm, "end": v(-29.89, 6.35) * mm});
            skLineSegment(sketch, "E1187", {"start": v(-29.89, 6.35) * mm, "end": v(-30.03, 5.49) * mm});
            skLineSegment(sketch, "E1188", {"start": v(-30.03, 5.49) * mm, "end": v(-29.86, 5.37) * mm});
            skLineSegment(sketch, "E1189", {"start": v(-29.86, 5.37) * mm, "end": v(-29.65, 5.24) * mm});
            skLineSegment(sketch, "E1190", {"start": v(-29.65, 5.24) * mm, "end": v(-29.45, 5.11) * mm});
            skLineSegment(sketch, "E1191", {"start": v(-29.45, 5.11) * mm, "end": v(-29.26, 5) * mm});
            skLineSegment(sketch, "E1192", {"start": v(-29.26, 5) * mm, "end": v(-29.07, 4.9) * mm});
            skLineSegment(sketch, "E1193", {"start": v(-29.07, 4.9) * mm, "end": v(-28.9, 4.8) * mm});
            skLineSegment(sketch, "E1194", {"start": v(-28.9, 4.8) * mm, "end": v(-28.73, 4.71) * mm});
            skLineSegment(sketch, "E1195", {"start": v(-28.73, 4.71) * mm, "end": v(-28.57, 4.63) * mm});
            skLineSegment(sketch, "E1196", {"start": v(-28.57, 4.63) * mm, "end": v(-28.42, 4.57) * mm});
            skLineSegment(sketch, "E1197", {"start": v(-28.42, 4.57) * mm, "end": v(-28.29, 4.5) * mm});
            skLineSegment(sketch, "E1198", {"start": v(-28.29, 4.5) * mm, "end": v(-28.16, 4.45) * mm});
            skLineSegment(sketch, "E1199", {"start": v(-28.16, 4.45) * mm, "end": v(-28.04, 4.4) * mm});
            skLineSegment(sketch, "E1200", {"start": v(-28.04, 4.4) * mm, "end": v(-27.93, 4.37) * mm});
            skLineSegment(sketch, "E1201", {"start": v(-27.93, 4.37) * mm, "end": v(-27.83, 4.33) * mm});
            skLineSegment(sketch, "E1202", {"start": v(-27.83, 4.33) * mm, "end": v(-27.75, 4.3) * mm});
            skLineSegment(sketch, "E1203", {"start": v(-27.75, 4.3) * mm, "end": v(-27.67, 4.28) * mm});
            skLineSegment(sketch, "E1204", {"start": v(-27.67, 4.28) * mm, "end": v(-27.6, 4.27) * mm});
            skLineSegment(sketch, "E1205", {"start": v(-27.6, 4.27) * mm, "end": v(-27.56, 4.25) * mm});
            skLineSegment(sketch, "E1206", {"start": v(-27.56, 4.25) * mm, "end": v(-27.52, 4.24) * mm});
            skLineSegment(sketch, "E1207", {"start": v(-27.52, 4.24) * mm, "end": v(-27.49, 4.24) * mm});
            skLineSegment(sketch, "E1208", {"start": v(-27.49, 4.24) * mm, "end": v(-27.47, 4.23) * mm});
            skLineSegment(sketch, "E1209", {"start": v(-27.47, 4.23) * mm, "end": v(-27.47, 4.23) * mm});
            skLineSegment(sketch, "E1210", {"start": v(-27.47, 4.23) * mm, "end": v(-27.38, 4.22) * mm});
            skLineSegment(sketch, "E1211", {"start": v(-27.38, 4.22) * mm, "end": v(-27.23, 4.2) * mm});
            skLineSegment(sketch, "E1212", {"start": v(-27.23, 4.2) * mm, "end": v(-27.08, 4.17) * mm});
            skLineSegment(sketch, "E1213", {"start": v(-27.08, 4.17) * mm, "end": v(-26.95, 4.14) * mm});
            skLineSegment(sketch, "E1214", {"start": v(-26.95, 4.14) * mm, "end": v(-26.83, 4.1) * mm});
            skLineSegment(sketch, "E1215", {"start": v(-26.83, 4.1) * mm, "end": v(-26.73, 4.06) * mm});
            skLineSegment(sketch, "E1216", {"start": v(-26.73, 4.06) * mm, "end": v(-26.64, 4.02) * mm});
            skLineSegment(sketch, "E1217", {"start": v(-26.64, 4.02) * mm, "end": v(-26.56, 3.98) * mm});
            skLineSegment(sketch, "E1218", {"start": v(-26.56, 3.98) * mm, "end": v(-26.5, 3.94) * mm});
            skLineSegment(sketch, "E1219", {"start": v(-26.5, 3.94) * mm, "end": v(-26.45, 3.9) * mm});
            skLineSegment(sketch, "E1220", {"start": v(-26.45, 3.9) * mm, "end": v(-26.4, 3.85) * mm});
            skLineSegment(sketch, "E1221", {"start": v(-26.4, 3.85) * mm, "end": v(-26.39, 3.8) * mm});
            skLineSegment(sketch, "E1222", {"start": v(-26.39, 3.8) * mm, "end": v(-26.38, 3.76) * mm});
            skLineSegment(sketch, "E1223", {"start": v(-26.38, 3.76) * mm, "end": v(-26.38, 3.72) * mm});
            skLineSegment(sketch, "E1224", {"start": v(-26.38, 3.72) * mm, "end": v(-26.4, 3.62) * mm});
            skLineSegment(sketch, "E1225", {"start": v(-26.4, 3.62) * mm, "end": v(-26.46, 3.06) * mm});
            skLineSegment(sketch, "E1226", {"start": v(-26.46, 3.06) * mm, "end": v(-26.52, 2.5) * mm});
            skLineSegment(sketch, "E1227", {"start": v(-26.52, 2.5) * mm, "end": v(-26.57, 1.95) * mm});
            skLineSegment(sketch, "E1228", {"start": v(-26.57, 1.95) * mm, "end": v(-26.57, 1.85) * mm});
            skLineSegment(sketch, "E1229", {"start": v(-26.57, 1.85) * mm, "end": v(-26.58, 1.8) * mm});
            skLineSegment(sketch, "E1230", {"start": v(-26.58, 1.8) * mm, "end": v(-26.6, 1.77) * mm});
            skLineSegment(sketch, "E1231", {"start": v(-26.6, 1.77) * mm, "end": v(-26.63, 1.73) * mm});
            skLineSegment(sketch, "E1232", {"start": v(-26.63, 1.73) * mm, "end": v(-26.68, 1.7) * mm});
            skLineSegment(sketch, "E1233", {"start": v(-26.68, 1.7) * mm, "end": v(-26.74, 1.66) * mm});
            skLineSegment(sketch, "E1234", {"start": v(-26.74, 1.66) * mm, "end": v(-26.8, 1.63) * mm});
            skLineSegment(sketch, "E1235", {"start": v(-26.8, 1.63) * mm, "end": v(-26.9, 1.6) * mm});
            skLineSegment(sketch, "E1236", {"start": v(-26.9, 1.6) * mm, "end": v(-26.99, 1.58) * mm});
            skLineSegment(sketch, "E1237", {"start": v(-26.99, 1.58) * mm, "end": v(-27.1, 1.57) * mm});
            skLineSegment(sketch, "E1238", {"start": v(-27.1, 1.57) * mm, "end": v(-27.22, 1.56) * mm});
            skLineSegment(sketch, "E1239", {"start": v(-27.22, 1.56) * mm, "end": v(-27.36, 1.55) * mm});
            skLineSegment(sketch, "E1240", {"start": v(-27.36, 1.55) * mm, "end": v(-27.5, 1.55) * mm});
            skLineSegment(sketch, "E1241", {"start": v(-27.5, 1.55) * mm, "end": v(-27.66, 1.56) * mm});
            skLineSegment(sketch, "E1242", {"start": v(-27.66, 1.56) * mm, "end": v(-27.75, 1.57) * mm});
            skLineSegment(sketch, "E1243", {"start": v(-27.75, 1.57) * mm, "end": v(-27.75, 1.57) * mm});
            skLineSegment(sketch, "E1244", {"start": v(-27.75, 1.57) * mm, "end": v(-27.77, 1.57) * mm});
            skLineSegment(sketch, "E1245", {"start": v(-27.77, 1.57) * mm, "end": v(-27.8, 1.57) * mm});
            skLineSegment(sketch, "E1246", {"start": v(-27.8, 1.57) * mm, "end": v(-27.84, 1.57) * mm});
            skLineSegment(sketch, "E1247", {"start": v(-27.84, 1.57) * mm, "end": v(-27.9, 1.57) * mm});
            skLineSegment(sketch, "E1248", {"start": v(-27.9, 1.57) * mm, "end": v(-27.96, 1.56) * mm});
            skLineSegment(sketch, "E1249", {"start": v(-27.96, 1.56) * mm, "end": v(-28.04, 1.56) * mm});
            skLineSegment(sketch, "E1250", {"start": v(-28.04, 1.56) * mm, "end": v(-28.13, 1.55) * mm});
            skLineSegment(sketch, "E1251", {"start": v(-28.13, 1.55) * mm, "end": v(-28.23, 1.54) * mm});
            skLineSegment(sketch, "E1252", {"start": v(-28.23, 1.54) * mm, "end": v(-28.34, 1.52) * mm});
            skLineSegment(sketch, "E1253", {"start": v(-28.34, 1.52) * mm, "end": v(-28.47, 1.5) * mm});
            skLineSegment(sketch, "E1254", {"start": v(-28.47, 1.5) * mm, "end": v(-28.6, 1.48) * mm});
            skLineSegment(sketch, "E1255", {"start": v(-28.6, 1.48) * mm, "end": v(-28.75, 1.44) * mm});
            skLineSegment(sketch, "E1256", {"start": v(-28.75, 1.44) * mm, "end": v(-28.91, 1.4) * mm});
            skLineSegment(sketch, "E1257", {"start": v(-28.91, 1.4) * mm, "end": v(-29.08, 1.37) * mm});
            skLineSegment(sketch, "E1258", {"start": v(-29.08, 1.37) * mm, "end": v(-29.26, 1.32) * mm});
            skLineSegment(sketch, "E1259", {"start": v(-29.26, 1.32) * mm, "end": v(-29.46, 1.26) * mm});
            skLineSegment(sketch, "E1260", {"start": v(-29.46, 1.26) * mm, "end": v(-29.66, 1.2) * mm});
            skLineSegment(sketch, "E1261", {"start": v(-29.66, 1.2) * mm, "end": v(-29.87, 1.12) * mm});
            skLineSegment(sketch, "E1262", {"start": v(-29.87, 1.12) * mm, "end": v(-30.1, 1.04) * mm});
            skLineSegment(sketch, "E1263", {"start": v(-30.1, 1.04) * mm, "end": v(-30.32, 0.95) * mm});
            skLineSegment(sketch, "E1264", {"start": v(-30.32, 0.95) * mm, "end": v(-30.51, 0.87) * mm});
            skLineSegment(sketch, "E1265", {"start": v(-30.51, 0.87) * mm, "end": v(-30.56, 0) * mm});
            skLineSegment(sketch, "E1266", {"start": v(-30.56, 0) * mm, "end": v(-30.51, -0.87) * mm});
            skLineSegment(sketch, "E1267", {"start": v(-30.51, -0.87) * mm, "end": v(-30.32, -0.95) * mm});
            skLineSegment(sketch, "E1268", {"start": v(-30.32, -0.95) * mm, "end": v(-30.1, -1.04) * mm});
            skLineSegment(sketch, "E1269", {"start": v(-30.1, -1.04) * mm, "end": v(-29.87, -1.12) * mm});
            skLineSegment(sketch, "E1270", {"start": v(-29.87, -1.12) * mm, "end": v(-29.66, -1.2) * mm});
            skLineSegment(sketch, "E1271", {"start": v(-29.66, -1.2) * mm, "end": v(-29.46, -1.26) * mm});
            skLineSegment(sketch, "E1272", {"start": v(-29.46, -1.26) * mm, "end": v(-29.26, -1.32) * mm});
            skLineSegment(sketch, "E1273", {"start": v(-29.26, -1.32) * mm, "end": v(-29.08, -1.37) * mm});
            skLineSegment(sketch, "E1274", {"start": v(-29.08, -1.37) * mm, "end": v(-28.91, -1.4) * mm});
            skLineSegment(sketch, "E1275", {"start": v(-28.91, -1.4) * mm, "end": v(-28.75, -1.44) * mm});
            skLineSegment(sketch, "E1276", {"start": v(-28.75, -1.44) * mm, "end": v(-28.6, -1.48) * mm});
            skLineSegment(sketch, "E1277", {"start": v(-28.6, -1.48) * mm, "end": v(-28.47, -1.5) * mm});
            skLineSegment(sketch, "E1278", {"start": v(-28.47, -1.5) * mm, "end": v(-28.34, -1.52) * mm});
            skLineSegment(sketch, "E1279", {"start": v(-28.34, -1.52) * mm, "end": v(-28.23, -1.54) * mm});
            skLineSegment(sketch, "E1280", {"start": v(-28.23, -1.54) * mm, "end": v(-28.13, -1.55) * mm});
            skLineSegment(sketch, "E1281", {"start": v(-28.13, -1.55) * mm, "end": v(-28.04, -1.56) * mm});
            skLineSegment(sketch, "E1282", {"start": v(-28.04, -1.56) * mm, "end": v(-27.96, -1.56) * mm});
            skLineSegment(sketch, "E1283", {"start": v(-27.96, -1.56) * mm, "end": v(-27.9, -1.57) * mm});
            skLineSegment(sketch, "E1284", {"start": v(-27.9, -1.57) * mm, "end": v(-27.84, -1.57) * mm});
            skLineSegment(sketch, "E1285", {"start": v(-27.84, -1.57) * mm, "end": v(-27.8, -1.57) * mm});
            skLineSegment(sketch, "E1286", {"start": v(-27.8, -1.57) * mm, "end": v(-27.77, -1.57) * mm});
            skLineSegment(sketch, "E1287", {"start": v(-27.77, -1.57) * mm, "end": v(-27.75, -1.57) * mm});
            skLineSegment(sketch, "E1288", {"start": v(-27.75, -1.57) * mm, "end": v(-27.75, -1.57) * mm});
            skLineSegment(sketch, "E1289", {"start": v(-27.75, -1.57) * mm, "end": v(-27.66, -1.56) * mm});
            skLineSegment(sketch, "E1290", {"start": v(-27.66, -1.56) * mm, "end": v(-27.5, -1.55) * mm});
            skLineSegment(sketch, "E1291", {"start": v(-27.5, -1.55) * mm, "end": v(-27.36, -1.55) * mm});
            skLineSegment(sketch, "E1292", {"start": v(-27.36, -1.55) * mm, "end": v(-27.22, -1.56) * mm});
            skLineSegment(sketch, "E1293", {"start": v(-27.22, -1.56) * mm, "end": v(-27.1, -1.57) * mm});
            skLineSegment(sketch, "E1294", {"start": v(-27.1, -1.57) * mm, "end": v(-26.99, -1.58) * mm});
            skLineSegment(sketch, "E1295", {"start": v(-26.99, -1.58) * mm, "end": v(-26.9, -1.6) * mm});
            skLineSegment(sketch, "E1296", {"start": v(-26.9, -1.6) * mm, "end": v(-26.8, -1.63) * mm});
            skLineSegment(sketch, "E1297", {"start": v(-26.8, -1.63) * mm, "end": v(-26.74, -1.66) * mm});
            skLineSegment(sketch, "E1298", {"start": v(-26.74, -1.66) * mm, "end": v(-26.68, -1.7) * mm});
            skLineSegment(sketch, "E1299", {"start": v(-26.68, -1.7) * mm, "end": v(-26.63, -1.73) * mm});
            skLineSegment(sketch, "E1300", {"start": v(-26.63, -1.73) * mm, "end": v(-26.6, -1.77) * mm});
            skLineSegment(sketch, "E1301", {"start": v(-26.6, -1.77) * mm, "end": v(-26.58, -1.8) * mm});
            skLineSegment(sketch, "E1302", {"start": v(-26.58, -1.8) * mm, "end": v(-26.57, -1.85) * mm});
            skLineSegment(sketch, "E1303", {"start": v(-26.57, -1.85) * mm, "end": v(-26.57, -1.95) * mm});
            skLineSegment(sketch, "E1304", {"start": v(-26.57, -1.95) * mm, "end": v(-26.52, -2.5) * mm});
            skLineSegment(sketch, "E1305", {"start": v(-26.52, -2.5) * mm, "end": v(-26.46, -3.06) * mm});
            skLineSegment(sketch, "E1306", {"start": v(-26.46, -3.06) * mm, "end": v(-26.4, -3.62) * mm});
            skLineSegment(sketch, "E1307", {"start": v(-26.4, -3.62) * mm, "end": v(-26.38, -3.72) * mm});
            skLineSegment(sketch, "E1308", {"start": v(-26.38, -3.72) * mm, "end": v(-26.38, -3.76) * mm});
            skLineSegment(sketch, "E1309", {"start": v(-26.38, -3.76) * mm, "end": v(-26.39, -3.8) * mm});
            skLineSegment(sketch, "E1310", {"start": v(-26.39, -3.8) * mm, "end": v(-26.4, -3.85) * mm});
            skLineSegment(sketch, "E1311", {"start": v(-26.4, -3.85) * mm, "end": v(-26.45, -3.9) * mm});
            skLineSegment(sketch, "E1312", {"start": v(-26.45, -3.9) * mm, "end": v(-26.5, -3.94) * mm});
            skLineSegment(sketch, "E1313", {"start": v(-26.5, -3.94) * mm, "end": v(-26.56, -3.98) * mm});
            skLineSegment(sketch, "E1314", {"start": v(-26.56, -3.98) * mm, "end": v(-26.64, -4.02) * mm});
            skLineSegment(sketch, "E1315", {"start": v(-26.64, -4.02) * mm, "end": v(-26.73, -4.06) * mm});
            skLineSegment(sketch, "E1316", {"start": v(-26.73, -4.06) * mm, "end": v(-26.83, -4.1) * mm});
            skLineSegment(sketch, "E1317", {"start": v(-26.83, -4.1) * mm, "end": v(-26.95, -4.14) * mm});
            skLineSegment(sketch, "E1318", {"start": v(-26.95, -4.14) * mm, "end": v(-27.08, -4.17) * mm});
            skLineSegment(sketch, "E1319", {"start": v(-27.08, -4.17) * mm, "end": v(-27.23, -4.2) * mm});
            skLineSegment(sketch, "E1320", {"start": v(-27.23, -4.2) * mm, "end": v(-27.38, -4.22) * mm});
            skLineSegment(sketch, "E1321", {"start": v(-27.38, -4.22) * mm, "end": v(-27.47, -4.23) * mm});
            skLineSegment(sketch, "E1322", {"start": v(-27.47, -4.23) * mm, "end": v(-27.47, -4.23) * mm});
            skLineSegment(sketch, "E1323", {"start": v(-27.47, -4.23) * mm, "end": v(-27.49, -4.24) * mm});
            skLineSegment(sketch, "E1324", {"start": v(-27.49, -4.24) * mm, "end": v(-27.52, -4.24) * mm});
            skLineSegment(sketch, "E1325", {"start": v(-27.52, -4.24) * mm, "end": v(-27.56, -4.25) * mm});
            skLineSegment(sketch, "E1326", {"start": v(-27.56, -4.25) * mm, "end": v(-27.6, -4.27) * mm});
            skLineSegment(sketch, "E1327", {"start": v(-27.6, -4.27) * mm, "end": v(-27.67, -4.28) * mm});
            skLineSegment(sketch, "E1328", {"start": v(-27.67, -4.28) * mm, "end": v(-27.75, -4.3) * mm});
            skLineSegment(sketch, "E1329", {"start": v(-27.75, -4.3) * mm, "end": v(-27.83, -4.33) * mm});
            skLineSegment(sketch, "E1330", {"start": v(-27.83, -4.33) * mm, "end": v(-27.93, -4.37) * mm});
            skLineSegment(sketch, "E1331", {"start": v(-27.93, -4.37) * mm, "end": v(-28.04, -4.4) * mm});
            skLineSegment(sketch, "E1332", {"start": v(-28.04, -4.4) * mm, "end": v(-28.16, -4.45) * mm});
            skLineSegment(sketch, "E1333", {"start": v(-28.16, -4.45) * mm, "end": v(-28.29, -4.5) * mm});
            skLineSegment(sketch, "E1334", {"start": v(-28.29, -4.5) * mm, "end": v(-28.42, -4.57) * mm});
            skLineSegment(sketch, "E1335", {"start": v(-28.42, -4.57) * mm, "end": v(-28.57, -4.63) * mm});
            skLineSegment(sketch, "E1336", {"start": v(-28.57, -4.63) * mm, "end": v(-28.73, -4.71) * mm});
            skLineSegment(sketch, "E1337", {"start": v(-28.73, -4.71) * mm, "end": v(-28.9, -4.8) * mm});
            skLineSegment(sketch, "E1338", {"start": v(-28.9, -4.8) * mm, "end": v(-29.07, -4.9) * mm});
            skLineSegment(sketch, "E1339", {"start": v(-29.07, -4.9) * mm, "end": v(-29.26, -5) * mm});
            skLineSegment(sketch, "E1340", {"start": v(-29.26, -5) * mm, "end": v(-29.45, -5.11) * mm});
            skLineSegment(sketch, "E1341", {"start": v(-29.45, -5.11) * mm, "end": v(-29.65, -5.24) * mm});
            skLineSegment(sketch, "E1342", {"start": v(-29.65, -5.24) * mm, "end": v(-29.86, -5.37) * mm});
            skLineSegment(sketch, "E1343", {"start": v(-29.86, -5.37) * mm, "end": v(-30.03, -5.49) * mm});
            skLineSegment(sketch, "E1344", {"start": v(-30.03, -5.49) * mm, "end": v(-29.89, -6.35) * mm});
            skLineSegment(sketch, "E1345", {"start": v(-29.89, -6.35) * mm, "end": v(-29.66, -7.2) * mm});
            skLineSegment(sketch, "E1346", {"start": v(-29.66, -7.2) * mm, "end": v(-29.46, -7.23) * mm});
            skLineSegment(sketch, "E1347", {"start": v(-29.46, -7.23) * mm, "end": v(-29.22, -7.28) * mm});
            skLineSegment(sketch, "E1348", {"start": v(-29.22, -7.28) * mm, "end": v(-28.98, -7.3) * mm});
            skLineSegment(sketch, "E1349", {"start": v(-28.98, -7.3) * mm, "end": v(-28.76, -7.33) * mm});
            skLineSegment(sketch, "E1350", {"start": v(-28.76, -7.33) * mm, "end": v(-28.55, -7.36) * mm});
            skLineSegment(sketch, "E1351", {"start": v(-28.55, -7.36) * mm, "end": v(-28.35, -7.37) * mm});
            skLineSegment(sketch, "E1352", {"start": v(-28.35, -7.37) * mm, "end": v(-28.16, -7.38) * mm});
            skLineSegment(sketch, "E1353", {"start": v(-28.16, -7.38) * mm, "end": v(-27.99, -7.39) * mm});
            skLineSegment(sketch, "E1354", {"start": v(-27.99, -7.39) * mm, "end": v(-27.82, -7.4) * mm});
            skLineSegment(sketch, "E1355", {"start": v(-27.82, -7.4) * mm, "end": v(-27.67, -7.39) * mm});
            skLineSegment(sketch, "E1356", {"start": v(-27.67, -7.39) * mm, "end": v(-27.53, -7.39) * mm});
            skLineSegment(sketch, "E1357", {"start": v(-27.53, -7.39) * mm, "end": v(-27.4, -7.38) * mm});
            skLineSegment(sketch, "E1358", {"start": v(-27.4, -7.38) * mm, "end": v(-27.3, -7.37) * mm});
            skLineSegment(sketch, "E1359", {"start": v(-27.3, -7.37) * mm, "end": v(-27.2, -7.36) * mm});
            skLineSegment(sketch, "E1360", {"start": v(-27.2, -7.36) * mm, "end": v(-27.1, -7.35) * mm});
            skLineSegment(sketch, "E1361", {"start": v(-27.1, -7.35) * mm, "end": v(-27.02, -7.34) * mm});
            skLineSegment(sketch, "E1362", {"start": v(-27.02, -7.34) * mm, "end": v(-26.96, -7.33) * mm});
            skLineSegment(sketch, "E1363", {"start": v(-26.96, -7.33) * mm, "end": v(-26.9, -7.32) * mm});
            skLineSegment(sketch, "E1364", {"start": v(-26.9, -7.32) * mm, "end": v(-26.86, -7.32) * mm});
            skLineSegment(sketch, "E1365", {"start": v(-26.86, -7.32) * mm, "end": v(-26.84, -7.3) * mm});
            skLineSegment(sketch, "E1366", {"start": v(-26.84, -7.3) * mm, "end": v(-26.82, -7.3) * mm});
            skLineSegment(sketch, "E1367", {"start": v(-26.82, -7.3) * mm, "end": v(-26.82, -7.3) * mm});
            skLineSegment(sketch, "E1368", {"start": v(-26.82, -7.3) * mm, "end": v(-26.73, -7.28) * mm});
            skLineSegment(sketch, "E1369", {"start": v(-26.73, -7.28) * mm, "end": v(-26.58, -7.24) * mm});
            skLineSegment(sketch, "E1370", {"start": v(-26.58, -7.24) * mm, "end": v(-26.44, -7.2) * mm});
            skLineSegment(sketch, "E1371", {"start": v(-26.44, -7.2) * mm, "end": v(-26.3, -7.18) * mm});
            skLineSegment(sketch, "E1372", {"start": v(-26.3, -7.18) * mm, "end": v(-26.18, -7.17) * mm});
            skLineSegment(sketch, "E1373", {"start": v(-26.18, -7.17) * mm, "end": v(-26.07, -7.16) * mm});
            skLineSegment(sketch, "E1374", {"start": v(-26.07, -7.16) * mm, "end": v(-25.97, -7.16) * mm});
            skLineSegment(sketch, "E1375", {"start": v(-25.97, -7.16) * mm, "end": v(-25.88, -7.17) * mm});
            skLineSegment(sketch, "E1376", {"start": v(-25.88, -7.17) * mm, "end": v(-25.8, -7.18) * mm});
            skLineSegment(sketch, "E1377", {"start": v(-25.8, -7.18) * mm, "end": v(-25.74, -7.2) * mm});
            skLineSegment(sketch, "E1378", {"start": v(-25.74, -7.2) * mm, "end": v(-25.69, -7.23) * mm});
            skLineSegment(sketch, "E1379", {"start": v(-25.69, -7.23) * mm, "end": v(-25.65, -7.26) * mm});
            skLineSegment(sketch, "E1380", {"start": v(-25.65, -7.26) * mm, "end": v(-25.62, -7.3) * mm});
            skLineSegment(sketch, "E1381", {"start": v(-25.62, -7.3) * mm, "end": v(-25.6, -7.33) * mm});
            skLineSegment(sketch, "E1382", {"start": v(-25.6, -7.33) * mm, "end": v(-25.58, -7.43) * mm});
            skLineSegment(sketch, "E1383", {"start": v(-25.58, -7.43) * mm, "end": v(-25.42, -7.97) * mm});
            skLineSegment(sketch, "E1384", {"start": v(-25.42, -7.97) * mm, "end": v(-25.25, -8.5) * mm});
            skLineSegment(sketch, "E1385", {"start": v(-25.25, -8.5) * mm, "end": v(-25.06, -9.02) * mm});
            skLineSegment(sketch, "E1386", {"start": v(-25.06, -9.02) * mm, "end": v(-25.03, -9.12) * mm});
            skLineSegment(sketch, "E1387", {"start": v(-25.03, -9.12) * mm, "end": v(-25.02, -9.16) * mm});
            skLineSegment(sketch, "E1388", {"start": v(-25.02, -9.16) * mm, "end": v(-25.02, -9.2) * mm});
            skLineSegment(sketch, "E1389", {"start": v(-25.02, -9.2) * mm, "end": v(-25.03, -9.25) * mm});
            skLineSegment(sketch, "E1390", {"start": v(-25.03, -9.25) * mm, "end": v(-25.06, -9.3) * mm});
            skLineSegment(sketch, "E1391", {"start": v(-25.06, -9.3) * mm, "end": v(-25.1, -9.36) * mm});
            skLineSegment(sketch, "E1392", {"start": v(-25.1, -9.36) * mm, "end": v(-25.15, -9.41) * mm});
            skLineSegment(sketch, "E1393", {"start": v(-25.15, -9.41) * mm, "end": v(-25.22, -9.47) * mm});
            skLineSegment(sketch, "E1394", {"start": v(-25.22, -9.47) * mm, "end": v(-25.3, -9.53) * mm});
            skLineSegment(sketch, "E1395", {"start": v(-25.3, -9.53) * mm, "end": v(-25.4, -9.6) * mm});
            skLineSegment(sketch, "E1396", {"start": v(-25.4, -9.6) * mm, "end": v(-25.5, -9.65) * mm});
            skLineSegment(sketch, "E1397", {"start": v(-25.5, -9.65) * mm, "end": v(-25.62, -9.71) * mm});
            skLineSegment(sketch, "E1398", {"start": v(-25.62, -9.71) * mm, "end": v(-25.76, -9.77) * mm});
            skLineSegment(sketch, "E1399", {"start": v(-25.76, -9.77) * mm, "end": v(-25.9, -9.82) * mm});
            skLineSegment(sketch, "E1400", {"start": v(-25.9, -9.82) * mm, "end": v(-25.99, -9.85) * mm});
            skLineSegment(sketch, "E1401", {"start": v(-25.99, -9.85) * mm, "end": v(-26, -9.85) * mm});
            skLineSegment(sketch, "E1402", {"start": v(-26, -9.85) * mm, "end": v(-26, -9.86) * mm});
            skLineSegment(sketch, "E1403", {"start": v(-26, -9.86) * mm, "end": v(-26.03, -9.87) * mm});
            skLineSegment(sketch, "E1404", {"start": v(-26.03, -9.87) * mm, "end": v(-26.07, -9.89) * mm});
            skLineSegment(sketch, "E1405", {"start": v(-26.07, -9.89) * mm, "end": v(-26.12, -9.91) * mm});
            skLineSegment(sketch, "E1406", {"start": v(-26.12, -9.91) * mm, "end": v(-26.18, -9.94) * mm});
            skLineSegment(sketch, "E1407", {"start": v(-26.18, -9.94) * mm, "end": v(-26.25, -9.98) * mm});
            skLineSegment(sketch, "E1408", {"start": v(-26.25, -9.98) * mm, "end": v(-26.33, -10.03) * mm});
            skLineSegment(sketch, "E1409", {"start": v(-26.33, -10.03) * mm, "end": v(-26.41, -10.08) * mm});
            skLineSegment(sketch, "E1410", {"start": v(-26.41, -10.08) * mm, "end": v(-26.51, -10.14) * mm});
            skLineSegment(sketch, "E1411", {"start": v(-26.51, -10.14) * mm, "end": v(-26.62, -10.2) * mm});
            skLineSegment(sketch, "E1412", {"start": v(-26.62, -10.2) * mm, "end": v(-26.73, -10.29) * mm});
            skLineSegment(sketch, "E1413", {"start": v(-26.73, -10.29) * mm, "end": v(-26.85, -10.38) * mm});
            skLineSegment(sketch, "E1414", {"start": v(-26.85, -10.38) * mm, "end": v(-26.99, -10.47) * mm});
            skLineSegment(sketch, "E1415", {"start": v(-26.99, -10.47) * mm, "end": v(-27.12, -10.58) * mm});
            skLineSegment(sketch, "E1416", {"start": v(-27.12, -10.58) * mm, "end": v(-27.27, -10.7) * mm});
            skLineSegment(sketch, "E1417", {"start": v(-27.27, -10.7) * mm, "end": v(-27.42, -10.83) * mm});
            skLineSegment(sketch, "E1418", {"start": v(-27.42, -10.83) * mm, "end": v(-27.58, -10.97) * mm});
            skLineSegment(sketch, "E1419", {"start": v(-27.58, -10.97) * mm, "end": v(-27.74, -11.12) * mm});
            skLineSegment(sketch, "E1420", {"start": v(-27.74, -11.12) * mm, "end": v(-27.91, -11.29) * mm});
            skLineSegment(sketch, "E1421", {"start": v(-27.91, -11.29) * mm, "end": v(-28.09, -11.47) * mm});
            skLineSegment(sketch, "E1422", {"start": v(-28.09, -11.47) * mm, "end": v(-28.23, -11.61) * mm});
            skLineSegment(sketch, "E1423", {"start": v(-28.23, -11.61) * mm, "end": v(-27.92, -12.43) * mm});
            skLineSegment(sketch, "E1424", {"start": v(-27.92, -12.43) * mm, "end": v(-27.52, -13.2) * mm});
            skLineSegment(sketch, "E1425", {"start": v(-27.52, -13.2) * mm, "end": v(-27.32, -13.2) * mm});
            skLineSegment(sketch, "E1426", {"start": v(-27.32, -13.2) * mm, "end": v(-27.07, -13.2) * mm});
            skLineSegment(sketch, "E1427", {"start": v(-27.07, -13.2) * mm, "end": v(-26.83, -13.17) * mm});
            skLineSegment(sketch, "E1428", {"start": v(-26.83, -13.17) * mm, "end": v(-26.6, -13.15) * mm});
            skLineSegment(sketch, "E1429", {"start": v(-26.6, -13.15) * mm, "end": v(-26.4, -13.13) * mm});
            skLineSegment(sketch, "E1430", {"start": v(-26.4, -13.13) * mm, "end": v(-26.2, -13.1) * mm});
            skLineSegment(sketch, "E1431", {"start": v(-26.2, -13.1) * mm, "end": v(-26.01, -13.08) * mm});
            skLineSegment(sketch, "E1432", {"start": v(-26.01, -13.08) * mm, "end": v(-25.84, -13.05) * mm});
            skLineSegment(sketch, "E1433", {"start": v(-25.84, -13.05) * mm, "end": v(-25.68, -13.01) * mm});
            skLineSegment(sketch, "E1434", {"start": v(-25.68, -13.01) * mm, "end": v(-25.53, -12.98) * mm});
            skLineSegment(sketch, "E1435", {"start": v(-25.53, -12.98) * mm, "end": v(-25.4, -12.95) * mm});
            skLineSegment(sketch, "E1436", {"start": v(-25.4, -12.95) * mm, "end": v(-25.27, -12.92) * mm});
            skLineSegment(sketch, "E1437", {"start": v(-25.27, -12.92) * mm, "end": v(-25.16, -12.89) * mm});
            skLineSegment(sketch, "E1438", {"start": v(-25.16, -12.89) * mm, "end": v(-25.07, -12.86) * mm});
            skLineSegment(sketch, "E1439", {"start": v(-25.07, -12.86) * mm, "end": v(-24.98, -12.83) * mm});
            skLineSegment(sketch, "E1440", {"start": v(-24.98, -12.83) * mm, "end": v(-24.9, -12.8) * mm});
            skLineSegment(sketch, "E1441", {"start": v(-24.9, -12.8) * mm, "end": v(-24.84, -12.78) * mm});
            skLineSegment(sketch, "E1442", {"start": v(-24.84, -12.78) * mm, "end": v(-24.8, -12.76) * mm});
            skLineSegment(sketch, "E1443", {"start": v(-24.8, -12.76) * mm, "end": v(-24.76, -12.74) * mm});
            skLineSegment(sketch, "E1444", {"start": v(-24.76, -12.74) * mm, "end": v(-24.73, -12.73) * mm});
            skLineSegment(sketch, "E1445", {"start": v(-24.73, -12.73) * mm, "end": v(-24.71, -12.72) * mm});
            skLineSegment(sketch, "E1446", {"start": v(-24.71, -12.72) * mm, "end": v(-24.71, -12.72) * mm});
            skLineSegment(sketch, "E1447", {"start": v(-24.71, -12.72) * mm, "end": v(-24.64, -12.68) * mm});
            skLineSegment(sketch, "E1448", {"start": v(-24.64, -12.68) * mm, "end": v(-24.5, -12.6) * mm});
            skLineSegment(sketch, "E1449", {"start": v(-24.5, -12.6) * mm, "end": v(-24.36, -12.54) * mm});
            skLineSegment(sketch, "E1450", {"start": v(-24.36, -12.54) * mm, "end": v(-24.24, -12.5) * mm});
            skLineSegment(sketch, "E1451", {"start": v(-24.24, -12.5) * mm, "end": v(-24.12, -12.45) * mm});
            skLineSegment(sketch, "E1452", {"start": v(-24.12, -12.45) * mm, "end": v(-24.01, -12.42) * mm});
            skLineSegment(sketch, "E1453", {"start": v(-24.01, -12.42) * mm, "end": v(-23.92, -12.4) * mm});
            skLineSegment(sketch, "E1454", {"start": v(-23.92, -12.4) * mm, "end": v(-23.83, -12.4) * mm});
            skLineSegment(sketch, "E1455", {"start": v(-23.83, -12.4) * mm, "end": v(-23.75, -12.4) * mm});
            skLineSegment(sketch, "E1456", {"start": v(-23.75, -12.4) * mm, "end": v(-23.68, -12.4) * mm});
            skLineSegment(sketch, "E1457", {"start": v(-23.68, -12.4) * mm, "end": v(-23.63, -12.41) * mm});
            skLineSegment(sketch, "E1458", {"start": v(-23.63, -12.41) * mm, "end": v(-23.58, -12.43) * mm});
            skLineSegment(sketch, "E1459", {"start": v(-23.58, -12.43) * mm, "end": v(-23.55, -12.46) * mm});
            skLineSegment(sketch, "E1460", {"start": v(-23.55, -12.46) * mm, "end": v(-23.52, -12.5) * mm});
            skLineSegment(sketch, "E1461", {"start": v(-23.52, -12.5) * mm, "end": v(-23.48, -12.59) * mm});
            skLineSegment(sketch, "E1462", {"start": v(-23.48, -12.59) * mm, "end": v(-23.2, -13.08) * mm});
            skLineSegment(sketch, "E1463", {"start": v(-23.2, -13.08) * mm, "end": v(-22.93, -13.56) * mm});
            skLineSegment(sketch, "E1464", {"start": v(-22.93, -13.56) * mm, "end": v(-22.64, -14.04) * mm});
            skLineSegment(sketch, "E1465", {"start": v(-22.64, -14.04) * mm, "end": v(-22.59, -14.12) * mm});
            skLineSegment(sketch, "E1466", {"start": v(-22.59, -14.12) * mm, "end": v(-22.57, -14.16) * mm});
            skLineSegment(sketch, "E1467", {"start": v(-22.57, -14.16) * mm, "end": v(-22.56, -14.2) * mm});
            skLineSegment(sketch, "E1468", {"start": v(-22.56, -14.2) * mm, "end": v(-22.56, -14.25) * mm});
            skLineSegment(sketch, "E1469", {"start": v(-22.56, -14.25) * mm, "end": v(-22.58, -14.31) * mm});
            skLineSegment(sketch, "E1470", {"start": v(-22.58, -14.31) * mm, "end": v(-22.6, -14.37) * mm});
            skLineSegment(sketch, "E1471", {"start": v(-22.6, -14.37) * mm, "end": v(-22.65, -14.44) * mm});
            skLineSegment(sketch, "E1472", {"start": v(-22.65, -14.44) * mm, "end": v(-22.7, -14.5) * mm});
            skLineSegment(sketch, "E1473", {"start": v(-22.7, -14.5) * mm, "end": v(-22.77, -14.58) * mm});
            skLineSegment(sketch, "E1474", {"start": v(-22.77, -14.58) * mm, "end": v(-22.84, -14.66) * mm});
            skLineSegment(sketch, "E1475", {"start": v(-22.84, -14.66) * mm, "end": v(-22.94, -14.74) * mm});
            skLineSegment(sketch, "E1476", {"start": v(-22.94, -14.74) * mm, "end": v(-23.04, -14.83) * mm});
            skLineSegment(sketch, "E1477", {"start": v(-23.04, -14.83) * mm, "end": v(-23.16, -14.91) * mm});
            skLineSegment(sketch, "E1478", {"start": v(-23.16, -14.91) * mm, "end": v(-23.3, -15) * mm});
            skLineSegment(sketch, "E1479", {"start": v(-23.3, -15) * mm, "end": v(-23.37, -15.04) * mm});
            skLineSegment(sketch, "E1480", {"start": v(-23.37, -15.04) * mm, "end": v(-23.37, -15.04) * mm});
            skLineSegment(sketch, "E1481", {"start": v(-23.37, -15.04) * mm, "end": v(-23.39, -15.05) * mm});
            skLineSegment(sketch, "E1482", {"start": v(-23.39, -15.05) * mm, "end": v(-23.41, -15.07) * mm});
            skLineSegment(sketch, "E1483", {"start": v(-23.41, -15.07) * mm, "end": v(-23.45, -15.1) * mm});
            skLineSegment(sketch, "E1484", {"start": v(-23.45, -15.1) * mm, "end": v(-23.49, -15.13) * mm});
            skLineSegment(sketch, "E1485", {"start": v(-23.49, -15.13) * mm, "end": v(-23.54, -15.17) * mm});
            skLineSegment(sketch, "E1486", {"start": v(-23.54, -15.17) * mm, "end": v(-23.6, -15.22) * mm});
            skLineSegment(sketch, "E1487", {"start": v(-23.6, -15.22) * mm, "end": v(-23.67, -15.28) * mm});
            skLineSegment(sketch, "E1488", {"start": v(-23.67, -15.28) * mm, "end": v(-23.74, -15.35) * mm});
            skLineSegment(sketch, "E1489", {"start": v(-23.74, -15.35) * mm, "end": v(-23.82, -15.43) * mm});
            skLineSegment(sketch, "E1490", {"start": v(-23.82, -15.43) * mm, "end": v(-23.91, -15.52) * mm});
            skLineSegment(sketch, "E1491", {"start": v(-23.91, -15.52) * mm, "end": v(-24, -15.62) * mm});
            skLineSegment(sketch, "E1492", {"start": v(-24, -15.62) * mm, "end": v(-24.11, -15.73) * mm});
            skLineSegment(sketch, "E1493", {"start": v(-24.11, -15.73) * mm, "end": v(-24.22, -15.85) * mm});
            skLineSegment(sketch, "E1494", {"start": v(-24.22, -15.85) * mm, "end": v(-24.33, -15.99) * mm});
            skLineSegment(sketch, "E1495", {"start": v(-24.33, -15.99) * mm, "end": v(-24.45, -16.14) * mm});
            skLineSegment(sketch, "E1496", {"start": v(-24.45, -16.14) * mm, "end": v(-24.57, -16.3) * mm});
            skLineSegment(sketch, "E1497", {"start": v(-24.57, -16.3) * mm, "end": v(-24.7, -16.47) * mm});
            skLineSegment(sketch, "E1498", {"start": v(-24.7, -16.47) * mm, "end": v(-24.83, -16.65) * mm});
            skLineSegment(sketch, "E1499", {"start": v(-24.83, -16.65) * mm, "end": v(-24.96, -16.85) * mm});
            skLineSegment(sketch, "E1500", {"start": v(-24.96, -16.85) * mm, "end": v(-25.1, -17.05) * mm});
            skLineSegment(sketch, "E1501", {"start": v(-25.1, -17.05) * mm, "end": v(-25.2, -17.23) * mm});
            skLineSegment(sketch, "E1502", {"start": v(-25.2, -17.23) * mm, "end": v(-24.72, -17.96) * mm});
            skLineSegment(sketch, "E1503", {"start": v(-24.72, -17.96) * mm, "end": v(-24.17, -18.64) * mm});
            skLineSegment(sketch, "E1504", {"start": v(-24.17, -18.64) * mm, "end": v(-23.97, -18.6) * mm});
            skLineSegment(sketch, "E1505", {"start": v(-23.97, -18.6) * mm, "end": v(-23.73, -18.53) * mm});
            skLineSegment(sketch, "E1506", {"start": v(-23.73, -18.53) * mm, "end": v(-23.5, -18.47) * mm});
            skLineSegment(sketch, "E1507", {"start": v(-23.5, -18.47) * mm, "end": v(-23.3, -18.4) * mm});
            skLineSegment(sketch, "E1508", {"start": v(-23.3, -18.4) * mm, "end": v(-23.09, -18.33) * mm});
            skLineSegment(sketch, "E1509", {"start": v(-23.09, -18.33) * mm, "end": v(-22.9, -18.27) * mm});
            skLineSegment(sketch, "E1510", {"start": v(-22.9, -18.27) * mm, "end": v(-22.73, -18.2) * mm});
            skLineSegment(sketch, "E1511", {"start": v(-22.73, -18.2) * mm, "end": v(-22.56, -18.13) * mm});
            skLineSegment(sketch, "E1512", {"start": v(-22.56, -18.13) * mm, "end": v(-22.41, -18.07) * mm});
            skLineSegment(sketch, "E1513", {"start": v(-22.41, -18.07) * mm, "end": v(-22.27, -18) * mm});
            skLineSegment(sketch, "E1514", {"start": v(-22.27, -18) * mm, "end": v(-22.15, -17.95) * mm});
            skLineSegment(sketch, "E1515", {"start": v(-22.15, -17.95) * mm, "end": v(-22.04, -17.89) * mm});
            skLineSegment(sketch, "E1516", {"start": v(-22.04, -17.89) * mm, "end": v(-21.93, -17.84) * mm});
            skLineSegment(sketch, "E1517", {"start": v(-21.93, -17.84) * mm, "end": v(-21.84, -17.79) * mm});
            skLineSegment(sketch, "E1518", {"start": v(-21.84, -17.79) * mm, "end": v(-21.77, -17.74) * mm});
            skLineSegment(sketch, "E1519", {"start": v(-21.77, -17.74) * mm, "end": v(-21.7, -17.7) * mm});
            skLineSegment(sketch, "E1520", {"start": v(-21.7, -17.7) * mm, "end": v(-21.64, -17.66) * mm});
            skLineSegment(sketch, "E1521", {"start": v(-21.64, -17.66) * mm, "end": v(-21.6, -17.63) * mm});
            skLineSegment(sketch, "E1522", {"start": v(-21.6, -17.63) * mm, "end": v(-21.57, -17.6) * mm});
            skLineSegment(sketch, "E1523", {"start": v(-21.57, -17.6) * mm, "end": v(-21.54, -17.6) * mm});
            skLineSegment(sketch, "E1524", {"start": v(-21.54, -17.6) * mm, "end": v(-21.53, -17.58) * mm});
            skLineSegment(sketch, "E1525", {"start": v(-21.53, -17.58) * mm, "end": v(-21.53, -17.58) * mm});
            skLineSegment(sketch, "E1526", {"start": v(-21.53, -17.58) * mm, "end": v(-21.46, -17.52) * mm});
            skLineSegment(sketch, "E1527", {"start": v(-21.46, -17.52) * mm, "end": v(-21.34, -17.42) * mm});
            skLineSegment(sketch, "E1528", {"start": v(-21.34, -17.42) * mm, "end": v(-21.22, -17.33) * mm});
            skLineSegment(sketch, "E1529", {"start": v(-21.22, -17.33) * mm, "end": v(-21.1, -17.26) * mm});
            skLineSegment(sketch, "E1530", {"start": v(-21.1, -17.26) * mm, "end": v(-21, -17.2) * mm});
            skLineSegment(sketch, "E1531", {"start": v(-21, -17.2) * mm, "end": v(-20.9, -17.14) * mm});
            skLineSegment(sketch, "E1532", {"start": v(-20.9, -17.14) * mm, "end": v(-20.81, -17.1) * mm});
            skLineSegment(sketch, "E1533", {"start": v(-20.81, -17.1) * mm, "end": v(-20.73, -17.08) * mm});
            skLineSegment(sketch, "E1534", {"start": v(-20.73, -17.08) * mm, "end": v(-20.65, -17.06) * mm});
            skLineSegment(sketch, "E1535", {"start": v(-20.65, -17.06) * mm, "end": v(-20.59, -17.05) * mm});
            skLineSegment(sketch, "E1536", {"start": v(-20.59, -17.05) * mm, "end": v(-20.53, -17.05) * mm});
            skLineSegment(sketch, "E1537", {"start": v(-20.53, -17.05) * mm, "end": v(-20.48, -17.06) * mm});
            skLineSegment(sketch, "E1538", {"start": v(-20.48, -17.06) * mm, "end": v(-20.44, -17.09) * mm});
            skLineSegment(sketch, "E1539", {"start": v(-20.44, -17.09) * mm, "end": v(-20.41, -17.12) * mm});
            skLineSegment(sketch, "E1540", {"start": v(-20.41, -17.12) * mm, "end": v(-20.35, -17.2) * mm});
            skLineSegment(sketch, "E1541", {"start": v(-20.35, -17.2) * mm, "end": v(-19.98, -17.62) * mm});
            skLineSegment(sketch, "E1542", {"start": v(-19.98, -17.62) * mm, "end": v(-19.6, -18.03) * mm});
            skLineSegment(sketch, "E1543", {"start": v(-19.6, -18.03) * mm, "end": v(-19.23, -18.44) * mm});
            skLineSegment(sketch, "E1544", {"start": v(-19.23, -18.44) * mm, "end": v(-19.16, -18.51) * mm});
            skLineSegment(sketch, "E1545", {"start": v(-19.16, -18.51) * mm, "end": v(-19.13, -18.54) * mm});
            skLineSegment(sketch, "E1546", {"start": v(-19.13, -18.54) * mm, "end": v(-19.11, -18.58) * mm});
            skLineSegment(sketch, "E1547", {"start": v(-19.11, -18.58) * mm, "end": v(-19.1, -18.63) * mm});
            skLineSegment(sketch, "E1548", {"start": v(-19.1, -18.63) * mm, "end": v(-19.1, -18.7) * mm});
            skLineSegment(sketch, "E1549", {"start": v(-19.1, -18.7) * mm, "end": v(-19.12, -18.76) * mm});
            skLineSegment(sketch, "E1550", {"start": v(-19.12, -18.76) * mm, "end": v(-19.15, -18.83) * mm});
            skLineSegment(sketch, "E1551", {"start": v(-19.15, -18.83) * mm, "end": v(-19.19, -18.91) * mm});
            skLineSegment(sketch, "E1552", {"start": v(-19.19, -18.91) * mm, "end": v(-19.24, -19) * mm});
            skLineSegment(sketch, "E1553", {"start": v(-19.24, -19) * mm, "end": v(-19.3, -19.1) * mm});
            skLineSegment(sketch, "E1554", {"start": v(-19.3, -19.1) * mm, "end": v(-19.37, -19.19) * mm});
            skLineSegment(sketch, "E1555", {"start": v(-19.37, -19.19) * mm, "end": v(-19.46, -19.3) * mm});
            skLineSegment(sketch, "E1556", {"start": v(-19.46, -19.3) * mm, "end": v(-19.56, -19.4) * mm});
            skLineSegment(sketch, "E1557", {"start": v(-19.56, -19.4) * mm, "end": v(-19.67, -19.51) * mm});
            skLineSegment(sketch, "E1558", {"start": v(-19.67, -19.51) * mm, "end": v(-19.73, -19.57) * mm});
            skLineSegment(sketch, "E1559", {"start": v(-19.73, -19.57) * mm, "end": v(-19.74, -19.57) * mm});
            skLineSegment(sketch, "E1560", {"start": v(-19.74, -19.57) * mm, "end": v(-19.75, -19.59) * mm});
            skLineSegment(sketch, "E1561", {"start": v(-19.75, -19.59) * mm, "end": v(-19.77, -19.6) * mm});
            skLineSegment(sketch, "E1562", {"start": v(-19.77, -19.6) * mm, "end": v(-19.8, -19.64) * mm});
            skLineSegment(sketch, "E1563", {"start": v(-19.8, -19.64) * mm, "end": v(-19.83, -19.68) * mm});
            skLineSegment(sketch, "E1564", {"start": v(-19.83, -19.68) * mm, "end": v(-19.87, -19.73) * mm});
            skLineSegment(sketch, "E1565", {"start": v(-19.87, -19.73) * mm, "end": v(-19.92, -19.8) * mm});
            skLineSegment(sketch, "E1566", {"start": v(-19.92, -19.8) * mm, "end": v(-19.97, -19.87) * mm});
            skLineSegment(sketch, "E1567", {"start": v(-19.97, -19.87) * mm, "end": v(-20.03, -19.95) * mm});
            skLineSegment(sketch, "E1568", {"start": v(-20.03, -19.95) * mm, "end": v(-20.1, -20.04) * mm});
            skLineSegment(sketch, "E1569", {"start": v(-20.1, -20.04) * mm, "end": v(-20.16, -20.15) * mm});
            skLineSegment(sketch, "E1570", {"start": v(-20.16, -20.15) * mm, "end": v(-20.24, -20.27) * mm});
            skLineSegment(sketch, "E1571", {"start": v(-20.24, -20.27) * mm, "end": v(-20.31, -20.4) * mm});
            skLineSegment(sketch, "E1572", {"start": v(-20.31, -20.4) * mm, "end": v(-20.4, -20.54) * mm});
            skLineSegment(sketch, "E1573", {"start": v(-20.4, -20.54) * mm, "end": v(-20.47, -20.7) * mm});
            skLineSegment(sketch, "E1574", {"start": v(-20.47, -20.7) * mm, "end": v(-20.56, -20.87) * mm});
            skLineSegment(sketch, "E1575", {"start": v(-20.56, -20.87) * mm, "end": v(-20.65, -21.05) * mm});
            skLineSegment(sketch, "E1576", {"start": v(-20.65, -21.05) * mm, "end": v(-20.73, -21.24) * mm});
            skLineSegment(sketch, "E1577", {"start": v(-20.73, -21.24) * mm, "end": v(-20.82, -21.45) * mm});
            skLineSegment(sketch, "E1578", {"start": v(-20.82, -21.45) * mm, "end": v(-20.9, -21.67) * mm});
            skLineSegment(sketch, "E1579", {"start": v(-20.9, -21.67) * mm, "end": v(-21, -21.9) * mm});
            skLineSegment(sketch, "E1580", {"start": v(-21, -21.9) * mm, "end": v(-21.07, -22.1) * mm});
            skLineSegment(sketch, "E1581", {"start": v(-21.07, -22.1) * mm, "end": v(-20.45, -22.7) * mm});
            skLineSegment(sketch, "E1582", {"start": v(-20.45, -22.7) * mm, "end": v(-19.77, -23.26) * mm});
            skLineSegment(sketch, "E1583", {"start": v(-19.77, -23.26) * mm, "end": v(-19.58, -23.17) * mm});
            skLineSegment(sketch, "E1584", {"start": v(-19.58, -23.17) * mm, "end": v(-19.36, -23.06) * mm});
            skLineSegment(sketch, "E1585", {"start": v(-19.36, -23.06) * mm, "end": v(-19.15, -22.95) * mm});
            skLineSegment(sketch, "E1586", {"start": v(-19.15, -22.95) * mm, "end": v(-18.96, -22.84) * mm});
            skLineSegment(sketch, "E1587", {"start": v(-18.96, -22.84) * mm, "end": v(-18.77, -22.73) * mm});
            skLineSegment(sketch, "E1588", {"start": v(-18.77, -22.73) * mm, "end": v(-18.6, -22.63) * mm});
            skLineSegment(sketch, "E1589", {"start": v(-18.6, -22.63) * mm, "end": v(-18.45, -22.53) * mm});
            skLineSegment(sketch, "E1590", {"start": v(-18.45, -22.53) * mm, "end": v(-18.3, -22.43) * mm});
            skLineSegment(sketch, "E1591", {"start": v(-18.3, -22.43) * mm, "end": v(-18.17, -22.33) * mm});
            skLineSegment(sketch, "E1592", {"start": v(-18.17, -22.33) * mm, "end": v(-18.04, -22.24) * mm});
            skLineSegment(sketch, "E1593", {"start": v(-18.04, -22.24) * mm, "end": v(-17.93, -22.16) * mm});
            skLineSegment(sketch, "E1594", {"start": v(-17.93, -22.16) * mm, "end": v(-17.83, -22.08) * mm});
            skLineSegment(sketch, "E1595", {"start": v(-17.83, -22.08) * mm, "end": v(-17.75, -22) * mm});
            skLineSegment(sketch, "E1596", {"start": v(-17.75, -22) * mm, "end": v(-17.67, -21.94) * mm});
            skLineSegment(sketch, "E1597", {"start": v(-17.67, -21.94) * mm, "end": v(-17.6, -21.88) * mm});
            skLineSegment(sketch, "E1598", {"start": v(-17.6, -21.88) * mm, "end": v(-17.55, -21.82) * mm});
            skLineSegment(sketch, "E1599", {"start": v(-17.55, -21.82) * mm, "end": v(-17.5, -21.78) * mm});
            skLineSegment(sketch, "E1600", {"start": v(-17.5, -21.78) * mm, "end": v(-17.46, -21.74) * mm});
            skLineSegment(sketch, "E1601", {"start": v(-17.46, -21.74) * mm, "end": v(-17.43, -21.7) * mm});
            skLineSegment(sketch, "E1602", {"start": v(-17.43, -21.7) * mm, "end": v(-17.41, -21.69) * mm});
            skLineSegment(sketch, "E1603", {"start": v(-17.41, -21.69) * mm, "end": v(-17.4, -21.67) * mm});
            skLineSegment(sketch, "E1604", {"start": v(-17.4, -21.67) * mm, "end": v(-17.4, -21.67) * mm});
            skLineSegment(sketch, "E1605", {"start": v(-17.4, -21.67) * mm, "end": v(-17.35, -21.6) * mm});
            skLineSegment(sketch, "E1606", {"start": v(-17.35, -21.6) * mm, "end": v(-17.25, -21.48) * mm});
            skLineSegment(sketch, "E1607", {"start": v(-17.25, -21.48) * mm, "end": v(-17.15, -21.37) * mm});
            skLineSegment(sketch, "E1608", {"start": v(-17.15, -21.37) * mm, "end": v(-17.06, -21.27) * mm});
            skLineSegment(sketch, "E1609", {"start": v(-17.06, -21.27) * mm, "end": v(-16.97, -21.19) * mm});
            skLineSegment(sketch, "E1610", {"start": v(-16.97, -21.19) * mm, "end": v(-16.88, -21.12) * mm});
            skLineSegment(sketch, "E1611", {"start": v(-16.88, -21.12) * mm, "end": v(-16.8, -21.06) * mm});
            skLineSegment(sketch, "E1612", {"start": v(-16.8, -21.06) * mm, "end": v(-16.73, -21.01) * mm});
            skLineSegment(sketch, "E1613", {"start": v(-16.73, -21.01) * mm, "end": v(-16.66, -20.98) * mm});
            skLineSegment(sketch, "E1614", {"start": v(-16.66, -20.98) * mm, "end": v(-16.6, -20.96) * mm});
            skLineSegment(sketch, "E1615", {"start": v(-16.6, -20.96) * mm, "end": v(-16.54, -20.95) * mm});
            skLineSegment(sketch, "E1616", {"start": v(-16.54, -20.95) * mm, "end": v(-16.48, -20.95) * mm});
            skLineSegment(sketch, "E1617", {"start": v(-16.48, -20.95) * mm, "end": v(-16.44, -20.96) * mm});
            skLineSegment(sketch, "E1618", {"start": v(-16.44, -20.96) * mm, "end": v(-16.4, -20.99) * mm});
            skLineSegment(sketch, "E1619", {"start": v(-16.4, -20.99) * mm, "end": v(-16.33, -21.05) * mm});
            skLineSegment(sketch, "E1620", {"start": v(-16.33, -21.05) * mm, "end": v(-15.88, -21.39) * mm});
            skLineSegment(sketch, "E1621", {"start": v(-15.88, -21.39) * mm, "end": v(-15.43, -21.71) * mm});
            skLineSegment(sketch, "E1622", {"start": v(-15.43, -21.71) * mm, "end": v(-14.97, -22.03) * mm});
            skLineSegment(sketch, "E1623", {"start": v(-14.97, -22.03) * mm, "end": v(-14.89, -22.09) * mm});
            skLineSegment(sketch, "E1624", {"start": v(-14.89, -22.09) * mm, "end": v(-14.86, -22.11) * mm});
            skLineSegment(sketch, "E1625", {"start": v(-14.86, -22.11) * mm, "end": v(-14.83, -22.15) * mm});
            skLineSegment(sketch, "E1626", {"start": v(-14.83, -22.15) * mm, "end": v(-14.81, -22.2) * mm});
            skLineSegment(sketch, "E1627", {"start": v(-14.81, -22.2) * mm, "end": v(-14.8, -22.26) * mm});
            skLineSegment(sketch, "E1628", {"start": v(-14.8, -22.26) * mm, "end": v(-14.8, -22.32) * mm});
            skLineSegment(sketch, "E1629", {"start": v(-14.8, -22.32) * mm, "end": v(-14.81, -22.4) * mm});
            skLineSegment(sketch, "E1630", {"start": v(-14.81, -22.4) * mm, "end": v(-14.83, -22.49) * mm});
            skLineSegment(sketch, "E1631", {"start": v(-14.83, -22.49) * mm, "end": v(-14.87, -22.58) * mm});
            skLineSegment(sketch, "E1632", {"start": v(-14.87, -22.58) * mm, "end": v(-14.9, -22.69) * mm});
            skLineSegment(sketch, "E1633", {"start": v(-14.9, -22.69) * mm, "end": v(-14.96, -22.8) * mm});
            skLineSegment(sketch, "E1634", {"start": v(-14.96, -22.8) * mm, "end": v(-15.02, -22.92) * mm});
            skLineSegment(sketch, "E1635", {"start": v(-15.02, -22.92) * mm, "end": v(-15.1, -23.04) * mm});
            skLineSegment(sketch, "E1636", {"start": v(-15.1, -23.04) * mm, "end": v(-15.18, -23.18) * mm});
            skLineSegment(sketch, "E1637", {"start": v(-15.18, -23.18) * mm, "end": v(-15.23, -23.25) * mm});
            skLineSegment(sketch, "E1638", {"start": v(-15.23, -23.25) * mm, "end": v(-15.23, -23.25) * mm});
            skLineSegment(sketch, "E1639", {"start": v(-15.23, -23.25) * mm, "end": v(-15.24, -23.26) * mm});
            skLineSegment(sketch, "E1640", {"start": v(-15.24, -23.26) * mm, "end": v(-15.26, -23.29) * mm});
            skLineSegment(sketch, "E1641", {"start": v(-15.26, -23.29) * mm, "end": v(-15.28, -23.32) * mm});
            skLineSegment(sketch, "E1642", {"start": v(-15.28, -23.32) * mm, "end": v(-15.3, -23.37) * mm});
            skLineSegment(sketch, "E1643", {"start": v(-15.3, -23.37) * mm, "end": v(-15.33, -23.43) * mm});
            skLineSegment(sketch, "E1644", {"start": v(-15.33, -23.43) * mm, "end": v(-15.37, -23.5) * mm});
            skLineSegment(sketch, "E1645", {"start": v(-15.37, -23.5) * mm, "end": v(-15.4, -23.58) * mm});
            skLineSegment(sketch, "E1646", {"start": v(-15.4, -23.58) * mm, "end": v(-15.45, -23.68) * mm});
            skLineSegment(sketch, "E1647", {"start": v(-15.45, -23.68) * mm, "end": v(-15.49, -23.78) * mm});
            skLineSegment(sketch, "E1648", {"start": v(-15.49, -23.78) * mm, "end": v(-15.53, -23.9) * mm});
            skLineSegment(sketch, "E1649", {"start": v(-15.53, -23.9) * mm, "end": v(-15.58, -24.03) * mm});
            skLineSegment(sketch, "E1650", {"start": v(-15.58, -24.03) * mm, "end": v(-15.63, -24.18) * mm});
            skLineSegment(sketch, "E1651", {"start": v(-15.63, -24.18) * mm, "end": v(-15.68, -24.33) * mm});
            skLineSegment(sketch, "E1652", {"start": v(-15.68, -24.33) * mm, "end": v(-15.72, -24.5) * mm});
            skLineSegment(sketch, "E1653", {"start": v(-15.72, -24.5) * mm, "end": v(-15.77, -24.69) * mm});
            skLineSegment(sketch, "E1654", {"start": v(-15.77, -24.69) * mm, "end": v(-15.82, -24.88) * mm});
            skLineSegment(sketch, "E1655", {"start": v(-15.82, -24.88) * mm, "end": v(-15.86, -25.09) * mm});
            skLineSegment(sketch, "E1656", {"start": v(-15.86, -25.09) * mm, "end": v(-15.9, -25.3) * mm});
            skLineSegment(sketch, "E1657", {"start": v(-15.9, -25.3) * mm, "end": v(-15.95, -25.54) * mm});
            skLineSegment(sketch, "E1658", {"start": v(-15.95, -25.54) * mm, "end": v(-15.99, -25.79) * mm});
            skLineSegment(sketch, "E1659", {"start": v(-15.99, -25.79) * mm, "end": v(-16.01, -25.99) * mm});
            skLineSegment(sketch, "E1660", {"start": v(-16.01, -25.99) * mm, "end": v(-15.28, -26.46) * mm});
            skLineSegment(sketch, "E1661", {"start": v(-15.28, -26.46) * mm, "end": v(-14.5, -26.86) * mm});
            skLineSegment(sketch, "E1662", {"start": v(-14.5, -26.86) * mm, "end": v(-14.34, -26.74) * mm});
            skLineSegment(sketch, "E1663", {"start": v(-14.34, -26.74) * mm, "end": v(-14.14, -26.58) * mm});
            skLineSegment(sketch, "E1664", {"start": v(-14.14, -26.58) * mm, "end": v(-13.96, -26.43) * mm});
            skLineSegment(sketch, "E1665", {"start": v(-13.96, -26.43) * mm, "end": v(-13.8, -26.28) * mm});
            skLineSegment(sketch, "E1666", {"start": v(-13.8, -26.28) * mm, "end": v(-13.64, -26.14) * mm});
            skLineSegment(sketch, "E1667", {"start": v(-13.64, -26.14) * mm, "end": v(-13.5, -26) * mm});
            skLineSegment(sketch, "E1668", {"start": v(-13.5, -26) * mm, "end": v(-13.36, -25.87) * mm});
            skLineSegment(sketch, "E1669", {"start": v(-13.36, -25.87) * mm, "end": v(-13.24, -25.74) * mm});
            skLineSegment(sketch, "E1670", {"start": v(-13.24, -25.74) * mm, "end": v(-13.13, -25.62) * mm});
            skLineSegment(sketch, "E1671", {"start": v(-13.13, -25.62) * mm, "end": v(-13.02, -25.5) * mm});
            skLineSegment(sketch, "E1672", {"start": v(-13.02, -25.5) * mm, "end": v(-12.93, -25.4) * mm});
            skLineSegment(sketch, "E1673", {"start": v(-12.93, -25.4) * mm, "end": v(-12.85, -25.3) * mm});
            skLineSegment(sketch, "E1674", {"start": v(-12.85, -25.3) * mm, "end": v(-12.78, -25.22) * mm});
            skLineSegment(sketch, "E1675", {"start": v(-12.78, -25.22) * mm, "end": v(-12.72, -25.13) * mm});
            skLineSegment(sketch, "E1676", {"start": v(-12.72, -25.13) * mm, "end": v(-12.67, -25.06) * mm});
            skLineSegment(sketch, "E1677", {"start": v(-12.67, -25.06) * mm, "end": v(-12.63, -25) * mm});
            skLineSegment(sketch, "E1678", {"start": v(-12.63, -25) * mm, "end": v(-12.59, -24.94) * mm});
            skLineSegment(sketch, "E1679", {"start": v(-12.59, -24.94) * mm, "end": v(-12.56, -24.9) * mm});
            skLineSegment(sketch, "E1680", {"start": v(-12.56, -24.9) * mm, "end": v(-12.54, -24.86) * mm});
            skLineSegment(sketch, "E1681", {"start": v(-12.54, -24.86) * mm, "end": v(-12.52, -24.83) * mm});
            skLineSegment(sketch, "E1682", {"start": v(-12.52, -24.83) * mm, "end": v(-12.52, -24.82) * mm});
            skLineSegment(sketch, "E1683", {"start": v(-12.52, -24.82) * mm, "end": v(-12.52, -24.82) * mm});
            skLineSegment(sketch, "E1684", {"start": v(-12.52, -24.82) * mm, "end": v(-12.48, -24.74) * mm});
            skLineSegment(sketch, "E1685", {"start": v(-12.48, -24.74) * mm, "end": v(-12.4, -24.6) * mm});
            skLineSegment(sketch, "E1686", {"start": v(-12.4, -24.6) * mm, "end": v(-12.34, -24.47) * mm});
            skLineSegment(sketch, "E1687", {"start": v(-12.34, -24.47) * mm, "end": v(-12.26, -24.35) * mm});
            skLineSegment(sketch, "E1688", {"start": v(-12.26, -24.35) * mm, "end": v(-12.2, -24.25) * mm});
            skLineSegment(sketch, "E1689", {"start": v(-12.2, -24.25) * mm, "end": v(-12.12, -24.17) * mm});
            skLineSegment(sketch, "E1690", {"start": v(-12.12, -24.17) * mm, "end": v(-12.06, -24.1) * mm});
            skLineSegment(sketch, "E1691", {"start": v(-12.06, -24.1) * mm, "end": v(-12, -24.03) * mm});
            skLineSegment(sketch, "E1692", {"start": v(-12, -24.03) * mm, "end": v(-11.93, -23.98) * mm});
            skLineSegment(sketch, "E1693", {"start": v(-11.93, -23.98) * mm, "end": v(-11.87, -23.95) * mm});
            skLineSegment(sketch, "E1694", {"start": v(-11.87, -23.95) * mm, "end": v(-11.82, -23.93) * mm});
            skLineSegment(sketch, "E1695", {"start": v(-11.82, -23.93) * mm, "end": v(-11.77, -23.92) * mm});
            skLineSegment(sketch, "E1696", {"start": v(-11.77, -23.92) * mm, "end": v(-11.72, -23.92) * mm});
            skLineSegment(sketch, "E1697", {"start": v(-11.72, -23.92) * mm, "end": v(-11.69, -23.94) * mm});
            skLineSegment(sketch, "E1698", {"start": v(-11.69, -23.94) * mm, "end": v(-11.6, -23.98) * mm});
            skLineSegment(sketch, "E1699", {"start": v(-11.6, -23.98) * mm, "end": v(-11.09, -24.22) * mm});
            skLineSegment(sketch, "E1700", {"start": v(-11.09, -24.22) * mm, "end": v(-10.58, -24.45) * mm});
            skLineSegment(sketch, "E1701", {"start": v(-10.58, -24.45) * mm, "end": v(-10.07, -24.66) * mm});
            skLineSegment(sketch, "E1702", {"start": v(-10.07, -24.66) * mm, "end": v(-9.97, -24.7) * mm});
            skLineSegment(sketch, "E1703", {"start": v(-9.97, -24.7) * mm, "end": v(-9.93, -24.72) * mm});
            skLineSegment(sketch, "E1704", {"start": v(-9.93, -24.72) * mm, "end": v(-9.9, -24.75) * mm});
            skLineSegment(sketch, "E1705", {"start": v(-9.9, -24.75) * mm, "end": v(-9.87, -24.8) * mm});
            skLineSegment(sketch, "E1706", {"start": v(-9.87, -24.8) * mm, "end": v(-9.85, -24.85) * mm});
            skLineSegment(sketch, "E1707", {"start": v(-9.85, -24.85) * mm, "end": v(-9.84, -24.91) * mm});
            skLineSegment(sketch, "E1708", {"start": v(-9.84, -24.91) * mm, "end": v(-9.83, -25) * mm});
            skLineSegment(sketch, "E1709", {"start": v(-9.83, -25) * mm, "end": v(-9.84, -25.08) * mm});
            skLineSegment(sketch, "E1710", {"start": v(-9.84, -25.08) * mm, "end": v(-9.85, -25.18) * mm});
            skLineSegment(sketch, "E1711", {"start": v(-9.85, -25.18) * mm, "end": v(-9.86, -25.29) * mm});
            skLineSegment(sketch, "E1712", {"start": v(-9.86, -25.29) * mm, "end": v(-9.9, -25.4) * mm});
            skLineSegment(sketch, "E1713", {"start": v(-9.9, -25.4) * mm, "end": v(-9.93, -25.54) * mm});
            skLineSegment(sketch, "E1714", {"start": v(-9.93, -25.54) * mm, "end": v(-9.98, -25.68) * mm});
            skLineSegment(sketch, "E1715", {"start": v(-9.98, -25.68) * mm, "end": v(-10.03, -25.83) * mm});
            skLineSegment(sketch, "E1716", {"start": v(-10.03, -25.83) * mm, "end": v(-10.07, -25.9) * mm});
            skLineSegment(sketch, "E1717", {"start": v(-10.07, -25.9) * mm, "end": v(-10.07, -25.9) * mm});
            skLineSegment(sketch, "E1718", {"start": v(-10.07, -25.9) * mm, "end": v(-10.07, -25.92) * mm});
            skLineSegment(sketch, "E1719", {"start": v(-10.07, -25.92) * mm, "end": v(-10.08, -25.95) * mm});
            skLineSegment(sketch, "E1720", {"start": v(-10.08, -25.95) * mm, "end": v(-10.1, -26) * mm});
            skLineSegment(sketch, "E1721", {"start": v(-10.1, -26) * mm, "end": v(-10.11, -26.04) * mm});
            skLineSegment(sketch, "E1722", {"start": v(-10.11, -26.04) * mm, "end": v(-10.13, -26.1) * mm});
            skLineSegment(sketch, "E1723", {"start": v(-10.13, -26.1) * mm, "end": v(-10.15, -26.18) * mm});
            skLineSegment(sketch, "E1724", {"start": v(-10.15, -26.18) * mm, "end": v(-10.16, -26.27) * mm});
            skLineSegment(sketch, "E1725", {"start": v(-10.16, -26.27) * mm, "end": v(-10.18, -26.37) * mm});
            skLineSegment(sketch, "E1726", {"start": v(-10.18, -26.37) * mm, "end": v(-10.2, -26.49) * mm});
            skLineSegment(sketch, "E1727", {"start": v(-10.2, -26.49) * mm, "end": v(-10.22, -26.61) * mm});
            skLineSegment(sketch, "E1728", {"start": v(-10.22, -26.61) * mm, "end": v(-10.24, -26.75) * mm});
            skLineSegment(sketch, "E1729", {"start": v(-10.24, -26.75) * mm, "end": v(-10.26, -26.9) * mm});
            skLineSegment(sketch, "E1730", {"start": v(-10.26, -26.9) * mm, "end": v(-10.27, -27.06) * mm});
            skLineSegment(sketch, "E1731", {"start": v(-10.27, -27.06) * mm, "end": v(-10.29, -27.24) * mm});
            skLineSegment(sketch, "E1732", {"start": v(-10.29, -27.24) * mm, "end": v(-10.3, -27.42) * mm});
            skLineSegment(sketch, "E1733", {"start": v(-10.3, -27.42) * mm, "end": v(-10.3, -27.62) * mm});
            skLineSegment(sketch, "E1734", {"start": v(-10.3, -27.62) * mm, "end": v(-10.3, -27.84) * mm});
            skLineSegment(sketch, "E1735", {"start": v(-10.3, -27.84) * mm, "end": v(-10.3, -28.06) * mm});
            skLineSegment(sketch, "E1736", {"start": v(-10.3, -28.06) * mm, "end": v(-10.29, -28.3) * mm});
            skLineSegment(sketch, "E1737", {"start": v(-10.29, -28.3) * mm, "end": v(-10.28, -28.55) * mm});
            skLineSegment(sketch, "E1738", {"start": v(-10.28, -28.55) * mm, "end": v(-10.26, -28.75) * mm});
            skLineSegment(sketch, "E1739", {"start": v(-10.26, -28.75) * mm, "end": v(-9.44, -29.06) * mm});
            skLineSegment(sketch, "E1740", {"start": v(-9.44, -29.06) * mm, "end": v(-8.6, -29.29) * mm});
            skLineSegment(sketch, "E1741", {"start": v(-8.6, -29.29) * mm, "end": v(-8.47, -29.13) * mm});
            skLineSegment(sketch, "E1742", {"start": v(-8.47, -29.13) * mm, "end": v(-8.3, -28.94) * mm});
            skLineSegment(sketch, "E1743", {"start": v(-8.3, -28.94) * mm, "end": v(-8.16, -28.76) * mm});
            skLineSegment(sketch, "E1744", {"start": v(-8.16, -28.76) * mm, "end": v(-8.03, -28.58) * mm});
            skLineSegment(sketch, "E1745", {"start": v(-8.03, -28.58) * mm, "end": v(-7.9, -28.4) * mm});
            skLineSegment(sketch, "E1746", {"start": v(-7.9, -28.4) * mm, "end": v(-7.8, -28.24) * mm});
            skLineSegment(sketch, "E1747", {"start": v(-7.8, -28.24) * mm, "end": v(-7.69, -28.08) * mm});
            skLineSegment(sketch, "E1748", {"start": v(-7.69, -28.08) * mm, "end": v(-7.6, -27.93) * mm});
            skLineSegment(sketch, "E1749", {"start": v(-7.6, -27.93) * mm, "end": v(-7.51, -27.8) * mm});
            skLineSegment(sketch, "E1750", {"start": v(-7.51, -27.8) * mm, "end": v(-7.44, -27.66) * mm});
            skLineSegment(sketch, "E1751", {"start": v(-7.44, -27.66) * mm, "end": v(-7.37, -27.54) * mm});
            skLineSegment(sketch, "E1752", {"start": v(-7.37, -27.54) * mm, "end": v(-7.31, -27.43) * mm});
            skLineSegment(sketch, "E1753", {"start": v(-7.31, -27.43) * mm, "end": v(-7.26, -27.32) * mm});
            skLineSegment(sketch, "E1754", {"start": v(-7.26, -27.32) * mm, "end": v(-7.22, -27.23) * mm});
            skLineSegment(sketch, "E1755", {"start": v(-7.22, -27.23) * mm, "end": v(-7.18, -27.15) * mm});
            skLineSegment(sketch, "E1756", {"start": v(-7.18, -27.15) * mm, "end": v(-7.15, -27.07) * mm});
            skLineSegment(sketch, "E1757", {"start": v(-7.15, -27.07) * mm, "end": v(-7.13, -27.01) * mm});
            skLineSegment(sketch, "E1758", {"start": v(-7.13, -27.01) * mm, "end": v(-7.11, -26.96) * mm});
            skLineSegment(sketch, "E1759", {"start": v(-7.11, -26.96) * mm, "end": v(-7.1, -26.92) * mm});
            skLineSegment(sketch, "E1760", {"start": v(-7.1, -26.92) * mm, "end": v(-7.09, -26.9) * mm});
            skLineSegment(sketch, "E1761", {"start": v(-7.09, -26.9) * mm, "end": v(-7.08, -26.88) * mm});
            skLineSegment(sketch, "E1762", {"start": v(-7.08, -26.88) * mm, "end": v(-7.08, -26.88) * mm});
            skLineSegment(sketch, "E1763", {"start": v(-7.08, -26.88) * mm, "end": v(-7.06, -26.8) * mm});
            skLineSegment(sketch, "E1764", {"start": v(-7.06, -26.8) * mm, "end": v(-7.02, -26.64) * mm});
            skLineSegment(sketch, "E1765", {"start": v(-7.02, -26.64) * mm, "end": v(-6.98, -26.5) * mm});
            skLineSegment(sketch, "E1766", {"start": v(-6.98, -26.5) * mm, "end": v(-6.93, -26.37) * mm});
            skLineSegment(sketch, "E1767", {"start": v(-6.93, -26.37) * mm, "end": v(-6.88, -26.26) * mm});
            skLineSegment(sketch, "E1768", {"start": v(-6.88, -26.26) * mm, "end": v(-6.84, -26.16) * mm});
            skLineSegment(sketch, "E1769", {"start": v(-6.84, -26.16) * mm, "end": v(-6.78, -26.07) * mm});
            skLineSegment(sketch, "E1770", {"start": v(-6.78, -26.07) * mm, "end": v(-6.73, -26) * mm});
            skLineSegment(sketch, "E1771", {"start": v(-6.73, -26) * mm, "end": v(-6.68, -25.94) * mm});
            skLineSegment(sketch, "E1772", {"start": v(-6.68, -25.94) * mm, "end": v(-6.63, -25.9) * mm});
            skLineSegment(sketch, "E1773", {"start": v(-6.63, -25.9) * mm, "end": v(-6.59, -25.86) * mm});
            skLineSegment(sketch, "E1774", {"start": v(-6.59, -25.86) * mm, "end": v(-6.54, -25.84) * mm});
            skLineSegment(sketch, "E1775", {"start": v(-6.54, -25.84) * mm, "end": v(-6.5, -25.84) * mm});
            skLineSegment(sketch, "E1776", {"start": v(-6.5, -25.84) * mm, "end": v(-6.45, -25.85) * mm});
            skLineSegment(sketch, "E1777", {"start": v(-6.45, -25.85) * mm, "end": v(-6.35, -25.87) * mm});
            skLineSegment(sketch, "E1778", {"start": v(-6.35, -25.87) * mm, "end": v(-5.81, -26) * mm});
            skLineSegment(sketch, "E1779", {"start": v(-5.81, -26) * mm, "end": v(-5.27, -26.11) * mm});
            skLineSegment(sketch, "E1780", {"start": v(-5.27, -26.11) * mm, "end": v(-4.72, -26.22) * mm});
            skLineSegment(sketch, "E1781", {"start": v(-4.72, -26.22) * mm, "end": v(-4.62, -26.24) * mm});
            skLineSegment(sketch, "E1782", {"start": v(-4.62, -26.24) * mm, "end": v(-4.58, -26.25) * mm});
            skLineSegment(sketch, "E1783", {"start": v(-4.58, -26.25) * mm, "end": v(-4.54, -26.27) * mm});
            skLineSegment(sketch, "E1784", {"start": v(-4.54, -26.27) * mm, "end": v(-4.5, -26.3) * mm});
            skLineSegment(sketch, "E1785", {"start": v(-4.5, -26.3) * mm, "end": v(-4.47, -26.35) * mm});
            skLineSegment(sketch, "E1786", {"start": v(-4.47, -26.35) * mm, "end": v(-4.44, -26.42) * mm});
            skLineSegment(sketch, "E1787", {"start": v(-4.44, -26.42) * mm, "end": v(-4.42, -26.5) * mm});
            skLineSegment(sketch, "E1788", {"start": v(-4.42, -26.5) * mm, "end": v(-4.4, -26.58) * mm});
            skLineSegment(sketch, "E1789", {"start": v(-4.4, -26.58) * mm, "end": v(-4.4, -26.68) * mm});
            skLineSegment(sketch, "E1790", {"start": v(-4.4, -26.68) * mm, "end": v(-4.4, -26.79) * mm});
            skLineSegment(sketch, "E1791", {"start": v(-4.4, -26.79) * mm, "end": v(-4.4, -26.91) * mm});
            skLineSegment(sketch, "E1792", {"start": v(-4.4, -26.91) * mm, "end": v(-4.4, -27.05) * mm});
            skLineSegment(sketch, "E1793", {"start": v(-4.4, -27.05) * mm, "end": v(-4.42, -27.2) * mm});
            skLineSegment(sketch, "E1794", {"start": v(-4.42, -27.2) * mm, "end": v(-4.44, -27.35) * mm});
            skLineSegment(sketch, "E1795", {"start": v(-4.44, -27.35) * mm, "end": v(-4.46, -27.43) * mm});
            skLineSegment(sketch, "E1796", {"start": v(-4.46, -27.43) * mm, "end": v(-4.46, -27.44) * mm});
            skLineSegment(sketch, "E1797", {"start": v(-4.46, -27.44) * mm, "end": v(-4.46, -27.45) * mm});
            skLineSegment(sketch, "E1798", {"start": v(-4.46, -27.45) * mm, "end": v(-4.47, -27.48) * mm});
            skLineSegment(sketch, "E1799", {"start": v(-4.47, -27.48) * mm, "end": v(-4.47, -27.52) * mm});
            skLineSegment(sketch, "E1800", {"start": v(-4.47, -27.52) * mm, "end": v(-4.47, -27.58) * mm});
            skLineSegment(sketch, "E1801", {"start": v(-4.47, -27.58) * mm, "end": v(-4.48, -27.64) * mm});
            skLineSegment(sketch, "E1802", {"start": v(-4.48, -27.64) * mm, "end": v(-4.48, -27.72) * mm});
            skLineSegment(sketch, "E1803", {"start": v(-4.48, -27.72) * mm, "end": v(-4.48, -27.81) * mm});
            skLineSegment(sketch, "E1804", {"start": v(-4.48, -27.81) * mm, "end": v(-4.48, -27.91) * mm});
            skLineSegment(sketch, "E1805", {"start": v(-4.48, -27.91) * mm, "end": v(-4.47, -28.03) * mm});
            skLineSegment(sketch, "E1806", {"start": v(-4.47, -28.03) * mm, "end": v(-4.47, -28.15) * mm});
            skLineSegment(sketch, "E1807", {"start": v(-4.47, -28.15) * mm, "end": v(-4.46, -28.3) * mm});
            skLineSegment(sketch, "E1808", {"start": v(-4.46, -28.3) * mm, "end": v(-4.44, -28.44) * mm});
            skLineSegment(sketch, "E1809", {"start": v(-4.44, -28.44) * mm, "end": v(-4.42, -28.6) * mm});
            skLineSegment(sketch, "E1810", {"start": v(-4.42, -28.6) * mm, "end": v(-4.4, -28.78) * mm});
            skLineSegment(sketch, "E1811", {"start": v(-4.4, -28.78) * mm, "end": v(-4.37, -28.97) * mm});
            skLineSegment(sketch, "E1812", {"start": v(-4.37, -28.97) * mm, "end": v(-4.33, -29.16) * mm});
            skLineSegment(sketch, "E1813", {"start": v(-4.33, -29.16) * mm, "end": v(-4.29, -29.37) * mm});
            skLineSegment(sketch, "E1814", {"start": v(-4.29, -29.37) * mm, "end": v(-4.24, -29.59) * mm});
            skLineSegment(sketch, "E1815", {"start": v(-4.24, -29.59) * mm, "end": v(-4.18, -29.82) * mm});
            skLineSegment(sketch, "E1816", {"start": v(-4.18, -29.82) * mm, "end": v(-4.12, -30.06) * mm});
            skLineSegment(sketch, "E1817", {"start": v(-4.12, -30.06) * mm, "end": v(-4.06, -30.25) * mm});
            skLineSegment(sketch, "E1818", {"start": v(-4.06, -30.25) * mm, "end": v(-3.2, -30.4) * mm});
            skLineSegment(sketch, "E1819", {"start": v(-3.2, -30.4) * mm, "end": v(-2.32, -30.44) * mm});
            skLineSegment(sketch, "E1820", {"start": v(-2.32, -30.44) * mm, "end": v(-2.22, -30.26) * mm});
            skLineSegment(sketch, "E1821", {"start": v(-2.22, -30.26) * mm, "end": v(-2.11, -30.04) * mm});
            skLineSegment(sketch, "E1822", {"start": v(-2.11, -30.04) * mm, "end": v(-2, -29.82) * mm});
            skLineSegment(sketch, "E1823", {"start": v(-2, -29.82) * mm, "end": v(-1.91, -29.62) * mm});
            skLineSegment(sketch, "E1824", {"start": v(-1.91, -29.62) * mm, "end": v(-1.83, -29.43) * mm});
            skLineSegment(sketch, "E1825", {"start": v(-1.83, -29.43) * mm, "end": v(-1.75, -29.24) * mm});
            skLineSegment(sketch, "E1826", {"start": v(-1.75, -29.24) * mm, "end": v(-1.68, -29.07) * mm});
            skLineSegment(sketch, "E1827", {"start": v(-1.68, -29.07) * mm, "end": v(-1.62, -28.9) * mm});
            skLineSegment(sketch, "E1828", {"start": v(-1.62, -28.9) * mm, "end": v(-1.57, -28.75) * mm});
            skLineSegment(sketch, "E1829", {"start": v(-1.57, -28.75) * mm, "end": v(-1.52, -28.6) * mm});
            skLineSegment(sketch, "E1830", {"start": v(-1.52, -28.6) * mm, "end": v(-1.48, -28.47) * mm});
            skLineSegment(sketch, "E1831", {"start": v(-1.48, -28.47) * mm, "end": v(-1.45, -28.35) * mm});
            skLineSegment(sketch, "E1832", {"start": v(-1.45, -28.35) * mm, "end": v(-1.42, -28.23) * mm});
            skLineSegment(sketch, "E1833", {"start": v(-1.42, -28.23) * mm, "end": v(-1.4, -28.13) * mm});
            skLineSegment(sketch, "E1834", {"start": v(-1.4, -28.13) * mm, "end": v(-1.38, -28.05) * mm});
            skLineSegment(sketch, "E1835", {"start": v(-1.38, -28.05) * mm, "end": v(-1.37, -27.97) * mm});
            skLineSegment(sketch, "E1836", {"start": v(-1.37, -27.97) * mm, "end": v(-1.36, -27.9) * mm});
            skLineSegment(sketch, "E1837", {"start": v(-1.36, -27.9) * mm, "end": v(-1.35, -27.85) * mm});
            skLineSegment(sketch, "E1838", {"start": v(-1.35, -27.85) * mm, "end": v(-1.34, -27.8) * mm});
            skLineSegment(sketch, "E1839", {"start": v(-1.34, -27.8) * mm, "end": v(-1.34, -27.78) * mm});
            skLineSegment(sketch, "E1840", {"start": v(-1.34, -27.78) * mm, "end": v(-1.34, -27.76) * mm});
            skLineSegment(sketch, "E1841", {"start": v(-1.34, -27.76) * mm, "end": v(-1.34, -27.76) * mm});
            skLineSegment(sketch, "E1842", {"start": v(-1.34, -27.76) * mm, "end": v(-1.34, -27.67) * mm});
            skLineSegment(sketch, "E1843", {"start": v(-1.34, -27.67) * mm, "end": v(-1.33, -27.52) * mm});
            skLineSegment(sketch, "E1844", {"start": v(-1.33, -27.52) * mm, "end": v(-1.32, -27.37) * mm});
            skLineSegment(sketch, "E1845", {"start": v(-1.32, -27.37) * mm, "end": v(-1.3, -27.24) * mm});
            skLineSegment(sketch, "E1846", {"start": v(-1.3, -27.24) * mm, "end": v(-1.28, -27.12) * mm});
            skLineSegment(sketch, "E1847", {"start": v(-1.28, -27.12) * mm, "end": v(-1.25, -27) * mm});
            skLineSegment(sketch, "E1848", {"start": v(-1.25, -27) * mm, "end": v(-1.22, -26.91) * mm});
            skLineSegment(sketch, "E1849", {"start": v(-1.22, -26.91) * mm, "end": v(-1.18, -26.83) * mm});
            skLineSegment(sketch, "E1850", {"start": v(-1.18, -26.83) * mm, "end": v(-1.14, -26.76) * mm});
            skLineSegment(sketch, "E1851", {"start": v(-1.14, -26.76) * mm, "end": v(-1.1, -26.7) * mm});
            skLineSegment(sketch, "E1852", {"start": v(-1.1, -26.7) * mm, "end": v(-1.06, -26.67) * mm});
            skLineSegment(sketch, "E1853", {"start": v(-1.06, -26.67) * mm, "end": v(-1.02, -26.64) * mm});
            skLineSegment(sketch, "E1854", {"start": v(-1.02, -26.64) * mm, "end": v(-0.98, -26.62) * mm});
            skLineSegment(sketch, "E1855", {"start": v(-0.98, -26.62) * mm, "end": v(-0.94, -26.62) * mm});
            skLineSegment(sketch, "E1856", {"start": v(-0.94, -26.62) * mm, "end": v(-0.84, -26.63) * mm});
            skLineSegment(sketch, "E1857", {"start": v(-0.84, -26.63) * mm, "end": v(-0.28, -26.64) * mm});
            skLineSegment(sketch, "E1858", {"start": v(-0.28, -26.64) * mm, "end": v(0.28, -26.64) * mm});
            skLineSegment(sketch, "E1859", {"start": v(0.28, -26.64) * mm, "end": v(0.84, -26.63) * mm});
            skLineSegment(sketch, "E1860", {"start": v(0.84, -26.63) * mm, "end": v(0.94, -26.62) * mm});
            skLineSegment(sketch, "E1861", {"start": v(0.94, -26.62) * mm, "end": v(0.98, -26.62) * mm});
            skLineSegment(sketch, "E1862", {"start": v(0.98, -26.62) * mm, "end": v(1.02, -26.64) * mm});
            skLineSegment(sketch, "E1863", {"start": v(1.02, -26.64) * mm, "end": v(1.06, -26.67) * mm});
            skLineSegment(sketch, "E1864", {"start": v(1.06, -26.67) * mm, "end": v(1.1, -26.7) * mm});
            skLineSegment(sketch, "E1865", {"start": v(1.1, -26.7) * mm, "end": v(1.14, -26.76) * mm});
            skLineSegment(sketch, "E1866", {"start": v(1.14, -26.76) * mm, "end": v(1.18, -26.83) * mm});
            skLineSegment(sketch, "E1867", {"start": v(1.18, -26.83) * mm, "end": v(1.22, -26.91) * mm});
            skLineSegment(sketch, "E1868", {"start": v(1.22, -26.91) * mm, "end": v(1.25, -27) * mm});
            skLineSegment(sketch, "E1869", {"start": v(1.25, -27) * mm, "end": v(1.28, -27.12) * mm});
            skLineSegment(sketch, "E1870", {"start": v(1.28, -27.12) * mm, "end": v(1.3, -27.24) * mm});
            skLineSegment(sketch, "E1871", {"start": v(1.3, -27.24) * mm, "end": v(1.32, -27.37) * mm});
            skLineSegment(sketch, "E1872", {"start": v(1.32, -27.37) * mm, "end": v(1.33, -27.52) * mm});
            skLineSegment(sketch, "E1873", {"start": v(1.33, -27.52) * mm, "end": v(1.34, -27.67) * mm});
            skLineSegment(sketch, "E1874", {"start": v(1.34, -27.67) * mm, "end": v(1.34, -27.76) * mm});
            skLineSegment(sketch, "E1875", {"start": v(1.34, -27.76) * mm, "end": v(1.34, -27.76) * mm});
            skLineSegment(sketch, "E1876", {"start": v(1.34, -27.76) * mm, "end": v(1.34, -27.78) * mm});
            skLineSegment(sketch, "E1877", {"start": v(1.34, -27.78) * mm, "end": v(1.34, -27.8) * mm});
            skLineSegment(sketch, "E1878", {"start": v(1.34, -27.8) * mm, "end": v(1.35, -27.85) * mm});
            skLineSegment(sketch, "E1879", {"start": v(1.35, -27.85) * mm, "end": v(1.36, -27.9) * mm});
            skLineSegment(sketch, "E1880", {"start": v(1.36, -27.9) * mm, "end": v(1.37, -27.97) * mm});
            skLineSegment(sketch, "E1881", {"start": v(1.37, -27.97) * mm, "end": v(1.38, -28.05) * mm});
            skLineSegment(sketch, "E1882", {"start": v(1.38, -28.05) * mm, "end": v(1.4, -28.13) * mm});
            skLineSegment(sketch, "E1883", {"start": v(1.4, -28.13) * mm, "end": v(1.42, -28.23) * mm});
            skLineSegment(sketch, "E1884", {"start": v(1.42, -28.23) * mm, "end": v(1.45, -28.35) * mm});
            skLineSegment(sketch, "E1885", {"start": v(1.45, -28.35) * mm, "end": v(1.48, -28.47) * mm});
            skLineSegment(sketch, "E1886", {"start": v(1.48, -28.47) * mm, "end": v(1.52, -28.6) * mm});
            skLineSegment(sketch, "E1887", {"start": v(1.52, -28.6) * mm, "end": v(1.57, -28.75) * mm});
            skLineSegment(sketch, "E1888", {"start": v(1.57, -28.75) * mm, "end": v(1.62, -28.9) * mm});
            skLineSegment(sketch, "E1889", {"start": v(1.62, -28.9) * mm, "end": v(1.68, -29.07) * mm});
            skLineSegment(sketch, "E1890", {"start": v(1.68, -29.07) * mm, "end": v(1.75, -29.24) * mm});
            skLineSegment(sketch, "E1891", {"start": v(1.75, -29.24) * mm, "end": v(1.83, -29.43) * mm});
            skLineSegment(sketch, "E1892", {"start": v(1.83, -29.43) * mm, "end": v(1.91, -29.62) * mm});
            skLineSegment(sketch, "E1893", {"start": v(1.91, -29.62) * mm, "end": v(2, -29.82) * mm});
            skLineSegment(sketch, "E1894", {"start": v(2, -29.82) * mm, "end": v(2.11, -30.04) * mm});
            skLineSegment(sketch, "E1895", {"start": v(2.11, -30.04) * mm, "end": v(2.22, -30.26) * mm});
            skLineSegment(sketch, "E1896", {"start": v(2.22, -30.26) * mm, "end": v(2.32, -30.44) * mm});
            skLineSegment(sketch, "E1897", {"start": v(2.32, -30.44) * mm, "end": v(3.2, -30.4) * mm});
            skLineSegment(sketch, "E1898", {"start": v(3.2, -30.4) * mm, "end": v(4.06, -30.25) * mm});
            skLineSegment(sketch, "E1899", {"start": v(4.06, -30.25) * mm, "end": v(4.12, -30.06) * mm});
            skLineSegment(sketch, "E1900", {"start": v(4.12, -30.06) * mm, "end": v(4.18, -29.82) * mm});
            skLineSegment(sketch, "E1901", {"start": v(4.18, -29.82) * mm, "end": v(4.24, -29.59) * mm});
            skLineSegment(sketch, "E1902", {"start": v(4.24, -29.59) * mm, "end": v(4.29, -29.37) * mm});
            skLineSegment(sketch, "E1903", {"start": v(4.29, -29.37) * mm, "end": v(4.33, -29.16) * mm});
            skLineSegment(sketch, "E1904", {"start": v(4.33, -29.16) * mm, "end": v(4.37, -28.97) * mm});
            skLineSegment(sketch, "E1905", {"start": v(4.37, -28.97) * mm, "end": v(4.4, -28.78) * mm});
            skLineSegment(sketch, "E1906", {"start": v(4.4, -28.78) * mm, "end": v(4.42, -28.6) * mm});
            skLineSegment(sketch, "E1907", {"start": v(4.42, -28.6) * mm, "end": v(4.44, -28.44) * mm});
            skLineSegment(sketch, "E1908", {"start": v(4.44, -28.44) * mm, "end": v(4.46, -28.3) * mm});
            skLineSegment(sketch, "E1909", {"start": v(4.46, -28.3) * mm, "end": v(4.47, -28.15) * mm});
            skLineSegment(sketch, "E1910", {"start": v(4.47, -28.15) * mm, "end": v(4.47, -28.03) * mm});
            skLineSegment(sketch, "E1911", {"start": v(4.47, -28.03) * mm, "end": v(4.48, -27.91) * mm});
            skLineSegment(sketch, "E1912", {"start": v(4.48, -27.91) * mm, "end": v(4.48, -27.81) * mm});
            skLineSegment(sketch, "E1913", {"start": v(4.48, -27.81) * mm, "end": v(4.48, -27.72) * mm});
            skLineSegment(sketch, "E1914", {"start": v(4.48, -27.72) * mm, "end": v(4.48, -27.64) * mm});
            skLineSegment(sketch, "E1915", {"start": v(4.48, -27.64) * mm, "end": v(4.47, -27.58) * mm});
            skLineSegment(sketch, "E1916", {"start": v(4.47, -27.58) * mm, "end": v(4.47, -27.52) * mm});
            skLineSegment(sketch, "E1917", {"start": v(4.47, -27.52) * mm, "end": v(4.47, -27.48) * mm});
            skLineSegment(sketch, "E1918", {"start": v(4.47, -27.48) * mm, "end": v(4.46, -27.45) * mm});
            skLineSegment(sketch, "E1919", {"start": v(4.46, -27.45) * mm, "end": v(4.46, -27.44) * mm});
            skLineSegment(sketch, "E1920", {"start": v(4.46, -27.44) * mm, "end": v(4.46, -27.43) * mm});
            skLineSegment(sketch, "E1921", {"start": v(4.46, -27.43) * mm, "end": v(4.44, -27.35) * mm});
            skLineSegment(sketch, "E1922", {"start": v(4.44, -27.35) * mm, "end": v(4.42, -27.2) * mm});
            skLineSegment(sketch, "E1923", {"start": v(4.42, -27.2) * mm, "end": v(4.4, -27.05) * mm});
            skLineSegment(sketch, "E1924", {"start": v(4.4, -27.05) * mm, "end": v(4.4, -26.91) * mm});
            skLineSegment(sketch, "E1925", {"start": v(4.4, -26.91) * mm, "end": v(4.4, -26.79) * mm});
            skLineSegment(sketch, "E1926", {"start": v(4.4, -26.79) * mm, "end": v(4.4, -26.68) * mm});
            skLineSegment(sketch, "E1927", {"start": v(4.4, -26.68) * mm, "end": v(4.4, -26.58) * mm});
            skLineSegment(sketch, "E1928", {"start": v(4.4, -26.58) * mm, "end": v(4.42, -26.5) * mm});
            skLineSegment(sketch, "E1929", {"start": v(4.42, -26.5) * mm, "end": v(4.44, -26.42) * mm});
            skLineSegment(sketch, "E1930", {"start": v(4.44, -26.42) * mm, "end": v(4.47, -26.35) * mm});
            skLineSegment(sketch, "E1931", {"start": v(4.47, -26.35) * mm, "end": v(4.5, -26.3) * mm});
            skLineSegment(sketch, "E1932", {"start": v(4.5, -26.3) * mm, "end": v(4.54, -26.27) * mm});
            skLineSegment(sketch, "E1933", {"start": v(4.54, -26.27) * mm, "end": v(4.58, -26.25) * mm});
            skLineSegment(sketch, "E1934", {"start": v(4.58, -26.25) * mm, "end": v(4.62, -26.24) * mm});
            skLineSegment(sketch, "E1935", {"start": v(4.62, -26.24) * mm, "end": v(4.72, -26.22) * mm});
            skLineSegment(sketch, "E1936", {"start": v(4.72, -26.22) * mm, "end": v(5.27, -26.11) * mm});
            skLineSegment(sketch, "E1937", {"start": v(5.27, -26.11) * mm, "end": v(5.81, -26) * mm});
            skLineSegment(sketch, "E1938", {"start": v(5.81, -26) * mm, "end": v(6.35, -25.87) * mm});
            skLineSegment(sketch, "E1939", {"start": v(6.35, -25.87) * mm, "end": v(6.45, -25.85) * mm});
            skLineSegment(sketch, "E1940", {"start": v(6.45, -25.85) * mm, "end": v(6.5, -25.84) * mm});
            skLineSegment(sketch, "E1941", {"start": v(6.5, -25.84) * mm, "end": v(6.54, -25.84) * mm});
            skLineSegment(sketch, "E1942", {"start": v(6.54, -25.84) * mm, "end": v(6.59, -25.86) * mm});
            skLineSegment(sketch, "E1943", {"start": v(6.59, -25.86) * mm, "end": v(6.63, -25.9) * mm});
            skLineSegment(sketch, "E1944", {"start": v(6.63, -25.9) * mm, "end": v(6.68, -25.94) * mm});
            skLineSegment(sketch, "E1945", {"start": v(6.68, -25.94) * mm, "end": v(6.73, -26) * mm});
            skLineSegment(sketch, "E1946", {"start": v(6.73, -26) * mm, "end": v(6.78, -26.07) * mm});
            skLineSegment(sketch, "E1947", {"start": v(6.78, -26.07) * mm, "end": v(6.84, -26.16) * mm});
            skLineSegment(sketch, "E1948", {"start": v(6.84, -26.16) * mm, "end": v(6.88, -26.26) * mm});
            skLineSegment(sketch, "E1949", {"start": v(6.88, -26.26) * mm, "end": v(6.93, -26.37) * mm});
            skLineSegment(sketch, "E1950", {"start": v(6.93, -26.37) * mm, "end": v(6.98, -26.5) * mm});
            skLineSegment(sketch, "E1951", {"start": v(6.98, -26.5) * mm, "end": v(7.02, -26.64) * mm});
            skLineSegment(sketch, "E1952", {"start": v(7.02, -26.64) * mm, "end": v(7.06, -26.8) * mm});
            skLineSegment(sketch, "E1953", {"start": v(7.06, -26.8) * mm, "end": v(7.08, -26.88) * mm});
            skLineSegment(sketch, "E1954", {"start": v(7.08, -26.88) * mm, "end": v(7.08, -26.88) * mm});
            skLineSegment(sketch, "E1955", {"start": v(7.08, -26.88) * mm, "end": v(7.09, -26.9) * mm});
            skLineSegment(sketch, "E1956", {"start": v(7.09, -26.9) * mm, "end": v(7.1, -26.92) * mm});
            skLineSegment(sketch, "E1957", {"start": v(7.1, -26.92) * mm, "end": v(7.11, -26.96) * mm});
            skLineSegment(sketch, "E1958", {"start": v(7.11, -26.96) * mm, "end": v(7.13, -27.01) * mm});
            skLineSegment(sketch, "E1959", {"start": v(7.13, -27.01) * mm, "end": v(7.15, -27.07) * mm});
            skLineSegment(sketch, "E1960", {"start": v(7.15, -27.07) * mm, "end": v(7.18, -27.15) * mm});
            skLineSegment(sketch, "E1961", {"start": v(7.18, -27.15) * mm, "end": v(7.22, -27.23) * mm});
            skLineSegment(sketch, "E1962", {"start": v(7.22, -27.23) * mm, "end": v(7.26, -27.32) * mm});
            skLineSegment(sketch, "E1963", {"start": v(7.26, -27.32) * mm, "end": v(7.31, -27.43) * mm});
            skLineSegment(sketch, "E1964", {"start": v(7.31, -27.43) * mm, "end": v(7.37, -27.54) * mm});
            skLineSegment(sketch, "E1965", {"start": v(7.37, -27.54) * mm, "end": v(7.44, -27.66) * mm});
            skLineSegment(sketch, "E1966", {"start": v(7.44, -27.66) * mm, "end": v(7.51, -27.8) * mm});
            skLineSegment(sketch, "E1967", {"start": v(7.51, -27.8) * mm, "end": v(7.6, -27.93) * mm});
            skLineSegment(sketch, "E1968", {"start": v(7.6, -27.93) * mm, "end": v(7.69, -28.08) * mm});
            skLineSegment(sketch, "E1969", {"start": v(7.69, -28.08) * mm, "end": v(7.8, -28.24) * mm});
            skLineSegment(sketch, "E1970", {"start": v(7.8, -28.24) * mm, "end": v(7.9, -28.4) * mm});
            skLineSegment(sketch, "E1971", {"start": v(7.9, -28.4) * mm, "end": v(8.03, -28.58) * mm});
            skLineSegment(sketch, "E1972", {"start": v(8.03, -28.58) * mm, "end": v(8.16, -28.76) * mm});
            skLineSegment(sketch, "E1973", {"start": v(8.16, -28.76) * mm, "end": v(8.3, -28.94) * mm});
            skLineSegment(sketch, "E1974", {"start": v(8.3, -28.94) * mm, "end": v(8.47, -29.13) * mm});
            skLineSegment(sketch, "E1975", {"start": v(8.47, -29.13) * mm, "end": v(8.6, -29.29) * mm});
            skLineSegment(sketch, "E1976", {"start": v(8.6, -29.29) * mm, "end": v(9.44, -29.06) * mm});
            skLineSegment(sketch, "E1977", {"start": v(9.44, -29.06) * mm, "end": v(10.26, -28.75) * mm});
            skLineSegment(sketch, "E1978", {"start": v(10.26, -28.75) * mm, "end": v(10.28, -28.55) * mm});
            skLineSegment(sketch, "E1979", {"start": v(10.28, -28.55) * mm, "end": v(10.29, -28.3) * mm});
            skLineSegment(sketch, "E1980", {"start": v(10.29, -28.3) * mm, "end": v(10.3, -28.06) * mm});
            skLineSegment(sketch, "E1981", {"start": v(10.3, -28.06) * mm, "end": v(10.3, -27.84) * mm});
            skLineSegment(sketch, "E1982", {"start": v(10.3, -27.84) * mm, "end": v(10.3, -27.62) * mm});
            skLineSegment(sketch, "E1983", {"start": v(10.3, -27.62) * mm, "end": v(10.3, -27.42) * mm});
            skLineSegment(sketch, "E1984", {"start": v(10.3, -27.42) * mm, "end": v(10.29, -27.24) * mm});
            skLineSegment(sketch, "E1985", {"start": v(10.29, -27.24) * mm, "end": v(10.27, -27.06) * mm});
            skLineSegment(sketch, "E1986", {"start": v(10.27, -27.06) * mm, "end": v(10.26, -26.9) * mm});
            skLineSegment(sketch, "E1987", {"start": v(10.26, -26.9) * mm, "end": v(10.24, -26.75) * mm});
            skLineSegment(sketch, "E1988", {"start": v(10.24, -26.75) * mm, "end": v(10.22, -26.61) * mm});
            skLineSegment(sketch, "E1989", {"start": v(10.22, -26.61) * mm, "end": v(10.2, -26.49) * mm});
            skLineSegment(sketch, "E1990", {"start": v(10.2, -26.49) * mm, "end": v(10.18, -26.37) * mm});
            skLineSegment(sketch, "E1991", {"start": v(10.18, -26.37) * mm, "end": v(10.16, -26.27) * mm});
            skLineSegment(sketch, "E1992", {"start": v(10.16, -26.27) * mm, "end": v(10.15, -26.18) * mm});
            skLineSegment(sketch, "E1993", {"start": v(10.15, -26.18) * mm, "end": v(10.13, -26.1) * mm});
            skLineSegment(sketch, "E1994", {"start": v(10.13, -26.1) * mm, "end": v(10.11, -26.04) * mm});
            skLineSegment(sketch, "E1995", {"start": v(10.11, -26.04) * mm, "end": v(10.1, -26) * mm});
            skLineSegment(sketch, "E1996", {"start": v(10.1, -26) * mm, "end": v(10.08, -25.95) * mm});
            skLineSegment(sketch, "E1997", {"start": v(10.08, -25.95) * mm, "end": v(10.07, -25.92) * mm});
            skLineSegment(sketch, "E1998", {"start": v(10.07, -25.92) * mm, "end": v(10.07, -25.9) * mm});
            skLineSegment(sketch, "E1999", {"start": v(10.07, -25.9) * mm, "end": v(10.07, -25.9) * mm});
            skLineSegment(sketch, "E2000", {"start": v(10.07, -25.9) * mm, "end": v(10.03, -25.83) * mm});
            skLineSegment(sketch, "E2001", {"start": v(10.03, -25.83) * mm, "end": v(9.98, -25.68) * mm});
            skLineSegment(sketch, "E2002", {"start": v(9.98, -25.68) * mm, "end": v(9.93, -25.54) * mm});
            skLineSegment(sketch, "E2003", {"start": v(9.93, -25.54) * mm, "end": v(9.9, -25.4) * mm});
            skLineSegment(sketch, "E2004", {"start": v(9.9, -25.4) * mm, "end": v(9.86, -25.29) * mm});
            skLineSegment(sketch, "E2005", {"start": v(9.86, -25.29) * mm, "end": v(9.85, -25.18) * mm});
            skLineSegment(sketch, "E2006", {"start": v(9.85, -25.18) * mm, "end": v(9.84, -25.08) * mm});
            skLineSegment(sketch, "E2007", {"start": v(9.84, -25.08) * mm, "end": v(9.83, -25) * mm});
            skLineSegment(sketch, "E2008", {"start": v(9.83, -25) * mm, "end": v(9.84, -24.91) * mm});
            skLineSegment(sketch, "E2009", {"start": v(9.84, -24.91) * mm, "end": v(9.85, -24.85) * mm});
            skLineSegment(sketch, "E2010", {"start": v(9.85, -24.85) * mm, "end": v(9.87, -24.8) * mm});
            skLineSegment(sketch, "E2011", {"start": v(9.87, -24.8) * mm, "end": v(9.9, -24.75) * mm});
            skLineSegment(sketch, "E2012", {"start": v(9.9, -24.75) * mm, "end": v(9.93, -24.72) * mm});
            skLineSegment(sketch, "E2013", {"start": v(9.93, -24.72) * mm, "end": v(9.97, -24.7) * mm});
            skLineSegment(sketch, "E2014", {"start": v(9.97, -24.7) * mm, "end": v(10.07, -24.66) * mm});
            skLineSegment(sketch, "E2015", {"start": v(10.07, -24.66) * mm, "end": v(10.58, -24.45) * mm});
            skLineSegment(sketch, "E2016", {"start": v(10.58, -24.45) * mm, "end": v(11.09, -24.22) * mm});
            skLineSegment(sketch, "E2017", {"start": v(11.09, -24.22) * mm, "end": v(11.6, -23.98) * mm});
            skLineSegment(sketch, "E2018", {"start": v(11.6, -23.98) * mm, "end": v(11.69, -23.94) * mm});
            skLineSegment(sketch, "E2019", {"start": v(11.69, -23.94) * mm, "end": v(11.72, -23.92) * mm});
            skLineSegment(sketch, "E2020", {"start": v(11.72, -23.92) * mm, "end": v(11.77, -23.92) * mm});
            skLineSegment(sketch, "E2021", {"start": v(11.77, -23.92) * mm, "end": v(11.82, -23.93) * mm});
            skLineSegment(sketch, "E2022", {"start": v(11.82, -23.93) * mm, "end": v(11.87, -23.95) * mm});
            skLineSegment(sketch, "E2023", {"start": v(11.87, -23.95) * mm, "end": v(11.93, -23.98) * mm});
            skLineSegment(sketch, "E2024", {"start": v(11.93, -23.98) * mm, "end": v(12, -24.03) * mm});
            skLineSegment(sketch, "E2025", {"start": v(12, -24.03) * mm, "end": v(12.06, -24.1) * mm});
            skLineSegment(sketch, "E2026", {"start": v(12.06, -24.1) * mm, "end": v(12.12, -24.17) * mm});
            skLineSegment(sketch, "E2027", {"start": v(12.12, -24.17) * mm, "end": v(12.2, -24.25) * mm});
            skLineSegment(sketch, "E2028", {"start": v(12.2, -24.25) * mm, "end": v(12.26, -24.35) * mm});
            skLineSegment(sketch, "E2029", {"start": v(12.26, -24.35) * mm, "end": v(12.34, -24.47) * mm});
            skLineSegment(sketch, "E2030", {"start": v(12.34, -24.47) * mm, "end": v(12.4, -24.6) * mm});
            skLineSegment(sketch, "E2031", {"start": v(12.4, -24.6) * mm, "end": v(12.48, -24.74) * mm});
            skLineSegment(sketch, "E2032", {"start": v(12.48, -24.74) * mm, "end": v(12.52, -24.82) * mm});
            skLineSegment(sketch, "E2033", {"start": v(12.52, -24.82) * mm, "end": v(12.52, -24.82) * mm});
            skLineSegment(sketch, "E2034", {"start": v(12.52, -24.82) * mm, "end": v(12.52, -24.83) * mm});
            skLineSegment(sketch, "E2035", {"start": v(12.52, -24.83) * mm, "end": v(12.54, -24.86) * mm});
            skLineSegment(sketch, "E2036", {"start": v(12.54, -24.86) * mm, "end": v(12.56, -24.9) * mm});
            skLineSegment(sketch, "E2037", {"start": v(12.56, -24.9) * mm, "end": v(12.59, -24.94) * mm});
            skLineSegment(sketch, "E2038", {"start": v(12.59, -24.94) * mm, "end": v(12.63, -25) * mm});
            skLineSegment(sketch, "E2039", {"start": v(12.63, -25) * mm, "end": v(12.67, -25.06) * mm});
            skLineSegment(sketch, "E2040", {"start": v(12.67, -25.06) * mm, "end": v(12.72, -25.13) * mm});
            skLineSegment(sketch, "E2041", {"start": v(12.72, -25.13) * mm, "end": v(12.78, -25.22) * mm});
            skLineSegment(sketch, "E2042", {"start": v(12.78, -25.22) * mm, "end": v(12.85, -25.3) * mm});
            skLineSegment(sketch, "E2043", {"start": v(12.85, -25.3) * mm, "end": v(12.93, -25.4) * mm});
            skLineSegment(sketch, "E2044", {"start": v(12.93, -25.4) * mm, "end": v(13.02, -25.5) * mm});
            skLineSegment(sketch, "E2045", {"start": v(13.02, -25.5) * mm, "end": v(13.13, -25.62) * mm});
            skLineSegment(sketch, "E2046", {"start": v(13.13, -25.62) * mm, "end": v(13.24, -25.74) * mm});
            skLineSegment(sketch, "E2047", {"start": v(13.24, -25.74) * mm, "end": v(13.36, -25.87) * mm});
            skLineSegment(sketch, "E2048", {"start": v(13.36, -25.87) * mm, "end": v(13.5, -26) * mm});
            skLineSegment(sketch, "E2049", {"start": v(13.5, -26) * mm, "end": v(13.64, -26.14) * mm});
            skLineSegment(sketch, "E2050", {"start": v(13.64, -26.14) * mm, "end": v(13.8, -26.28) * mm});
            skLineSegment(sketch, "E2051", {"start": v(13.8, -26.28) * mm, "end": v(13.96, -26.43) * mm});
            skLineSegment(sketch, "E2052", {"start": v(13.96, -26.43) * mm, "end": v(14.14, -26.58) * mm});
            skLineSegment(sketch, "E2053", {"start": v(14.14, -26.58) * mm, "end": v(14.34, -26.74) * mm});
            skLineSegment(sketch, "E2054", {"start": v(14.34, -26.74) * mm, "end": v(14.5, -26.86) * mm});
            skLineSegment(sketch, "E2055", {"start": v(14.5, -26.86) * mm, "end": v(15.28, -26.46) * mm});
            skLineSegment(sketch, "E2056", {"start": v(15.28, -26.46) * mm, "end": v(16.01, -25.99) * mm});
            skLineSegment(sketch, "E2057", {"start": v(16.01, -25.99) * mm, "end": v(15.99, -25.79) * mm});
            skLineSegment(sketch, "E2058", {"start": v(15.99, -25.79) * mm, "end": v(15.95, -25.54) * mm});
            skLineSegment(sketch, "E2059", {"start": v(15.95, -25.54) * mm, "end": v(15.9, -25.3) * mm});
            skLineSegment(sketch, "E2060", {"start": v(15.9, -25.3) * mm, "end": v(15.86, -25.09) * mm});
            skLineSegment(sketch, "E2061", {"start": v(15.86, -25.09) * mm, "end": v(15.82, -24.88) * mm});
            skLineSegment(sketch, "E2062", {"start": v(15.82, -24.88) * mm, "end": v(15.77, -24.69) * mm});
            skLineSegment(sketch, "E2063", {"start": v(15.77, -24.69) * mm, "end": v(15.72, -24.5) * mm});
            skLineSegment(sketch, "E2064", {"start": v(15.72, -24.5) * mm, "end": v(15.68, -24.33) * mm});
            skLineSegment(sketch, "E2065", {"start": v(15.68, -24.33) * mm, "end": v(15.63, -24.18) * mm});
            skLineSegment(sketch, "E2066", {"start": v(15.63, -24.18) * mm, "end": v(15.58, -24.03) * mm});
            skLineSegment(sketch, "E2067", {"start": v(15.58, -24.03) * mm, "end": v(15.53, -23.9) * mm});
            skLineSegment(sketch, "E2068", {"start": v(15.53, -23.9) * mm, "end": v(15.49, -23.78) * mm});
            skLineSegment(sketch, "E2069", {"start": v(15.49, -23.78) * mm, "end": v(15.45, -23.68) * mm});
            skLineSegment(sketch, "E2070", {"start": v(15.45, -23.68) * mm, "end": v(15.4, -23.58) * mm});
            skLineSegment(sketch, "E2071", {"start": v(15.4, -23.58) * mm, "end": v(15.37, -23.5) * mm});
            skLineSegment(sketch, "E2072", {"start": v(15.37, -23.5) * mm, "end": v(15.33, -23.43) * mm});
            skLineSegment(sketch, "E2073", {"start": v(15.33, -23.43) * mm, "end": v(15.3, -23.37) * mm});
            skLineSegment(sketch, "E2074", {"start": v(15.3, -23.37) * mm, "end": v(15.28, -23.32) * mm});
            skLineSegment(sketch, "E2075", {"start": v(15.28, -23.32) * mm, "end": v(15.26, -23.29) * mm});
            skLineSegment(sketch, "E2076", {"start": v(15.26, -23.29) * mm, "end": v(15.24, -23.26) * mm});
            skLineSegment(sketch, "E2077", {"start": v(15.24, -23.26) * mm, "end": v(15.23, -23.25) * mm});
            skLineSegment(sketch, "E2078", {"start": v(15.23, -23.25) * mm, "end": v(15.23, -23.25) * mm});
            skLineSegment(sketch, "E2079", {"start": v(15.23, -23.25) * mm, "end": v(15.18, -23.18) * mm});
            skLineSegment(sketch, "E2080", {"start": v(15.18, -23.18) * mm, "end": v(15.1, -23.04) * mm});
            skLineSegment(sketch, "E2081", {"start": v(15.1, -23.04) * mm, "end": v(15.02, -22.92) * mm});
            skLineSegment(sketch, "E2082", {"start": v(15.02, -22.92) * mm, "end": v(14.96, -22.8) * mm});
            skLineSegment(sketch, "E2083", {"start": v(14.96, -22.8) * mm, "end": v(14.9, -22.69) * mm});
            skLineSegment(sketch, "E2084", {"start": v(14.9, -22.69) * mm, "end": v(14.87, -22.58) * mm});
            skLineSegment(sketch, "E2085", {"start": v(14.87, -22.58) * mm, "end": v(14.83, -22.49) * mm});
            skLineSegment(sketch, "E2086", {"start": v(14.83, -22.49) * mm, "end": v(14.81, -22.4) * mm});
            skLineSegment(sketch, "E2087", {"start": v(14.81, -22.4) * mm, "end": v(14.8, -22.32) * mm});
            skLineSegment(sketch, "E2088", {"start": v(14.8, -22.32) * mm, "end": v(14.8, -22.26) * mm});
            skLineSegment(sketch, "E2089", {"start": v(14.8, -22.26) * mm, "end": v(14.81, -22.2) * mm});
            skLineSegment(sketch, "E2090", {"start": v(14.81, -22.2) * mm, "end": v(14.83, -22.15) * mm});
            skLineSegment(sketch, "E2091", {"start": v(14.83, -22.15) * mm, "end": v(14.86, -22.11) * mm});
            skLineSegment(sketch, "E2092", {"start": v(14.86, -22.11) * mm, "end": v(14.89, -22.09) * mm});
            skLineSegment(sketch, "E2093", {"start": v(14.89, -22.09) * mm, "end": v(14.97, -22.03) * mm});
            skLineSegment(sketch, "E2094", {"start": v(14.97, -22.03) * mm, "end": v(15.43, -21.71) * mm});
            skLineSegment(sketch, "E2095", {"start": v(15.43, -21.71) * mm, "end": v(15.88, -21.39) * mm});
            skLineSegment(sketch, "E2096", {"start": v(15.88, -21.39) * mm, "end": v(16.33, -21.05) * mm});
            skLineSegment(sketch, "E2097", {"start": v(16.33, -21.05) * mm, "end": v(16.4, -20.99) * mm});
            skLineSegment(sketch, "E2098", {"start": v(16.4, -20.99) * mm, "end": v(16.44, -20.96) * mm});
            skLineSegment(sketch, "E2099", {"start": v(16.44, -20.96) * mm, "end": v(16.48, -20.95) * mm});
            skLineSegment(sketch, "E2100", {"start": v(16.48, -20.95) * mm, "end": v(16.54, -20.95) * mm});
            skLineSegment(sketch, "E2101", {"start": v(16.54, -20.95) * mm, "end": v(16.6, -20.96) * mm});
            skLineSegment(sketch, "E2102", {"start": v(16.6, -20.96) * mm, "end": v(16.66, -20.98) * mm});
            skLineSegment(sketch, "E2103", {"start": v(16.66, -20.98) * mm, "end": v(16.73, -21.01) * mm});
            skLineSegment(sketch, "E2104", {"start": v(16.73, -21.01) * mm, "end": v(16.8, -21.06) * mm});
            skLineSegment(sketch, "E2105", {"start": v(16.8, -21.06) * mm, "end": v(16.88, -21.12) * mm});
            skLineSegment(sketch, "E2106", {"start": v(16.88, -21.12) * mm, "end": v(16.97, -21.19) * mm});
            skLineSegment(sketch, "E2107", {"start": v(16.97, -21.19) * mm, "end": v(17.06, -21.27) * mm});
            skLineSegment(sketch, "E2108", {"start": v(17.06, -21.27) * mm, "end": v(17.15, -21.37) * mm});
            skLineSegment(sketch, "E2109", {"start": v(17.15, -21.37) * mm, "end": v(17.25, -21.48) * mm});
            skLineSegment(sketch, "E2110", {"start": v(17.25, -21.48) * mm, "end": v(17.35, -21.6) * mm});
            skLineSegment(sketch, "E2111", {"start": v(17.35, -21.6) * mm, "end": v(17.4, -21.67) * mm});
            skLineSegment(sketch, "E2112", {"start": v(17.4, -21.67) * mm, "end": v(17.4, -21.67) * mm});
            skLineSegment(sketch, "E2113", {"start": v(17.4, -21.67) * mm, "end": v(17.41, -21.69) * mm});
            skLineSegment(sketch, "E2114", {"start": v(17.41, -21.69) * mm, "end": v(17.43, -21.7) * mm});
            skLineSegment(sketch, "E2115", {"start": v(17.43, -21.7) * mm, "end": v(17.46, -21.74) * mm});
            skLineSegment(sketch, "E2116", {"start": v(17.46, -21.74) * mm, "end": v(17.5, -21.78) * mm});
            skLineSegment(sketch, "E2117", {"start": v(17.5, -21.78) * mm, "end": v(17.55, -21.82) * mm});
            skLineSegment(sketch, "E2118", {"start": v(17.55, -21.82) * mm, "end": v(17.6, -21.88) * mm});
            skLineSegment(sketch, "E2119", {"start": v(17.6, -21.88) * mm, "end": v(17.67, -21.94) * mm});
            skLineSegment(sketch, "E2120", {"start": v(17.67, -21.94) * mm, "end": v(17.75, -22) * mm});
            skLineSegment(sketch, "E2121", {"start": v(17.75, -22) * mm, "end": v(17.83, -22.08) * mm});
            skLineSegment(sketch, "E2122", {"start": v(17.83, -22.08) * mm, "end": v(17.93, -22.16) * mm});
            skLineSegment(sketch, "E2123", {"start": v(17.93, -22.16) * mm, "end": v(18.04, -22.24) * mm});
            skLineSegment(sketch, "E2124", {"start": v(18.04, -22.24) * mm, "end": v(18.17, -22.33) * mm});
            skLineSegment(sketch, "E2125", {"start": v(18.17, -22.33) * mm, "end": v(18.3, -22.43) * mm});
            skLineSegment(sketch, "E2126", {"start": v(18.3, -22.43) * mm, "end": v(18.45, -22.53) * mm});
            skLineSegment(sketch, "E2127", {"start": v(18.45, -22.53) * mm, "end": v(18.6, -22.63) * mm});
            skLineSegment(sketch, "E2128", {"start": v(18.6, -22.63) * mm, "end": v(18.77, -22.73) * mm});
            skLineSegment(sketch, "E2129", {"start": v(18.77, -22.73) * mm, "end": v(18.96, -22.84) * mm});
            skLineSegment(sketch, "E2130", {"start": v(18.96, -22.84) * mm, "end": v(19.15, -22.95) * mm});
            skLineSegment(sketch, "E2131", {"start": v(19.15, -22.95) * mm, "end": v(19.36, -23.06) * mm});
            skLineSegment(sketch, "E2132", {"start": v(19.36, -23.06) * mm, "end": v(19.58, -23.17) * mm});
            skLineSegment(sketch, "E2133", {"start": v(19.58, -23.17) * mm, "end": v(19.77, -23.26) * mm});
            skLineSegment(sketch, "E2134", {"start": v(19.77, -23.26) * mm, "end": v(20.45, -22.7) * mm});
            skLineSegment(sketch, "E2135", {"start": v(20.45, -22.7) * mm, "end": v(21.07, -22.1) * mm});
            skLineSegment(sketch, "E2136", {"start": v(21.07, -22.1) * mm, "end": v(21, -21.9) * mm});
            skLineSegment(sketch, "E2137", {"start": v(21, -21.9) * mm, "end": v(20.9, -21.67) * mm});
            skLineSegment(sketch, "E2138", {"start": v(20.9, -21.67) * mm, "end": v(20.82, -21.45) * mm});
            skLineSegment(sketch, "E2139", {"start": v(20.82, -21.45) * mm, "end": v(20.73, -21.24) * mm});
            skLineSegment(sketch, "E2140", {"start": v(20.73, -21.24) * mm, "end": v(20.65, -21.05) * mm});
            skLineSegment(sketch, "E2141", {"start": v(20.65, -21.05) * mm, "end": v(20.56, -20.87) * mm});
            skLineSegment(sketch, "E2142", {"start": v(20.56, -20.87) * mm, "end": v(20.47, -20.7) * mm});
            skLineSegment(sketch, "E2143", {"start": v(20.47, -20.7) * mm, "end": v(20.4, -20.54) * mm});
            skLineSegment(sketch, "E2144", {"start": v(20.4, -20.54) * mm, "end": v(20.31, -20.4) * mm});
            skLineSegment(sketch, "E2145", {"start": v(20.31, -20.4) * mm, "end": v(20.24, -20.27) * mm});
            skLineSegment(sketch, "E2146", {"start": v(20.24, -20.27) * mm, "end": v(20.16, -20.15) * mm});
            skLineSegment(sketch, "E2147", {"start": v(20.16, -20.15) * mm, "end": v(20.1, -20.04) * mm});
            skLineSegment(sketch, "E2148", {"start": v(20.1, -20.04) * mm, "end": v(20.03, -19.95) * mm});
            skLineSegment(sketch, "E2149", {"start": v(20.03, -19.95) * mm, "end": v(19.97, -19.87) * mm});
            skLineSegment(sketch, "E2150", {"start": v(19.97, -19.87) * mm, "end": v(19.92, -19.8) * mm});
            skLineSegment(sketch, "E2151", {"start": v(19.92, -19.8) * mm, "end": v(19.87, -19.73) * mm});
            skLineSegment(sketch, "E2152", {"start": v(19.87, -19.73) * mm, "end": v(19.83, -19.68) * mm});
            skLineSegment(sketch, "E2153", {"start": v(19.83, -19.68) * mm, "end": v(19.8, -19.64) * mm});
            skLineSegment(sketch, "E2154", {"start": v(19.8, -19.64) * mm, "end": v(19.77, -19.6) * mm});
            skLineSegment(sketch, "E2155", {"start": v(19.77, -19.6) * mm, "end": v(19.75, -19.59) * mm});
            skLineSegment(sketch, "E2156", {"start": v(19.75, -19.59) * mm, "end": v(19.74, -19.57) * mm});
            skLineSegment(sketch, "E2157", {"start": v(19.74, -19.57) * mm, "end": v(19.73, -19.57) * mm});
            skLineSegment(sketch, "E2158", {"start": v(19.73, -19.57) * mm, "end": v(19.67, -19.51) * mm});
            skLineSegment(sketch, "E2159", {"start": v(19.67, -19.51) * mm, "end": v(19.56, -19.4) * mm});
            skLineSegment(sketch, "E2160", {"start": v(19.56, -19.4) * mm, "end": v(19.46, -19.3) * mm});
            skLineSegment(sketch, "E2161", {"start": v(19.46, -19.3) * mm, "end": v(19.37, -19.19) * mm});
            skLineSegment(sketch, "E2162", {"start": v(19.37, -19.19) * mm, "end": v(19.3, -19.1) * mm});
            skLineSegment(sketch, "E2163", {"start": v(19.3, -19.1) * mm, "end": v(19.24, -19) * mm});
            skLineSegment(sketch, "E2164", {"start": v(19.24, -19) * mm, "end": v(19.19, -18.91) * mm});
            skLineSegment(sketch, "E2165", {"start": v(19.19, -18.91) * mm, "end": v(19.15, -18.83) * mm});
            skLineSegment(sketch, "E2166", {"start": v(19.15, -18.83) * mm, "end": v(19.12, -18.76) * mm});
            skLineSegment(sketch, "E2167", {"start": v(19.12, -18.76) * mm, "end": v(19.1, -18.7) * mm});
            skLineSegment(sketch, "E2168", {"start": v(19.1, -18.7) * mm, "end": v(19.1, -18.63) * mm});
            skLineSegment(sketch, "E2169", {"start": v(19.1, -18.63) * mm, "end": v(19.11, -18.58) * mm});
            skLineSegment(sketch, "E2170", {"start": v(19.11, -18.58) * mm, "end": v(19.13, -18.54) * mm});
            skLineSegment(sketch, "E2171", {"start": v(19.13, -18.54) * mm, "end": v(19.16, -18.51) * mm});
            skLineSegment(sketch, "E2172", {"start": v(19.16, -18.51) * mm, "end": v(19.23, -18.44) * mm});
            skLineSegment(sketch, "E2173", {"start": v(19.23, -18.44) * mm, "end": v(19.6, -18.03) * mm});
            skLineSegment(sketch, "E2174", {"start": v(19.6, -18.03) * mm, "end": v(19.98, -17.62) * mm});
            skLineSegment(sketch, "E2175", {"start": v(19.98, -17.62) * mm, "end": v(20.35, -17.2) * mm});
            skLineSegment(sketch, "E2176", {"start": v(20.35, -17.2) * mm, "end": v(20.41, -17.12) * mm});
            skLineSegment(sketch, "E2177", {"start": v(20.41, -17.12) * mm, "end": v(20.44, -17.09) * mm});
            skLineSegment(sketch, "E2178", {"start": v(20.44, -17.09) * mm, "end": v(20.48, -17.06) * mm});
            skLineSegment(sketch, "E2179", {"start": v(20.48, -17.06) * mm, "end": v(20.53, -17.05) * mm});
            skLineSegment(sketch, "E2180", {"start": v(20.53, -17.05) * mm, "end": v(20.59, -17.05) * mm});
            skLineSegment(sketch, "E2181", {"start": v(20.59, -17.05) * mm, "end": v(20.65, -17.06) * mm});
            skLineSegment(sketch, "E2182", {"start": v(20.65, -17.06) * mm, "end": v(20.73, -17.08) * mm});
            skLineSegment(sketch, "E2183", {"start": v(20.73, -17.08) * mm, "end": v(20.81, -17.1) * mm});
            skLineSegment(sketch, "E2184", {"start": v(20.81, -17.1) * mm, "end": v(20.9, -17.14) * mm});
            skLineSegment(sketch, "E2185", {"start": v(20.9, -17.14) * mm, "end": v(21, -17.2) * mm});
            skLineSegment(sketch, "E2186", {"start": v(21, -17.2) * mm, "end": v(21.1, -17.26) * mm});
            skLineSegment(sketch, "E2187", {"start": v(21.1, -17.26) * mm, "end": v(21.22, -17.33) * mm});
            skLineSegment(sketch, "E2188", {"start": v(21.22, -17.33) * mm, "end": v(21.34, -17.42) * mm});
            skLineSegment(sketch, "E2189", {"start": v(21.34, -17.42) * mm, "end": v(21.46, -17.52) * mm});
            skLineSegment(sketch, "E2190", {"start": v(21.46, -17.52) * mm, "end": v(21.53, -17.58) * mm});
            skLineSegment(sketch, "E2191", {"start": v(21.53, -17.58) * mm, "end": v(21.53, -17.58) * mm});
            skLineSegment(sketch, "E2192", {"start": v(21.53, -17.58) * mm, "end": v(21.54, -17.6) * mm});
            skLineSegment(sketch, "E2193", {"start": v(21.54, -17.6) * mm, "end": v(21.57, -17.6) * mm});
            skLineSegment(sketch, "E2194", {"start": v(21.57, -17.6) * mm, "end": v(21.6, -17.63) * mm});
            skLineSegment(sketch, "E2195", {"start": v(21.6, -17.63) * mm, "end": v(21.64, -17.66) * mm});
            skLineSegment(sketch, "E2196", {"start": v(21.64, -17.66) * mm, "end": v(21.7, -17.7) * mm});
            skLineSegment(sketch, "E2197", {"start": v(21.7, -17.7) * mm, "end": v(21.77, -17.74) * mm});
            skLineSegment(sketch, "E2198", {"start": v(21.77, -17.74) * mm, "end": v(21.84, -17.79) * mm});
            skLineSegment(sketch, "E2199", {"start": v(21.84, -17.79) * mm, "end": v(21.93, -17.84) * mm});
            skLineSegment(sketch, "E2200", {"start": v(21.93, -17.84) * mm, "end": v(22.04, -17.89) * mm});
            skLineSegment(sketch, "E2201", {"start": v(22.04, -17.89) * mm, "end": v(22.15, -17.95) * mm});
            skLineSegment(sketch, "E2202", {"start": v(22.15, -17.95) * mm, "end": v(22.27, -18) * mm});
            skLineSegment(sketch, "E2203", {"start": v(22.27, -18) * mm, "end": v(22.41, -18.07) * mm});
            skLineSegment(sketch, "E2204", {"start": v(22.41, -18.07) * mm, "end": v(22.56, -18.13) * mm});
            skLineSegment(sketch, "E2205", {"start": v(22.56, -18.13) * mm, "end": v(22.73, -18.2) * mm});
            skLineSegment(sketch, "E2206", {"start": v(22.73, -18.2) * mm, "end": v(22.9, -18.27) * mm});
            skLineSegment(sketch, "E2207", {"start": v(22.9, -18.27) * mm, "end": v(23.09, -18.33) * mm});
            skLineSegment(sketch, "E2208", {"start": v(23.09, -18.33) * mm, "end": v(23.3, -18.4) * mm});
            skLineSegment(sketch, "E2209", {"start": v(23.3, -18.4) * mm, "end": v(23.5, -18.47) * mm});
            skLineSegment(sketch, "E2210", {"start": v(23.5, -18.47) * mm, "end": v(23.73, -18.53) * mm});
            skLineSegment(sketch, "E2211", {"start": v(23.73, -18.53) * mm, "end": v(23.97, -18.6) * mm});
            skLineSegment(sketch, "E2212", {"start": v(23.97, -18.6) * mm, "end": v(24.17, -18.64) * mm});
            skLineSegment(sketch, "E2213", {"start": v(24.17, -18.64) * mm, "end": v(24.72, -17.96) * mm});
            skLineSegment(sketch, "E2214", {"start": v(24.72, -17.96) * mm, "end": v(25.2, -17.23) * mm});
            skLineSegment(sketch, "E2215", {"start": v(25.2, -17.23) * mm, "end": v(25.1, -17.05) * mm});
            skLineSegment(sketch, "E2216", {"start": v(25.1, -17.05) * mm, "end": v(24.96, -16.85) * mm});
            skLineSegment(sketch, "E2217", {"start": v(24.96, -16.85) * mm, "end": v(24.83, -16.65) * mm});
            skLineSegment(sketch, "E2218", {"start": v(24.83, -16.65) * mm, "end": v(24.7, -16.47) * mm});
            skLineSegment(sketch, "E2219", {"start": v(24.7, -16.47) * mm, "end": v(24.57, -16.3) * mm});
            skLineSegment(sketch, "E2220", {"start": v(24.57, -16.3) * mm, "end": v(24.45, -16.14) * mm});
            skLineSegment(sketch, "E2221", {"start": v(24.45, -16.14) * mm, "end": v(24.33, -15.99) * mm});
            skLineSegment(sketch, "E2222", {"start": v(24.33, -15.99) * mm, "end": v(24.22, -15.85) * mm});
            skLineSegment(sketch, "E2223", {"start": v(24.22, -15.85) * mm, "end": v(24.11, -15.73) * mm});
            skLineSegment(sketch, "E2224", {"start": v(24.11, -15.73) * mm, "end": v(24, -15.62) * mm});
            skLineSegment(sketch, "E2225", {"start": v(24, -15.62) * mm, "end": v(23.91, -15.52) * mm});
            skLineSegment(sketch, "E2226", {"start": v(23.91, -15.52) * mm, "end": v(23.82, -15.43) * mm});
            skLineSegment(sketch, "E2227", {"start": v(23.82, -15.43) * mm, "end": v(23.74, -15.35) * mm});
            skLineSegment(sketch, "E2228", {"start": v(23.74, -15.35) * mm, "end": v(23.67, -15.28) * mm});
            skLineSegment(sketch, "E2229", {"start": v(23.67, -15.28) * mm, "end": v(23.6, -15.22) * mm});
            skLineSegment(sketch, "E2230", {"start": v(23.6, -15.22) * mm, "end": v(23.54, -15.17) * mm});
            skLineSegment(sketch, "E2231", {"start": v(23.54, -15.17) * mm, "end": v(23.49, -15.13) * mm});
            skLineSegment(sketch, "E2232", {"start": v(23.49, -15.13) * mm, "end": v(23.45, -15.1) * mm});
            skLineSegment(sketch, "E2233", {"start": v(23.45, -15.1) * mm, "end": v(23.41, -15.07) * mm});
            skLineSegment(sketch, "E2234", {"start": v(23.41, -15.07) * mm, "end": v(23.39, -15.05) * mm});
            skLineSegment(sketch, "E2235", {"start": v(23.39, -15.05) * mm, "end": v(23.37, -15.04) * mm});
            skLineSegment(sketch, "E2236", {"start": v(23.37, -15.04) * mm, "end": v(23.37, -15.04) * mm});
            skLineSegment(sketch, "E2237", {"start": v(23.37, -15.04) * mm, "end": v(23.3, -15) * mm});
            skLineSegment(sketch, "E2238", {"start": v(23.3, -15) * mm, "end": v(23.16, -14.91) * mm});
            skLineSegment(sketch, "E2239", {"start": v(23.16, -14.91) * mm, "end": v(23.04, -14.83) * mm});
            skLineSegment(sketch, "E2240", {"start": v(23.04, -14.83) * mm, "end": v(22.94, -14.74) * mm});
            skLineSegment(sketch, "E2241", {"start": v(22.94, -14.74) * mm, "end": v(22.84, -14.66) * mm});
            skLineSegment(sketch, "E2242", {"start": v(22.84, -14.66) * mm, "end": v(22.77, -14.58) * mm});
            skLineSegment(sketch, "E2243", {"start": v(22.77, -14.58) * mm, "end": v(22.7, -14.5) * mm});
            skLineSegment(sketch, "E2244", {"start": v(22.7, -14.5) * mm, "end": v(22.65, -14.44) * mm});
            skLineSegment(sketch, "E2245", {"start": v(22.65, -14.44) * mm, "end": v(22.6, -14.37) * mm});
            skLineSegment(sketch, "E2246", {"start": v(22.6, -14.37) * mm, "end": v(22.58, -14.31) * mm});
            skLineSegment(sketch, "E2247", {"start": v(22.58, -14.31) * mm, "end": v(22.56, -14.25) * mm});
            skLineSegment(sketch, "E2248", {"start": v(22.56, -14.25) * mm, "end": v(22.56, -14.2) * mm});
            skLineSegment(sketch, "E2249", {"start": v(22.56, -14.2) * mm, "end": v(22.57, -14.16) * mm});
            skLineSegment(sketch, "E2250", {"start": v(22.57, -14.16) * mm, "end": v(22.59, -14.12) * mm});
            skLineSegment(sketch, "E2251", {"start": v(22.59, -14.12) * mm, "end": v(22.64, -14.04) * mm});
            skLineSegment(sketch, "E2252", {"start": v(22.64, -14.04) * mm, "end": v(22.93, -13.56) * mm});
            skLineSegment(sketch, "E2253", {"start": v(22.93, -13.56) * mm, "end": v(23.2, -13.08) * mm});
            skLineSegment(sketch, "E2254", {"start": v(23.2, -13.08) * mm, "end": v(23.48, -12.59) * mm});
            skLineSegment(sketch, "E2255", {"start": v(23.48, -12.59) * mm, "end": v(23.52, -12.5) * mm});
            skLineSegment(sketch, "E2256", {"start": v(23.52, -12.5) * mm, "end": v(23.55, -12.46) * mm});
            skLineSegment(sketch, "E2257", {"start": v(23.55, -12.46) * mm, "end": v(23.58, -12.43) * mm});
            skLineSegment(sketch, "E2258", {"start": v(23.58, -12.43) * mm, "end": v(23.63, -12.41) * mm});
            skLineSegment(sketch, "E2259", {"start": v(23.63, -12.41) * mm, "end": v(23.68, -12.4) * mm});
            skLineSegment(sketch, "E2260", {"start": v(23.68, -12.4) * mm, "end": v(23.75, -12.4) * mm});
            skLineSegment(sketch, "E2261", {"start": v(23.75, -12.4) * mm, "end": v(23.83, -12.4) * mm});
            skLineSegment(sketch, "E2262", {"start": v(23.83, -12.4) * mm, "end": v(23.92, -12.4) * mm});
            skLineSegment(sketch, "E2263", {"start": v(23.92, -12.4) * mm, "end": v(24.01, -12.42) * mm});
            skLineSegment(sketch, "E2264", {"start": v(24.01, -12.42) * mm, "end": v(24.12, -12.45) * mm});
            skLineSegment(sketch, "E2265", {"start": v(24.12, -12.45) * mm, "end": v(24.24, -12.5) * mm});
            skLineSegment(sketch, "E2266", {"start": v(24.24, -12.5) * mm, "end": v(24.36, -12.54) * mm});
            skLineSegment(sketch, "E2267", {"start": v(24.36, -12.54) * mm, "end": v(24.5, -12.6) * mm});
            skLineSegment(sketch, "E2268", {"start": v(24.5, -12.6) * mm, "end": v(24.64, -12.68) * mm});
            skLineSegment(sketch, "E2269", {"start": v(24.64, -12.68) * mm, "end": v(24.71, -12.72) * mm});
            skLineSegment(sketch, "E2270", {"start": v(24.71, -12.72) * mm, "end": v(24.71, -12.72) * mm});
            skLineSegment(sketch, "E2271", {"start": v(24.71, -12.72) * mm, "end": v(24.73, -12.73) * mm});
            skLineSegment(sketch, "E2272", {"start": v(24.73, -12.73) * mm, "end": v(24.76, -12.74) * mm});
            skLineSegment(sketch, "E2273", {"start": v(24.76, -12.74) * mm, "end": v(24.8, -12.76) * mm});
            skLineSegment(sketch, "E2274", {"start": v(24.8, -12.76) * mm, "end": v(24.84, -12.78) * mm});
            skLineSegment(sketch, "E2275", {"start": v(24.84, -12.78) * mm, "end": v(24.9, -12.8) * mm});
            skLineSegment(sketch, "E2276", {"start": v(24.9, -12.8) * mm, "end": v(24.98, -12.83) * mm});
            skLineSegment(sketch, "E2277", {"start": v(24.98, -12.83) * mm, "end": v(25.07, -12.86) * mm});
            skLineSegment(sketch, "E2278", {"start": v(25.07, -12.86) * mm, "end": v(25.16, -12.89) * mm});
            skLineSegment(sketch, "E2279", {"start": v(25.16, -12.89) * mm, "end": v(25.27, -12.92) * mm});
            skLineSegment(sketch, "E2280", {"start": v(25.27, -12.92) * mm, "end": v(25.4, -12.95) * mm});
            skLineSegment(sketch, "E2281", {"start": v(25.4, -12.95) * mm, "end": v(25.53, -12.98) * mm});
            skLineSegment(sketch, "E2282", {"start": v(25.53, -12.98) * mm, "end": v(25.68, -13.01) * mm});
            skLineSegment(sketch, "E2283", {"start": v(25.68, -13.01) * mm, "end": v(25.84, -13.05) * mm});
            skLineSegment(sketch, "E2284", {"start": v(25.84, -13.05) * mm, "end": v(26.01, -13.08) * mm});
            skLineSegment(sketch, "E2285", {"start": v(26.01, -13.08) * mm, "end": v(26.2, -13.1) * mm});
            skLineSegment(sketch, "E2286", {"start": v(26.2, -13.1) * mm, "end": v(26.4, -13.13) * mm});
            skLineSegment(sketch, "E2287", {"start": v(26.4, -13.13) * mm, "end": v(26.6, -13.15) * mm});
            skLineSegment(sketch, "E2288", {"start": v(26.6, -13.15) * mm, "end": v(26.83, -13.17) * mm});
            skLineSegment(sketch, "E2289", {"start": v(26.83, -13.17) * mm, "end": v(27.07, -13.2) * mm});
            skLineSegment(sketch, "E2290", {"start": v(27.07, -13.2) * mm, "end": v(27.32, -13.2) * mm});
            skLineSegment(sketch, "E2291", {"start": v(27.32, -13.2) * mm, "end": v(27.52, -13.2) * mm});
            skLineSegment(sketch, "E2292", {"start": v(27.52, -13.2) * mm, "end": v(27.92, -12.43) * mm});
            skLineSegment(sketch, "E2293", {"start": v(27.92, -12.43) * mm, "end": v(28.23, -11.61) * mm});
            skLineSegment(sketch, "E2294", {"start": v(28.23, -11.61) * mm, "end": v(28.09, -11.47) * mm});
            skLineSegment(sketch, "E2295", {"start": v(28.09, -11.47) * mm, "end": v(27.91, -11.29) * mm});
            skLineSegment(sketch, "E2296", {"start": v(27.91, -11.29) * mm, "end": v(27.74, -11.12) * mm});
            skLineSegment(sketch, "E2297", {"start": v(27.74, -11.12) * mm, "end": v(27.58, -10.97) * mm});
            skLineSegment(sketch, "E2298", {"start": v(27.58, -10.97) * mm, "end": v(27.42, -10.83) * mm});
            skLineSegment(sketch, "E2299", {"start": v(27.42, -10.83) * mm, "end": v(27.27, -10.7) * mm});
            skLineSegment(sketch, "E2300", {"start": v(27.27, -10.7) * mm, "end": v(27.12, -10.58) * mm});
            skLineSegment(sketch, "E2301", {"start": v(27.12, -10.58) * mm, "end": v(26.99, -10.47) * mm});
            skLineSegment(sketch, "E2302", {"start": v(26.99, -10.47) * mm, "end": v(26.85, -10.38) * mm});
            skLineSegment(sketch, "E2303", {"start": v(26.85, -10.38) * mm, "end": v(26.73, -10.29) * mm});
            skLineSegment(sketch, "E2304", {"start": v(26.73, -10.29) * mm, "end": v(26.62, -10.2) * mm});
            skLineSegment(sketch, "E2305", {"start": v(26.62, -10.2) * mm, "end": v(26.51, -10.14) * mm});
            skLineSegment(sketch, "E2306", {"start": v(26.51, -10.14) * mm, "end": v(26.41, -10.08) * mm});
            skLineSegment(sketch, "E2307", {"start": v(26.41, -10.08) * mm, "end": v(26.33, -10.03) * mm});
            skLineSegment(sketch, "E2308", {"start": v(26.33, -10.03) * mm, "end": v(26.25, -9.98) * mm});
            skLineSegment(sketch, "E2309", {"start": v(26.25, -9.98) * mm, "end": v(26.18, -9.94) * mm});
            skLineSegment(sketch, "E2310", {"start": v(26.18, -9.94) * mm, "end": v(26.12, -9.91) * mm});
            skLineSegment(sketch, "E2311", {"start": v(26.12, -9.91) * mm, "end": v(26.07, -9.89) * mm});
            skLineSegment(sketch, "E2312", {"start": v(26.07, -9.89) * mm, "end": v(26.03, -9.87) * mm});
            skLineSegment(sketch, "E2313", {"start": v(26.03, -9.87) * mm, "end": v(26, -9.86) * mm});
            skLineSegment(sketch, "E2314", {"start": v(26, -9.86) * mm, "end": v(26, -9.85) * mm});
            skLineSegment(sketch, "E2315", {"start": v(26, -9.85) * mm, "end": v(25.99, -9.85) * mm});
            skLineSegment(sketch, "E2316", {"start": v(25.99, -9.85) * mm, "end": v(25.9, -9.82) * mm});
            skLineSegment(sketch, "E2317", {"start": v(25.9, -9.82) * mm, "end": v(25.76, -9.77) * mm});
            skLineSegment(sketch, "E2318", {"start": v(25.76, -9.77) * mm, "end": v(25.62, -9.71) * mm});
            skLineSegment(sketch, "E2319", {"start": v(25.62, -9.71) * mm, "end": v(25.5, -9.65) * mm});
            skLineSegment(sketch, "E2320", {"start": v(25.5, -9.65) * mm, "end": v(25.4, -9.6) * mm});
            skLineSegment(sketch, "E2321", {"start": v(25.4, -9.6) * mm, "end": v(25.3, -9.53) * mm});
            skLineSegment(sketch, "E2322", {"start": v(25.3, -9.53) * mm, "end": v(25.22, -9.47) * mm});
            skLineSegment(sketch, "E2323", {"start": v(25.22, -9.47) * mm, "end": v(25.15, -9.41) * mm});
            skLineSegment(sketch, "E2324", {"start": v(25.15, -9.41) * mm, "end": v(25.1, -9.36) * mm});
            skLineSegment(sketch, "E2325", {"start": v(25.1, -9.36) * mm, "end": v(25.06, -9.3) * mm});
            skLineSegment(sketch, "E2326", {"start": v(25.06, -9.3) * mm, "end": v(25.03, -9.25) * mm});
            skLineSegment(sketch, "E2327", {"start": v(25.03, -9.25) * mm, "end": v(25.02, -9.2) * mm});
            skLineSegment(sketch, "E2328", {"start": v(25.02, -9.2) * mm, "end": v(25.02, -9.16) * mm});
            skLineSegment(sketch, "E2329", {"start": v(25.02, -9.16) * mm, "end": v(25.03, -9.12) * mm});
            skLineSegment(sketch, "E2330", {"start": v(25.03, -9.12) * mm, "end": v(25.06, -9.02) * mm});
            skLineSegment(sketch, "E2331", {"start": v(25.06, -9.02) * mm, "end": v(25.25, -8.5) * mm});
            skLineSegment(sketch, "E2332", {"start": v(25.25, -8.5) * mm, "end": v(25.42, -7.97) * mm});
            skLineSegment(sketch, "E2333", {"start": v(25.42, -7.97) * mm, "end": v(25.58, -7.43) * mm});
            skLineSegment(sketch, "E2334", {"start": v(25.58, -7.43) * mm, "end": v(25.6, -7.33) * mm});
            skLineSegment(sketch, "E2335", {"start": v(25.6, -7.33) * mm, "end": v(25.62, -7.3) * mm});
            skLineSegment(sketch, "E2336", {"start": v(25.62, -7.3) * mm, "end": v(25.65, -7.26) * mm});
            skLineSegment(sketch, "E2337", {"start": v(25.65, -7.26) * mm, "end": v(25.69, -7.23) * mm});
            skLineSegment(sketch, "E2338", {"start": v(25.69, -7.23) * mm, "end": v(25.74, -7.2) * mm});
            skLineSegment(sketch, "E2339", {"start": v(25.74, -7.2) * mm, "end": v(25.8, -7.18) * mm});
            skLineSegment(sketch, "E2340", {"start": v(25.8, -7.18) * mm, "end": v(25.88, -7.17) * mm});
            skLineSegment(sketch, "E2341", {"start": v(25.88, -7.17) * mm, "end": v(25.97, -7.16) * mm});
            skLineSegment(sketch, "E2342", {"start": v(25.97, -7.16) * mm, "end": v(26.07, -7.16) * mm});
            skLineSegment(sketch, "E2343", {"start": v(26.07, -7.16) * mm, "end": v(26.18, -7.17) * mm});
            skLineSegment(sketch, "E2344", {"start": v(26.18, -7.17) * mm, "end": v(26.3, -7.18) * mm});
            skLineSegment(sketch, "E2345", {"start": v(26.3, -7.18) * mm, "end": v(26.44, -7.2) * mm});
            skLineSegment(sketch, "E2346", {"start": v(26.44, -7.2) * mm, "end": v(26.58, -7.24) * mm});
            skLineSegment(sketch, "E2347", {"start": v(26.58, -7.24) * mm, "end": v(26.73, -7.28) * mm});
            skLineSegment(sketch, "E2348", {"start": v(26.73, -7.28) * mm, "end": v(26.82, -7.3) * mm});
            skLineSegment(sketch, "E2349", {"start": v(26.82, -7.3) * mm, "end": v(26.82, -7.3) * mm});
            skLineSegment(sketch, "E2350", {"start": v(26.82, -7.3) * mm, "end": v(26.84, -7.3) * mm});
            skLineSegment(sketch, "E2351", {"start": v(26.84, -7.3) * mm, "end": v(26.86, -7.32) * mm});
            skLineSegment(sketch, "E2352", {"start": v(26.86, -7.32) * mm, "end": v(26.9, -7.32) * mm});
            skLineSegment(sketch, "E2353", {"start": v(26.9, -7.32) * mm, "end": v(26.96, -7.33) * mm});
            skLineSegment(sketch, "E2354", {"start": v(26.96, -7.33) * mm, "end": v(27.02, -7.34) * mm});
            skLineSegment(sketch, "E2355", {"start": v(27.02, -7.34) * mm, "end": v(27.1, -7.35) * mm});
            skLineSegment(sketch, "E2356", {"start": v(27.1, -7.35) * mm, "end": v(27.2, -7.36) * mm});
            skLineSegment(sketch, "E2357", {"start": v(27.2, -7.36) * mm, "end": v(27.3, -7.37) * mm});
            skLineSegment(sketch, "E2358", {"start": v(27.3, -7.37) * mm, "end": v(27.4, -7.38) * mm});
            skLineSegment(sketch, "E2359", {"start": v(27.4, -7.38) * mm, "end": v(27.53, -7.39) * mm});
            skLineSegment(sketch, "E2360", {"start": v(27.53, -7.39) * mm, "end": v(27.67, -7.39) * mm});
            skLineSegment(sketch, "E2361", {"start": v(27.67, -7.39) * mm, "end": v(27.82, -7.4) * mm});
            skLineSegment(sketch, "E2362", {"start": v(27.82, -7.4) * mm, "end": v(27.99, -7.39) * mm});
            skLineSegment(sketch, "E2363", {"start": v(27.99, -7.39) * mm, "end": v(28.16, -7.38) * mm});
            skLineSegment(sketch, "E2364", {"start": v(28.16, -7.38) * mm, "end": v(28.35, -7.37) * mm});
            skLineSegment(sketch, "E2365", {"start": v(28.35, -7.37) * mm, "end": v(28.55, -7.36) * mm});
            skLineSegment(sketch, "E2366", {"start": v(28.55, -7.36) * mm, "end": v(28.76, -7.33) * mm});
            skLineSegment(sketch, "E2367", {"start": v(28.76, -7.33) * mm, "end": v(28.98, -7.3) * mm});
            skLineSegment(sketch, "E2368", {"start": v(28.98, -7.3) * mm, "end": v(29.22, -7.28) * mm});
            skLineSegment(sketch, "E2369", {"start": v(29.22, -7.28) * mm, "end": v(29.46, -7.23) * mm});
            skLineSegment(sketch, "E2370", {"start": v(29.46, -7.23) * mm, "end": v(29.66, -7.2) * mm});
            skSolve(sketch);
        }
        {
            var Q0;
            Q0=makeQuery(id+"F0.imprint","IMPRINT",FACE,{"disambiguationData":[TD([[makeQuery(id+"F0.imprint","IMPRINT",EDGE,{"derivedFrom":sQuery(id+"F0.wireOp",EDGE,"E0")}),-1.0]])]});
            extrude(context, id + "F1", {"entities" : qUnion([Q0]), "depth" : 1 * mm});
        }
        {
            var Q0;
            Q0=makeQuery(id+"F1.opExtrude","CAP_FACE",FACE,{"disambiguationData":[OSD([sQuery(id+"F0.wireOp",EDGE,"E0"),sQuery(id+"F0.wireOp",EDGE,"E1"),sQuery(id+"F0.wireOp",EDGE,"E2"),sQuery(id+"F0.wireOp",EDGE,"E3"),sQuery(id+"F0.wireOp",EDGE,"E4"),sQuery(id+"F0.wireOp",EDGE,"E5"),sQuery(id+"F0.wireOp",EDGE,"E6"),sQuery(id+"F0.wireOp",EDGE,"E7"),sQuery(id+"F0.wireOp",EDGE,"E8"),sQuery(id+"F0.wireOp",EDGE,"E9"),sQuery(id+"F0.wireOp",EDGE,"E10"),sQuery(id+"F0.wireOp",EDGE,"E11"),sQuery(id+"F0.wireOp",EDGE,"E12"),sQuery(id+"F0.wireOp",EDGE,"E13"),sQuery(id+"F0.wireOp",EDGE,"E14"),sQuery(id+"F0.wireOp",EDGE,"E15"),sQuery(id+"F0.wireOp",EDGE,"E16"),sQuery(id+"F0.wireOp",EDGE,"E17"),sQuery(id+"F0.wireOp",EDGE,"E18"),sQuery(id+"F0.wireOp",EDGE,"E19"),sQuery(id+"F0.wireOp",EDGE,"E20"),sQuery(id+"F0.wireOp",EDGE,"E21"),sQuery(id+"F0.wireOp",EDGE,"E22"),sQuery(id+"F0.wireOp",EDGE,"E23"),sQuery(id+"F0.wireOp",EDGE,"E24"),sQuery(id+"F0.wireOp",EDGE,"E25"),sQuery(id+"F0.wireOp",EDGE,"E26"),sQuery(id+"F0.wireOp",EDGE,"E27"),sQuery(id+"F0.wireOp",EDGE,"E28"),sQuery(id+"F0.wireOp",EDGE,"E29"),sQuery(id+"F0.wireOp",EDGE,"E30"),sQuery(id+"F0.wireOp",EDGE,"E31"),sQuery(id+"F0.wireOp",EDGE,"E32"),sQuery(id+"F0.wireOp",EDGE,"E33"),sQuery(id+"F0.wireOp",EDGE,"E34"),sQuery(id+"F0.wireOp",EDGE,"E35"),sQuery(id+"F0.wireOp",EDGE,"E36"),sQuery(id+"F0.wireOp",EDGE,"E37"),sQuery(id+"F0.wireOp",EDGE,"E38"),sQuery(id+"F0.wireOp",EDGE,"E39"),sQuery(id+"F0.wireOp",EDGE,"E40"),sQuery(id+"F0.wireOp",EDGE,"E41"),sQuery(id+"F0.wireOp",EDGE,"E42"),sQuery(id+"F0.wireOp",EDGE,"E43"),sQuery(id+"F0.wireOp",EDGE,"E44"),sQuery(id+"F0.wireOp",EDGE,"E45"),sQuery(id+"F0.wireOp",EDGE,"E46"),sQuery(id+"F0.wireOp",EDGE,"E47"),sQuery(id+"F0.wireOp",EDGE,"E48"),sQuery(id+"F0.wireOp",EDGE,"E49"),sQuery(id+"F0.wireOp",EDGE,"E50"),sQuery(id+"F0.wireOp",EDGE,"E51"),sQuery(id+"F0.wireOp",EDGE,"E52"),sQuery(id+"F0.wireOp",EDGE,"E53"),sQuery(id+"F0.wireOp",EDGE,"E54"),sQuery(id+"F0.wireOp",EDGE,"E55"),sQuery(id+"F0.wireOp",EDGE,"E56"),sQuery(id+"F0.wireOp",EDGE,"E57"),sQuery(id+"F0.wireOp",EDGE,"E58"),sQuery(id+"F0.wireOp",EDGE,"E59"),sQuery(id+"F0.wireOp",EDGE,"E60"),sQuery(id+"F0.wireOp",EDGE,"E61"),sQuery(id+"F0.wireOp",EDGE,"E62"),sQuery(id+"F0.wireOp",EDGE,"E63"),sQuery(id+"F0.wireOp",EDGE,"E64"),sQuery(id+"F0.wireOp",EDGE,"E65"),sQuery(id+"F0.wireOp",EDGE,"E66"),sQuery(id+"F0.wireOp",EDGE,"E67"),sQuery(id+"F0.wireOp",EDGE,"E68"),sQuery(id+"F0.wireOp",EDGE,"E69"),sQuery(id+"F0.wireOp",EDGE,"E70"),sQuery(id+"F0.wireOp",EDGE,"E71"),sQuery(id+"F0.wireOp",EDGE,"E72"),sQuery(id+"F0.wireOp",EDGE,"E73"),sQuery(id+"F0.wireOp",EDGE,"E74"),sQuery(id+"F0.wireOp",EDGE,"E75"),sQuery(id+"F0.wireOp",EDGE,"E76"),sQuery(id+"F0.wireOp",EDGE,"E77"),sQuery(id+"F0.wireOp",EDGE,"E78"),sQuery(id+"F0.wireOp",EDGE,"E79"),sQuery(id+"F0.wireOp",EDGE,"E80"),sQuery(id+"F0.wireOp",EDGE,"E81"),sQuery(id+"F0.wireOp",EDGE,"E82"),sQuery(id+"F0.wireOp",EDGE,"E83"),sQuery(id+"F0.wireOp",EDGE,"E84"),sQuery(id+"F0.wireOp",EDGE,"E85"),sQuery(id+"F0.wireOp",EDGE,"E86"),sQuery(id+"F0.wireOp",EDGE,"E87"),sQuery(id+"F0.wireOp",EDGE,"E88"),sQuery(id+"F0.wireOp",EDGE,"E89"),sQuery(id+"F0.wireOp",EDGE,"E90"),sQuery(id+"F0.wireOp",EDGE,"E91"),sQuery(id+"F0.wireOp",EDGE,"E92"),sQuery(id+"F0.wireOp",EDGE,"E93"),sQuery(id+"F0.wireOp",EDGE,"E94"),sQuery(id+"F0.wireOp",EDGE,"E95"),sQuery(id+"F0.wireOp",EDGE,"E96"),sQuery(id+"F0.wireOp",EDGE,"E97"),sQuery(id+"F0.wireOp",EDGE,"E98"),sQuery(id+"F0.wireOp",EDGE,"E99"),sQuery(id+"F0.wireOp",EDGE,"E100"),sQuery(id+"F0.wireOp",EDGE,"E101"),sQuery(id+"F0.wireOp",EDGE,"E102"),sQuery(id+"F0.wireOp",EDGE,"E103"),sQuery(id+"F0.wireOp",EDGE,"E104"),sQuery(id+"F0.wireOp",EDGE,"E105"),sQuery(id+"F0.wireOp",EDGE,"E106"),sQuery(id+"F0.wireOp",EDGE,"E107"),sQuery(id+"F0.wireOp",EDGE,"E108"),sQuery(id+"F0.wireOp",EDGE,"E109"),sQuery(id+"F0.wireOp",EDGE,"E110"),sQuery(id+"F0.wireOp",EDGE,"E111"),sQuery(id+"F0.wireOp",EDGE,"E112"),sQuery(id+"F0.wireOp",EDGE,"E113"),sQuery(id+"F0.wireOp",EDGE,"E114"),sQuery(id+"F0.wireOp",EDGE,"E115"),sQuery(id+"F0.wireOp",EDGE,"E116"),sQuery(id+"F0.wireOp",EDGE,"E117"),sQuery(id+"F0.wireOp",EDGE,"E118"),sQuery(id+"F0.wireOp",EDGE,"E119"),sQuery(id+"F0.wireOp",EDGE,"E120"),sQuery(id+"F0.wireOp",EDGE,"E121"),sQuery(id+"F0.wireOp",EDGE,"E122"),sQuery(id+"F0.wireOp",EDGE,"E123"),sQuery(id+"F0.wireOp",EDGE,"E124"),sQuery(id+"F0.wireOp",EDGE,"E125"),sQuery(id+"F0.wireOp",EDGE,"E126"),sQuery(id+"F0.wireOp",EDGE,"E127"),sQuery(id+"F0.wireOp",EDGE,"E128"),sQuery(id+"F0.wireOp",EDGE,"E129"),sQuery(id+"F0.wireOp",EDGE,"E130"),sQuery(id+"F0.wireOp",EDGE,"E131"),sQuery(id+"F0.wireOp",EDGE,"E132"),sQuery(id+"F0.wireOp",EDGE,"E133"),sQuery(id+"F0.wireOp",EDGE,"E134"),sQuery(id+"F0.wireOp",EDGE,"E135"),sQuery(id+"F0.wireOp",EDGE,"E136"),sQuery(id+"F0.wireOp",EDGE,"E137"),sQuery(id+"F0.wireOp",EDGE,"E138"),sQuery(id+"F0.wireOp",EDGE,"E139"),sQuery(id+"F0.wireOp",EDGE,"E140"),sQuery(id+"F0.wireOp",EDGE,"E141"),sQuery(id+"F0.wireOp",EDGE,"E142"),sQuery(id+"F0.wireOp",EDGE,"E143"),sQuery(id+"F0.wireOp",EDGE,"E144"),sQuery(id+"F0.wireOp",EDGE,"E145"),sQuery(id+"F0.wireOp",EDGE,"E146"),sQuery(id+"F0.wireOp",EDGE,"E147"),sQuery(id+"F0.wireOp",EDGE,"E148"),sQuery(id+"F0.wireOp",EDGE,"E149"),sQuery(id+"F0.wireOp",EDGE,"E150"),sQuery(id+"F0.wireOp",EDGE,"E151"),sQuery(id+"F0.wireOp",EDGE,"E152"),sQuery(id+"F0.wireOp",EDGE,"E153"),sQuery(id+"F0.wireOp",EDGE,"E154"),sQuery(id+"F0.wireOp",EDGE,"E155"),sQuery(id+"F0.wireOp",EDGE,"E156"),sQuery(id+"F0.wireOp",EDGE,"E157"),sQuery(id+"F0.wireOp",EDGE,"E158"),sQuery(id+"F0.wireOp",EDGE,"E159"),sQuery(id+"F0.wireOp",EDGE,"E160"),sQuery(id+"F0.wireOp",EDGE,"E161"),sQuery(id+"F0.wireOp",EDGE,"E162"),sQuery(id+"F0.wireOp",EDGE,"E163"),sQuery(id+"F0.wireOp",EDGE,"E164"),sQuery(id+"F0.wireOp",EDGE,"E165"),sQuery(id+"F0.wireOp",EDGE,"E166"),sQuery(id+"F0.wireOp",EDGE,"E167"),sQuery(id+"F0.wireOp",EDGE,"E168"),sQuery(id+"F0.wireOp",EDGE,"E169"),sQuery(id+"F0.wireOp",EDGE,"E170"),sQuery(id+"F0.wireOp",EDGE,"E171"),sQuery(id+"F0.wireOp",EDGE,"E172"),sQuery(id+"F0.wireOp",EDGE,"E173"),sQuery(id+"F0.wireOp",EDGE,"E174"),sQuery(id+"F0.wireOp",EDGE,"E175"),sQuery(id+"F0.wireOp",EDGE,"E176"),sQuery(id+"F0.wireOp",EDGE,"E177"),sQuery(id+"F0.wireOp",EDGE,"E178"),sQuery(id+"F0.wireOp",EDGE,"E179"),sQuery(id+"F0.wireOp",EDGE,"E180"),sQuery(id+"F0.wireOp",EDGE,"E181"),sQuery(id+"F0.wireOp",EDGE,"E182"),sQuery(id+"F0.wireOp",EDGE,"E183"),sQuery(id+"F0.wireOp",EDGE,"E184"),sQuery(id+"F0.wireOp",EDGE,"E185"),sQuery(id+"F0.wireOp",EDGE,"E186"),sQuery(id+"F0.wireOp",EDGE,"E187"),sQuery(id+"F0.wireOp",EDGE,"E188"),sQuery(id+"F0.wireOp",EDGE,"E189"),sQuery(id+"F0.wireOp",EDGE,"E190"),sQuery(id+"F0.wireOp",EDGE,"E191"),sQuery(id+"F0.wireOp",EDGE,"E192"),sQuery(id+"F0.wireOp",EDGE,"E193"),sQuery(id+"F0.wireOp",EDGE,"E194"),sQuery(id+"F0.wireOp",EDGE,"E195"),sQuery(id+"F0.wireOp",EDGE,"E196"),sQuery(id+"F0.wireOp",EDGE,"E197"),sQuery(id+"F0.wireOp",EDGE,"E198"),sQuery(id+"F0.wireOp",EDGE,"E199"),sQuery(id+"F0.wireOp",EDGE,"E200"),sQuery(id+"F0.wireOp",EDGE,"E201"),sQuery(id+"F0.wireOp",EDGE,"E202"),sQuery(id+"F0.wireOp",EDGE,"E203"),sQuery(id+"F0.wireOp",EDGE,"E204"),sQuery(id+"F0.wireOp",EDGE,"E205"),sQuery(id+"F0.wireOp",EDGE,"E206"),sQuery(id+"F0.wireOp",EDGE,"E207"),sQuery(id+"F0.wireOp",EDGE,"E208"),sQuery(id+"F0.wireOp",EDGE,"E209"),sQuery(id+"F0.wireOp",EDGE,"E210"),sQuery(id+"F0.wireOp",EDGE,"E211"),sQuery(id+"F0.wireOp",EDGE,"E212"),sQuery(id+"F0.wireOp",EDGE,"E213"),sQuery(id+"F0.wireOp",EDGE,"E214"),sQuery(id+"F0.wireOp",EDGE,"E215"),sQuery(id+"F0.wireOp",EDGE,"E216"),sQuery(id+"F0.wireOp",EDGE,"E217"),sQuery(id+"F0.wireOp",EDGE,"E218"),sQuery(id+"F0.wireOp",EDGE,"E219"),sQuery(id+"F0.wireOp",EDGE,"E220"),sQuery(id+"F0.wireOp",EDGE,"E221"),sQuery(id+"F0.wireOp",EDGE,"E222"),sQuery(id+"F0.wireOp",EDGE,"E223"),sQuery(id+"F0.wireOp",EDGE,"E224"),sQuery(id+"F0.wireOp",EDGE,"E225"),sQuery(id+"F0.wireOp",EDGE,"E226"),sQuery(id+"F0.wireOp",EDGE,"E227"),sQuery(id+"F0.wireOp",EDGE,"E228"),sQuery(id+"F0.wireOp",EDGE,"E229"),sQuery(id+"F0.wireOp",EDGE,"E230"),sQuery(id+"F0.wireOp",EDGE,"E231"),sQuery(id+"F0.wireOp",EDGE,"E232"),sQuery(id+"F0.wireOp",EDGE,"E233"),sQuery(id+"F0.wireOp",EDGE,"E234"),sQuery(id+"F0.wireOp",EDGE,"E235"),sQuery(id+"F0.wireOp",EDGE,"E236"),sQuery(id+"F0.wireOp",EDGE,"E237"),sQuery(id+"F0.wireOp",EDGE,"E238"),sQuery(id+"F0.wireOp",EDGE,"E239"),sQuery(id+"F0.wireOp",EDGE,"E240"),sQuery(id+"F0.wireOp",EDGE,"E241"),sQuery(id+"F0.wireOp",EDGE,"E242"),sQuery(id+"F0.wireOp",EDGE,"E243"),sQuery(id+"F0.wireOp",EDGE,"E244"),sQuery(id+"F0.wireOp",EDGE,"E245"),sQuery(id+"F0.wireOp",EDGE,"E246"),sQuery(id+"F0.wireOp",EDGE,"E247"),sQuery(id+"F0.wireOp",EDGE,"E248"),sQuery(id+"F0.wireOp",EDGE,"E249"),sQuery(id+"F0.wireOp",EDGE,"E250"),sQuery(id+"F0.wireOp",EDGE,"E251"),sQuery(id+"F0.wireOp",EDGE,"E252"),sQuery(id+"F0.wireOp",EDGE,"E253"),sQuery(id+"F0.wireOp",EDGE,"E254"),sQuery(id+"F0.wireOp",EDGE,"E255"),sQuery(id+"F0.wireOp",EDGE,"E256"),sQuery(id+"F0.wireOp",EDGE,"E257"),sQuery(id+"F0.wireOp",EDGE,"E258"),sQuery(id+"F0.wireOp",EDGE,"E259"),sQuery(id+"F0.wireOp",EDGE,"E260"),sQuery(id+"F0.wireOp",EDGE,"E261"),sQuery(id+"F0.wireOp",EDGE,"E262"),sQuery(id+"F0.wireOp",EDGE,"E263"),sQuery(id+"F0.wireOp",EDGE,"E264"),sQuery(id+"F0.wireOp",EDGE,"E265"),sQuery(id+"F0.wireOp",EDGE,"E266"),sQuery(id+"F0.wireOp",EDGE,"E267"),sQuery(id+"F0.wireOp",EDGE,"E268"),sQuery(id+"F0.wireOp",EDGE,"E269"),sQuery(id+"F0.wireOp",EDGE,"E270"),sQuery(id+"F0.wireOp",EDGE,"E271"),sQuery(id+"F0.wireOp",EDGE,"E272"),sQuery(id+"F0.wireOp",EDGE,"E273"),sQuery(id+"F0.wireOp",EDGE,"E274"),sQuery(id+"F0.wireOp",EDGE,"E275"),sQuery(id+"F0.wireOp",EDGE,"E276"),sQuery(id+"F0.wireOp",EDGE,"E277"),sQuery(id+"F0.wireOp",EDGE,"E278"),sQuery(id+"F0.wireOp",EDGE,"E279"),sQuery(id+"F0.wireOp",EDGE,"E280"),sQuery(id+"F0.wireOp",EDGE,"E281"),sQuery(id+"F0.wireOp",EDGE,"E282"),sQuery(id+"F0.wireOp",EDGE,"E283"),sQuery(id+"F0.wireOp",EDGE,"E284"),sQuery(id+"F0.wireOp",EDGE,"E285"),sQuery(id+"F0.wireOp",EDGE,"E286"),sQuery(id+"F0.wireOp",EDGE,"E287"),sQuery(id+"F0.wireOp",EDGE,"E288"),sQuery(id+"F0.wireOp",EDGE,"E289"),sQuery(id+"F0.wireOp",EDGE,"E290"),sQuery(id+"F0.wireOp",EDGE,"E291"),sQuery(id+"F0.wireOp",EDGE,"E292"),sQuery(id+"F0.wireOp",EDGE,"E293"),sQuery(id+"F0.wireOp",EDGE,"E294"),sQuery(id+"F0.wireOp",EDGE,"E295"),sQuery(id+"F0.wireOp",EDGE,"E296"),sQuery(id+"F0.wireOp",EDGE,"E297"),sQuery(id+"F0.wireOp",EDGE,"E298"),sQuery(id+"F0.wireOp",EDGE,"E299"),sQuery(id+"F0.wireOp",EDGE,"E300"),sQuery(id+"F0.wireOp",EDGE,"E301"),sQuery(id+"F0.wireOp",EDGE,"E302"),sQuery(id+"F0.wireOp",EDGE,"E303"),sQuery(id+"F0.wireOp",EDGE,"E304"),sQuery(id+"F0.wireOp",EDGE,"E305"),sQuery(id+"F0.wireOp",EDGE,"E306"),sQuery(id+"F0.wireOp",EDGE,"E307"),sQuery(id+"F0.wireOp",EDGE,"E308"),sQuery(id+"F0.wireOp",EDGE,"E309"),sQuery(id+"F0.wireOp",EDGE,"E310"),sQuery(id+"F0.wireOp",EDGE,"E311"),sQuery(id+"F0.wireOp",EDGE,"E312"),sQuery(id+"F0.wireOp",EDGE,"E313"),sQuery(id+"F0.wireOp",EDGE,"E314"),sQuery(id+"F0.wireOp",EDGE,"E315"),sQuery(id+"F0.wireOp",EDGE,"E316"),sQuery(id+"F0.wireOp",EDGE,"E317"),sQuery(id+"F0.wireOp",EDGE,"E318"),sQuery(id+"F0.wireOp",EDGE,"E319"),sQuery(id+"F0.wireOp",EDGE,"E320"),sQuery(id+"F0.wireOp",EDGE,"E321"),sQuery(id+"F0.wireOp",EDGE,"E322"),sQuery(id+"F0.wireOp",EDGE,"E323"),sQuery(id+"F0.wireOp",EDGE,"E324"),sQuery(id+"F0.wireOp",EDGE,"E325"),sQuery(id+"F0.wireOp",EDGE,"E326"),sQuery(id+"F0.wireOp",EDGE,"E327"),sQuery(id+"F0.wireOp",EDGE,"E328"),sQuery(id+"F0.wireOp",EDGE,"E329"),sQuery(id+"F0.wireOp",EDGE,"E330"),sQuery(id+"F0.wireOp",EDGE,"E331"),sQuery(id+"F0.wireOp",EDGE,"E332"),sQuery(id+"F0.wireOp",EDGE,"E333"),sQuery(id+"F0.wireOp",EDGE,"E334"),sQuery(id+"F0.wireOp",EDGE,"E335"),sQuery(id+"F0.wireOp",EDGE,"E336"),sQuery(id+"F0.wireOp",EDGE,"E337"),sQuery(id+"F0.wireOp",EDGE,"E338"),sQuery(id+"F0.wireOp",EDGE,"E339"),sQuery(id+"F0.wireOp",EDGE,"E340"),sQuery(id+"F0.wireOp",EDGE,"E341"),sQuery(id+"F0.wireOp",EDGE,"E342"),sQuery(id+"F0.wireOp",EDGE,"E343"),sQuery(id+"F0.wireOp",EDGE,"E344"),sQuery(id+"F0.wireOp",EDGE,"E345"),sQuery(id+"F0.wireOp",EDGE,"E346"),sQuery(id+"F0.wireOp",EDGE,"E347"),sQuery(id+"F0.wireOp",EDGE,"E348"),sQuery(id+"F0.wireOp",EDGE,"E349"),sQuery(id+"F0.wireOp",EDGE,"E350"),sQuery(id+"F0.wireOp",EDGE,"E351"),sQuery(id+"F0.wireOp",EDGE,"E352"),sQuery(id+"F0.wireOp",EDGE,"E353"),sQuery(id+"F0.wireOp",EDGE,"E354"),sQuery(id+"F0.wireOp",EDGE,"E355"),sQuery(id+"F0.wireOp",EDGE,"E356"),sQuery(id+"F0.wireOp",EDGE,"E357"),sQuery(id+"F0.wireOp",EDGE,"E358"),sQuery(id+"F0.wireOp",EDGE,"E359"),sQuery(id+"F0.wireOp",EDGE,"E360"),sQuery(id+"F0.wireOp",EDGE,"E361"),sQuery(id+"F0.wireOp",EDGE,"E362"),sQuery(id+"F0.wireOp",EDGE,"E363"),sQuery(id+"F0.wireOp",EDGE,"E364"),sQuery(id+"F0.wireOp",EDGE,"E365"),sQuery(id+"F0.wireOp",EDGE,"E366"),sQuery(id+"F0.wireOp",EDGE,"E367"),sQuery(id+"F0.wireOp",EDGE,"E368"),sQuery(id+"F0.wireOp",EDGE,"E369"),sQuery(id+"F0.wireOp",EDGE,"E370"),sQuery(id+"F0.wireOp",EDGE,"E371"),sQuery(id+"F0.wireOp",EDGE,"E372"),sQuery(id+"F0.wireOp",EDGE,"E373"),sQuery(id+"F0.wireOp",EDGE,"E374"),sQuery(id+"F0.wireOp",EDGE,"E375"),sQuery(id+"F0.wireOp",EDGE,"E376"),sQuery(id+"F0.wireOp",EDGE,"E377"),sQuery(id+"F0.wireOp",EDGE,"E378"),sQuery(id+"F0.wireOp",EDGE,"E379"),sQuery(id+"F0.wireOp",EDGE,"E380"),sQuery(id+"F0.wireOp",EDGE,"E381"),sQuery(id+"F0.wireOp",EDGE,"E382"),sQuery(id+"F0.wireOp",EDGE,"E383"),sQuery(id+"F0.wireOp",EDGE,"E384"),sQuery(id+"F0.wireOp",EDGE,"E385"),sQuery(id+"F0.wireOp",EDGE,"E386"),sQuery(id+"F0.wireOp",EDGE,"E387"),sQuery(id+"F0.wireOp",EDGE,"E388"),sQuery(id+"F0.wireOp",EDGE,"E389"),sQuery(id+"F0.wireOp",EDGE,"E390"),sQuery(id+"F0.wireOp",EDGE,"E391"),sQuery(id+"F0.wireOp",EDGE,"E392"),sQuery(id+"F0.wireOp",EDGE,"E393"),sQuery(id+"F0.wireOp",EDGE,"E394"),sQuery(id+"F0.wireOp",EDGE,"E395"),sQuery(id+"F0.wireOp",EDGE,"E396"),sQuery(id+"F0.wireOp",EDGE,"E397"),sQuery(id+"F0.wireOp",EDGE,"E398"),sQuery(id+"F0.wireOp",EDGE,"E399"),sQuery(id+"F0.wireOp",EDGE,"E400"),sQuery(id+"F0.wireOp",EDGE,"E401"),sQuery(id+"F0.wireOp",EDGE,"E402"),sQuery(id+"F0.wireOp",EDGE,"E403"),sQuery(id+"F0.wireOp",EDGE,"E404"),sQuery(id+"F0.wireOp",EDGE,"E405"),sQuery(id+"F0.wireOp",EDGE,"E406"),sQuery(id+"F0.wireOp",EDGE,"E407"),sQuery(id+"F0.wireOp",EDGE,"E408"),sQuery(id+"F0.wireOp",EDGE,"E409"),sQuery(id+"F0.wireOp",EDGE,"E410"),sQuery(id+"F0.wireOp",EDGE,"E411"),sQuery(id+"F0.wireOp",EDGE,"E412"),sQuery(id+"F0.wireOp",EDGE,"E413"),sQuery(id+"F0.wireOp",EDGE,"E414"),sQuery(id+"F0.wireOp",EDGE,"E415"),sQuery(id+"F0.wireOp",EDGE,"E416"),sQuery(id+"F0.wireOp",EDGE,"E417"),sQuery(id+"F0.wireOp",EDGE,"E418"),sQuery(id+"F0.wireOp",EDGE,"E419"),sQuery(id+"F0.wireOp",EDGE,"E420"),sQuery(id+"F0.wireOp",EDGE,"E421"),sQuery(id+"F0.wireOp",EDGE,"E422"),sQuery(id+"F0.wireOp",EDGE,"E423"),sQuery(id+"F0.wireOp",EDGE,"E424"),sQuery(id+"F0.wireOp",EDGE,"E425"),sQuery(id+"F0.wireOp",EDGE,"E426"),sQuery(id+"F0.wireOp",EDGE,"E427"),sQuery(id+"F0.wireOp",EDGE,"E428"),sQuery(id+"F0.wireOp",EDGE,"E429"),sQuery(id+"F0.wireOp",EDGE,"E430"),sQuery(id+"F0.wireOp",EDGE,"E431"),sQuery(id+"F0.wireOp",EDGE,"E432"),sQuery(id+"F0.wireOp",EDGE,"E433"),sQuery(id+"F0.wireOp",EDGE,"E434"),sQuery(id+"F0.wireOp",EDGE,"E435"),sQuery(id+"F0.wireOp",EDGE,"E436"),sQuery(id+"F0.wireOp",EDGE,"E437"),sQuery(id+"F0.wireOp",EDGE,"E438"),sQuery(id+"F0.wireOp",EDGE,"E439"),sQuery(id+"F0.wireOp",EDGE,"E440"),sQuery(id+"F0.wireOp",EDGE,"E441"),sQuery(id+"F0.wireOp",EDGE,"E442"),sQuery(id+"F0.wireOp",EDGE,"E443"),sQuery(id+"F0.wireOp",EDGE,"E444"),sQuery(id+"F0.wireOp",EDGE,"E445"),sQuery(id+"F0.wireOp",EDGE,"E446"),sQuery(id+"F0.wireOp",EDGE,"E447"),sQuery(id+"F0.wireOp",EDGE,"E448"),sQuery(id+"F0.wireOp",EDGE,"E449"),sQuery(id+"F0.wireOp",EDGE,"E450"),sQuery(id+"F0.wireOp",EDGE,"E451"),sQuery(id+"F0.wireOp",EDGE,"E452"),sQuery(id+"F0.wireOp",EDGE,"E453"),sQuery(id+"F0.wireOp",EDGE,"E454"),sQuery(id+"F0.wireOp",EDGE,"E455"),sQuery(id+"F0.wireOp",EDGE,"E456"),sQuery(id+"F0.wireOp",EDGE,"E457"),sQuery(id+"F0.wireOp",EDGE,"E458"),sQuery(id+"F0.wireOp",EDGE,"E459"),sQuery(id+"F0.wireOp",EDGE,"E460"),sQuery(id+"F0.wireOp",EDGE,"E461"),sQuery(id+"F0.wireOp",EDGE,"E462"),sQuery(id+"F0.wireOp",EDGE,"E463"),sQuery(id+"F0.wireOp",EDGE,"E464"),sQuery(id+"F0.wireOp",EDGE,"E465"),sQuery(id+"F0.wireOp",EDGE,"E466"),sQuery(id+"F0.wireOp",EDGE,"E467"),sQuery(id+"F0.wireOp",EDGE,"E468"),sQuery(id+"F0.wireOp",EDGE,"E469"),sQuery(id+"F0.wireOp",EDGE,"E470"),sQuery(id+"F0.wireOp",EDGE,"E471"),sQuery(id+"F0.wireOp",EDGE,"E472"),sQuery(id+"F0.wireOp",EDGE,"E473"),sQuery(id+"F0.wireOp",EDGE,"E474"),sQuery(id+"F0.wireOp",EDGE,"E475"),sQuery(id+"F0.wireOp",EDGE,"E476"),sQuery(id+"F0.wireOp",EDGE,"E477"),sQuery(id+"F0.wireOp",EDGE,"E478"),sQuery(id+"F0.wireOp",EDGE,"E479"),sQuery(id+"F0.wireOp",EDGE,"E480"),sQuery(id+"F0.wireOp",EDGE,"E481"),sQuery(id+"F0.wireOp",EDGE,"E482"),sQuery(id+"F0.wireOp",EDGE,"E483"),sQuery(id+"F0.wireOp",EDGE,"E484"),sQuery(id+"F0.wireOp",EDGE,"E485"),sQuery(id+"F0.wireOp",EDGE,"E486"),sQuery(id+"F0.wireOp",EDGE,"E487"),sQuery(id+"F0.wireOp",EDGE,"E488"),sQuery(id+"F0.wireOp",EDGE,"E489"),sQuery(id+"F0.wireOp",EDGE,"E490"),sQuery(id+"F0.wireOp",EDGE,"E491"),sQuery(id+"F0.wireOp",EDGE,"E492"),sQuery(id+"F0.wireOp",EDGE,"E493"),sQuery(id+"F0.wireOp",EDGE,"E494"),sQuery(id+"F0.wireOp",EDGE,"E495"),sQuery(id+"F0.wireOp",EDGE,"E496"),sQuery(id+"F0.wireOp",EDGE,"E497"),sQuery(id+"F0.wireOp",EDGE,"E498"),sQuery(id+"F0.wireOp",EDGE,"E499"),sQuery(id+"F0.wireOp",EDGE,"E500"),sQuery(id+"F0.wireOp",EDGE,"E501"),sQuery(id+"F0.wireOp",EDGE,"E502"),sQuery(id+"F0.wireOp",EDGE,"E503"),sQuery(id+"F0.wireOp",EDGE,"E504"),sQuery(id+"F0.wireOp",EDGE,"E505"),sQuery(id+"F0.wireOp",EDGE,"E506"),sQuery(id+"F0.wireOp",EDGE,"E507"),sQuery(id+"F0.wireOp",EDGE,"E508"),sQuery(id+"F0.wireOp",EDGE,"E509"),sQuery(id+"F0.wireOp",EDGE,"E510"),sQuery(id+"F0.wireOp",EDGE,"E511"),sQuery(id+"F0.wireOp",EDGE,"E512"),sQuery(id+"F0.wireOp",EDGE,"E513"),sQuery(id+"F0.wireOp",EDGE,"E514"),sQuery(id+"F0.wireOp",EDGE,"E515"),sQuery(id+"F0.wireOp",EDGE,"E516"),sQuery(id+"F0.wireOp",EDGE,"E517"),sQuery(id+"F0.wireOp",EDGE,"E518"),sQuery(id+"F0.wireOp",EDGE,"E519"),sQuery(id+"F0.wireOp",EDGE,"E520"),sQuery(id+"F0.wireOp",EDGE,"E521"),sQuery(id+"F0.wireOp",EDGE,"E522"),sQuery(id+"F0.wireOp",EDGE,"E523"),sQuery(id+"F0.wireOp",EDGE,"E524"),sQuery(id+"F0.wireOp",EDGE,"E525"),sQuery(id+"F0.wireOp",EDGE,"E526"),sQuery(id+"F0.wireOp",EDGE,"E527"),sQuery(id+"F0.wireOp",EDGE,"E528"),sQuery(id+"F0.wireOp",EDGE,"E529"),sQuery(id+"F0.wireOp",EDGE,"E530"),sQuery(id+"F0.wireOp",EDGE,"E531"),sQuery(id+"F0.wireOp",EDGE,"E532"),sQuery(id+"F0.wireOp",EDGE,"E533"),sQuery(id+"F0.wireOp",EDGE,"E534"),sQuery(id+"F0.wireOp",EDGE,"E535"),sQuery(id+"F0.wireOp",EDGE,"E536"),sQuery(id+"F0.wireOp",EDGE,"E537"),sQuery(id+"F0.wireOp",EDGE,"E538"),sQuery(id+"F0.wireOp",EDGE,"E539"),sQuery(id+"F0.wireOp",EDGE,"E540"),sQuery(id+"F0.wireOp",EDGE,"E541"),sQuery(id+"F0.wireOp",EDGE,"E542"),sQuery(id+"F0.wireOp",EDGE,"E543"),sQuery(id+"F0.wireOp",EDGE,"E544"),sQuery(id+"F0.wireOp",EDGE,"E545"),sQuery(id+"F0.wireOp",EDGE,"E546"),sQuery(id+"F0.wireOp",EDGE,"E547"),sQuery(id+"F0.wireOp",EDGE,"E548"),sQuery(id+"F0.wireOp",EDGE,"E549"),sQuery(id+"F0.wireOp",EDGE,"E550"),sQuery(id+"F0.wireOp",EDGE,"E551"),sQuery(id+"F0.wireOp",EDGE,"E552"),sQuery(id+"F0.wireOp",EDGE,"E553"),sQuery(id+"F0.wireOp",EDGE,"E554"),sQuery(id+"F0.wireOp",EDGE,"E555"),sQuery(id+"F0.wireOp",EDGE,"E556"),sQuery(id+"F0.wireOp",EDGE,"E557"),sQuery(id+"F0.wireOp",EDGE,"E558"),sQuery(id+"F0.wireOp",EDGE,"E559"),sQuery(id+"F0.wireOp",EDGE,"E560"),sQuery(id+"F0.wireOp",EDGE,"E561"),sQuery(id+"F0.wireOp",EDGE,"E562"),sQuery(id+"F0.wireOp",EDGE,"E563"),sQuery(id+"F0.wireOp",EDGE,"E564"),sQuery(id+"F0.wireOp",EDGE,"E565"),sQuery(id+"F0.wireOp",EDGE,"E566"),sQuery(id+"F0.wireOp",EDGE,"E567"),sQuery(id+"F0.wireOp",EDGE,"E568"),sQuery(id+"F0.wireOp",EDGE,"E569"),sQuery(id+"F0.wireOp",EDGE,"E570"),sQuery(id+"F0.wireOp",EDGE,"E571"),sQuery(id+"F0.wireOp",EDGE,"E572"),sQuery(id+"F0.wireOp",EDGE,"E573"),sQuery(id+"F0.wireOp",EDGE,"E574"),sQuery(id+"F0.wireOp",EDGE,"E575"),sQuery(id+"F0.wireOp",EDGE,"E576"),sQuery(id+"F0.wireOp",EDGE,"E577"),sQuery(id+"F0.wireOp",EDGE,"E578"),sQuery(id+"F0.wireOp",EDGE,"E579"),sQuery(id+"F0.wireOp",EDGE,"E580"),sQuery(id+"F0.wireOp",EDGE,"E581"),sQuery(id+"F0.wireOp",EDGE,"E582"),sQuery(id+"F0.wireOp",EDGE,"E583"),sQuery(id+"F0.wireOp",EDGE,"E584"),sQuery(id+"F0.wireOp",EDGE,"E585"),sQuery(id+"F0.wireOp",EDGE,"E586"),sQuery(id+"F0.wireOp",EDGE,"E587"),sQuery(id+"F0.wireOp",EDGE,"E588"),sQuery(id+"F0.wireOp",EDGE,"E589"),sQuery(id+"F0.wireOp",EDGE,"E590"),sQuery(id+"F0.wireOp",EDGE,"E591"),sQuery(id+"F0.wireOp",EDGE,"E592"),sQuery(id+"F0.wireOp",EDGE,"E593"),sQuery(id+"F0.wireOp",EDGE,"E594"),sQuery(id+"F0.wireOp",EDGE,"E595"),sQuery(id+"F0.wireOp",EDGE,"E596"),sQuery(id+"F0.wireOp",EDGE,"E597"),sQuery(id+"F0.wireOp",EDGE,"E598"),sQuery(id+"F0.wireOp",EDGE,"E599"),sQuery(id+"F0.wireOp",EDGE,"E600"),sQuery(id+"F0.wireOp",EDGE,"E601"),sQuery(id+"F0.wireOp",EDGE,"E602"),sQuery(id+"F0.wireOp",EDGE,"E603"),sQuery(id+"F0.wireOp",EDGE,"E604"),sQuery(id+"F0.wireOp",EDGE,"E605"),sQuery(id+"F0.wireOp",EDGE,"E606"),sQuery(id+"F0.wireOp",EDGE,"E607"),sQuery(id+"F0.wireOp",EDGE,"E608"),sQuery(id+"F0.wireOp",EDGE,"E609"),sQuery(id+"F0.wireOp",EDGE,"E610"),sQuery(id+"F0.wireOp",EDGE,"E611"),sQuery(id+"F0.wireOp",EDGE,"E612"),sQuery(id+"F0.wireOp",EDGE,"E613"),sQuery(id+"F0.wireOp",EDGE,"E614"),sQuery(id+"F0.wireOp",EDGE,"E615"),sQuery(id+"F0.wireOp",EDGE,"E616"),sQuery(id+"F0.wireOp",EDGE,"E617"),sQuery(id+"F0.wireOp",EDGE,"E618"),sQuery(id+"F0.wireOp",EDGE,"E619"),sQuery(id+"F0.wireOp",EDGE,"E620"),sQuery(id+"F0.wireOp",EDGE,"E621"),sQuery(id+"F0.wireOp",EDGE,"E622"),sQuery(id+"F0.wireOp",EDGE,"E623"),sQuery(id+"F0.wireOp",EDGE,"E624"),sQuery(id+"F0.wireOp",EDGE,"E625"),sQuery(id+"F0.wireOp",EDGE,"E626"),sQuery(id+"F0.wireOp",EDGE,"E627"),sQuery(id+"F0.wireOp",EDGE,"E628"),sQuery(id+"F0.wireOp",EDGE,"E629"),sQuery(id+"F0.wireOp",EDGE,"E630"),sQuery(id+"F0.wireOp",EDGE,"E631"),sQuery(id+"F0.wireOp",EDGE,"E632"),sQuery(id+"F0.wireOp",EDGE,"E633"),sQuery(id+"F0.wireOp",EDGE,"E634"),sQuery(id+"F0.wireOp",EDGE,"E635"),sQuery(id+"F0.wireOp",EDGE,"E636"),sQuery(id+"F0.wireOp",EDGE,"E637"),sQuery(id+"F0.wireOp",EDGE,"E638"),sQuery(id+"F0.wireOp",EDGE,"E639"),sQuery(id+"F0.wireOp",EDGE,"E640"),sQuery(id+"F0.wireOp",EDGE,"E641"),sQuery(id+"F0.wireOp",EDGE,"E642"),sQuery(id+"F0.wireOp",EDGE,"E643"),sQuery(id+"F0.wireOp",EDGE,"E644"),sQuery(id+"F0.wireOp",EDGE,"E645"),sQuery(id+"F0.wireOp",EDGE,"E646"),sQuery(id+"F0.wireOp",EDGE,"E647"),sQuery(id+"F0.wireOp",EDGE,"E648"),sQuery(id+"F0.wireOp",EDGE,"E649"),sQuery(id+"F0.wireOp",EDGE,"E650"),sQuery(id+"F0.wireOp",EDGE,"E651"),sQuery(id+"F0.wireOp",EDGE,"E652"),sQuery(id+"F0.wireOp",EDGE,"E653"),sQuery(id+"F0.wireOp",EDGE,"E654"),sQuery(id+"F0.wireOp",EDGE,"E655"),sQuery(id+"F0.wireOp",EDGE,"E656"),sQuery(id+"F0.wireOp",EDGE,"E657"),sQuery(id+"F0.wireOp",EDGE,"E658"),sQuery(id+"F0.wireOp",EDGE,"E659"),sQuery(id+"F0.wireOp",EDGE,"E660"),sQuery(id+"F0.wireOp",EDGE,"E661"),sQuery(id+"F0.wireOp",EDGE,"E662"),sQuery(id+"F0.wireOp",EDGE,"E663"),sQuery(id+"F0.wireOp",EDGE,"E664"),sQuery(id+"F0.wireOp",EDGE,"E665"),sQuery(id+"F0.wireOp",EDGE,"E666"),sQuery(id+"F0.wireOp",EDGE,"E667"),sQuery(id+"F0.wireOp",EDGE,"E668"),sQuery(id+"F0.wireOp",EDGE,"E669"),sQuery(id+"F0.wireOp",EDGE,"E670"),sQuery(id+"F0.wireOp",EDGE,"E671"),sQuery(id+"F0.wireOp",EDGE,"E672"),sQuery(id+"F0.wireOp",EDGE,"E673"),sQuery(id+"F0.wireOp",EDGE,"E674"),sQuery(id+"F0.wireOp",EDGE,"E675"),sQuery(id+"F0.wireOp",EDGE,"E676"),sQuery(id+"F0.wireOp",EDGE,"E677"),sQuery(id+"F0.wireOp",EDGE,"E678"),sQuery(id+"F0.wireOp",EDGE,"E679"),sQuery(id+"F0.wireOp",EDGE,"E680"),sQuery(id+"F0.wireOp",EDGE,"E681"),sQuery(id+"F0.wireOp",EDGE,"E682"),sQuery(id+"F0.wireOp",EDGE,"E683"),sQuery(id+"F0.wireOp",EDGE,"E684"),sQuery(id+"F0.wireOp",EDGE,"E685"),sQuery(id+"F0.wireOp",EDGE,"E686"),sQuery(id+"F0.wireOp",EDGE,"E687"),sQuery(id+"F0.wireOp",EDGE,"E688"),sQuery(id+"F0.wireOp",EDGE,"E689"),sQuery(id+"F0.wireOp",EDGE,"E690"),sQuery(id+"F0.wireOp",EDGE,"E691"),sQuery(id+"F0.wireOp",EDGE,"E692"),sQuery(id+"F0.wireOp",EDGE,"E693"),sQuery(id+"F0.wireOp",EDGE,"E694"),sQuery(id+"F0.wireOp",EDGE,"E695"),sQuery(id+"F0.wireOp",EDGE,"E696"),sQuery(id+"F0.wireOp",EDGE,"E697"),sQuery(id+"F0.wireOp",EDGE,"E698"),sQuery(id+"F0.wireOp",EDGE,"E699"),sQuery(id+"F0.wireOp",EDGE,"E700"),sQuery(id+"F0.wireOp",EDGE,"E701"),sQuery(id+"F0.wireOp",EDGE,"E702"),sQuery(id+"F0.wireOp",EDGE,"E703"),sQuery(id+"F0.wireOp",EDGE,"E704"),sQuery(id+"F0.wireOp",EDGE,"E705"),sQuery(id+"F0.wireOp",EDGE,"E706"),sQuery(id+"F0.wireOp",EDGE,"E707"),sQuery(id+"F0.wireOp",EDGE,"E708"),sQuery(id+"F0.wireOp",EDGE,"E709"),sQuery(id+"F0.wireOp",EDGE,"E710"),sQuery(id+"F0.wireOp",EDGE,"E711"),sQuery(id+"F0.wireOp",EDGE,"E712"),sQuery(id+"F0.wireOp",EDGE,"E713"),sQuery(id+"F0.wireOp",EDGE,"E714"),sQuery(id+"F0.wireOp",EDGE,"E715"),sQuery(id+"F0.wireOp",EDGE,"E716"),sQuery(id+"F0.wireOp",EDGE,"E717"),sQuery(id+"F0.wireOp",EDGE,"E718"),sQuery(id+"F0.wireOp",EDGE,"E719"),sQuery(id+"F0.wireOp",EDGE,"E720"),sQuery(id+"F0.wireOp",EDGE,"E721"),sQuery(id+"F0.wireOp",EDGE,"E722"),sQuery(id+"F0.wireOp",EDGE,"E723"),sQuery(id+"F0.wireOp",EDGE,"E724"),sQuery(id+"F0.wireOp",EDGE,"E725"),sQuery(id+"F0.wireOp",EDGE,"E726"),sQuery(id+"F0.wireOp",EDGE,"E727"),sQuery(id+"F0.wireOp",EDGE,"E728"),sQuery(id+"F0.wireOp",EDGE,"E729"),sQuery(id+"F0.wireOp",EDGE,"E730"),sQuery(id+"F0.wireOp",EDGE,"E731"),sQuery(id+"F0.wireOp",EDGE,"E732"),sQuery(id+"F0.wireOp",EDGE,"E733"),sQuery(id+"F0.wireOp",EDGE,"E734"),sQuery(id+"F0.wireOp",EDGE,"E735"),sQuery(id+"F0.wireOp",EDGE,"E736"),sQuery(id+"F0.wireOp",EDGE,"E737"),sQuery(id+"F0.wireOp",EDGE,"E738"),sQuery(id+"F0.wireOp",EDGE,"E739"),sQuery(id+"F0.wireOp",EDGE,"E740"),sQuery(id+"F0.wireOp",EDGE,"E741"),sQuery(id+"F0.wireOp",EDGE,"E742"),sQuery(id+"F0.wireOp",EDGE,"E743"),sQuery(id+"F0.wireOp",EDGE,"E744"),sQuery(id+"F0.wireOp",EDGE,"E745"),sQuery(id+"F0.wireOp",EDGE,"E746"),sQuery(id+"F0.wireOp",EDGE,"E747"),sQuery(id+"F0.wireOp",EDGE,"E748"),sQuery(id+"F0.wireOp",EDGE,"E749"),sQuery(id+"F0.wireOp",EDGE,"E750"),sQuery(id+"F0.wireOp",EDGE,"E751"),sQuery(id+"F0.wireOp",EDGE,"E752"),sQuery(id+"F0.wireOp",EDGE,"E753"),sQuery(id+"F0.wireOp",EDGE,"E754"),sQuery(id+"F0.wireOp",EDGE,"E755"),sQuery(id+"F0.wireOp",EDGE,"E756"),sQuery(id+"F0.wireOp",EDGE,"E757"),sQuery(id+"F0.wireOp",EDGE,"E758"),sQuery(id+"F0.wireOp",EDGE,"E759"),sQuery(id+"F0.wireOp",EDGE,"E760"),sQuery(id+"F0.wireOp",EDGE,"E761"),sQuery(id+"F0.wireOp",EDGE,"E762"),sQuery(id+"F0.wireOp",EDGE,"E763"),sQuery(id+"F0.wireOp",EDGE,"E764"),sQuery(id+"F0.wireOp",EDGE,"E765"),sQuery(id+"F0.wireOp",EDGE,"E766"),sQuery(id+"F0.wireOp",EDGE,"E767"),sQuery(id+"F0.wireOp",EDGE,"E768"),sQuery(id+"F0.wireOp",EDGE,"E769"),sQuery(id+"F0.wireOp",EDGE,"E770"),sQuery(id+"F0.wireOp",EDGE,"E771"),sQuery(id+"F0.wireOp",EDGE,"E772"),sQuery(id+"F0.wireOp",EDGE,"E773"),sQuery(id+"F0.wireOp",EDGE,"E774"),sQuery(id+"F0.wireOp",EDGE,"E775"),sQuery(id+"F0.wireOp",EDGE,"E776"),sQuery(id+"F0.wireOp",EDGE,"E777"),sQuery(id+"F0.wireOp",EDGE,"E778"),sQuery(id+"F0.wireOp",EDGE,"E779"),sQuery(id+"F0.wireOp",EDGE,"E780"),sQuery(id+"F0.wireOp",EDGE,"E781"),sQuery(id+"F0.wireOp",EDGE,"E782"),sQuery(id+"F0.wireOp",EDGE,"E783"),sQuery(id+"F0.wireOp",EDGE,"E784"),sQuery(id+"F0.wireOp",EDGE,"E785"),sQuery(id+"F0.wireOp",EDGE,"E786"),sQuery(id+"F0.wireOp",EDGE,"E787"),sQuery(id+"F0.wireOp",EDGE,"E788"),sQuery(id+"F0.wireOp",EDGE,"E789"),sQuery(id+"F0.wireOp",EDGE,"E790"),sQuery(id+"F0.wireOp",EDGE,"E791"),sQuery(id+"F0.wireOp",EDGE,"E792"),sQuery(id+"F0.wireOp",EDGE,"E793"),sQuery(id+"F0.wireOp",EDGE,"E794"),sQuery(id+"F0.wireOp",EDGE,"E795"),sQuery(id+"F0.wireOp",EDGE,"E796"),sQuery(id+"F0.wireOp",EDGE,"E797"),sQuery(id+"F0.wireOp",EDGE,"E798"),sQuery(id+"F0.wireOp",EDGE,"E799"),sQuery(id+"F0.wireOp",EDGE,"E800"),sQuery(id+"F0.wireOp",EDGE,"E801"),sQuery(id+"F0.wireOp",EDGE,"E802"),sQuery(id+"F0.wireOp",EDGE,"E803"),sQuery(id+"F0.wireOp",EDGE,"E804"),sQuery(id+"F0.wireOp",EDGE,"E805"),sQuery(id+"F0.wireOp",EDGE,"E806"),sQuery(id+"F0.wireOp",EDGE,"E807"),sQuery(id+"F0.wireOp",EDGE,"E808"),sQuery(id+"F0.wireOp",EDGE,"E809"),sQuery(id+"F0.wireOp",EDGE,"E810"),sQuery(id+"F0.wireOp",EDGE,"E811"),sQuery(id+"F0.wireOp",EDGE,"E812"),sQuery(id+"F0.wireOp",EDGE,"E813"),sQuery(id+"F0.wireOp",EDGE,"E814"),sQuery(id+"F0.wireOp",EDGE,"E815"),sQuery(id+"F0.wireOp",EDGE,"E816"),sQuery(id+"F0.wireOp",EDGE,"E817"),sQuery(id+"F0.wireOp",EDGE,"E818"),sQuery(id+"F0.wireOp",EDGE,"E819"),sQuery(id+"F0.wireOp",EDGE,"E820"),sQuery(id+"F0.wireOp",EDGE,"E821"),sQuery(id+"F0.wireOp",EDGE,"E822"),sQuery(id+"F0.wireOp",EDGE,"E823"),sQuery(id+"F0.wireOp",EDGE,"E824"),sQuery(id+"F0.wireOp",EDGE,"E825"),sQuery(id+"F0.wireOp",EDGE,"E826"),sQuery(id+"F0.wireOp",EDGE,"E827"),sQuery(id+"F0.wireOp",EDGE,"E828"),sQuery(id+"F0.wireOp",EDGE,"E829"),sQuery(id+"F0.wireOp",EDGE,"E830"),sQuery(id+"F0.wireOp",EDGE,"E831"),sQuery(id+"F0.wireOp",EDGE,"E832"),sQuery(id+"F0.wireOp",EDGE,"E833"),sQuery(id+"F0.wireOp",EDGE,"E834"),sQuery(id+"F0.wireOp",EDGE,"E835"),sQuery(id+"F0.wireOp",EDGE,"E836"),sQuery(id+"F0.wireOp",EDGE,"E837"),sQuery(id+"F0.wireOp",EDGE,"E838"),sQuery(id+"F0.wireOp",EDGE,"E839"),sQuery(id+"F0.wireOp",EDGE,"E840"),sQuery(id+"F0.wireOp",EDGE,"E841"),sQuery(id+"F0.wireOp",EDGE,"E842"),sQuery(id+"F0.wireOp",EDGE,"E843"),sQuery(id+"F0.wireOp",EDGE,"E844"),sQuery(id+"F0.wireOp",EDGE,"E845"),sQuery(id+"F0.wireOp",EDGE,"E846"),sQuery(id+"F0.wireOp",EDGE,"E847"),sQuery(id+"F0.wireOp",EDGE,"E848"),sQuery(id+"F0.wireOp",EDGE,"E849"),sQuery(id+"F0.wireOp",EDGE,"E850"),sQuery(id+"F0.wireOp",EDGE,"E851"),sQuery(id+"F0.wireOp",EDGE,"E852"),sQuery(id+"F0.wireOp",EDGE,"E853"),sQuery(id+"F0.wireOp",EDGE,"E854"),sQuery(id+"F0.wireOp",EDGE,"E855"),sQuery(id+"F0.wireOp",EDGE,"E856"),sQuery(id+"F0.wireOp",EDGE,"E857"),sQuery(id+"F0.wireOp",EDGE,"E858"),sQuery(id+"F0.wireOp",EDGE,"E859"),sQuery(id+"F0.wireOp",EDGE,"E860"),sQuery(id+"F0.wireOp",EDGE,"E861"),sQuery(id+"F0.wireOp",EDGE,"E862"),sQuery(id+"F0.wireOp",EDGE,"E863"),sQuery(id+"F0.wireOp",EDGE,"E864"),sQuery(id+"F0.wireOp",EDGE,"E865"),sQuery(id+"F0.wireOp",EDGE,"E866"),sQuery(id+"F0.wireOp",EDGE,"E867"),sQuery(id+"F0.wireOp",EDGE,"E868"),sQuery(id+"F0.wireOp",EDGE,"E869"),sQuery(id+"F0.wireOp",EDGE,"E870"),sQuery(id+"F0.wireOp",EDGE,"E871"),sQuery(id+"F0.wireOp",EDGE,"E872"),sQuery(id+"F0.wireOp",EDGE,"E873"),sQuery(id+"F0.wireOp",EDGE,"E874"),sQuery(id+"F0.wireOp",EDGE,"E875"),sQuery(id+"F0.wireOp",EDGE,"E876"),sQuery(id+"F0.wireOp",EDGE,"E877"),sQuery(id+"F0.wireOp",EDGE,"E878"),sQuery(id+"F0.wireOp",EDGE,"E879"),sQuery(id+"F0.wireOp",EDGE,"E880"),sQuery(id+"F0.wireOp",EDGE,"E881"),sQuery(id+"F0.wireOp",EDGE,"E882"),sQuery(id+"F0.wireOp",EDGE,"E883"),sQuery(id+"F0.wireOp",EDGE,"E884"),sQuery(id+"F0.wireOp",EDGE,"E885"),sQuery(id+"F0.wireOp",EDGE,"E886"),sQuery(id+"F0.wireOp",EDGE,"E887"),sQuery(id+"F0.wireOp",EDGE,"E888"),sQuery(id+"F0.wireOp",EDGE,"E889"),sQuery(id+"F0.wireOp",EDGE,"E890"),sQuery(id+"F0.wireOp",EDGE,"E891"),sQuery(id+"F0.wireOp",EDGE,"E892"),sQuery(id+"F0.wireOp",EDGE,"E893"),sQuery(id+"F0.wireOp",EDGE,"E894"),sQuery(id+"F0.wireOp",EDGE,"E895"),sQuery(id+"F0.wireOp",EDGE,"E896"),sQuery(id+"F0.wireOp",EDGE,"E897"),sQuery(id+"F0.wireOp",EDGE,"E898"),sQuery(id+"F0.wireOp",EDGE,"E899"),sQuery(id+"F0.wireOp",EDGE,"E900"),sQuery(id+"F0.wireOp",EDGE,"E901"),sQuery(id+"F0.wireOp",EDGE,"E902"),sQuery(id+"F0.wireOp",EDGE,"E903"),sQuery(id+"F0.wireOp",EDGE,"E904"),sQuery(id+"F0.wireOp",EDGE,"E905"),sQuery(id+"F0.wireOp",EDGE,"E906"),sQuery(id+"F0.wireOp",EDGE,"E907"),sQuery(id+"F0.wireOp",EDGE,"E908"),sQuery(id+"F0.wireOp",EDGE,"E909"),sQuery(id+"F0.wireOp",EDGE,"E910"),sQuery(id+"F0.wireOp",EDGE,"E911"),sQuery(id+"F0.wireOp",EDGE,"E912"),sQuery(id+"F0.wireOp",EDGE,"E913"),sQuery(id+"F0.wireOp",EDGE,"E914"),sQuery(id+"F0.wireOp",EDGE,"E915"),sQuery(id+"F0.wireOp",EDGE,"E916"),sQuery(id+"F0.wireOp",EDGE,"E917"),sQuery(id+"F0.wireOp",EDGE,"E918"),sQuery(id+"F0.wireOp",EDGE,"E919"),sQuery(id+"F0.wireOp",EDGE,"E920"),sQuery(id+"F0.wireOp",EDGE,"E921"),sQuery(id+"F0.wireOp",EDGE,"E922"),sQuery(id+"F0.wireOp",EDGE,"E923"),sQuery(id+"F0.wireOp",EDGE,"E924"),sQuery(id+"F0.wireOp",EDGE,"E925"),sQuery(id+"F0.wireOp",EDGE,"E926"),sQuery(id+"F0.wireOp",EDGE,"E927"),sQuery(id+"F0.wireOp",EDGE,"E928"),sQuery(id+"F0.wireOp",EDGE,"E929"),sQuery(id+"F0.wireOp",EDGE,"E930"),sQuery(id+"F0.wireOp",EDGE,"E931"),sQuery(id+"F0.wireOp",EDGE,"E932"),sQuery(id+"F0.wireOp",EDGE,"E933"),sQuery(id+"F0.wireOp",EDGE,"E934"),sQuery(id+"F0.wireOp",EDGE,"E935"),sQuery(id+"F0.wireOp",EDGE,"E936"),sQuery(id+"F0.wireOp",EDGE,"E937"),sQuery(id+"F0.wireOp",EDGE,"E938"),sQuery(id+"F0.wireOp",EDGE,"E939"),sQuery(id+"F0.wireOp",EDGE,"E940"),sQuery(id+"F0.wireOp",EDGE,"E941"),sQuery(id+"F0.wireOp",EDGE,"E942"),sQuery(id+"F0.wireOp",EDGE,"E943"),sQuery(id+"F0.wireOp",EDGE,"E944"),sQuery(id+"F0.wireOp",EDGE,"E945"),sQuery(id+"F0.wireOp",EDGE,"E946"),sQuery(id+"F0.wireOp",EDGE,"E947"),sQuery(id+"F0.wireOp",EDGE,"E948"),sQuery(id+"F0.wireOp",EDGE,"E949"),sQuery(id+"F0.wireOp",EDGE,"E950"),sQuery(id+"F0.wireOp",EDGE,"E951"),sQuery(id+"F0.wireOp",EDGE,"E952"),sQuery(id+"F0.wireOp",EDGE,"E953"),sQuery(id+"F0.wireOp",EDGE,"E954"),sQuery(id+"F0.wireOp",EDGE,"E955"),sQuery(id+"F0.wireOp",EDGE,"E956"),sQuery(id+"F0.wireOp",EDGE,"E957"),sQuery(id+"F0.wireOp",EDGE,"E958"),sQuery(id+"F0.wireOp",EDGE,"E959"),sQuery(id+"F0.wireOp",EDGE,"E960"),sQuery(id+"F0.wireOp",EDGE,"E961"),sQuery(id+"F0.wireOp",EDGE,"E962"),sQuery(id+"F0.wireOp",EDGE,"E963"),sQuery(id+"F0.wireOp",EDGE,"E964"),sQuery(id+"F0.wireOp",EDGE,"E965"),sQuery(id+"F0.wireOp",EDGE,"E966"),sQuery(id+"F0.wireOp",EDGE,"E967"),sQuery(id+"F0.wireOp",EDGE,"E968"),sQuery(id+"F0.wireOp",EDGE,"E969"),sQuery(id+"F0.wireOp",EDGE,"E970"),sQuery(id+"F0.wireOp",EDGE,"E971"),sQuery(id+"F0.wireOp",EDGE,"E972"),sQuery(id+"F0.wireOp",EDGE,"E973"),sQuery(id+"F0.wireOp",EDGE,"E974"),sQuery(id+"F0.wireOp",EDGE,"E975"),sQuery(id+"F0.wireOp",EDGE,"E976"),sQuery(id+"F0.wireOp",EDGE,"E977"),sQuery(id+"F0.wireOp",EDGE,"E978"),sQuery(id+"F0.wireOp",EDGE,"E979"),sQuery(id+"F0.wireOp",EDGE,"E980"),sQuery(id+"F0.wireOp",EDGE,"E981"),sQuery(id+"F0.wireOp",EDGE,"E982"),sQuery(id+"F0.wireOp",EDGE,"E983"),sQuery(id+"F0.wireOp",EDGE,"E984"),sQuery(id+"F0.wireOp",EDGE,"E985"),sQuery(id+"F0.wireOp",EDGE,"E986"),sQuery(id+"F0.wireOp",EDGE,"E987"),sQuery(id+"F0.wireOp",EDGE,"E988"),sQuery(id+"F0.wireOp",EDGE,"E989"),sQuery(id+"F0.wireOp",EDGE,"E990"),sQuery(id+"F0.wireOp",EDGE,"E991"),sQuery(id+"F0.wireOp",EDGE,"E992"),sQuery(id+"F0.wireOp",EDGE,"E993"),sQuery(id+"F0.wireOp",EDGE,"E994"),sQuery(id+"F0.wireOp",EDGE,"E995"),sQuery(id+"F0.wireOp",EDGE,"E996"),sQuery(id+"F0.wireOp",EDGE,"E997"),sQuery(id+"F0.wireOp",EDGE,"E998"),sQuery(id+"F0.wireOp",EDGE,"E999"),sQuery(id+"F0.wireOp",EDGE,"E1000"),sQuery(id+"F0.wireOp",EDGE,"E1001"),sQuery(id+"F0.wireOp",EDGE,"E1002"),sQuery(id+"F0.wireOp",EDGE,"E1003"),sQuery(id+"F0.wireOp",EDGE,"E1004"),sQuery(id+"F0.wireOp",EDGE,"E1005"),sQuery(id+"F0.wireOp",EDGE,"E1006"),sQuery(id+"F0.wireOp",EDGE,"E1007"),sQuery(id+"F0.wireOp",EDGE,"E1008"),sQuery(id+"F0.wireOp",EDGE,"E1009"),sQuery(id+"F0.wireOp",EDGE,"E1010"),sQuery(id+"F0.wireOp",EDGE,"E1011"),sQuery(id+"F0.wireOp",EDGE,"E1012"),sQuery(id+"F0.wireOp",EDGE,"E1013"),sQuery(id+"F0.wireOp",EDGE,"E1014"),sQuery(id+"F0.wireOp",EDGE,"E1015"),sQuery(id+"F0.wireOp",EDGE,"E1016"),sQuery(id+"F0.wireOp",EDGE,"E1017"),sQuery(id+"F0.wireOp",EDGE,"E1018"),sQuery(id+"F0.wireOp",EDGE,"E1019"),sQuery(id+"F0.wireOp",EDGE,"E1020"),sQuery(id+"F0.wireOp",EDGE,"E1021"),sQuery(id+"F0.wireOp",EDGE,"E1022"),sQuery(id+"F0.wireOp",EDGE,"E1023"),sQuery(id+"F0.wireOp",EDGE,"E1024"),sQuery(id+"F0.wireOp",EDGE,"E1025"),sQuery(id+"F0.wireOp",EDGE,"E1026"),sQuery(id+"F0.wireOp",EDGE,"E1027"),sQuery(id+"F0.wireOp",EDGE,"E1028"),sQuery(id+"F0.wireOp",EDGE,"E1029"),sQuery(id+"F0.wireOp",EDGE,"E1030"),sQuery(id+"F0.wireOp",EDGE,"E1031"),sQuery(id+"F0.wireOp",EDGE,"E1032"),sQuery(id+"F0.wireOp",EDGE,"E1033"),sQuery(id+"F0.wireOp",EDGE,"E1034"),sQuery(id+"F0.wireOp",EDGE,"E1035"),sQuery(id+"F0.wireOp",EDGE,"E1036"),sQuery(id+"F0.wireOp",EDGE,"E1037"),sQuery(id+"F0.wireOp",EDGE,"E1038"),sQuery(id+"F0.wireOp",EDGE,"E1039"),sQuery(id+"F0.wireOp",EDGE,"E1040"),sQuery(id+"F0.wireOp",EDGE,"E1041"),sQuery(id+"F0.wireOp",EDGE,"E1042"),sQuery(id+"F0.wireOp",EDGE,"E1043"),sQuery(id+"F0.wireOp",EDGE,"E1044"),sQuery(id+"F0.wireOp",EDGE,"E1045"),sQuery(id+"F0.wireOp",EDGE,"E1046"),sQuery(id+"F0.wireOp",EDGE,"E1047"),sQuery(id+"F0.wireOp",EDGE,"E1048"),sQuery(id+"F0.wireOp",EDGE,"E1049"),sQuery(id+"F0.wireOp",EDGE,"E1050"),sQuery(id+"F0.wireOp",EDGE,"E1051"),sQuery(id+"F0.wireOp",EDGE,"E1052"),sQuery(id+"F0.wireOp",EDGE,"E1053"),sQuery(id+"F0.wireOp",EDGE,"E1054"),sQuery(id+"F0.wireOp",EDGE,"E1055"),sQuery(id+"F0.wireOp",EDGE,"E1056"),sQuery(id+"F0.wireOp",EDGE,"E1057"),sQuery(id+"F0.wireOp",EDGE,"E1058"),sQuery(id+"F0.wireOp",EDGE,"E1059"),sQuery(id+"F0.wireOp",EDGE,"E1060"),sQuery(id+"F0.wireOp",EDGE,"E1061"),sQuery(id+"F0.wireOp",EDGE,"E1062"),sQuery(id+"F0.wireOp",EDGE,"E1063"),sQuery(id+"F0.wireOp",EDGE,"E1064"),sQuery(id+"F0.wireOp",EDGE,"E1065"),sQuery(id+"F0.wireOp",EDGE,"E1066"),sQuery(id+"F0.wireOp",EDGE,"E1067"),sQuery(id+"F0.wireOp",EDGE,"E1068"),sQuery(id+"F0.wireOp",EDGE,"E1069"),sQuery(id+"F0.wireOp",EDGE,"E1070"),sQuery(id+"F0.wireOp",EDGE,"E1071"),sQuery(id+"F0.wireOp",EDGE,"E1072"),sQuery(id+"F0.wireOp",EDGE,"E1073"),sQuery(id+"F0.wireOp",EDGE,"E1074"),sQuery(id+"F0.wireOp",EDGE,"E1075"),sQuery(id+"F0.wireOp",EDGE,"E1076"),sQuery(id+"F0.wireOp",EDGE,"E1077"),sQuery(id+"F0.wireOp",EDGE,"E1078"),sQuery(id+"F0.wireOp",EDGE,"E1079"),sQuery(id+"F0.wireOp",EDGE,"E1080"),sQuery(id+"F0.wireOp",EDGE,"E1081"),sQuery(id+"F0.wireOp",EDGE,"E1082"),sQuery(id+"F0.wireOp",EDGE,"E1083"),sQuery(id+"F0.wireOp",EDGE,"E1084"),sQuery(id+"F0.wireOp",EDGE,"E1085"),sQuery(id+"F0.wireOp",EDGE,"E1086"),sQuery(id+"F0.wireOp",EDGE,"E1087"),sQuery(id+"F0.wireOp",EDGE,"E1088"),sQuery(id+"F0.wireOp",EDGE,"E1089"),sQuery(id+"F0.wireOp",EDGE,"E1090"),sQuery(id+"F0.wireOp",EDGE,"E1091"),sQuery(id+"F0.wireOp",EDGE,"E1092"),sQuery(id+"F0.wireOp",EDGE,"E1093"),sQuery(id+"F0.wireOp",EDGE,"E1094"),sQuery(id+"F0.wireOp",EDGE,"E1095"),sQuery(id+"F0.wireOp",EDGE,"E1096"),sQuery(id+"F0.wireOp",EDGE,"E1097"),sQuery(id+"F0.wireOp",EDGE,"E1098"),sQuery(id+"F0.wireOp",EDGE,"E1099"),sQuery(id+"F0.wireOp",EDGE,"E1100"),sQuery(id+"F0.wireOp",EDGE,"E1101"),sQuery(id+"F0.wireOp",EDGE,"E1102"),sQuery(id+"F0.wireOp",EDGE,"E1103"),sQuery(id+"F0.wireOp",EDGE,"E1104"),sQuery(id+"F0.wireOp",EDGE,"E1105"),sQuery(id+"F0.wireOp",EDGE,"E1106"),sQuery(id+"F0.wireOp",EDGE,"E1107"),sQuery(id+"F0.wireOp",EDGE,"E1108"),sQuery(id+"F0.wireOp",EDGE,"E1109"),sQuery(id+"F0.wireOp",EDGE,"E1110"),sQuery(id+"F0.wireOp",EDGE,"E1111"),sQuery(id+"F0.wireOp",EDGE,"E1112"),sQuery(id+"F0.wireOp",EDGE,"E1113"),sQuery(id+"F0.wireOp",EDGE,"E1114"),sQuery(id+"F0.wireOp",EDGE,"E1115"),sQuery(id+"F0.wireOp",EDGE,"E1116"),sQuery(id+"F0.wireOp",EDGE,"E1117"),sQuery(id+"F0.wireOp",EDGE,"E1118"),sQuery(id+"F0.wireOp",EDGE,"E1119"),sQuery(id+"F0.wireOp",EDGE,"E1120"),sQuery(id+"F0.wireOp",EDGE,"E1121"),sQuery(id+"F0.wireOp",EDGE,"E1122"),sQuery(id+"F0.wireOp",EDGE,"E1123"),sQuery(id+"F0.wireOp",EDGE,"E1124"),sQuery(id+"F0.wireOp",EDGE,"E1125"),sQuery(id+"F0.wireOp",EDGE,"E1126"),sQuery(id+"F0.wireOp",EDGE,"E1127"),sQuery(id+"F0.wireOp",EDGE,"E1128"),sQuery(id+"F0.wireOp",EDGE,"E1129"),sQuery(id+"F0.wireOp",EDGE,"E1130"),sQuery(id+"F0.wireOp",EDGE,"E1131"),sQuery(id+"F0.wireOp",EDGE,"E1132"),sQuery(id+"F0.wireOp",EDGE,"E1133"),sQuery(id+"F0.wireOp",EDGE,"E1134"),sQuery(id+"F0.wireOp",EDGE,"E1135"),sQuery(id+"F0.wireOp",EDGE,"E1136"),sQuery(id+"F0.wireOp",EDGE,"E1137"),sQuery(id+"F0.wireOp",EDGE,"E1138"),sQuery(id+"F0.wireOp",EDGE,"E1139"),sQuery(id+"F0.wireOp",EDGE,"E1140"),sQuery(id+"F0.wireOp",EDGE,"E1141"),sQuery(id+"F0.wireOp",EDGE,"E1142"),sQuery(id+"F0.wireOp",EDGE,"E1143"),sQuery(id+"F0.wireOp",EDGE,"E1144"),sQuery(id+"F0.wireOp",EDGE,"E1145"),sQuery(id+"F0.wireOp",EDGE,"E1146"),sQuery(id+"F0.wireOp",EDGE,"E1147"),sQuery(id+"F0.wireOp",EDGE,"E1148"),sQuery(id+"F0.wireOp",EDGE,"E1149"),sQuery(id+"F0.wireOp",EDGE,"E1150"),sQuery(id+"F0.wireOp",EDGE,"E1151"),sQuery(id+"F0.wireOp",EDGE,"E1152"),sQuery(id+"F0.wireOp",EDGE,"E1153"),sQuery(id+"F0.wireOp",EDGE,"E1154"),sQuery(id+"F0.wireOp",EDGE,"E1155"),sQuery(id+"F0.wireOp",EDGE,"E1156"),sQuery(id+"F0.wireOp",EDGE,"E1157"),sQuery(id+"F0.wireOp",EDGE,"E1158"),sQuery(id+"F0.wireOp",EDGE,"E1159"),sQuery(id+"F0.wireOp",EDGE,"E1160"),sQuery(id+"F0.wireOp",EDGE,"E1161"),sQuery(id+"F0.wireOp",EDGE,"E1162"),sQuery(id+"F0.wireOp",EDGE,"E1163"),sQuery(id+"F0.wireOp",EDGE,"E1164"),sQuery(id+"F0.wireOp",EDGE,"E1165"),sQuery(id+"F0.wireOp",EDGE,"E1166"),sQuery(id+"F0.wireOp",EDGE,"E1167"),sQuery(id+"F0.wireOp",EDGE,"E1168"),sQuery(id+"F0.wireOp",EDGE,"E1169"),sQuery(id+"F0.wireOp",EDGE,"E1170"),sQuery(id+"F0.wireOp",EDGE,"E1171"),sQuery(id+"F0.wireOp",EDGE,"E1172"),sQuery(id+"F0.wireOp",EDGE,"E1173"),sQuery(id+"F0.wireOp",EDGE,"E1174"),sQuery(id+"F0.wireOp",EDGE,"E1175"),sQuery(id+"F0.wireOp",EDGE,"E1176"),sQuery(id+"F0.wireOp",EDGE,"E1177"),sQuery(id+"F0.wireOp",EDGE,"E1178"),sQuery(id+"F0.wireOp",EDGE,"E1179"),sQuery(id+"F0.wireOp",EDGE,"E1180"),sQuery(id+"F0.wireOp",EDGE,"E1181"),sQuery(id+"F0.wireOp",EDGE,"E1182"),sQuery(id+"F0.wireOp",EDGE,"E1183"),sQuery(id+"F0.wireOp",EDGE,"E1184"),sQuery(id+"F0.wireOp",EDGE,"E1185"),sQuery(id+"F0.wireOp",EDGE,"E1186"),sQuery(id+"F0.wireOp",EDGE,"E1187"),sQuery(id+"F0.wireOp",EDGE,"E1188"),sQuery(id+"F0.wireOp",EDGE,"E1189"),sQuery(id+"F0.wireOp",EDGE,"E1190"),sQuery(id+"F0.wireOp",EDGE,"E1191"),sQuery(id+"F0.wireOp",EDGE,"E1192"),sQuery(id+"F0.wireOp",EDGE,"E1193"),sQuery(id+"F0.wireOp",EDGE,"E1194"),sQuery(id+"F0.wireOp",EDGE,"E1195"),sQuery(id+"F0.wireOp",EDGE,"E1196"),sQuery(id+"F0.wireOp",EDGE,"E1197"),sQuery(id+"F0.wireOp",EDGE,"E1198"),sQuery(id+"F0.wireOp",EDGE,"E1199"),sQuery(id+"F0.wireOp",EDGE,"E1200"),sQuery(id+"F0.wireOp",EDGE,"E1201"),sQuery(id+"F0.wireOp",EDGE,"E1202"),sQuery(id+"F0.wireOp",EDGE,"E1203"),sQuery(id+"F0.wireOp",EDGE,"E1204"),sQuery(id+"F0.wireOp",EDGE,"E1205"),sQuery(id+"F0.wireOp",EDGE,"E1206"),sQuery(id+"F0.wireOp",EDGE,"E1207"),sQuery(id+"F0.wireOp",EDGE,"E1208"),sQuery(id+"F0.wireOp",EDGE,"E1209"),sQuery(id+"F0.wireOp",EDGE,"E1210"),sQuery(id+"F0.wireOp",EDGE,"E1211"),sQuery(id+"F0.wireOp",EDGE,"E1212"),sQuery(id+"F0.wireOp",EDGE,"E1213"),sQuery(id+"F0.wireOp",EDGE,"E1214"),sQuery(id+"F0.wireOp",EDGE,"E1215"),sQuery(id+"F0.wireOp",EDGE,"E1216"),sQuery(id+"F0.wireOp",EDGE,"E1217"),sQuery(id+"F0.wireOp",EDGE,"E1218"),sQuery(id+"F0.wireOp",EDGE,"E1219"),sQuery(id+"F0.wireOp",EDGE,"E1220"),sQuery(id+"F0.wireOp",EDGE,"E1221"),sQuery(id+"F0.wireOp",EDGE,"E1222"),sQuery(id+"F0.wireOp",EDGE,"E1223"),sQuery(id+"F0.wireOp",EDGE,"E1224"),sQuery(id+"F0.wireOp",EDGE,"E1225"),sQuery(id+"F0.wireOp",EDGE,"E1226"),sQuery(id+"F0.wireOp",EDGE,"E1227"),sQuery(id+"F0.wireOp",EDGE,"E1228"),sQuery(id+"F0.wireOp",EDGE,"E1229"),sQuery(id+"F0.wireOp",EDGE,"E1230"),sQuery(id+"F0.wireOp",EDGE,"E1231"),sQuery(id+"F0.wireOp",EDGE,"E1232"),sQuery(id+"F0.wireOp",EDGE,"E1233"),sQuery(id+"F0.wireOp",EDGE,"E1234"),sQuery(id+"F0.wireOp",EDGE,"E1235"),sQuery(id+"F0.wireOp",EDGE,"E1236"),sQuery(id+"F0.wireOp",EDGE,"E1237"),sQuery(id+"F0.wireOp",EDGE,"E1238"),sQuery(id+"F0.wireOp",EDGE,"E1239"),sQuery(id+"F0.wireOp",EDGE,"E1240"),sQuery(id+"F0.wireOp",EDGE,"E1241"),sQuery(id+"F0.wireOp",EDGE,"E1242"),sQuery(id+"F0.wireOp",EDGE,"E1243"),sQuery(id+"F0.wireOp",EDGE,"E1244"),sQuery(id+"F0.wireOp",EDGE,"E1245"),sQuery(id+"F0.wireOp",EDGE,"E1246"),sQuery(id+"F0.wireOp",EDGE,"E1247"),sQuery(id+"F0.wireOp",EDGE,"E1248"),sQuery(id+"F0.wireOp",EDGE,"E1249"),sQuery(id+"F0.wireOp",EDGE,"E1250"),sQuery(id+"F0.wireOp",EDGE,"E1251"),sQuery(id+"F0.wireOp",EDGE,"E1252"),sQuery(id+"F0.wireOp",EDGE,"E1253"),sQuery(id+"F0.wireOp",EDGE,"E1254"),sQuery(id+"F0.wireOp",EDGE,"E1255"),sQuery(id+"F0.wireOp",EDGE,"E1256"),sQuery(id+"F0.wireOp",EDGE,"E1257"),sQuery(id+"F0.wireOp",EDGE,"E1258"),sQuery(id+"F0.wireOp",EDGE,"E1259"),sQuery(id+"F0.wireOp",EDGE,"E1260"),sQuery(id+"F0.wireOp",EDGE,"E1261"),sQuery(id+"F0.wireOp",EDGE,"E1262"),sQuery(id+"F0.wireOp",EDGE,"E1263"),sQuery(id+"F0.wireOp",EDGE,"E1264"),sQuery(id+"F0.wireOp",EDGE,"E1265"),sQuery(id+"F0.wireOp",EDGE,"E1266"),sQuery(id+"F0.wireOp",EDGE,"E1267"),sQuery(id+"F0.wireOp",EDGE,"E1268"),sQuery(id+"F0.wireOp",EDGE,"E1269"),sQuery(id+"F0.wireOp",EDGE,"E1270"),sQuery(id+"F0.wireOp",EDGE,"E1271"),sQuery(id+"F0.wireOp",EDGE,"E1272"),sQuery(id+"F0.wireOp",EDGE,"E1273"),sQuery(id+"F0.wireOp",EDGE,"E1274"),sQuery(id+"F0.wireOp",EDGE,"E1275"),sQuery(id+"F0.wireOp",EDGE,"E1276"),sQuery(id+"F0.wireOp",EDGE,"E1277"),sQuery(id+"F0.wireOp",EDGE,"E1278"),sQuery(id+"F0.wireOp",EDGE,"E1279"),sQuery(id+"F0.wireOp",EDGE,"E1280"),sQuery(id+"F0.wireOp",EDGE,"E1281"),sQuery(id+"F0.wireOp",EDGE,"E1282"),sQuery(id+"F0.wireOp",EDGE,"E1283"),sQuery(id+"F0.wireOp",EDGE,"E1284"),sQuery(id+"F0.wireOp",EDGE,"E1285"),sQuery(id+"F0.wireOp",EDGE,"E1286"),sQuery(id+"F0.wireOp",EDGE,"E1287"),sQuery(id+"F0.wireOp",EDGE,"E1288"),sQuery(id+"F0.wireOp",EDGE,"E1289"),sQuery(id+"F0.wireOp",EDGE,"E1290"),sQuery(id+"F0.wireOp",EDGE,"E1291"),sQuery(id+"F0.wireOp",EDGE,"E1292"),sQuery(id+"F0.wireOp",EDGE,"E1293"),sQuery(id+"F0.wireOp",EDGE,"E1294"),sQuery(id+"F0.wireOp",EDGE,"E1295"),sQuery(id+"F0.wireOp",EDGE,"E1296"),sQuery(id+"F0.wireOp",EDGE,"E1297"),sQuery(id+"F0.wireOp",EDGE,"E1298"),sQuery(id+"F0.wireOp",EDGE,"E1299"),sQuery(id+"F0.wireOp",EDGE,"E1300"),sQuery(id+"F0.wireOp",EDGE,"E1301"),sQuery(id+"F0.wireOp",EDGE,"E1302"),sQuery(id+"F0.wireOp",EDGE,"E1303"),sQuery(id+"F0.wireOp",EDGE,"E1304"),sQuery(id+"F0.wireOp",EDGE,"E1305"),sQuery(id+"F0.wireOp",EDGE,"E1306"),sQuery(id+"F0.wireOp",EDGE,"E1307"),sQuery(id+"F0.wireOp",EDGE,"E1308"),sQuery(id+"F0.wireOp",EDGE,"E1309"),sQuery(id+"F0.wireOp",EDGE,"E1310"),sQuery(id+"F0.wireOp",EDGE,"E1311"),sQuery(id+"F0.wireOp",EDGE,"E1312"),sQuery(id+"F0.wireOp",EDGE,"E1313"),sQuery(id+"F0.wireOp",EDGE,"E1314"),sQuery(id+"F0.wireOp",EDGE,"E1315"),sQuery(id+"F0.wireOp",EDGE,"E1316"),sQuery(id+"F0.wireOp",EDGE,"E1317"),sQuery(id+"F0.wireOp",EDGE,"E1318"),sQuery(id+"F0.wireOp",EDGE,"E1319"),sQuery(id+"F0.wireOp",EDGE,"E1320"),sQuery(id+"F0.wireOp",EDGE,"E1321"),sQuery(id+"F0.wireOp",EDGE,"E1322"),sQuery(id+"F0.wireOp",EDGE,"E1323"),sQuery(id+"F0.wireOp",EDGE,"E1324"),sQuery(id+"F0.wireOp",EDGE,"E1325"),sQuery(id+"F0.wireOp",EDGE,"E1326"),sQuery(id+"F0.wireOp",EDGE,"E1327"),sQuery(id+"F0.wireOp",EDGE,"E1328"),sQuery(id+"F0.wireOp",EDGE,"E1329"),sQuery(id+"F0.wireOp",EDGE,"E1330"),sQuery(id+"F0.wireOp",EDGE,"E1331"),sQuery(id+"F0.wireOp",EDGE,"E1332"),sQuery(id+"F0.wireOp",EDGE,"E1333"),sQuery(id+"F0.wireOp",EDGE,"E1334"),sQuery(id+"F0.wireOp",EDGE,"E1335"),sQuery(id+"F0.wireOp",EDGE,"E1336"),sQuery(id+"F0.wireOp",EDGE,"E1337"),sQuery(id+"F0.wireOp",EDGE,"E1338"),sQuery(id+"F0.wireOp",EDGE,"E1339"),sQuery(id+"F0.wireOp",EDGE,"E1340"),sQuery(id+"F0.wireOp",EDGE,"E1341"),sQuery(id+"F0.wireOp",EDGE,"E1342"),sQuery(id+"F0.wireOp",EDGE,"E1343"),sQuery(id+"F0.wireOp",EDGE,"E1344"),sQuery(id+"F0.wireOp",EDGE,"E1345"),sQuery(id+"F0.wireOp",EDGE,"E1346"),sQuery(id+"F0.wireOp",EDGE,"E1347"),sQuery(id+"F0.wireOp",EDGE,"E1348"),sQuery(id+"F0.wireOp",EDGE,"E1349"),sQuery(id+"F0.wireOp",EDGE,"E1350"),sQuery(id+"F0.wireOp",EDGE,"E1351"),sQuery(id+"F0.wireOp",EDGE,"E1352"),sQuery(id+"F0.wireOp",EDGE,"E1353"),sQuery(id+"F0.wireOp",EDGE,"E1354"),sQuery(id+"F0.wireOp",EDGE,"E1355"),sQuery(id+"F0.wireOp",EDGE,"E1356"),sQuery(id+"F0.wireOp",EDGE,"E1357"),sQuery(id+"F0.wireOp",EDGE,"E1358"),sQuery(id+"F0.wireOp",EDGE,"E1359"),sQuery(id+"F0.wireOp",EDGE,"E1360"),sQuery(id+"F0.wireOp",EDGE,"E1361"),sQuery(id+"F0.wireOp",EDGE,"E1362"),sQuery(id+"F0.wireOp",EDGE,"E1363"),sQuery(id+"F0.wireOp",EDGE,"E1364"),sQuery(id+"F0.wireOp",EDGE,"E1365"),sQuery(id+"F0.wireOp",EDGE,"E1366"),sQuery(id+"F0.wireOp",EDGE,"E1367"),sQuery(id+"F0.wireOp",EDGE,"E1368"),sQuery(id+"F0.wireOp",EDGE,"E1369"),sQuery(id+"F0.wireOp",EDGE,"E1370"),sQuery(id+"F0.wireOp",EDGE,"E1371"),sQuery(id+"F0.wireOp",EDGE,"E1372"),sQuery(id+"F0.wireOp",EDGE,"E1373"),sQuery(id+"F0.wireOp",EDGE,"E1374"),sQuery(id+"F0.wireOp",EDGE,"E1375"),sQuery(id+"F0.wireOp",EDGE,"E1376"),sQuery(id+"F0.wireOp",EDGE,"E1377"),sQuery(id+"F0.wireOp",EDGE,"E1378"),sQuery(id+"F0.wireOp",EDGE,"E1379"),sQuery(id+"F0.wireOp",EDGE,"E1380"),sQuery(id+"F0.wireOp",EDGE,"E1381"),sQuery(id+"F0.wireOp",EDGE,"E1382"),sQuery(id+"F0.wireOp",EDGE,"E1383"),sQuery(id+"F0.wireOp",EDGE,"E1384"),sQuery(id+"F0.wireOp",EDGE,"E1385"),sQuery(id+"F0.wireOp",EDGE,"E1386"),sQuery(id+"F0.wireOp",EDGE,"E1387"),sQuery(id+"F0.wireOp",EDGE,"E1388"),sQuery(id+"F0.wireOp",EDGE,"E1389"),sQuery(id+"F0.wireOp",EDGE,"E1390"),sQuery(id+"F0.wireOp",EDGE,"E1391"),sQuery(id+"F0.wireOp",EDGE,"E1392"),sQuery(id+"F0.wireOp",EDGE,"E1393"),sQuery(id+"F0.wireOp",EDGE,"E1394"),sQuery(id+"F0.wireOp",EDGE,"E1395"),sQuery(id+"F0.wireOp",EDGE,"E1396"),sQuery(id+"F0.wireOp",EDGE,"E1397"),sQuery(id+"F0.wireOp",EDGE,"E1398"),sQuery(id+"F0.wireOp",EDGE,"E1399"),sQuery(id+"F0.wireOp",EDGE,"E1400"),sQuery(id+"F0.wireOp",EDGE,"E1401"),sQuery(id+"F0.wireOp",EDGE,"E1402"),sQuery(id+"F0.wireOp",EDGE,"E1403"),sQuery(id+"F0.wireOp",EDGE,"E1404"),sQuery(id+"F0.wireOp",EDGE,"E1405"),sQuery(id+"F0.wireOp",EDGE,"E1406"),sQuery(id+"F0.wireOp",EDGE,"E1407"),sQuery(id+"F0.wireOp",EDGE,"E1408"),sQuery(id+"F0.wireOp",EDGE,"E1409"),sQuery(id+"F0.wireOp",EDGE,"E1410"),sQuery(id+"F0.wireOp",EDGE,"E1411"),sQuery(id+"F0.wireOp",EDGE,"E1412"),sQuery(id+"F0.wireOp",EDGE,"E1413"),sQuery(id+"F0.wireOp",EDGE,"E1414"),sQuery(id+"F0.wireOp",EDGE,"E1415"),sQuery(id+"F0.wireOp",EDGE,"E1416"),sQuery(id+"F0.wireOp",EDGE,"E1417"),sQuery(id+"F0.wireOp",EDGE,"E1418"),sQuery(id+"F0.wireOp",EDGE,"E1419"),sQuery(id+"F0.wireOp",EDGE,"E1420"),sQuery(id+"F0.wireOp",EDGE,"E1421"),sQuery(id+"F0.wireOp",EDGE,"E1422"),sQuery(id+"F0.wireOp",EDGE,"E1423"),sQuery(id+"F0.wireOp",EDGE,"E1424"),sQuery(id+"F0.wireOp",EDGE,"E1425"),sQuery(id+"F0.wireOp",EDGE,"E1426"),sQuery(id+"F0.wireOp",EDGE,"E1427"),sQuery(id+"F0.wireOp",EDGE,"E1428"),sQuery(id+"F0.wireOp",EDGE,"E1429"),sQuery(id+"F0.wireOp",EDGE,"E1430"),sQuery(id+"F0.wireOp",EDGE,"E1431"),sQuery(id+"F0.wireOp",EDGE,"E1432"),sQuery(id+"F0.wireOp",EDGE,"E1433"),sQuery(id+"F0.wireOp",EDGE,"E1434"),sQuery(id+"F0.wireOp",EDGE,"E1435"),sQuery(id+"F0.wireOp",EDGE,"E1436"),sQuery(id+"F0.wireOp",EDGE,"E1437"),sQuery(id+"F0.wireOp",EDGE,"E1438"),sQuery(id+"F0.wireOp",EDGE,"E1439"),sQuery(id+"F0.wireOp",EDGE,"E1440"),sQuery(id+"F0.wireOp",EDGE,"E1441"),sQuery(id+"F0.wireOp",EDGE,"E1442"),sQuery(id+"F0.wireOp",EDGE,"E1443"),sQuery(id+"F0.wireOp",EDGE,"E1444"),sQuery(id+"F0.wireOp",EDGE,"E1445"),sQuery(id+"F0.wireOp",EDGE,"E1446"),sQuery(id+"F0.wireOp",EDGE,"E1447"),sQuery(id+"F0.wireOp",EDGE,"E1448"),sQuery(id+"F0.wireOp",EDGE,"E1449"),sQuery(id+"F0.wireOp",EDGE,"E1450"),sQuery(id+"F0.wireOp",EDGE,"E1451"),sQuery(id+"F0.wireOp",EDGE,"E1452"),sQuery(id+"F0.wireOp",EDGE,"E1453"),sQuery(id+"F0.wireOp",EDGE,"E1454"),sQuery(id+"F0.wireOp",EDGE,"E1455"),sQuery(id+"F0.wireOp",EDGE,"E1456"),sQuery(id+"F0.wireOp",EDGE,"E1457"),sQuery(id+"F0.wireOp",EDGE,"E1458"),sQuery(id+"F0.wireOp",EDGE,"E1459"),sQuery(id+"F0.wireOp",EDGE,"E1460"),sQuery(id+"F0.wireOp",EDGE,"E1461"),sQuery(id+"F0.wireOp",EDGE,"E1462"),sQuery(id+"F0.wireOp",EDGE,"E1463"),sQuery(id+"F0.wireOp",EDGE,"E1464"),sQuery(id+"F0.wireOp",EDGE,"E1465"),sQuery(id+"F0.wireOp",EDGE,"E1466"),sQuery(id+"F0.wireOp",EDGE,"E1467"),sQuery(id+"F0.wireOp",EDGE,"E1468"),sQuery(id+"F0.wireOp",EDGE,"E1469"),sQuery(id+"F0.wireOp",EDGE,"E1470"),sQuery(id+"F0.wireOp",EDGE,"E1471"),sQuery(id+"F0.wireOp",EDGE,"E1472"),sQuery(id+"F0.wireOp",EDGE,"E1473"),sQuery(id+"F0.wireOp",EDGE,"E1474"),sQuery(id+"F0.wireOp",EDGE,"E1475"),sQuery(id+"F0.wireOp",EDGE,"E1476"),sQuery(id+"F0.wireOp",EDGE,"E1477"),sQuery(id+"F0.wireOp",EDGE,"E1478"),sQuery(id+"F0.wireOp",EDGE,"E1479"),sQuery(id+"F0.wireOp",EDGE,"E1480"),sQuery(id+"F0.wireOp",EDGE,"E1481"),sQuery(id+"F0.wireOp",EDGE,"E1482"),sQuery(id+"F0.wireOp",EDGE,"E1483"),sQuery(id+"F0.wireOp",EDGE,"E1484"),sQuery(id+"F0.wireOp",EDGE,"E1485"),sQuery(id+"F0.wireOp",EDGE,"E1486"),sQuery(id+"F0.wireOp",EDGE,"E1487"),sQuery(id+"F0.wireOp",EDGE,"E1488"),sQuery(id+"F0.wireOp",EDGE,"E1489"),sQuery(id+"F0.wireOp",EDGE,"E1490"),sQuery(id+"F0.wireOp",EDGE,"E1491"),sQuery(id+"F0.wireOp",EDGE,"E1492"),sQuery(id+"F0.wireOp",EDGE,"E1493"),sQuery(id+"F0.wireOp",EDGE,"E1494"),sQuery(id+"F0.wireOp",EDGE,"E1495"),sQuery(id+"F0.wireOp",EDGE,"E1496"),sQuery(id+"F0.wireOp",EDGE,"E1497"),sQuery(id+"F0.wireOp",EDGE,"E1498"),sQuery(id+"F0.wireOp",EDGE,"E1499"),sQuery(id+"F0.wireOp",EDGE,"E1500"),sQuery(id+"F0.wireOp",EDGE,"E1501"),sQuery(id+"F0.wireOp",EDGE,"E1502"),sQuery(id+"F0.wireOp",EDGE,"E1503"),sQuery(id+"F0.wireOp",EDGE,"E1504"),sQuery(id+"F0.wireOp",EDGE,"E1505"),sQuery(id+"F0.wireOp",EDGE,"E1506"),sQuery(id+"F0.wireOp",EDGE,"E1507"),sQuery(id+"F0.wireOp",EDGE,"E1508"),sQuery(id+"F0.wireOp",EDGE,"E1509"),sQuery(id+"F0.wireOp",EDGE,"E1510"),sQuery(id+"F0.wireOp",EDGE,"E1511"),sQuery(id+"F0.wireOp",EDGE,"E1512"),sQuery(id+"F0.wireOp",EDGE,"E1513"),sQuery(id+"F0.wireOp",EDGE,"E1514"),sQuery(id+"F0.wireOp",EDGE,"E1515"),sQuery(id+"F0.wireOp",EDGE,"E1516"),sQuery(id+"F0.wireOp",EDGE,"E1517"),sQuery(id+"F0.wireOp",EDGE,"E1518"),sQuery(id+"F0.wireOp",EDGE,"E1519"),sQuery(id+"F0.wireOp",EDGE,"E1520"),sQuery(id+"F0.wireOp",EDGE,"E1521"),sQuery(id+"F0.wireOp",EDGE,"E1522"),sQuery(id+"F0.wireOp",EDGE,"E1523"),sQuery(id+"F0.wireOp",EDGE,"E1524"),sQuery(id+"F0.wireOp",EDGE,"E1525"),sQuery(id+"F0.wireOp",EDGE,"E1526"),sQuery(id+"F0.wireOp",EDGE,"E1527"),sQuery(id+"F0.wireOp",EDGE,"E1528"),sQuery(id+"F0.wireOp",EDGE,"E1529"),sQuery(id+"F0.wireOp",EDGE,"E1530"),sQuery(id+"F0.wireOp",EDGE,"E1531"),sQuery(id+"F0.wireOp",EDGE,"E1532"),sQuery(id+"F0.wireOp",EDGE,"E1533"),sQuery(id+"F0.wireOp",EDGE,"E1534"),sQuery(id+"F0.wireOp",EDGE,"E1535"),sQuery(id+"F0.wireOp",EDGE,"E1536"),sQuery(id+"F0.wireOp",EDGE,"E1537"),sQuery(id+"F0.wireOp",EDGE,"E1538"),sQuery(id+"F0.wireOp",EDGE,"E1539"),sQuery(id+"F0.wireOp",EDGE,"E1540"),sQuery(id+"F0.wireOp",EDGE,"E1541"),sQuery(id+"F0.wireOp",EDGE,"E1542"),sQuery(id+"F0.wireOp",EDGE,"E1543"),sQuery(id+"F0.wireOp",EDGE,"E1544"),sQuery(id+"F0.wireOp",EDGE,"E1545"),sQuery(id+"F0.wireOp",EDGE,"E1546"),sQuery(id+"F0.wireOp",EDGE,"E1547"),sQuery(id+"F0.wireOp",EDGE,"E1548"),sQuery(id+"F0.wireOp",EDGE,"E1549"),sQuery(id+"F0.wireOp",EDGE,"E1550"),sQuery(id+"F0.wireOp",EDGE,"E1551"),sQuery(id+"F0.wireOp",EDGE,"E1552"),sQuery(id+"F0.wireOp",EDGE,"E1553"),sQuery(id+"F0.wireOp",EDGE,"E1554"),sQuery(id+"F0.wireOp",EDGE,"E1555"),sQuery(id+"F0.wireOp",EDGE,"E1556"),sQuery(id+"F0.wireOp",EDGE,"E1557"),sQuery(id+"F0.wireOp",EDGE,"E1558"),sQuery(id+"F0.wireOp",EDGE,"E1559"),sQuery(id+"F0.wireOp",EDGE,"E1560"),sQuery(id+"F0.wireOp",EDGE,"E1561"),sQuery(id+"F0.wireOp",EDGE,"E1562"),sQuery(id+"F0.wireOp",EDGE,"E1563"),sQuery(id+"F0.wireOp",EDGE,"E1564"),sQuery(id+"F0.wireOp",EDGE,"E1565"),sQuery(id+"F0.wireOp",EDGE,"E1566"),sQuery(id+"F0.wireOp",EDGE,"E1567"),sQuery(id+"F0.wireOp",EDGE,"E1568"),sQuery(id+"F0.wireOp",EDGE,"E1569"),sQuery(id+"F0.wireOp",EDGE,"E1570"),sQuery(id+"F0.wireOp",EDGE,"E1571"),sQuery(id+"F0.wireOp",EDGE,"E1572"),sQuery(id+"F0.wireOp",EDGE,"E1573"),sQuery(id+"F0.wireOp",EDGE,"E1574"),sQuery(id+"F0.wireOp",EDGE,"E1575"),sQuery(id+"F0.wireOp",EDGE,"E1576"),sQuery(id+"F0.wireOp",EDGE,"E1577"),sQuery(id+"F0.wireOp",EDGE,"E1578"),sQuery(id+"F0.wireOp",EDGE,"E1579"),sQuery(id+"F0.wireOp",EDGE,"E1580"),sQuery(id+"F0.wireOp",EDGE,"E1581"),sQuery(id+"F0.wireOp",EDGE,"E1582"),sQuery(id+"F0.wireOp",EDGE,"E1583"),sQuery(id+"F0.wireOp",EDGE,"E1584"),sQuery(id+"F0.wireOp",EDGE,"E1585"),sQuery(id+"F0.wireOp",EDGE,"E1586"),sQuery(id+"F0.wireOp",EDGE,"E1587"),sQuery(id+"F0.wireOp",EDGE,"E1588"),sQuery(id+"F0.wireOp",EDGE,"E1589"),sQuery(id+"F0.wireOp",EDGE,"E1590"),sQuery(id+"F0.wireOp",EDGE,"E1591"),sQuery(id+"F0.wireOp",EDGE,"E1592"),sQuery(id+"F0.wireOp",EDGE,"E1593"),sQuery(id+"F0.wireOp",EDGE,"E1594"),sQuery(id+"F0.wireOp",EDGE,"E1595"),sQuery(id+"F0.wireOp",EDGE,"E1596"),sQuery(id+"F0.wireOp",EDGE,"E1597"),sQuery(id+"F0.wireOp",EDGE,"E1598"),sQuery(id+"F0.wireOp",EDGE,"E1599"),sQuery(id+"F0.wireOp",EDGE,"E1600"),sQuery(id+"F0.wireOp",EDGE,"E1601"),sQuery(id+"F0.wireOp",EDGE,"E1602"),sQuery(id+"F0.wireOp",EDGE,"E1603"),sQuery(id+"F0.wireOp",EDGE,"E1604"),sQuery(id+"F0.wireOp",EDGE,"E1605"),sQuery(id+"F0.wireOp",EDGE,"E1606"),sQuery(id+"F0.wireOp",EDGE,"E1607"),sQuery(id+"F0.wireOp",EDGE,"E1608"),sQuery(id+"F0.wireOp",EDGE,"E1609"),sQuery(id+"F0.wireOp",EDGE,"E1610"),sQuery(id+"F0.wireOp",EDGE,"E1611"),sQuery(id+"F0.wireOp",EDGE,"E1612"),sQuery(id+"F0.wireOp",EDGE,"E1613"),sQuery(id+"F0.wireOp",EDGE,"E1614"),sQuery(id+"F0.wireOp",EDGE,"E1615"),sQuery(id+"F0.wireOp",EDGE,"E1616"),sQuery(id+"F0.wireOp",EDGE,"E1617"),sQuery(id+"F0.wireOp",EDGE,"E1618"),sQuery(id+"F0.wireOp",EDGE,"E1619"),sQuery(id+"F0.wireOp",EDGE,"E1620"),sQuery(id+"F0.wireOp",EDGE,"E1621"),sQuery(id+"F0.wireOp",EDGE,"E1622"),sQuery(id+"F0.wireOp",EDGE,"E1623"),sQuery(id+"F0.wireOp",EDGE,"E1624"),sQuery(id+"F0.wireOp",EDGE,"E1625"),sQuery(id+"F0.wireOp",EDGE,"E1626"),sQuery(id+"F0.wireOp",EDGE,"E1627"),sQuery(id+"F0.wireOp",EDGE,"E1628"),sQuery(id+"F0.wireOp",EDGE,"E1629"),sQuery(id+"F0.wireOp",EDGE,"E1630"),sQuery(id+"F0.wireOp",EDGE,"E1631"),sQuery(id+"F0.wireOp",EDGE,"E1632"),sQuery(id+"F0.wireOp",EDGE,"E1633"),sQuery(id+"F0.wireOp",EDGE,"E1634"),sQuery(id+"F0.wireOp",EDGE,"E1635"),sQuery(id+"F0.wireOp",EDGE,"E1636"),sQuery(id+"F0.wireOp",EDGE,"E1637"),sQuery(id+"F0.wireOp",EDGE,"E1638"),sQuery(id+"F0.wireOp",EDGE,"E1639"),sQuery(id+"F0.wireOp",EDGE,"E1640"),sQuery(id+"F0.wireOp",EDGE,"E1641"),sQuery(id+"F0.wireOp",EDGE,"E1642"),sQuery(id+"F0.wireOp",EDGE,"E1643"),sQuery(id+"F0.wireOp",EDGE,"E1644"),sQuery(id+"F0.wireOp",EDGE,"E1645"),sQuery(id+"F0.wireOp",EDGE,"E1646"),sQuery(id+"F0.wireOp",EDGE,"E1647"),sQuery(id+"F0.wireOp",EDGE,"E1648"),sQuery(id+"F0.wireOp",EDGE,"E1649"),sQuery(id+"F0.wireOp",EDGE,"E1650"),sQuery(id+"F0.wireOp",EDGE,"E1651"),sQuery(id+"F0.wireOp",EDGE,"E1652"),sQuery(id+"F0.wireOp",EDGE,"E1653"),sQuery(id+"F0.wireOp",EDGE,"E1654"),sQuery(id+"F0.wireOp",EDGE,"E1655"),sQuery(id+"F0.wireOp",EDGE,"E1656"),sQuery(id+"F0.wireOp",EDGE,"E1657"),sQuery(id+"F0.wireOp",EDGE,"E1658"),sQuery(id+"F0.wireOp",EDGE,"E1659"),sQuery(id+"F0.wireOp",EDGE,"E1660"),sQuery(id+"F0.wireOp",EDGE,"E1661"),sQuery(id+"F0.wireOp",EDGE,"E1662"),sQuery(id+"F0.wireOp",EDGE,"E1663"),sQuery(id+"F0.wireOp",EDGE,"E1664"),sQuery(id+"F0.wireOp",EDGE,"E1665"),sQuery(id+"F0.wireOp",EDGE,"E1666"),sQuery(id+"F0.wireOp",EDGE,"E1667"),sQuery(id+"F0.wireOp",EDGE,"E1668"),sQuery(id+"F0.wireOp",EDGE,"E1669"),sQuery(id+"F0.wireOp",EDGE,"E1670"),sQuery(id+"F0.wireOp",EDGE,"E1671"),sQuery(id+"F0.wireOp",EDGE,"E1672"),sQuery(id+"F0.wireOp",EDGE,"E1673"),sQuery(id+"F0.wireOp",EDGE,"E1674"),sQuery(id+"F0.wireOp",EDGE,"E1675"),sQuery(id+"F0.wireOp",EDGE,"E1676"),sQuery(id+"F0.wireOp",EDGE,"E1677"),sQuery(id+"F0.wireOp",EDGE,"E1678"),sQuery(id+"F0.wireOp",EDGE,"E1679"),sQuery(id+"F0.wireOp",EDGE,"E1680"),sQuery(id+"F0.wireOp",EDGE,"E1681"),sQuery(id+"F0.wireOp",EDGE,"E1682"),sQuery(id+"F0.wireOp",EDGE,"E1683"),sQuery(id+"F0.wireOp",EDGE,"E1684"),sQuery(id+"F0.wireOp",EDGE,"E1685"),sQuery(id+"F0.wireOp",EDGE,"E1686"),sQuery(id+"F0.wireOp",EDGE,"E1687"),sQuery(id+"F0.wireOp",EDGE,"E1688"),sQuery(id+"F0.wireOp",EDGE,"E1689"),sQuery(id+"F0.wireOp",EDGE,"E1690"),sQuery(id+"F0.wireOp",EDGE,"E1691"),sQuery(id+"F0.wireOp",EDGE,"E1692"),sQuery(id+"F0.wireOp",EDGE,"E1693"),sQuery(id+"F0.wireOp",EDGE,"E1694"),sQuery(id+"F0.wireOp",EDGE,"E1695"),sQuery(id+"F0.wireOp",EDGE,"E1696"),sQuery(id+"F0.wireOp",EDGE,"E1697"),sQuery(id+"F0.wireOp",EDGE,"E1698"),sQuery(id+"F0.wireOp",EDGE,"E1699"),sQuery(id+"F0.wireOp",EDGE,"E1700"),sQuery(id+"F0.wireOp",EDGE,"E1701"),sQuery(id+"F0.wireOp",EDGE,"E1702"),sQuery(id+"F0.wireOp",EDGE,"E1703"),sQuery(id+"F0.wireOp",EDGE,"E1704"),sQuery(id+"F0.wireOp",EDGE,"E1705"),sQuery(id+"F0.wireOp",EDGE,"E1706"),sQuery(id+"F0.wireOp",EDGE,"E1707"),sQuery(id+"F0.wireOp",EDGE,"E1708"),sQuery(id+"F0.wireOp",EDGE,"E1709"),sQuery(id+"F0.wireOp",EDGE,"E1710"),sQuery(id+"F0.wireOp",EDGE,"E1711"),sQuery(id+"F0.wireOp",EDGE,"E1712"),sQuery(id+"F0.wireOp",EDGE,"E1713"),sQuery(id+"F0.wireOp",EDGE,"E1714"),sQuery(id+"F0.wireOp",EDGE,"E1715"),sQuery(id+"F0.wireOp",EDGE,"E1716"),sQuery(id+"F0.wireOp",EDGE,"E1717"),sQuery(id+"F0.wireOp",EDGE,"E1718"),sQuery(id+"F0.wireOp",EDGE,"E1719"),sQuery(id+"F0.wireOp",EDGE,"E1720"),sQuery(id+"F0.wireOp",EDGE,"E1721"),sQuery(id+"F0.wireOp",EDGE,"E1722"),sQuery(id+"F0.wireOp",EDGE,"E1723"),sQuery(id+"F0.wireOp",EDGE,"E1724"),sQuery(id+"F0.wireOp",EDGE,"E1725"),sQuery(id+"F0.wireOp",EDGE,"E1726"),sQuery(id+"F0.wireOp",EDGE,"E1727"),sQuery(id+"F0.wireOp",EDGE,"E1728"),sQuery(id+"F0.wireOp",EDGE,"E1729"),sQuery(id+"F0.wireOp",EDGE,"E1730"),sQuery(id+"F0.wireOp",EDGE,"E1731"),sQuery(id+"F0.wireOp",EDGE,"E1732"),sQuery(id+"F0.wireOp",EDGE,"E1733"),sQuery(id+"F0.wireOp",EDGE,"E1734"),sQuery(id+"F0.wireOp",EDGE,"E1735"),sQuery(id+"F0.wireOp",EDGE,"E1736"),sQuery(id+"F0.wireOp",EDGE,"E1737"),sQuery(id+"F0.wireOp",EDGE,"E1738"),sQuery(id+"F0.wireOp",EDGE,"E1739"),sQuery(id+"F0.wireOp",EDGE,"E1740"),sQuery(id+"F0.wireOp",EDGE,"E1741"),sQuery(id+"F0.wireOp",EDGE,"E1742"),sQuery(id+"F0.wireOp",EDGE,"E1743"),sQuery(id+"F0.wireOp",EDGE,"E1744"),sQuery(id+"F0.wireOp",EDGE,"E1745"),sQuery(id+"F0.wireOp",EDGE,"E1746"),sQuery(id+"F0.wireOp",EDGE,"E1747"),sQuery(id+"F0.wireOp",EDGE,"E1748"),sQuery(id+"F0.wireOp",EDGE,"E1749"),sQuery(id+"F0.wireOp",EDGE,"E1750"),sQuery(id+"F0.wireOp",EDGE,"E1751"),sQuery(id+"F0.wireOp",EDGE,"E1752"),sQuery(id+"F0.wireOp",EDGE,"E1753"),sQuery(id+"F0.wireOp",EDGE,"E1754"),sQuery(id+"F0.wireOp",EDGE,"E1755"),sQuery(id+"F0.wireOp",EDGE,"E1756"),sQuery(id+"F0.wireOp",EDGE,"E1757"),sQuery(id+"F0.wireOp",EDGE,"E1758"),sQuery(id+"F0.wireOp",EDGE,"E1759"),sQuery(id+"F0.wireOp",EDGE,"E1760"),sQuery(id+"F0.wireOp",EDGE,"E1761"),sQuery(id+"F0.wireOp",EDGE,"E1762"),sQuery(id+"F0.wireOp",EDGE,"E1763"),sQuery(id+"F0.wireOp",EDGE,"E1764"),sQuery(id+"F0.wireOp",EDGE,"E1765"),sQuery(id+"F0.wireOp",EDGE,"E1766"),sQuery(id+"F0.wireOp",EDGE,"E1767"),sQuery(id+"F0.wireOp",EDGE,"E1768"),sQuery(id+"F0.wireOp",EDGE,"E1769"),sQuery(id+"F0.wireOp",EDGE,"E1770"),sQuery(id+"F0.wireOp",EDGE,"E1771"),sQuery(id+"F0.wireOp",EDGE,"E1772"),sQuery(id+"F0.wireOp",EDGE,"E1773"),sQuery(id+"F0.wireOp",EDGE,"E1774"),sQuery(id+"F0.wireOp",EDGE,"E1775"),sQuery(id+"F0.wireOp",EDGE,"E1776"),sQuery(id+"F0.wireOp",EDGE,"E1777"),sQuery(id+"F0.wireOp",EDGE,"E1778"),sQuery(id+"F0.wireOp",EDGE,"E1779"),sQuery(id+"F0.wireOp",EDGE,"E1780"),sQuery(id+"F0.wireOp",EDGE,"E1781"),sQuery(id+"F0.wireOp",EDGE,"E1782"),sQuery(id+"F0.wireOp",EDGE,"E1783"),sQuery(id+"F0.wireOp",EDGE,"E1784"),sQuery(id+"F0.wireOp",EDGE,"E1785"),sQuery(id+"F0.wireOp",EDGE,"E1786"),sQuery(id+"F0.wireOp",EDGE,"E1787"),sQuery(id+"F0.wireOp",EDGE,"E1788"),sQuery(id+"F0.wireOp",EDGE,"E1789"),sQuery(id+"F0.wireOp",EDGE,"E1790"),sQuery(id+"F0.wireOp",EDGE,"E1791"),sQuery(id+"F0.wireOp",EDGE,"E1792"),sQuery(id+"F0.wireOp",EDGE,"E1793"),sQuery(id+"F0.wireOp",EDGE,"E1794"),sQuery(id+"F0.wireOp",EDGE,"E1795"),sQuery(id+"F0.wireOp",EDGE,"E1796"),sQuery(id+"F0.wireOp",EDGE,"E1797"),sQuery(id+"F0.wireOp",EDGE,"E1798"),sQuery(id+"F0.wireOp",EDGE,"E1799"),sQuery(id+"F0.wireOp",EDGE,"E1800"),sQuery(id+"F0.wireOp",EDGE,"E1801"),sQuery(id+"F0.wireOp",EDGE,"E1802"),sQuery(id+"F0.wireOp",EDGE,"E1803"),sQuery(id+"F0.wireOp",EDGE,"E1804"),sQuery(id+"F0.wireOp",EDGE,"E1805"),sQuery(id+"F0.wireOp",EDGE,"E1806"),sQuery(id+"F0.wireOp",EDGE,"E1807"),sQuery(id+"F0.wireOp",EDGE,"E1808"),sQuery(id+"F0.wireOp",EDGE,"E1809"),sQuery(id+"F0.wireOp",EDGE,"E1810"),sQuery(id+"F0.wireOp",EDGE,"E1811"),sQuery(id+"F0.wireOp",EDGE,"E1812"),sQuery(id+"F0.wireOp",EDGE,"E1813"),sQuery(id+"F0.wireOp",EDGE,"E1814"),sQuery(id+"F0.wireOp",EDGE,"E1815"),sQuery(id+"F0.wireOp",EDGE,"E1816"),sQuery(id+"F0.wireOp",EDGE,"E1817"),sQuery(id+"F0.wireOp",EDGE,"E1818"),sQuery(id+"F0.wireOp",EDGE,"E1819"),sQuery(id+"F0.wireOp",EDGE,"E1820"),sQuery(id+"F0.wireOp",EDGE,"E1821"),sQuery(id+"F0.wireOp",EDGE,"E1822"),sQuery(id+"F0.wireOp",EDGE,"E1823"),sQuery(id+"F0.wireOp",EDGE,"E1824"),sQuery(id+"F0.wireOp",EDGE,"E1825"),sQuery(id+"F0.wireOp",EDGE,"E1826"),sQuery(id+"F0.wireOp",EDGE,"E1827"),sQuery(id+"F0.wireOp",EDGE,"E1828"),sQuery(id+"F0.wireOp",EDGE,"E1829"),sQuery(id+"F0.wireOp",EDGE,"E1830"),sQuery(id+"F0.wireOp",EDGE,"E1831"),sQuery(id+"F0.wireOp",EDGE,"E1832"),sQuery(id+"F0.wireOp",EDGE,"E1833"),sQuery(id+"F0.wireOp",EDGE,"E1834"),sQuery(id+"F0.wireOp",EDGE,"E1835"),sQuery(id+"F0.wireOp",EDGE,"E1836"),sQuery(id+"F0.wireOp",EDGE,"E1837"),sQuery(id+"F0.wireOp",EDGE,"E1838"),sQuery(id+"F0.wireOp",EDGE,"E1839"),sQuery(id+"F0.wireOp",EDGE,"E1840"),sQuery(id+"F0.wireOp",EDGE,"E1841"),sQuery(id+"F0.wireOp",EDGE,"E1842"),sQuery(id+"F0.wireOp",EDGE,"E1843"),sQuery(id+"F0.wireOp",EDGE,"E1844"),sQuery(id+"F0.wireOp",EDGE,"E1845"),sQuery(id+"F0.wireOp",EDGE,"E1846"),sQuery(id+"F0.wireOp",EDGE,"E1847"),sQuery(id+"F0.wireOp",EDGE,"E1848"),sQuery(id+"F0.wireOp",EDGE,"E1849"),sQuery(id+"F0.wireOp",EDGE,"E1850"),sQuery(id+"F0.wireOp",EDGE,"E1851"),sQuery(id+"F0.wireOp",EDGE,"E1852"),sQuery(id+"F0.wireOp",EDGE,"E1853"),sQuery(id+"F0.wireOp",EDGE,"E1854"),sQuery(id+"F0.wireOp",EDGE,"E1855"),sQuery(id+"F0.wireOp",EDGE,"E1856"),sQuery(id+"F0.wireOp",EDGE,"E1857"),sQuery(id+"F0.wireOp",EDGE,"E1858"),sQuery(id+"F0.wireOp",EDGE,"E1859"),sQuery(id+"F0.wireOp",EDGE,"E1860"),sQuery(id+"F0.wireOp",EDGE,"E1861"),sQuery(id+"F0.wireOp",EDGE,"E1862"),sQuery(id+"F0.wireOp",EDGE,"E1863"),sQuery(id+"F0.wireOp",EDGE,"E1864"),sQuery(id+"F0.wireOp",EDGE,"E1865"),sQuery(id+"F0.wireOp",EDGE,"E1866"),sQuery(id+"F0.wireOp",EDGE,"E1867"),sQuery(id+"F0.wireOp",EDGE,"E1868"),sQuery(id+"F0.wireOp",EDGE,"E1869"),sQuery(id+"F0.wireOp",EDGE,"E1870"),sQuery(id+"F0.wireOp",EDGE,"E1871"),sQuery(id+"F0.wireOp",EDGE,"E1872"),sQuery(id+"F0.wireOp",EDGE,"E1873"),sQuery(id+"F0.wireOp",EDGE,"E1874"),sQuery(id+"F0.wireOp",EDGE,"E1875"),sQuery(id+"F0.wireOp",EDGE,"E1876"),sQuery(id+"F0.wireOp",EDGE,"E1877"),sQuery(id+"F0.wireOp",EDGE,"E1878"),sQuery(id+"F0.wireOp",EDGE,"E1879"),sQuery(id+"F0.wireOp",EDGE,"E1880"),sQuery(id+"F0.wireOp",EDGE,"E1881"),sQuery(id+"F0.wireOp",EDGE,"E1882"),sQuery(id+"F0.wireOp",EDGE,"E1883"),sQuery(id+"F0.wireOp",EDGE,"E1884"),sQuery(id+"F0.wireOp",EDGE,"E1885"),sQuery(id+"F0.wireOp",EDGE,"E1886"),sQuery(id+"F0.wireOp",EDGE,"E1887"),sQuery(id+"F0.wireOp",EDGE,"E1888"),sQuery(id+"F0.wireOp",EDGE,"E1889"),sQuery(id+"F0.wireOp",EDGE,"E1890"),sQuery(id+"F0.wireOp",EDGE,"E1891"),sQuery(id+"F0.wireOp",EDGE,"E1892"),sQuery(id+"F0.wireOp",EDGE,"E1893"),sQuery(id+"F0.wireOp",EDGE,"E1894"),sQuery(id+"F0.wireOp",EDGE,"E1895"),sQuery(id+"F0.wireOp",EDGE,"E1896"),sQuery(id+"F0.wireOp",EDGE,"E1897"),sQuery(id+"F0.wireOp",EDGE,"E1898"),sQuery(id+"F0.wireOp",EDGE,"E1899"),sQuery(id+"F0.wireOp",EDGE,"E1900"),sQuery(id+"F0.wireOp",EDGE,"E1901"),sQuery(id+"F0.wireOp",EDGE,"E1902"),sQuery(id+"F0.wireOp",EDGE,"E1903"),sQuery(id+"F0.wireOp",EDGE,"E1904"),sQuery(id+"F0.wireOp",EDGE,"E1905"),sQuery(id+"F0.wireOp",EDGE,"E1906"),sQuery(id+"F0.wireOp",EDGE,"E1907"),sQuery(id+"F0.wireOp",EDGE,"E1908"),sQuery(id+"F0.wireOp",EDGE,"E1909"),sQuery(id+"F0.wireOp",EDGE,"E1910"),sQuery(id+"F0.wireOp",EDGE,"E1911"),sQuery(id+"F0.wireOp",EDGE,"E1912"),sQuery(id+"F0.wireOp",EDGE,"E1913"),sQuery(id+"F0.wireOp",EDGE,"E1914"),sQuery(id+"F0.wireOp",EDGE,"E1915"),sQuery(id+"F0.wireOp",EDGE,"E1916"),sQuery(id+"F0.wireOp",EDGE,"E1917"),sQuery(id+"F0.wireOp",EDGE,"E1918"),sQuery(id+"F0.wireOp",EDGE,"E1919"),sQuery(id+"F0.wireOp",EDGE,"E1920"),sQuery(id+"F0.wireOp",EDGE,"E1921"),sQuery(id+"F0.wireOp",EDGE,"E1922"),sQuery(id+"F0.wireOp",EDGE,"E1923"),sQuery(id+"F0.wireOp",EDGE,"E1924"),sQuery(id+"F0.wireOp",EDGE,"E1925"),sQuery(id+"F0.wireOp",EDGE,"E1926"),sQuery(id+"F0.wireOp",EDGE,"E1927"),sQuery(id+"F0.wireOp",EDGE,"E1928"),sQuery(id+"F0.wireOp",EDGE,"E1929"),sQuery(id+"F0.wireOp",EDGE,"E1930"),sQuery(id+"F0.wireOp",EDGE,"E1931"),sQuery(id+"F0.wireOp",EDGE,"E1932"),sQuery(id+"F0.wireOp",EDGE,"E1933"),sQuery(id+"F0.wireOp",EDGE,"E1934"),sQuery(id+"F0.wireOp",EDGE,"E1935"),sQuery(id+"F0.wireOp",EDGE,"E1936"),sQuery(id+"F0.wireOp",EDGE,"E1937"),sQuery(id+"F0.wireOp",EDGE,"E1938"),sQuery(id+"F0.wireOp",EDGE,"E1939"),sQuery(id+"F0.wireOp",EDGE,"E1940"),sQuery(id+"F0.wireOp",EDGE,"E1941"),sQuery(id+"F0.wireOp",EDGE,"E1942"),sQuery(id+"F0.wireOp",EDGE,"E1943"),sQuery(id+"F0.wireOp",EDGE,"E1944"),sQuery(id+"F0.wireOp",EDGE,"E1945"),sQuery(id+"F0.wireOp",EDGE,"E1946"),sQuery(id+"F0.wireOp",EDGE,"E1947"),sQuery(id+"F0.wireOp",EDGE,"E1948"),sQuery(id+"F0.wireOp",EDGE,"E1949"),sQuery(id+"F0.wireOp",EDGE,"E1950"),sQuery(id+"F0.wireOp",EDGE,"E1951"),sQuery(id+"F0.wireOp",EDGE,"E1952"),sQuery(id+"F0.wireOp",EDGE,"E1953"),sQuery(id+"F0.wireOp",EDGE,"E1954"),sQuery(id+"F0.wireOp",EDGE,"E1955"),sQuery(id+"F0.wireOp",EDGE,"E1956"),sQuery(id+"F0.wireOp",EDGE,"E1957"),sQuery(id+"F0.wireOp",EDGE,"E1958"),sQuery(id+"F0.wireOp",EDGE,"E1959"),sQuery(id+"F0.wireOp",EDGE,"E1960"),sQuery(id+"F0.wireOp",EDGE,"E1961"),sQuery(id+"F0.wireOp",EDGE,"E1962"),sQuery(id+"F0.wireOp",EDGE,"E1963"),sQuery(id+"F0.wireOp",EDGE,"E1964"),sQuery(id+"F0.wireOp",EDGE,"E1965"),sQuery(id+"F0.wireOp",EDGE,"E1966"),sQuery(id+"F0.wireOp",EDGE,"E1967"),sQuery(id+"F0.wireOp",EDGE,"E1968"),sQuery(id+"F0.wireOp",EDGE,"E1969"),sQuery(id+"F0.wireOp",EDGE,"E1970"),sQuery(id+"F0.wireOp",EDGE,"E1971"),sQuery(id+"F0.wireOp",EDGE,"E1972"),sQuery(id+"F0.wireOp",EDGE,"E1973"),sQuery(id+"F0.wireOp",EDGE,"E1974"),sQuery(id+"F0.wireOp",EDGE,"E1975"),sQuery(id+"F0.wireOp",EDGE,"E1976"),sQuery(id+"F0.wireOp",EDGE,"E1977"),sQuery(id+"F0.wireOp",EDGE,"E1978"),sQuery(id+"F0.wireOp",EDGE,"E1979"),sQuery(id+"F0.wireOp",EDGE,"E1980"),sQuery(id+"F0.wireOp",EDGE,"E1981"),sQuery(id+"F0.wireOp",EDGE,"E1982"),sQuery(id+"F0.wireOp",EDGE,"E1983"),sQuery(id+"F0.wireOp",EDGE,"E1984"),sQuery(id+"F0.wireOp",EDGE,"E1985"),sQuery(id+"F0.wireOp",EDGE,"E1986"),sQuery(id+"F0.wireOp",EDGE,"E1987"),sQuery(id+"F0.wireOp",EDGE,"E1988"),sQuery(id+"F0.wireOp",EDGE,"E1989"),sQuery(id+"F0.wireOp",EDGE,"E1990"),sQuery(id+"F0.wireOp",EDGE,"E1991"),sQuery(id+"F0.wireOp",EDGE,"E1992"),sQuery(id+"F0.wireOp",EDGE,"E1993"),sQuery(id+"F0.wireOp",EDGE,"E1994"),sQuery(id+"F0.wireOp",EDGE,"E1995"),sQuery(id+"F0.wireOp",EDGE,"E1996"),sQuery(id+"F0.wireOp",EDGE,"E1997"),sQuery(id+"F0.wireOp",EDGE,"E1998"),sQuery(id+"F0.wireOp",EDGE,"E1999"),sQuery(id+"F0.wireOp",EDGE,"E2000"),sQuery(id+"F0.wireOp",EDGE,"E2001"),sQuery(id+"F0.wireOp",EDGE,"E2002"),sQuery(id+"F0.wireOp",EDGE,"E2003"),sQuery(id+"F0.wireOp",EDGE,"E2004"),sQuery(id+"F0.wireOp",EDGE,"E2005"),sQuery(id+"F0.wireOp",EDGE,"E2006"),sQuery(id+"F0.wireOp",EDGE,"E2007"),sQuery(id+"F0.wireOp",EDGE,"E2008"),sQuery(id+"F0.wireOp",EDGE,"E2009"),sQuery(id+"F0.wireOp",EDGE,"E2010"),sQuery(id+"F0.wireOp",EDGE,"E2011"),sQuery(id+"F0.wireOp",EDGE,"E2012"),sQuery(id+"F0.wireOp",EDGE,"E2013"),sQuery(id+"F0.wireOp",EDGE,"E2014"),sQuery(id+"F0.wireOp",EDGE,"E2015"),sQuery(id+"F0.wireOp",EDGE,"E2016"),sQuery(id+"F0.wireOp",EDGE,"E2017"),sQuery(id+"F0.wireOp",EDGE,"E2018"),sQuery(id+"F0.wireOp",EDGE,"E2019"),sQuery(id+"F0.wireOp",EDGE,"E2020"),sQuery(id+"F0.wireOp",EDGE,"E2021"),sQuery(id+"F0.wireOp",EDGE,"E2022"),sQuery(id+"F0.wireOp",EDGE,"E2023"),sQuery(id+"F0.wireOp",EDGE,"E2024"),sQuery(id+"F0.wireOp",EDGE,"E2025"),sQuery(id+"F0.wireOp",EDGE,"E2026"),sQuery(id+"F0.wireOp",EDGE,"E2027"),sQuery(id+"F0.wireOp",EDGE,"E2028"),sQuery(id+"F0.wireOp",EDGE,"E2029"),sQuery(id+"F0.wireOp",EDGE,"E2030"),sQuery(id+"F0.wireOp",EDGE,"E2031"),sQuery(id+"F0.wireOp",EDGE,"E2032"),sQuery(id+"F0.wireOp",EDGE,"E2033"),sQuery(id+"F0.wireOp",EDGE,"E2034"),sQuery(id+"F0.wireOp",EDGE,"E2035"),sQuery(id+"F0.wireOp",EDGE,"E2036"),sQuery(id+"F0.wireOp",EDGE,"E2037"),sQuery(id+"F0.wireOp",EDGE,"E2038"),sQuery(id+"F0.wireOp",EDGE,"E2039"),sQuery(id+"F0.wireOp",EDGE,"E2040"),sQuery(id+"F0.wireOp",EDGE,"E2041"),sQuery(id+"F0.wireOp",EDGE,"E2042"),sQuery(id+"F0.wireOp",EDGE,"E2043"),sQuery(id+"F0.wireOp",EDGE,"E2044"),sQuery(id+"F0.wireOp",EDGE,"E2045"),sQuery(id+"F0.wireOp",EDGE,"E2046"),sQuery(id+"F0.wireOp",EDGE,"E2047"),sQuery(id+"F0.wireOp",EDGE,"E2048"),sQuery(id+"F0.wireOp",EDGE,"E2049"),sQuery(id+"F0.wireOp",EDGE,"E2050"),sQuery(id+"F0.wireOp",EDGE,"E2051"),sQuery(id+"F0.wireOp",EDGE,"E2052"),sQuery(id+"F0.wireOp",EDGE,"E2053"),sQuery(id+"F0.wireOp",EDGE,"E2054"),sQuery(id+"F0.wireOp",EDGE,"E2055"),sQuery(id+"F0.wireOp",EDGE,"E2056"),sQuery(id+"F0.wireOp",EDGE,"E2057"),sQuery(id+"F0.wireOp",EDGE,"E2058"),sQuery(id+"F0.wireOp",EDGE,"E2059"),sQuery(id+"F0.wireOp",EDGE,"E2060"),sQuery(id+"F0.wireOp",EDGE,"E2061"),sQuery(id+"F0.wireOp",EDGE,"E2062"),sQuery(id+"F0.wireOp",EDGE,"E2063"),sQuery(id+"F0.wireOp",EDGE,"E2064"),sQuery(id+"F0.wireOp",EDGE,"E2065"),sQuery(id+"F0.wireOp",EDGE,"E2066"),sQuery(id+"F0.wireOp",EDGE,"E2067"),sQuery(id+"F0.wireOp",EDGE,"E2068"),sQuery(id+"F0.wireOp",EDGE,"E2069"),sQuery(id+"F0.wireOp",EDGE,"E2070"),sQuery(id+"F0.wireOp",EDGE,"E2071"),sQuery(id+"F0.wireOp",EDGE,"E2072"),sQuery(id+"F0.wireOp",EDGE,"E2073"),sQuery(id+"F0.wireOp",EDGE,"E2074"),sQuery(id+"F0.wireOp",EDGE,"E2075"),sQuery(id+"F0.wireOp",EDGE,"E2076"),sQuery(id+"F0.wireOp",EDGE,"E2077"),sQuery(id+"F0.wireOp",EDGE,"E2078"),sQuery(id+"F0.wireOp",EDGE,"E2079"),sQuery(id+"F0.wireOp",EDGE,"E2080"),sQuery(id+"F0.wireOp",EDGE,"E2081"),sQuery(id+"F0.wireOp",EDGE,"E2082"),sQuery(id+"F0.wireOp",EDGE,"E2083"),sQuery(id+"F0.wireOp",EDGE,"E2084"),sQuery(id+"F0.wireOp",EDGE,"E2085"),sQuery(id+"F0.wireOp",EDGE,"E2086"),sQuery(id+"F0.wireOp",EDGE,"E2087"),sQuery(id+"F0.wireOp",EDGE,"E2088"),sQuery(id+"F0.wireOp",EDGE,"E2089"),sQuery(id+"F0.wireOp",EDGE,"E2090"),sQuery(id+"F0.wireOp",EDGE,"E2091"),sQuery(id+"F0.wireOp",EDGE,"E2092"),sQuery(id+"F0.wireOp",EDGE,"E2093"),sQuery(id+"F0.wireOp",EDGE,"E2094"),sQuery(id+"F0.wireOp",EDGE,"E2095"),sQuery(id+"F0.wireOp",EDGE,"E2096"),sQuery(id+"F0.wireOp",EDGE,"E2097"),sQuery(id+"F0.wireOp",EDGE,"E2098"),sQuery(id+"F0.wireOp",EDGE,"E2099"),sQuery(id+"F0.wireOp",EDGE,"E2100"),sQuery(id+"F0.wireOp",EDGE,"E2101"),sQuery(id+"F0.wireOp",EDGE,"E2102"),sQuery(id+"F0.wireOp",EDGE,"E2103"),sQuery(id+"F0.wireOp",EDGE,"E2104"),sQuery(id+"F0.wireOp",EDGE,"E2105"),sQuery(id+"F0.wireOp",EDGE,"E2106"),sQuery(id+"F0.wireOp",EDGE,"E2107"),sQuery(id+"F0.wireOp",EDGE,"E2108"),sQuery(id+"F0.wireOp",EDGE,"E2109"),sQuery(id+"F0.wireOp",EDGE,"E2110"),sQuery(id+"F0.wireOp",EDGE,"E2111"),sQuery(id+"F0.wireOp",EDGE,"E2112"),sQuery(id+"F0.wireOp",EDGE,"E2113"),sQuery(id+"F0.wireOp",EDGE,"E2114"),sQuery(id+"F0.wireOp",EDGE,"E2115"),sQuery(id+"F0.wireOp",EDGE,"E2116"),sQuery(id+"F0.wireOp",EDGE,"E2117"),sQuery(id+"F0.wireOp",EDGE,"E2118"),sQuery(id+"F0.wireOp",EDGE,"E2119"),sQuery(id+"F0.wireOp",EDGE,"E2120"),sQuery(id+"F0.wireOp",EDGE,"E2121"),sQuery(id+"F0.wireOp",EDGE,"E2122"),sQuery(id+"F0.wireOp",EDGE,"E2123"),sQuery(id+"F0.wireOp",EDGE,"E2124"),sQuery(id+"F0.wireOp",EDGE,"E2125"),sQuery(id+"F0.wireOp",EDGE,"E2126"),sQuery(id+"F0.wireOp",EDGE,"E2127"),sQuery(id+"F0.wireOp",EDGE,"E2128"),sQuery(id+"F0.wireOp",EDGE,"E2129"),sQuery(id+"F0.wireOp",EDGE,"E2130"),sQuery(id+"F0.wireOp",EDGE,"E2131"),sQuery(id+"F0.wireOp",EDGE,"E2132"),sQuery(id+"F0.wireOp",EDGE,"E2133"),sQuery(id+"F0.wireOp",EDGE,"E2134"),sQuery(id+"F0.wireOp",EDGE,"E2135"),sQuery(id+"F0.wireOp",EDGE,"E2136"),sQuery(id+"F0.wireOp",EDGE,"E2137"),sQuery(id+"F0.wireOp",EDGE,"E2138"),sQuery(id+"F0.wireOp",EDGE,"E2139"),sQuery(id+"F0.wireOp",EDGE,"E2140"),sQuery(id+"F0.wireOp",EDGE,"E2141"),sQuery(id+"F0.wireOp",EDGE,"E2142"),sQuery(id+"F0.wireOp",EDGE,"E2143"),sQuery(id+"F0.wireOp",EDGE,"E2144"),sQuery(id+"F0.wireOp",EDGE,"E2145"),sQuery(id+"F0.wireOp",EDGE,"E2146"),sQuery(id+"F0.wireOp",EDGE,"E2147"),sQuery(id+"F0.wireOp",EDGE,"E2148"),sQuery(id+"F0.wireOp",EDGE,"E2149"),sQuery(id+"F0.wireOp",EDGE,"E2150"),sQuery(id+"F0.wireOp",EDGE,"E2151"),sQuery(id+"F0.wireOp",EDGE,"E2152"),sQuery(id+"F0.wireOp",EDGE,"E2153"),sQuery(id+"F0.wireOp",EDGE,"E2154"),sQuery(id+"F0.wireOp",EDGE,"E2155"),sQuery(id+"F0.wireOp",EDGE,"E2156"),sQuery(id+"F0.wireOp",EDGE,"E2157"),sQuery(id+"F0.wireOp",EDGE,"E2158"),sQuery(id+"F0.wireOp",EDGE,"E2159"),sQuery(id+"F0.wireOp",EDGE,"E2160"),sQuery(id+"F0.wireOp",EDGE,"E2161"),sQuery(id+"F0.wireOp",EDGE,"E2162"),sQuery(id+"F0.wireOp",EDGE,"E2163"),sQuery(id+"F0.wireOp",EDGE,"E2164"),sQuery(id+"F0.wireOp",EDGE,"E2165"),sQuery(id+"F0.wireOp",EDGE,"E2166"),sQuery(id+"F0.wireOp",EDGE,"E2167"),sQuery(id+"F0.wireOp",EDGE,"E2168"),sQuery(id+"F0.wireOp",EDGE,"E2169"),sQuery(id+"F0.wireOp",EDGE,"E2170"),sQuery(id+"F0.wireOp",EDGE,"E2171"),sQuery(id+"F0.wireOp",EDGE,"E2172"),sQuery(id+"F0.wireOp",EDGE,"E2173"),sQuery(id+"F0.wireOp",EDGE,"E2174"),sQuery(id+"F0.wireOp",EDGE,"E2175"),sQuery(id+"F0.wireOp",EDGE,"E2176"),sQuery(id+"F0.wireOp",EDGE,"E2177"),sQuery(id+"F0.wireOp",EDGE,"E2178"),sQuery(id+"F0.wireOp",EDGE,"E2179"),sQuery(id+"F0.wireOp",EDGE,"E2180"),sQuery(id+"F0.wireOp",EDGE,"E2181"),sQuery(id+"F0.wireOp",EDGE,"E2182"),sQuery(id+"F0.wireOp",EDGE,"E2183"),sQuery(id+"F0.wireOp",EDGE,"E2184"),sQuery(id+"F0.wireOp",EDGE,"E2185"),sQuery(id+"F0.wireOp",EDGE,"E2186"),sQuery(id+"F0.wireOp",EDGE,"E2187"),sQuery(id+"F0.wireOp",EDGE,"E2188"),sQuery(id+"F0.wireOp",EDGE,"E2189"),sQuery(id+"F0.wireOp",EDGE,"E2190"),sQuery(id+"F0.wireOp",EDGE,"E2191"),sQuery(id+"F0.wireOp",EDGE,"E2192"),sQuery(id+"F0.wireOp",EDGE,"E2193"),sQuery(id+"F0.wireOp",EDGE,"E2194"),sQuery(id+"F0.wireOp",EDGE,"E2195"),sQuery(id+"F0.wireOp",EDGE,"E2196"),sQuery(id+"F0.wireOp",EDGE,"E2197"),sQuery(id+"F0.wireOp",EDGE,"E2198"),sQuery(id+"F0.wireOp",EDGE,"E2199"),sQuery(id+"F0.wireOp",EDGE,"E2200"),sQuery(id+"F0.wireOp",EDGE,"E2201"),sQuery(id+"F0.wireOp",EDGE,"E2202"),sQuery(id+"F0.wireOp",EDGE,"E2203"),sQuery(id+"F0.wireOp",EDGE,"E2204"),sQuery(id+"F0.wireOp",EDGE,"E2205"),sQuery(id+"F0.wireOp",EDGE,"E2206"),sQuery(id+"F0.wireOp",EDGE,"E2207"),sQuery(id+"F0.wireOp",EDGE,"E2208"),sQuery(id+"F0.wireOp",EDGE,"E2209"),sQuery(id+"F0.wireOp",EDGE,"E2210"),sQuery(id+"F0.wireOp",EDGE,"E2211"),sQuery(id+"F0.wireOp",EDGE,"E2212"),sQuery(id+"F0.wireOp",EDGE,"E2213"),sQuery(id+"F0.wireOp",EDGE,"E2214"),sQuery(id+"F0.wireOp",EDGE,"E2215"),sQuery(id+"F0.wireOp",EDGE,"E2216"),sQuery(id+"F0.wireOp",EDGE,"E2217"),sQuery(id+"F0.wireOp",EDGE,"E2218"),sQuery(id+"F0.wireOp",EDGE,"E2219"),sQuery(id+"F0.wireOp",EDGE,"E2220"),sQuery(id+"F0.wireOp",EDGE,"E2221"),sQuery(id+"F0.wireOp",EDGE,"E2222"),sQuery(id+"F0.wireOp",EDGE,"E2223"),sQuery(id+"F0.wireOp",EDGE,"E2224"),sQuery(id+"F0.wireOp",EDGE,"E2225"),sQuery(id+"F0.wireOp",EDGE,"E2226"),sQuery(id+"F0.wireOp",EDGE,"E2227"),sQuery(id+"F0.wireOp",EDGE,"E2228"),sQuery(id+"F0.wireOp",EDGE,"E2229"),sQuery(id+"F0.wireOp",EDGE,"E2230"),sQuery(id+"F0.wireOp",EDGE,"E2231"),sQuery(id+"F0.wireOp",EDGE,"E2232"),sQuery(id+"F0.wireOp",EDGE,"E2233"),sQuery(id+"F0.wireOp",EDGE,"E2234"),sQuery(id+"F0.wireOp",EDGE,"E2235"),sQuery(id+"F0.wireOp",EDGE,"E2236"),sQuery(id+"F0.wireOp",EDGE,"E2237"),sQuery(id+"F0.wireOp",EDGE,"E2238"),sQuery(id+"F0.wireOp",EDGE,"E2239"),sQuery(id+"F0.wireOp",EDGE,"E2240"),sQuery(id+"F0.wireOp",EDGE,"E2241"),sQuery(id+"F0.wireOp",EDGE,"E2242"),sQuery(id+"F0.wireOp",EDGE,"E2243"),sQuery(id+"F0.wireOp",EDGE,"E2244"),sQuery(id+"F0.wireOp",EDGE,"E2245"),sQuery(id+"F0.wireOp",EDGE,"E2246"),sQuery(id+"F0.wireOp",EDGE,"E2247"),sQuery(id+"F0.wireOp",EDGE,"E2248"),sQuery(id+"F0.wireOp",EDGE,"E2249"),sQuery(id+"F0.wireOp",EDGE,"E2250"),sQuery(id+"F0.wireOp",EDGE,"E2251"),sQuery(id+"F0.wireOp",EDGE,"E2252"),sQuery(id+"F0.wireOp",EDGE,"E2253"),sQuery(id+"F0.wireOp",EDGE,"E2254"),sQuery(id+"F0.wireOp",EDGE,"E2255"),sQuery(id+"F0.wireOp",EDGE,"E2256"),sQuery(id+"F0.wireOp",EDGE,"E2257"),sQuery(id+"F0.wireOp",EDGE,"E2258"),sQuery(id+"F0.wireOp",EDGE,"E2259"),sQuery(id+"F0.wireOp",EDGE,"E2260"),sQuery(id+"F0.wireOp",EDGE,"E2261"),sQuery(id+"F0.wireOp",EDGE,"E2262"),sQuery(id+"F0.wireOp",EDGE,"E2263"),sQuery(id+"F0.wireOp",EDGE,"E2264"),sQuery(id+"F0.wireOp",EDGE,"E2265"),sQuery(id+"F0.wireOp",EDGE,"E2266"),sQuery(id+"F0.wireOp",EDGE,"E2267"),sQuery(id+"F0.wireOp",EDGE,"E2268"),sQuery(id+"F0.wireOp",EDGE,"E2269"),sQuery(id+"F0.wireOp",EDGE,"E2270"),sQuery(id+"F0.wireOp",EDGE,"E2271"),sQuery(id+"F0.wireOp",EDGE,"E2272"),sQuery(id+"F0.wireOp",EDGE,"E2273"),sQuery(id+"F0.wireOp",EDGE,"E2274"),sQuery(id+"F0.wireOp",EDGE,"E2275"),sQuery(id+"F0.wireOp",EDGE,"E2276"),sQuery(id+"F0.wireOp",EDGE,"E2277"),sQuery(id+"F0.wireOp",EDGE,"E2278"),sQuery(id+"F0.wireOp",EDGE,"E2279"),sQuery(id+"F0.wireOp",EDGE,"E2280"),sQuery(id+"F0.wireOp",EDGE,"E2281"),sQuery(id+"F0.wireOp",EDGE,"E2282"),sQuery(id+"F0.wireOp",EDGE,"E2283"),sQuery(id+"F0.wireOp",EDGE,"E2284"),sQuery(id+"F0.wireOp",EDGE,"E2285"),sQuery(id+"F0.wireOp",EDGE,"E2286"),sQuery(id+"F0.wireOp",EDGE,"E2287"),sQuery(id+"F0.wireOp",EDGE,"E2288"),sQuery(id+"F0.wireOp",EDGE,"E2289"),sQuery(id+"F0.wireOp",EDGE,"E2290"),sQuery(id+"F0.wireOp",EDGE,"E2291"),sQuery(id+"F0.wireOp",EDGE,"E2292"),sQuery(id+"F0.wireOp",EDGE,"E2293"),sQuery(id+"F0.wireOp",EDGE,"E2294"),sQuery(id+"F0.wireOp",EDGE,"E2295"),sQuery(id+"F0.wireOp",EDGE,"E2296"),sQuery(id+"F0.wireOp",EDGE,"E2297"),sQuery(id+"F0.wireOp",EDGE,"E2298"),sQuery(id+"F0.wireOp",EDGE,"E2299"),sQuery(id+"F0.wireOp",EDGE,"E2300"),sQuery(id+"F0.wireOp",EDGE,"E2301"),sQuery(id+"F0.wireOp",EDGE,"E2302"),sQuery(id+"F0.wireOp",EDGE,"E2303"),sQuery(id+"F0.wireOp",EDGE,"E2304"),sQuery(id+"F0.wireOp",EDGE,"E2305"),sQuery(id+"F0.wireOp",EDGE,"E2306"),sQuery(id+"F0.wireOp",EDGE,"E2307"),sQuery(id+"F0.wireOp",EDGE,"E2308"),sQuery(id+"F0.wireOp",EDGE,"E2309"),sQuery(id+"F0.wireOp",EDGE,"E2310"),sQuery(id+"F0.wireOp",EDGE,"E2311"),sQuery(id+"F0.wireOp",EDGE,"E2312"),sQuery(id+"F0.wireOp",EDGE,"E2313"),sQuery(id+"F0.wireOp",EDGE,"E2314"),sQuery(id+"F0.wireOp",EDGE,"E2315"),sQuery(id+"F0.wireOp",EDGE,"E2316"),sQuery(id+"F0.wireOp",EDGE,"E2317"),sQuery(id+"F0.wireOp",EDGE,"E2318"),sQuery(id+"F0.wireOp",EDGE,"E2319"),sQuery(id+"F0.wireOp",EDGE,"E2320"),sQuery(id+"F0.wireOp",EDGE,"E2321"),sQuery(id+"F0.wireOp",EDGE,"E2322"),sQuery(id+"F0.wireOp",EDGE,"E2323"),sQuery(id+"F0.wireOp",EDGE,"E2324"),sQuery(id+"F0.wireOp",EDGE,"E2325"),sQuery(id+"F0.wireOp",EDGE,"E2326"),sQuery(id+"F0.wireOp",EDGE,"E2327"),sQuery(id+"F0.wireOp",EDGE,"E2328"),sQuery(id+"F0.wireOp",EDGE,"E2329"),sQuery(id+"F0.wireOp",EDGE,"E2330"),sQuery(id+"F0.wireOp",EDGE,"E2331"),sQuery(id+"F0.wireOp",EDGE,"E2332"),sQuery(id+"F0.wireOp",EDGE,"E2333"),sQuery(id+"F0.wireOp",EDGE,"E2334"),sQuery(id+"F0.wireOp",EDGE,"E2335"),sQuery(id+"F0.wireOp",EDGE,"E2336"),sQuery(id+"F0.wireOp",EDGE,"E2337"),sQuery(id+"F0.wireOp",EDGE,"E2338"),sQuery(id+"F0.wireOp",EDGE,"E2339"),sQuery(id+"F0.wireOp",EDGE,"E2340"),sQuery(id+"F0.wireOp",EDGE,"E2341"),sQuery(id+"F0.wireOp",EDGE,"E2342"),sQuery(id+"F0.wireOp",EDGE,"E2343"),sQuery(id+"F0.wireOp",EDGE,"E2344"),sQuery(id+"F0.wireOp",EDGE,"E2345"),sQuery(id+"F0.wireOp",EDGE,"E2346"),sQuery(id+"F0.wireOp",EDGE,"E2347"),sQuery(id+"F0.wireOp",EDGE,"E2348"),sQuery(id+"F0.wireOp",EDGE,"E2349"),sQuery(id+"F0.wireOp",EDGE,"E2350"),sQuery(id+"F0.wireOp",EDGE,"E2351"),sQuery(id+"F0.wireOp",EDGE,"E2352"),sQuery(id+"F0.wireOp",EDGE,"E2353"),sQuery(id+"F0.wireOp",EDGE,"E2354"),sQuery(id+"F0.wireOp",EDGE,"E2355"),sQuery(id+"F0.wireOp",EDGE,"E2356"),sQuery(id+"F0.wireOp",EDGE,"E2357"),sQuery(id+"F0.wireOp",EDGE,"E2358"),sQuery(id+"F0.wireOp",EDGE,"E2359"),sQuery(id+"F0.wireOp",EDGE,"E2360"),sQuery(id+"F0.wireOp",EDGE,"E2361"),sQuery(id+"F0.wireOp",EDGE,"E2362"),sQuery(id+"F0.wireOp",EDGE,"E2363"),sQuery(id+"F0.wireOp",EDGE,"E2364"),sQuery(id+"F0.wireOp",EDGE,"E2365"),sQuery(id+"F0.wireOp",EDGE,"E2366"),sQuery(id+"F0.wireOp",EDGE,"E2367"),sQuery(id+"F0.wireOp",EDGE,"E2368"),sQuery(id+"F0.wireOp",EDGE,"E2369"),sQuery(id+"F0.wireOp",EDGE,"E2370")])],"isStart":false});
            var sketch = newSketch(context, id + "F2", { "sketchPlane" : qUnion([Q0])});
            skCircle(sketch, "E2371.cCircle", {"center": v(0, 0) * mm, "radius": 5.25 * mm, "construction": true});
            skLineSegment(sketch, "E2371.0", {"start": v(5.25, 3.03) * mm, "end": v(5.25, -3.03) * mm});
            skLineSegment(sketch, "E2371.1", {"start": v(5.25, -3.03) * mm, "end": v(0, -6.06) * mm});
            skLineSegment(sketch, "E2371.2", {"start": v(0, -6.06) * mm, "end": v(-5.25, -3.03) * mm});
            skLineSegment(sketch, "E2371.3", {"start": v(-5.25, -3.03) * mm, "end": v(-5.25, 3.03) * mm});
            skLineSegment(sketch, "E2371.4", {"start": v(-5.25, 3.03) * mm, "end": v(0, 6.06) * mm});
            skLineSegment(sketch, "E2371.5", {"start": v(0, 6.06) * mm, "end": v(5.25, 3.03) * mm});
            skPoint(sketch, "E2371.0.midPoint", {"position": v(5.25, 0) * mm});
            skSolve(sketch);
        }
        {
            var Q0;
            Q0=makeQuery(id+"F2.imprint","IMPRINT",FACE,{"disambiguationData":[TD([[makeQuery(id+"F2.imprint","IMPRINT",EDGE,{"derivedFrom":sQuery(id+"F2.wireOp",EDGE,"E2371.0")}),1.0]])]});
            extrude(context, id + "F3", {"entities" : qUnion([Q0]), "operationType" : NewBodyOperationType.ADD, "depth" : 5 * mm});
        }
    });
